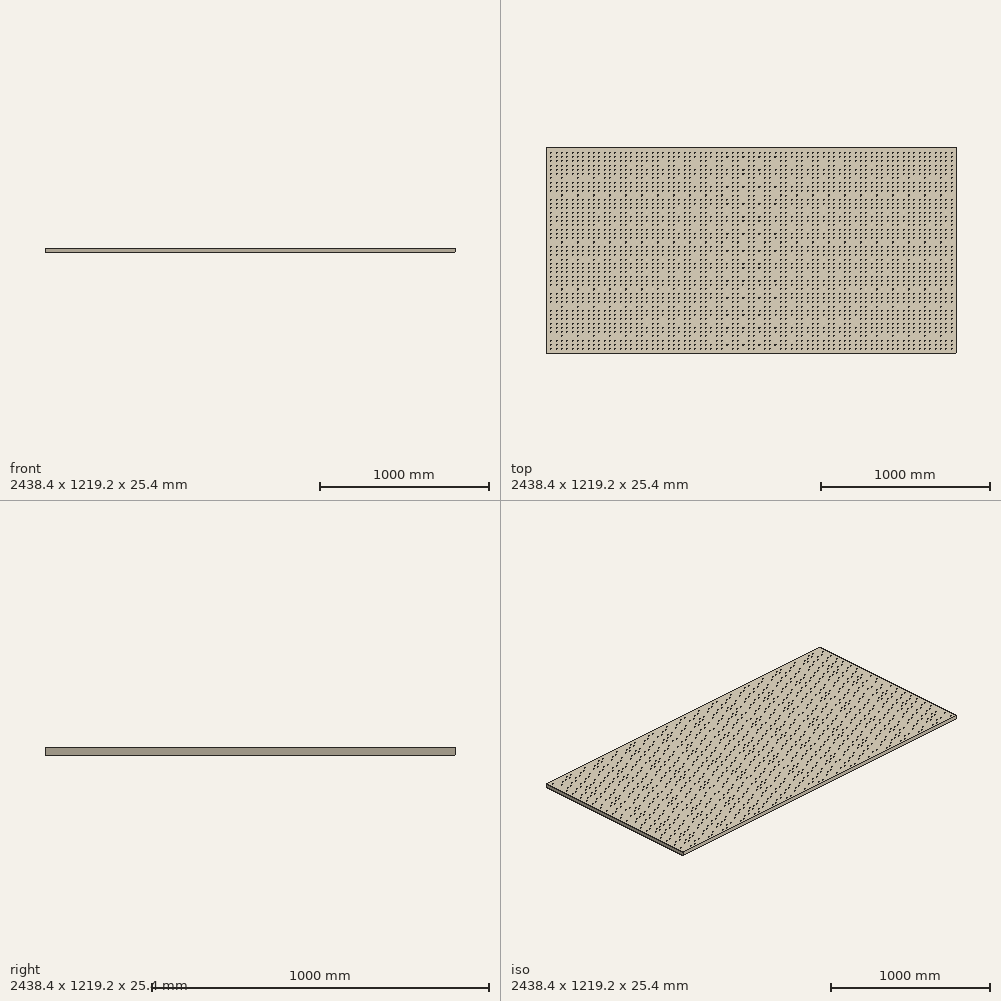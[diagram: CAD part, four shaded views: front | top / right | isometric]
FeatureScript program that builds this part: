
annotation { "Feature Type Name" : "Feature", "Feature Type Description" : "" }
export const myFeature = defineFeature(function(context is Context, id is Id, definition is map)
    precondition{}
    {
        {
            var Q0;
            Q0=qCreatedBy(makeId("Top.planeOp"),FACE);
            var sketch = newSketch(context, id + "F0", { "sketchPlane" : qUnion([Q0])});
            skLineSegment(sketch, "E0.bottom", {"start": v(-70.34, 15.58) * mm, "end": v(2368.06, 15.58) * mm});
            skLineSegment(sketch, "E0.top", {"start": v(-70.34, -1203.62) * mm, "end": v(2368.06, -1203.62) * mm});
            skLineSegment(sketch, "E0.left", {"start": v(-70.34, 15.58) * mm, "end": v(-70.34, -1203.62) * mm});
            skLineSegment(sketch, "E0.right", {"start": v(2368.06, 15.58) * mm, "end": v(2368.06, -1203.62) * mm});
            skCircle(sketch, "E1", {"center": v(-41.76, -13) * mm, "radius": 3.18 * mm});
            skCircle(sketch, "E2.1.0.0", {"center": v(-10.01, -13) * mm, "radius": 3.18 * mm});
            skCircle(sketch, "E2.2.0.0", {"center": v(21.74, -13) * mm, "radius": 3.18 * mm});
            skLineSegment(sketch, "E2.direction1", {"start": v(-41.76, -13) * mm, "end": v(-10.01, -13) * mm, "construction": true});
            skCircle(sketch, "E3.0.3.0", {"center": v(53.49, -13) * mm, "radius": 3.18 * mm});
            skCircle(sketch, "E3.0.4.0", {"center": v(85.24, -13) * mm, "radius": 3.18 * mm});
            skCircle(sketch, "E3.0.5.0", {"center": v(116.99, -13) * mm, "radius": 3.18 * mm});
            skCircle(sketch, "E3.0.6.0", {"center": v(148.74, -13) * mm, "radius": 3.18 * mm});
            skCircle(sketch, "E3.0.7.0", {"center": v(180.49, -13) * mm, "radius": 3.18 * mm});
            skCircle(sketch, "E3.0.8.0", {"center": v(212.24, -13) * mm, "radius": 3.18 * mm});
            skCircle(sketch, "E3.0.9.0", {"center": v(243.99, -13) * mm, "radius": 3.18 * mm});
            skCircle(sketch, "E3.0.10.0", {"center": v(275.74, -13) * mm, "radius": 3.18 * mm});
            skCircle(sketch, "E3.0.11.0", {"center": v(307.49, -13) * mm, "radius": 3.18 * mm});
            skCircle(sketch, "E4.0.12.0", {"center": v(339.24, -13) * mm, "radius": 3.18 * mm});
            skCircle(sketch, "E4.0.13.0", {"center": v(370.99, -13) * mm, "radius": 3.18 * mm});
            skCircle(sketch, "E4.0.14.0", {"center": v(402.74, -13) * mm, "radius": 3.18 * mm});
            skCircle(sketch, "E4.0.15.0", {"center": v(434.49, -13) * mm, "radius": 3.18 * mm});
            skCircle(sketch, "E4.0.16.0", {"center": v(466.24, -13) * mm, "radius": 3.18 * mm});
            skCircle(sketch, "E4.0.17.0", {"center": v(497.99, -13) * mm, "radius": 3.18 * mm});
            skCircle(sketch, "E4.0.18.0", {"center": v(529.74, -13) * mm, "radius": 3.18 * mm});
            skCircle(sketch, "E4.0.19.0", {"center": v(561.49, -13) * mm, "radius": 3.18 * mm});
            skCircle(sketch, "E4.0.20.0", {"center": v(593.24, -13) * mm, "radius": 3.18 * mm});
            skCircle(sketch, "E4.0.21.0", {"center": v(624.99, -13) * mm, "radius": 3.18 * mm});
            skCircle(sketch, "E4.0.22.0", {"center": v(656.74, -13) * mm, "radius": 3.18 * mm});
            skCircle(sketch, "E4.0.23.0", {"center": v(688.49, -13) * mm, "radius": 3.18 * mm});
            skCircle(sketch, "E4.0.24.0", {"center": v(720.24, -13) * mm, "radius": 3.18 * mm});
            skCircle(sketch, "E4.0.25.0", {"center": v(751.99, -13) * mm, "radius": 3.18 * mm});
            skCircle(sketch, "E4.0.26.0", {"center": v(783.74, -13) * mm, "radius": 3.18 * mm});
            skCircle(sketch, "E4.0.27.0", {"center": v(815.49, -13) * mm, "radius": 3.18 * mm});
            skCircle(sketch, "E4.0.28.0", {"center": v(847.24, -13) * mm, "radius": 3.18 * mm});
            skCircle(sketch, "E4.0.29.0", {"center": v(878.99, -13) * mm, "radius": 3.18 * mm});
            skCircle(sketch, "E4.0.30.0", {"center": v(910.74, -13) * mm, "radius": 3.18 * mm});
            skCircle(sketch, "E4.0.31.0", {"center": v(942.49, -13) * mm, "radius": 3.18 * mm});
            skCircle(sketch, "E4.0.32.0", {"center": v(974.24, -13) * mm, "radius": 3.18 * mm});
            skCircle(sketch, "E4.0.33.0", {"center": v(1005.99, -13) * mm, "radius": 3.18 * mm});
            skCircle(sketch, "E4.0.34.0", {"center": v(1037.74, -13) * mm, "radius": 3.18 * mm});
            skCircle(sketch, "E4.0.35.0", {"center": v(1069.49, -13) * mm, "radius": 3.18 * mm});
            skCircle(sketch, "E4.0.36.0", {"center": v(1101.24, -13) * mm, "radius": 3.18 * mm});
            skCircle(sketch, "E4.0.37.0", {"center": v(1132.99, -13) * mm, "radius": 3.18 * mm});
            skCircle(sketch, "E4.0.38.0", {"center": v(1164.74, -13) * mm, "radius": 3.18 * mm});
            skCircle(sketch, "E4.0.39.0", {"center": v(1196.49, -13) * mm, "radius": 3.18 * mm});
            skCircle(sketch, "E4.0.40.0", {"center": v(1228.24, -13) * mm, "radius": 3.18 * mm});
            skCircle(sketch, "E4.0.41.0", {"center": v(1259.99, -13) * mm, "radius": 3.18 * mm});
            skCircle(sketch, "E4.0.42.0", {"center": v(1291.74, -13) * mm, "radius": 3.18 * mm});
            skCircle(sketch, "E4.0.43.0", {"center": v(1323.49, -13) * mm, "radius": 3.18 * mm});
            skCircle(sketch, "E4.0.44.0", {"center": v(1355.24, -13) * mm, "radius": 3.18 * mm});
            skCircle(sketch, "E4.0.45.0", {"center": v(1386.99, -13) * mm, "radius": 3.18 * mm});
            skCircle(sketch, "E4.0.46.0", {"center": v(1418.74, -13) * mm, "radius": 3.18 * mm});
            skCircle(sketch, "E4.0.47.0", {"center": v(1450.49, -13) * mm, "radius": 3.18 * mm});
            skCircle(sketch, "E4.0.48.0", {"center": v(1482.24, -13) * mm, "radius": 3.18 * mm});
            skCircle(sketch, "E4.0.49.0", {"center": v(1513.99, -13) * mm, "radius": 3.18 * mm});
            skCircle(sketch, "E4.0.50.0", {"center": v(1545.74, -13) * mm, "radius": 3.18 * mm});
            skCircle(sketch, "E4.0.51.0", {"center": v(1577.49, -13) * mm, "radius": 3.18 * mm});
            skCircle(sketch, "E4.0.52.0", {"center": v(1609.24, -13) * mm, "radius": 3.18 * mm});
            skCircle(sketch, "E4.0.53.0", {"center": v(1640.99, -13) * mm, "radius": 3.18 * mm});
            skCircle(sketch, "E4.0.54.0", {"center": v(1672.74, -13) * mm, "radius": 3.18 * mm});
            skCircle(sketch, "E4.0.55.0", {"center": v(1704.49, -13) * mm, "radius": 3.18 * mm});
            skCircle(sketch, "E4.0.56.0", {"center": v(1736.24, -13) * mm, "radius": 3.18 * mm});
            skCircle(sketch, "E4.0.57.0", {"center": v(1767.99, -13) * mm, "radius": 3.18 * mm});
            skCircle(sketch, "E4.0.58.0", {"center": v(1799.74, -13) * mm, "radius": 3.18 * mm});
            skCircle(sketch, "E4.0.59.0", {"center": v(1831.49, -13) * mm, "radius": 3.18 * mm});
            skCircle(sketch, "E4.0.60.0", {"center": v(1863.24, -13) * mm, "radius": 3.18 * mm});
            skCircle(sketch, "E4.0.61.0", {"center": v(1894.99, -13) * mm, "radius": 3.18 * mm});
            skCircle(sketch, "E4.0.62.0", {"center": v(1926.74, -13) * mm, "radius": 3.18 * mm});
            skCircle(sketch, "E4.0.63.0", {"center": v(1958.49, -13) * mm, "radius": 3.18 * mm});
            skCircle(sketch, "E4.0.64.0", {"center": v(1990.24, -13) * mm, "radius": 3.18 * mm});
            skCircle(sketch, "E4.0.65.0", {"center": v(2021.99, -13) * mm, "radius": 3.18 * mm});
            skCircle(sketch, "E4.0.66.0", {"center": v(2053.74, -13) * mm, "radius": 3.18 * mm});
            skCircle(sketch, "E4.0.67.0", {"center": v(2085.49, -13) * mm, "radius": 3.18 * mm});
            skCircle(sketch, "E4.0.68.0", {"center": v(2117.24, -13) * mm, "radius": 3.18 * mm});
            skCircle(sketch, "E4.0.69.0", {"center": v(2148.99, -13) * mm, "radius": 3.18 * mm});
            skCircle(sketch, "E4.0.70.0", {"center": v(2180.74, -13) * mm, "radius": 3.18 * mm});
            skCircle(sketch, "E4.0.71.0", {"center": v(2212.49, -13) * mm, "radius": 3.18 * mm});
            skCircle(sketch, "E4.0.72.0", {"center": v(2244.24, -13) * mm, "radius": 3.18 * mm});
            skCircle(sketch, "E4.0.73.0", {"center": v(2275.99, -13) * mm, "radius": 3.18 * mm});
            skCircle(sketch, "E4.0.74.0", {"center": v(2307.74, -13) * mm, "radius": 3.18 * mm});
            skCircle(sketch, "E4.0.75.0", {"center": v(2339.49, -13) * mm, "radius": 3.18 * mm});
            skCircle(sketch, "E5.0.1.0", {"center": v(2244.24, -38.4) * mm, "radius": 3.18 * mm});
            skCircle(sketch, "E5.0.1.1", {"center": v(2180.74, -38.4) * mm, "radius": 3.18 * mm});
            skCircle(sketch, "E5.0.1.2", {"center": v(2339.49, -38.4) * mm, "radius": 3.18 * mm});
            skCircle(sketch, "E5.0.1.3", {"center": v(2307.74, -38.4) * mm, "radius": 3.18 * mm});
            skCircle(sketch, "E5.0.1.4", {"center": v(2275.99, -38.4) * mm, "radius": 3.18 * mm});
            skCircle(sketch, "E5.0.1.5", {"center": v(2212.49, -38.4) * mm, "radius": 3.18 * mm});
            skCircle(sketch, "E5.0.1.6", {"center": v(1958.49, -38.4) * mm, "radius": 3.18 * mm});
            skCircle(sketch, "E5.0.1.7", {"center": v(1894.99, -38.4) * mm, "radius": 3.18 * mm});
            skCircle(sketch, "E5.0.1.8", {"center": v(2117.24, -38.4) * mm, "radius": 3.18 * mm});
            skCircle(sketch, "E5.0.1.9", {"center": v(2085.49, -38.4) * mm, "radius": 3.18 * mm});
            skCircle(sketch, "E5.0.1.10", {"center": v(2053.74, -38.4) * mm, "radius": 3.18 * mm});
            skCircle(sketch, "E5.0.1.11", {"center": v(1926.74, -38.4) * mm, "radius": 3.18 * mm});
            skCircle(sketch, "E5.0.1.12", {"center": v(2021.99, -38.4) * mm, "radius": 3.18 * mm});
            skCircle(sketch, "E5.0.1.13", {"center": v(2148.99, -38.4) * mm, "radius": 3.18 * mm});
            skCircle(sketch, "E5.0.1.14", {"center": v(1990.24, -38.4) * mm, "radius": 3.18 * mm});
            skCircle(sketch, "E5.0.1.15", {"center": v(1450.49, -38.4) * mm, "radius": 3.18 * mm});
            skCircle(sketch, "E5.0.1.16", {"center": v(1228.24, -38.4) * mm, "radius": 3.18 * mm});
            skCircle(sketch, "E5.0.1.17", {"center": v(1736.24, -38.4) * mm, "radius": 3.18 * mm});
            skCircle(sketch, "E5.0.1.18", {"center": v(1386.99, -38.4) * mm, "radius": 3.18 * mm});
            skCircle(sketch, "E5.0.1.19", {"center": v(1164.74, -38.4) * mm, "radius": 3.18 * mm});
            skCircle(sketch, "E5.0.1.20", {"center": v(1672.74, -38.4) * mm, "radius": 3.18 * mm});
            skCircle(sketch, "E5.0.1.21", {"center": v(1101.24, -38.4) * mm, "radius": 3.18 * mm});
            skCircle(sketch, "E5.0.1.22", {"center": v(1609.24, -38.4) * mm, "radius": 3.18 * mm});
            skCircle(sketch, "E5.0.1.23", {"center": v(1355.24, -38.4) * mm, "radius": 3.18 * mm});
            skCircle(sketch, "E5.0.1.24", {"center": v(1863.24, -38.4) * mm, "radius": 3.18 * mm});
            skCircle(sketch, "E5.0.1.25", {"center": v(1069.49, -38.4) * mm, "radius": 3.18 * mm});
            skCircle(sketch, "E5.0.1.26", {"center": v(1577.49, -38.4) * mm, "radius": 3.18 * mm});
            skCircle(sketch, "E5.0.1.27", {"center": v(1323.49, -38.4) * mm, "radius": 3.18 * mm});
            skCircle(sketch, "E5.0.1.28", {"center": v(1831.49, -38.4) * mm, "radius": 3.18 * mm});
            skCircle(sketch, "E5.0.1.29", {"center": v(1037.74, -38.4) * mm, "radius": 3.18 * mm});
            skCircle(sketch, "E5.0.1.30", {"center": v(1545.74, -38.4) * mm, "radius": 3.18 * mm});
            skCircle(sketch, "E5.0.1.31", {"center": v(1418.74, -38.4) * mm, "radius": 3.18 * mm});
            skCircle(sketch, "E5.0.1.32", {"center": v(1005.99, -38.4) * mm, "radius": 3.18 * mm});
            skCircle(sketch, "E5.0.1.33", {"center": v(1513.99, -38.4) * mm, "radius": 3.18 * mm});
            skCircle(sketch, "E5.0.1.34", {"center": v(1799.74, -38.4) * mm, "radius": 3.18 * mm});
            skCircle(sketch, "E5.0.1.35", {"center": v(1291.74, -38.4) * mm, "radius": 3.18 * mm});
            skCircle(sketch, "E5.0.1.36", {"center": v(1132.99, -38.4) * mm, "radius": 3.18 * mm});
            skCircle(sketch, "E5.0.1.37", {"center": v(974.24, -38.4) * mm, "radius": 3.18 * mm});
            skCircle(sketch, "E5.0.1.38", {"center": v(1482.24, -38.4) * mm, "radius": 3.18 * mm});
            skCircle(sketch, "E5.0.1.39", {"center": v(1259.99, -38.4) * mm, "radius": 3.18 * mm});
            skCircle(sketch, "E5.0.1.40", {"center": v(1640.99, -38.4) * mm, "radius": 3.18 * mm});
            skCircle(sketch, "E5.0.1.41", {"center": v(1767.99, -38.4) * mm, "radius": 3.18 * mm});
            skCircle(sketch, "E5.0.1.42", {"center": v(1196.49, -38.4) * mm, "radius": 3.18 * mm});
            skCircle(sketch, "E5.0.1.43", {"center": v(1704.49, -38.4) * mm, "radius": 3.18 * mm});
            skCircle(sketch, "E5.0.1.44", {"center": v(720.24, -38.4) * mm, "radius": 3.18 * mm});
            skCircle(sketch, "E5.0.1.45", {"center": v(942.49, -38.4) * mm, "radius": 3.18 * mm});
            skCircle(sketch, "E5.0.1.46", {"center": v(878.99, -38.4) * mm, "radius": 3.18 * mm});
            skCircle(sketch, "E5.0.1.47", {"center": v(434.49, -38.4) * mm, "radius": 3.18 * mm});
            skCircle(sketch, "E5.0.1.48", {"center": v(656.74, -38.4) * mm, "radius": 3.18 * mm});
            skCircle(sketch, "E5.0.1.49", {"center": v(370.99, -38.4) * mm, "radius": 3.18 * mm});
            skCircle(sketch, "E5.0.1.50", {"center": v(593.24, -38.4) * mm, "radius": 3.18 * mm});
            skCircle(sketch, "E5.0.1.51", {"center": v(847.24, -38.4) * mm, "radius": 3.18 * mm});
            skCircle(sketch, "E5.0.1.52", {"center": v(339.24, -38.4) * mm, "radius": 3.18 * mm});
            skCircle(sketch, "E5.0.1.53", {"center": v(561.49, -38.4) * mm, "radius": 3.18 * mm});
            skCircle(sketch, "E5.0.1.54", {"center": v(815.49, -38.4) * mm, "radius": 3.18 * mm});
            skCircle(sketch, "E5.0.1.55", {"center": v(307.49, -38.4) * mm, "radius": 3.18 * mm});
            skCircle(sketch, "E5.0.1.56", {"center": v(529.74, -38.4) * mm, "radius": 3.18 * mm});
            skCircle(sketch, "E5.0.1.57", {"center": v(180.49, -38.4) * mm, "radius": 3.18 * mm});
            skCircle(sketch, "E5.0.1.58", {"center": v(148.74, -38.4) * mm, "radius": 3.18 * mm});
            skCircle(sketch, "E5.0.1.59", {"center": v(910.74, -38.4) * mm, "radius": 3.18 * mm});
            skCircle(sketch, "E5.0.1.60", {"center": v(275.74, -38.4) * mm, "radius": 3.18 * mm});
            skCircle(sketch, "E5.0.1.61", {"center": v(243.99, -38.4) * mm, "radius": 3.18 * mm});
            skCircle(sketch, "E5.0.1.62", {"center": v(212.24, -38.4) * mm, "radius": 3.18 * mm});
            skCircle(sketch, "E5.0.1.63", {"center": v(783.74, -38.4) * mm, "radius": 3.18 * mm});
            skCircle(sketch, "E5.0.1.64", {"center": v(497.99, -38.4) * mm, "radius": 3.18 * mm});
            skCircle(sketch, "E5.0.1.65", {"center": v(402.74, -38.4) * mm, "radius": 3.18 * mm});
            skCircle(sketch, "E5.0.1.66", {"center": v(624.99, -38.4) * mm, "radius": 3.18 * mm});
            skCircle(sketch, "E5.0.1.67", {"center": v(751.99, -38.4) * mm, "radius": 3.18 * mm});
            skCircle(sketch, "E5.0.1.68", {"center": v(466.24, -38.4) * mm, "radius": 3.18 * mm});
            skCircle(sketch, "E5.0.1.69", {"center": v(688.49, -38.4) * mm, "radius": 3.18 * mm});
            skCircle(sketch, "E5.0.1.70", {"center": v(116.99, -38.4) * mm, "radius": 3.18 * mm});
            skCircle(sketch, "E5.0.1.71", {"center": v(85.24, -38.4) * mm, "radius": 3.18 * mm});
            skCircle(sketch, "E5.0.1.72", {"center": v(53.49, -38.4) * mm, "radius": 3.18 * mm});
            skLineSegment(sketch, "E5.0.1.73", {"start": v(-41.76, -38.4) * mm, "end": v(-10.01, -38.4) * mm, "construction": true});
            skCircle(sketch, "E5.0.1.74", {"center": v(21.74, -38.4) * mm, "radius": 3.18 * mm});
            skCircle(sketch, "E5.0.1.75", {"center": v(-10.01, -38.4) * mm, "radius": 3.18 * mm});
            skCircle(sketch, "E5.0.1.76", {"center": v(-41.76, -38.4) * mm, "radius": 3.18 * mm});
            skCircle(sketch, "E5.0.2.0", {"center": v(2244.24, -63.8) * mm, "radius": 3.18 * mm});
            skCircle(sketch, "E5.0.2.1", {"center": v(2180.74, -63.8) * mm, "radius": 3.18 * mm});
            skCircle(sketch, "E5.0.2.2", {"center": v(2339.49, -63.8) * mm, "radius": 3.18 * mm});
            skCircle(sketch, "E5.0.2.3", {"center": v(2307.74, -63.8) * mm, "radius": 3.18 * mm});
            skCircle(sketch, "E5.0.2.4", {"center": v(2275.99, -63.8) * mm, "radius": 3.18 * mm});
            skCircle(sketch, "E5.0.2.5", {"center": v(2212.49, -63.8) * mm, "radius": 3.18 * mm});
            skCircle(sketch, "E5.0.2.6", {"center": v(1958.49, -63.8) * mm, "radius": 3.18 * mm});
            skCircle(sketch, "E5.0.2.7", {"center": v(1894.99, -63.8) * mm, "radius": 3.18 * mm});
            skCircle(sketch, "E5.0.2.8", {"center": v(2117.24, -63.8) * mm, "radius": 3.18 * mm});
            skCircle(sketch, "E5.0.2.9", {"center": v(2085.49, -63.8) * mm, "radius": 3.18 * mm});
            skCircle(sketch, "E5.0.2.10", {"center": v(2053.74, -63.8) * mm, "radius": 3.18 * mm});
            skCircle(sketch, "E5.0.2.11", {"center": v(1926.74, -63.8) * mm, "radius": 3.18 * mm});
            skCircle(sketch, "E5.0.2.12", {"center": v(2021.99, -63.8) * mm, "radius": 3.18 * mm});
            skCircle(sketch, "E5.0.2.13", {"center": v(2148.99, -63.8) * mm, "radius": 3.18 * mm});
            skCircle(sketch, "E5.0.2.14", {"center": v(1990.24, -63.8) * mm, "radius": 3.18 * mm});
            skCircle(sketch, "E5.0.2.15", {"center": v(1450.49, -63.8) * mm, "radius": 3.18 * mm});
            skCircle(sketch, "E5.0.2.16", {"center": v(1228.24, -63.8) * mm, "radius": 3.18 * mm});
            skCircle(sketch, "E5.0.2.17", {"center": v(1736.24, -63.8) * mm, "radius": 3.18 * mm});
            skCircle(sketch, "E5.0.2.18", {"center": v(1386.99, -63.8) * mm, "radius": 3.18 * mm});
            skCircle(sketch, "E5.0.2.19", {"center": v(1164.74, -63.8) * mm, "radius": 3.18 * mm});
            skCircle(sketch, "E5.0.2.20", {"center": v(1672.74, -63.8) * mm, "radius": 3.18 * mm});
            skCircle(sketch, "E5.0.2.21", {"center": v(1101.24, -63.8) * mm, "radius": 3.18 * mm});
            skCircle(sketch, "E5.0.2.22", {"center": v(1609.24, -63.8) * mm, "radius": 3.18 * mm});
            skCircle(sketch, "E5.0.2.23", {"center": v(1355.24, -63.8) * mm, "radius": 3.18 * mm});
            skCircle(sketch, "E5.0.2.24", {"center": v(1863.24, -63.8) * mm, "radius": 3.18 * mm});
            skCircle(sketch, "E5.0.2.25", {"center": v(1069.49, -63.8) * mm, "radius": 3.18 * mm});
            skCircle(sketch, "E5.0.2.26", {"center": v(1577.49, -63.8) * mm, "radius": 3.18 * mm});
            skCircle(sketch, "E5.0.2.27", {"center": v(1323.49, -63.8) * mm, "radius": 3.18 * mm});
            skCircle(sketch, "E5.0.2.28", {"center": v(1831.49, -63.8) * mm, "radius": 3.18 * mm});
            skCircle(sketch, "E5.0.2.29", {"center": v(1037.74, -63.8) * mm, "radius": 3.18 * mm});
            skCircle(sketch, "E5.0.2.30", {"center": v(1545.74, -63.8) * mm, "radius": 3.18 * mm});
            skCircle(sketch, "E5.0.2.31", {"center": v(1418.74, -63.8) * mm, "radius": 3.18 * mm});
            skCircle(sketch, "E5.0.2.32", {"center": v(1005.99, -63.8) * mm, "radius": 3.18 * mm});
            skCircle(sketch, "E5.0.2.33", {"center": v(1513.99, -63.8) * mm, "radius": 3.18 * mm});
            skCircle(sketch, "E5.0.2.34", {"center": v(1799.74, -63.8) * mm, "radius": 3.18 * mm});
            skCircle(sketch, "E5.0.2.35", {"center": v(1291.74, -63.8) * mm, "radius": 3.18 * mm});
            skCircle(sketch, "E5.0.2.36", {"center": v(1132.99, -63.8) * mm, "radius": 3.18 * mm});
            skCircle(sketch, "E5.0.2.37", {"center": v(974.24, -63.8) * mm, "radius": 3.18 * mm});
            skCircle(sketch, "E5.0.2.38", {"center": v(1482.24, -63.8) * mm, "radius": 3.18 * mm});
            skCircle(sketch, "E5.0.2.39", {"center": v(1259.99, -63.8) * mm, "radius": 3.18 * mm});
            skCircle(sketch, "E5.0.2.40", {"center": v(1640.99, -63.8) * mm, "radius": 3.18 * mm});
            skCircle(sketch, "E5.0.2.41", {"center": v(1767.99, -63.8) * mm, "radius": 3.18 * mm});
            skCircle(sketch, "E5.0.2.42", {"center": v(1196.49, -63.8) * mm, "radius": 3.18 * mm});
            skCircle(sketch, "E5.0.2.43", {"center": v(1704.49, -63.8) * mm, "radius": 3.18 * mm});
            skCircle(sketch, "E5.0.2.44", {"center": v(720.24, -63.8) * mm, "radius": 3.18 * mm});
            skCircle(sketch, "E5.0.2.45", {"center": v(942.49, -63.8) * mm, "radius": 3.18 * mm});
            skCircle(sketch, "E5.0.2.46", {"center": v(878.99, -63.8) * mm, "radius": 3.18 * mm});
            skCircle(sketch, "E5.0.2.47", {"center": v(434.49, -63.8) * mm, "radius": 3.18 * mm});
            skCircle(sketch, "E5.0.2.48", {"center": v(656.74, -63.8) * mm, "radius": 3.18 * mm});
            skCircle(sketch, "E5.0.2.49", {"center": v(370.99, -63.8) * mm, "radius": 3.18 * mm});
            skCircle(sketch, "E5.0.2.50", {"center": v(593.24, -63.8) * mm, "radius": 3.18 * mm});
            skCircle(sketch, "E5.0.2.51", {"center": v(847.24, -63.8) * mm, "radius": 3.18 * mm});
            skCircle(sketch, "E5.0.2.52", {"center": v(339.24, -63.8) * mm, "radius": 3.18 * mm});
            skCircle(sketch, "E5.0.2.53", {"center": v(561.49, -63.8) * mm, "radius": 3.18 * mm});
            skCircle(sketch, "E5.0.2.54", {"center": v(815.49, -63.8) * mm, "radius": 3.18 * mm});
            skCircle(sketch, "E5.0.2.55", {"center": v(307.49, -63.8) * mm, "radius": 3.18 * mm});
            skCircle(sketch, "E5.0.2.56", {"center": v(529.74, -63.8) * mm, "radius": 3.18 * mm});
            skCircle(sketch, "E5.0.2.57", {"center": v(180.49, -63.8) * mm, "radius": 3.18 * mm});
            skCircle(sketch, "E5.0.2.58", {"center": v(148.74, -63.8) * mm, "radius": 3.18 * mm});
            skCircle(sketch, "E5.0.2.59", {"center": v(910.74, -63.8) * mm, "radius": 3.18 * mm});
            skCircle(sketch, "E5.0.2.60", {"center": v(275.74, -63.8) * mm, "radius": 3.18 * mm});
            skCircle(sketch, "E5.0.2.61", {"center": v(243.99, -63.8) * mm, "radius": 3.18 * mm});
            skCircle(sketch, "E5.0.2.62", {"center": v(212.24, -63.8) * mm, "radius": 3.18 * mm});
            skCircle(sketch, "E5.0.2.63", {"center": v(783.74, -63.8) * mm, "radius": 3.18 * mm});
            skCircle(sketch, "E5.0.2.64", {"center": v(497.99, -63.8) * mm, "radius": 3.18 * mm});
            skCircle(sketch, "E5.0.2.65", {"center": v(402.74, -63.8) * mm, "radius": 3.18 * mm});
            skCircle(sketch, "E5.0.2.66", {"center": v(624.99, -63.8) * mm, "radius": 3.18 * mm});
            skCircle(sketch, "E5.0.2.67", {"center": v(751.99, -63.8) * mm, "radius": 3.18 * mm});
            skCircle(sketch, "E5.0.2.68", {"center": v(466.24, -63.8) * mm, "radius": 3.18 * mm});
            skCircle(sketch, "E5.0.2.69", {"center": v(688.49, -63.8) * mm, "radius": 3.18 * mm});
            skCircle(sketch, "E5.0.2.70", {"center": v(116.99, -63.8) * mm, "radius": 3.18 * mm});
            skCircle(sketch, "E5.0.2.71", {"center": v(85.24, -63.8) * mm, "radius": 3.18 * mm});
            skCircle(sketch, "E5.0.2.72", {"center": v(53.49, -63.8) * mm, "radius": 3.18 * mm});
            skLineSegment(sketch, "E5.0.2.73", {"start": v(-41.76, -63.8) * mm, "end": v(-10.01, -63.8) * mm, "construction": true});
            skCircle(sketch, "E5.0.2.74", {"center": v(21.74, -63.8) * mm, "radius": 3.18 * mm});
            skCircle(sketch, "E5.0.2.75", {"center": v(-10.01, -63.8) * mm, "radius": 3.18 * mm});
            skCircle(sketch, "E5.0.2.76", {"center": v(-41.76, -63.8) * mm, "radius": 3.18 * mm});
            skCircle(sketch, "E5.0.3.0", {"center": v(2244.24, -89.2) * mm, "radius": 3.18 * mm});
            skCircle(sketch, "E5.0.3.1", {"center": v(2180.74, -89.2) * mm, "radius": 3.18 * mm});
            skCircle(sketch, "E5.0.3.2", {"center": v(2339.49, -89.2) * mm, "radius": 3.18 * mm});
            skCircle(sketch, "E5.0.3.3", {"center": v(2307.74, -89.2) * mm, "radius": 3.18 * mm});
            skCircle(sketch, "E5.0.3.4", {"center": v(2275.99, -89.2) * mm, "radius": 3.18 * mm});
            skCircle(sketch, "E5.0.3.5", {"center": v(2212.49, -89.2) * mm, "radius": 3.18 * mm});
            skCircle(sketch, "E5.0.3.6", {"center": v(1958.49, -89.2) * mm, "radius": 3.18 * mm});
            skCircle(sketch, "E5.0.3.7", {"center": v(1894.99, -89.2) * mm, "radius": 3.18 * mm});
            skCircle(sketch, "E5.0.3.8", {"center": v(2117.24, -89.2) * mm, "radius": 3.18 * mm});
            skCircle(sketch, "E5.0.3.9", {"center": v(2085.49, -89.2) * mm, "radius": 3.18 * mm});
            skCircle(sketch, "E5.0.3.10", {"center": v(2053.74, -89.2) * mm, "radius": 3.18 * mm});
            skCircle(sketch, "E5.0.3.11", {"center": v(1926.74, -89.2) * mm, "radius": 3.18 * mm});
            skCircle(sketch, "E5.0.3.12", {"center": v(2021.99, -89.2) * mm, "radius": 3.18 * mm});
            skCircle(sketch, "E5.0.3.13", {"center": v(2148.99, -89.2) * mm, "radius": 3.18 * mm});
            skCircle(sketch, "E5.0.3.14", {"center": v(1990.24, -89.2) * mm, "radius": 3.18 * mm});
            skCircle(sketch, "E5.0.3.15", {"center": v(1450.49, -89.2) * mm, "radius": 3.18 * mm});
            skCircle(sketch, "E5.0.3.16", {"center": v(1228.24, -89.2) * mm, "radius": 3.18 * mm});
            skCircle(sketch, "E5.0.3.17", {"center": v(1736.24, -89.2) * mm, "radius": 3.18 * mm});
            skCircle(sketch, "E5.0.3.18", {"center": v(1386.99, -89.2) * mm, "radius": 3.18 * mm});
            skCircle(sketch, "E5.0.3.19", {"center": v(1164.74, -89.2) * mm, "radius": 3.18 * mm});
            skCircle(sketch, "E5.0.3.20", {"center": v(1672.74, -89.2) * mm, "radius": 3.18 * mm});
            skCircle(sketch, "E5.0.3.21", {"center": v(1101.24, -89.2) * mm, "radius": 3.18 * mm});
            skCircle(sketch, "E5.0.3.22", {"center": v(1609.24, -89.2) * mm, "radius": 3.18 * mm});
            skCircle(sketch, "E5.0.3.23", {"center": v(1355.24, -89.2) * mm, "radius": 3.18 * mm});
            skCircle(sketch, "E5.0.3.24", {"center": v(1863.24, -89.2) * mm, "radius": 3.18 * mm});
            skCircle(sketch, "E5.0.3.25", {"center": v(1069.49, -89.2) * mm, "radius": 3.18 * mm});
            skCircle(sketch, "E5.0.3.26", {"center": v(1577.49, -89.2) * mm, "radius": 3.18 * mm});
            skCircle(sketch, "E5.0.3.27", {"center": v(1323.49, -89.2) * mm, "radius": 3.18 * mm});
            skCircle(sketch, "E5.0.3.28", {"center": v(1831.49, -89.2) * mm, "radius": 3.18 * mm});
            skCircle(sketch, "E5.0.3.29", {"center": v(1037.74, -89.2) * mm, "radius": 3.18 * mm});
            skCircle(sketch, "E5.0.3.30", {"center": v(1545.74, -89.2) * mm, "radius": 3.18 * mm});
            skCircle(sketch, "E5.0.3.31", {"center": v(1418.74, -89.2) * mm, "radius": 3.18 * mm});
            skCircle(sketch, "E5.0.3.32", {"center": v(1005.99, -89.2) * mm, "radius": 3.18 * mm});
            skCircle(sketch, "E5.0.3.33", {"center": v(1513.99, -89.2) * mm, "radius": 3.18 * mm});
            skCircle(sketch, "E5.0.3.34", {"center": v(1799.74, -89.2) * mm, "radius": 3.18 * mm});
            skCircle(sketch, "E5.0.3.35", {"center": v(1291.74, -89.2) * mm, "radius": 3.18 * mm});
            skCircle(sketch, "E5.0.3.36", {"center": v(1132.99, -89.2) * mm, "radius": 3.18 * mm});
            skCircle(sketch, "E5.0.3.37", {"center": v(974.24, -89.2) * mm, "radius": 3.18 * mm});
            skCircle(sketch, "E5.0.3.38", {"center": v(1482.24, -89.2) * mm, "radius": 3.18 * mm});
            skCircle(sketch, "E5.0.3.39", {"center": v(1259.99, -89.2) * mm, "radius": 3.18 * mm});
            skCircle(sketch, "E5.0.3.40", {"center": v(1640.99, -89.2) * mm, "radius": 3.18 * mm});
            skCircle(sketch, "E5.0.3.41", {"center": v(1767.99, -89.2) * mm, "radius": 3.18 * mm});
            skCircle(sketch, "E5.0.3.42", {"center": v(1196.49, -89.2) * mm, "radius": 3.18 * mm});
            skCircle(sketch, "E5.0.3.43", {"center": v(1704.49, -89.2) * mm, "radius": 3.18 * mm});
            skCircle(sketch, "E5.0.3.44", {"center": v(720.24, -89.2) * mm, "radius": 3.18 * mm});
            skCircle(sketch, "E5.0.3.45", {"center": v(942.49, -89.2) * mm, "radius": 3.18 * mm});
            skCircle(sketch, "E5.0.3.46", {"center": v(878.99, -89.2) * mm, "radius": 3.18 * mm});
            skCircle(sketch, "E5.0.3.47", {"center": v(434.49, -89.2) * mm, "radius": 3.18 * mm});
            skCircle(sketch, "E5.0.3.48", {"center": v(656.74, -89.2) * mm, "radius": 3.18 * mm});
            skCircle(sketch, "E5.0.3.49", {"center": v(370.99, -89.2) * mm, "radius": 3.18 * mm});
            skCircle(sketch, "E5.0.3.50", {"center": v(593.24, -89.2) * mm, "radius": 3.18 * mm});
            skCircle(sketch, "E5.0.3.51", {"center": v(847.24, -89.2) * mm, "radius": 3.18 * mm});
            skCircle(sketch, "E5.0.3.52", {"center": v(339.24, -89.2) * mm, "radius": 3.18 * mm});
            skCircle(sketch, "E5.0.3.53", {"center": v(561.49, -89.2) * mm, "radius": 3.18 * mm});
            skCircle(sketch, "E5.0.3.54", {"center": v(815.49, -89.2) * mm, "radius": 3.18 * mm});
            skCircle(sketch, "E5.0.3.55", {"center": v(307.49, -89.2) * mm, "radius": 3.18 * mm});
            skCircle(sketch, "E5.0.3.56", {"center": v(529.74, -89.2) * mm, "radius": 3.18 * mm});
            skCircle(sketch, "E5.0.3.57", {"center": v(180.49, -89.2) * mm, "radius": 3.18 * mm});
            skCircle(sketch, "E5.0.3.58", {"center": v(148.74, -89.2) * mm, "radius": 3.18 * mm});
            skCircle(sketch, "E5.0.3.59", {"center": v(910.74, -89.2) * mm, "radius": 3.18 * mm});
            skCircle(sketch, "E5.0.3.60", {"center": v(275.74, -89.2) * mm, "radius": 3.18 * mm});
            skCircle(sketch, "E5.0.3.61", {"center": v(243.99, -89.2) * mm, "radius": 3.18 * mm});
            skCircle(sketch, "E5.0.3.62", {"center": v(212.24, -89.2) * mm, "radius": 3.18 * mm});
            skCircle(sketch, "E5.0.3.63", {"center": v(783.74, -89.2) * mm, "radius": 3.18 * mm});
            skCircle(sketch, "E5.0.3.64", {"center": v(497.99, -89.2) * mm, "radius": 3.18 * mm});
            skCircle(sketch, "E5.0.3.65", {"center": v(402.74, -89.2) * mm, "radius": 3.18 * mm});
            skCircle(sketch, "E5.0.3.66", {"center": v(624.99, -89.2) * mm, "radius": 3.18 * mm});
            skCircle(sketch, "E5.0.3.67", {"center": v(751.99, -89.2) * mm, "radius": 3.18 * mm});
            skCircle(sketch, "E5.0.3.68", {"center": v(466.24, -89.2) * mm, "radius": 3.18 * mm});
            skCircle(sketch, "E5.0.3.69", {"center": v(688.49, -89.2) * mm, "radius": 3.18 * mm});
            skCircle(sketch, "E5.0.3.70", {"center": v(116.99, -89.2) * mm, "radius": 3.18 * mm});
            skCircle(sketch, "E5.0.3.71", {"center": v(85.24, -89.2) * mm, "radius": 3.18 * mm});
            skCircle(sketch, "E5.0.3.72", {"center": v(53.49, -89.2) * mm, "radius": 3.18 * mm});
            skLineSegment(sketch, "E5.0.3.73", {"start": v(-41.76, -89.2) * mm, "end": v(-10.01, -89.2) * mm, "construction": true});
            skCircle(sketch, "E5.0.3.74", {"center": v(21.74, -89.2) * mm, "radius": 3.18 * mm});
            skCircle(sketch, "E5.0.3.75", {"center": v(-10.01, -89.2) * mm, "radius": 3.18 * mm});
            skCircle(sketch, "E5.0.3.76", {"center": v(-41.76, -89.2) * mm, "radius": 3.18 * mm});
            skCircle(sketch, "E5.0.4.0", {"center": v(2244.24, -114.6) * mm, "radius": 3.18 * mm});
            skCircle(sketch, "E5.0.4.1", {"center": v(2180.74, -114.6) * mm, "radius": 3.18 * mm});
            skCircle(sketch, "E5.0.4.2", {"center": v(2339.49, -114.6) * mm, "radius": 3.18 * mm});
            skCircle(sketch, "E5.0.4.3", {"center": v(2307.74, -114.6) * mm, "radius": 3.18 * mm});
            skCircle(sketch, "E5.0.4.4", {"center": v(2275.99, -114.6) * mm, "radius": 3.18 * mm});
            skCircle(sketch, "E5.0.4.5", {"center": v(2212.49, -114.6) * mm, "radius": 3.18 * mm});
            skCircle(sketch, "E5.0.4.6", {"center": v(1958.49, -114.6) * mm, "radius": 3.18 * mm});
            skCircle(sketch, "E5.0.4.7", {"center": v(1894.99, -114.6) * mm, "radius": 3.18 * mm});
            skCircle(sketch, "E5.0.4.8", {"center": v(2117.24, -114.6) * mm, "radius": 3.18 * mm});
            skCircle(sketch, "E5.0.4.9", {"center": v(2085.49, -114.6) * mm, "radius": 3.18 * mm});
            skCircle(sketch, "E5.0.4.10", {"center": v(2053.74, -114.6) * mm, "radius": 3.18 * mm});
            skCircle(sketch, "E5.0.4.11", {"center": v(1926.74, -114.6) * mm, "radius": 3.18 * mm});
            skCircle(sketch, "E5.0.4.12", {"center": v(2021.99, -114.6) * mm, "radius": 3.18 * mm});
            skCircle(sketch, "E5.0.4.13", {"center": v(2148.99, -114.6) * mm, "radius": 3.18 * mm});
            skCircle(sketch, "E5.0.4.14", {"center": v(1990.24, -114.6) * mm, "radius": 3.18 * mm});
            skCircle(sketch, "E5.0.4.15", {"center": v(1450.49, -114.6) * mm, "radius": 3.18 * mm});
            skCircle(sketch, "E5.0.4.16", {"center": v(1228.24, -114.6) * mm, "radius": 3.18 * mm});
            skCircle(sketch, "E5.0.4.17", {"center": v(1736.24, -114.6) * mm, "radius": 3.18 * mm});
            skCircle(sketch, "E5.0.4.18", {"center": v(1386.99, -114.6) * mm, "radius": 3.18 * mm});
            skCircle(sketch, "E5.0.4.19", {"center": v(1164.74, -114.6) * mm, "radius": 3.18 * mm});
            skCircle(sketch, "E5.0.4.20", {"center": v(1672.74, -114.6) * mm, "radius": 3.18 * mm});
            skCircle(sketch, "E5.0.4.21", {"center": v(1101.24, -114.6) * mm, "radius": 3.18 * mm});
            skCircle(sketch, "E5.0.4.22", {"center": v(1609.24, -114.6) * mm, "radius": 3.18 * mm});
            skCircle(sketch, "E5.0.4.23", {"center": v(1355.24, -114.6) * mm, "radius": 3.18 * mm});
            skCircle(sketch, "E5.0.4.24", {"center": v(1863.24, -114.6) * mm, "radius": 3.18 * mm});
            skCircle(sketch, "E5.0.4.25", {"center": v(1069.49, -114.6) * mm, "radius": 3.18 * mm});
            skCircle(sketch, "E5.0.4.26", {"center": v(1577.49, -114.6) * mm, "radius": 3.18 * mm});
            skCircle(sketch, "E5.0.4.27", {"center": v(1323.49, -114.6) * mm, "radius": 3.18 * mm});
            skCircle(sketch, "E5.0.4.28", {"center": v(1831.49, -114.6) * mm, "radius": 3.18 * mm});
            skCircle(sketch, "E5.0.4.29", {"center": v(1037.74, -114.6) * mm, "radius": 3.18 * mm});
            skCircle(sketch, "E5.0.4.30", {"center": v(1545.74, -114.6) * mm, "radius": 3.18 * mm});
            skCircle(sketch, "E5.0.4.31", {"center": v(1418.74, -114.6) * mm, "radius": 3.18 * mm});
            skCircle(sketch, "E5.0.4.32", {"center": v(1005.99, -114.6) * mm, "radius": 3.18 * mm});
            skCircle(sketch, "E5.0.4.33", {"center": v(1513.99, -114.6) * mm, "radius": 3.18 * mm});
            skCircle(sketch, "E5.0.4.34", {"center": v(1799.74, -114.6) * mm, "radius": 3.18 * mm});
            skCircle(sketch, "E5.0.4.35", {"center": v(1291.74, -114.6) * mm, "radius": 3.18 * mm});
            skCircle(sketch, "E5.0.4.36", {"center": v(1132.99, -114.6) * mm, "radius": 3.18 * mm});
            skCircle(sketch, "E5.0.4.37", {"center": v(974.24, -114.6) * mm, "radius": 3.18 * mm});
            skCircle(sketch, "E5.0.4.38", {"center": v(1482.24, -114.6) * mm, "radius": 3.18 * mm});
            skCircle(sketch, "E5.0.4.39", {"center": v(1259.99, -114.6) * mm, "radius": 3.18 * mm});
            skCircle(sketch, "E5.0.4.40", {"center": v(1640.99, -114.6) * mm, "radius": 3.18 * mm});
            skCircle(sketch, "E5.0.4.41", {"center": v(1767.99, -114.6) * mm, "radius": 3.18 * mm});
            skCircle(sketch, "E5.0.4.42", {"center": v(1196.49, -114.6) * mm, "radius": 3.18 * mm});
            skCircle(sketch, "E5.0.4.43", {"center": v(1704.49, -114.6) * mm, "radius": 3.18 * mm});
            skCircle(sketch, "E5.0.4.44", {"center": v(720.24, -114.6) * mm, "radius": 3.18 * mm});
            skCircle(sketch, "E5.0.4.45", {"center": v(942.49, -114.6) * mm, "radius": 3.18 * mm});
            skCircle(sketch, "E5.0.4.46", {"center": v(878.99, -114.6) * mm, "radius": 3.18 * mm});
            skCircle(sketch, "E5.0.4.47", {"center": v(434.49, -114.6) * mm, "radius": 3.18 * mm});
            skCircle(sketch, "E5.0.4.48", {"center": v(656.74, -114.6) * mm, "radius": 3.18 * mm});
            skCircle(sketch, "E5.0.4.49", {"center": v(370.99, -114.6) * mm, "radius": 3.18 * mm});
            skCircle(sketch, "E5.0.4.50", {"center": v(593.24, -114.6) * mm, "radius": 3.18 * mm});
            skCircle(sketch, "E5.0.4.51", {"center": v(847.24, -114.6) * mm, "radius": 3.18 * mm});
            skCircle(sketch, "E5.0.4.52", {"center": v(339.24, -114.6) * mm, "radius": 3.18 * mm});
            skCircle(sketch, "E5.0.4.53", {"center": v(561.49, -114.6) * mm, "radius": 3.18 * mm});
            skCircle(sketch, "E5.0.4.54", {"center": v(815.49, -114.6) * mm, "radius": 3.18 * mm});
            skCircle(sketch, "E5.0.4.55", {"center": v(307.49, -114.6) * mm, "radius": 3.18 * mm});
            skCircle(sketch, "E5.0.4.56", {"center": v(529.74, -114.6) * mm, "radius": 3.18 * mm});
            skCircle(sketch, "E5.0.4.57", {"center": v(180.49, -114.6) * mm, "radius": 3.18 * mm});
            skCircle(sketch, "E5.0.4.58", {"center": v(148.74, -114.6) * mm, "radius": 3.18 * mm});
            skCircle(sketch, "E5.0.4.59", {"center": v(910.74, -114.6) * mm, "radius": 3.18 * mm});
            skCircle(sketch, "E5.0.4.60", {"center": v(275.74, -114.6) * mm, "radius": 3.18 * mm});
            skCircle(sketch, "E5.0.4.61", {"center": v(243.99, -114.6) * mm, "radius": 3.18 * mm});
            skCircle(sketch, "E5.0.4.62", {"center": v(212.24, -114.6) * mm, "radius": 3.18 * mm});
            skCircle(sketch, "E5.0.4.63", {"center": v(783.74, -114.6) * mm, "radius": 3.18 * mm});
            skCircle(sketch, "E5.0.4.64", {"center": v(497.99, -114.6) * mm, "radius": 3.18 * mm});
            skCircle(sketch, "E5.0.4.65", {"center": v(402.74, -114.6) * mm, "radius": 3.18 * mm});
            skCircle(sketch, "E5.0.4.66", {"center": v(624.99, -114.6) * mm, "radius": 3.18 * mm});
            skCircle(sketch, "E5.0.4.67", {"center": v(751.99, -114.6) * mm, "radius": 3.18 * mm});
            skCircle(sketch, "E5.0.4.68", {"center": v(466.24, -114.6) * mm, "radius": 3.18 * mm});
            skCircle(sketch, "E5.0.4.69", {"center": v(688.49, -114.6) * mm, "radius": 3.18 * mm});
            skCircle(sketch, "E5.0.4.70", {"center": v(116.99, -114.6) * mm, "radius": 3.18 * mm});
            skCircle(sketch, "E5.0.4.71", {"center": v(85.24, -114.6) * mm, "radius": 3.18 * mm});
            skCircle(sketch, "E5.0.4.72", {"center": v(53.49, -114.6) * mm, "radius": 3.18 * mm});
            skLineSegment(sketch, "E5.0.4.73", {"start": v(-41.76, -114.6) * mm, "end": v(-10.01, -114.6) * mm, "construction": true});
            skCircle(sketch, "E5.0.4.74", {"center": v(21.74, -114.6) * mm, "radius": 3.18 * mm});
            skCircle(sketch, "E5.0.4.75", {"center": v(-10.01, -114.6) * mm, "radius": 3.18 * mm});
            skCircle(sketch, "E5.0.4.76", {"center": v(-41.76, -114.6) * mm, "radius": 3.18 * mm});
            skCircle(sketch, "E5.0.5.0", {"center": v(2244.24, -140) * mm, "radius": 3.18 * mm});
            skCircle(sketch, "E5.0.5.1", {"center": v(2180.74, -140) * mm, "radius": 3.18 * mm});
            skCircle(sketch, "E5.0.5.2", {"center": v(2339.49, -140) * mm, "radius": 3.18 * mm});
            skCircle(sketch, "E5.0.5.3", {"center": v(2307.74, -140) * mm, "radius": 3.18 * mm});
            skCircle(sketch, "E5.0.5.4", {"center": v(2275.99, -140) * mm, "radius": 3.18 * mm});
            skCircle(sketch, "E5.0.5.5", {"center": v(2212.49, -140) * mm, "radius": 3.18 * mm});
            skCircle(sketch, "E5.0.5.6", {"center": v(1958.49, -140) * mm, "radius": 3.18 * mm});
            skCircle(sketch, "E5.0.5.7", {"center": v(1894.99, -140) * mm, "radius": 3.18 * mm});
            skCircle(sketch, "E5.0.5.8", {"center": v(2117.24, -140) * mm, "radius": 3.18 * mm});
            skCircle(sketch, "E5.0.5.9", {"center": v(2085.49, -140) * mm, "radius": 3.18 * mm});
            skCircle(sketch, "E5.0.5.10", {"center": v(2053.74, -140) * mm, "radius": 3.18 * mm});
            skCircle(sketch, "E5.0.5.11", {"center": v(1926.74, -140) * mm, "radius": 3.18 * mm});
            skCircle(sketch, "E5.0.5.12", {"center": v(2021.99, -140) * mm, "radius": 3.18 * mm});
            skCircle(sketch, "E5.0.5.13", {"center": v(2148.99, -140) * mm, "radius": 3.18 * mm});
            skCircle(sketch, "E5.0.5.14", {"center": v(1990.24, -140) * mm, "radius": 3.18 * mm});
            skCircle(sketch, "E5.0.5.15", {"center": v(1450.49, -140) * mm, "radius": 3.18 * mm});
            skCircle(sketch, "E5.0.5.16", {"center": v(1228.24, -140) * mm, "radius": 3.18 * mm});
            skCircle(sketch, "E5.0.5.17", {"center": v(1736.24, -140) * mm, "radius": 3.18 * mm});
            skCircle(sketch, "E5.0.5.18", {"center": v(1386.99, -140) * mm, "radius": 3.18 * mm});
            skCircle(sketch, "E5.0.5.19", {"center": v(1164.74, -140) * mm, "radius": 3.18 * mm});
            skCircle(sketch, "E5.0.5.20", {"center": v(1672.74, -140) * mm, "radius": 3.18 * mm});
            skCircle(sketch, "E5.0.5.21", {"center": v(1101.24, -140) * mm, "radius": 3.18 * mm});
            skCircle(sketch, "E5.0.5.22", {"center": v(1609.24, -140) * mm, "radius": 3.18 * mm});
            skCircle(sketch, "E5.0.5.23", {"center": v(1355.24, -140) * mm, "radius": 3.18 * mm});
            skCircle(sketch, "E5.0.5.24", {"center": v(1863.24, -140) * mm, "radius": 3.18 * mm});
            skCircle(sketch, "E5.0.5.25", {"center": v(1069.49, -140) * mm, "radius": 3.18 * mm});
            skCircle(sketch, "E5.0.5.26", {"center": v(1577.49, -140) * mm, "radius": 3.18 * mm});
            skCircle(sketch, "E5.0.5.27", {"center": v(1323.49, -140) * mm, "radius": 3.18 * mm});
            skCircle(sketch, "E5.0.5.28", {"center": v(1831.49, -140) * mm, "radius": 3.18 * mm});
            skCircle(sketch, "E5.0.5.29", {"center": v(1037.74, -140) * mm, "radius": 3.18 * mm});
            skCircle(sketch, "E5.0.5.30", {"center": v(1545.74, -140) * mm, "radius": 3.18 * mm});
            skCircle(sketch, "E5.0.5.31", {"center": v(1418.74, -140) * mm, "radius": 3.18 * mm});
            skCircle(sketch, "E5.0.5.32", {"center": v(1005.99, -140) * mm, "radius": 3.18 * mm});
            skCircle(sketch, "E5.0.5.33", {"center": v(1513.99, -140) * mm, "radius": 3.18 * mm});
            skCircle(sketch, "E5.0.5.34", {"center": v(1799.74, -140) * mm, "radius": 3.18 * mm});
            skCircle(sketch, "E5.0.5.35", {"center": v(1291.74, -140) * mm, "radius": 3.18 * mm});
            skCircle(sketch, "E5.0.5.36", {"center": v(1132.99, -140) * mm, "radius": 3.18 * mm});
            skCircle(sketch, "E5.0.5.37", {"center": v(974.24, -140) * mm, "radius": 3.18 * mm});
            skCircle(sketch, "E5.0.5.38", {"center": v(1482.24, -140) * mm, "radius": 3.18 * mm});
            skCircle(sketch, "E5.0.5.39", {"center": v(1259.99, -140) * mm, "radius": 3.18 * mm});
            skCircle(sketch, "E5.0.5.40", {"center": v(1640.99, -140) * mm, "radius": 3.18 * mm});
            skCircle(sketch, "E5.0.5.41", {"center": v(1767.99, -140) * mm, "radius": 3.18 * mm});
            skCircle(sketch, "E5.0.5.42", {"center": v(1196.49, -140) * mm, "radius": 3.18 * mm});
            skCircle(sketch, "E5.0.5.43", {"center": v(1704.49, -140) * mm, "radius": 3.18 * mm});
            skCircle(sketch, "E5.0.5.44", {"center": v(720.24, -140) * mm, "radius": 3.18 * mm});
            skCircle(sketch, "E5.0.5.45", {"center": v(942.49, -140) * mm, "radius": 3.18 * mm});
            skCircle(sketch, "E5.0.5.46", {"center": v(878.99, -140) * mm, "radius": 3.18 * mm});
            skCircle(sketch, "E5.0.5.47", {"center": v(434.49, -140) * mm, "radius": 3.18 * mm});
            skCircle(sketch, "E5.0.5.48", {"center": v(656.74, -140) * mm, "radius": 3.18 * mm});
            skCircle(sketch, "E5.0.5.49", {"center": v(370.99, -140) * mm, "radius": 3.18 * mm});
            skCircle(sketch, "E5.0.5.50", {"center": v(593.24, -140) * mm, "radius": 3.18 * mm});
            skCircle(sketch, "E5.0.5.51", {"center": v(847.24, -140) * mm, "radius": 3.18 * mm});
            skCircle(sketch, "E5.0.5.52", {"center": v(339.24, -140) * mm, "radius": 3.18 * mm});
            skCircle(sketch, "E5.0.5.53", {"center": v(561.49, -140) * mm, "radius": 3.18 * mm});
            skCircle(sketch, "E5.0.5.54", {"center": v(815.49, -140) * mm, "radius": 3.18 * mm});
            skCircle(sketch, "E5.0.5.55", {"center": v(307.49, -140) * mm, "radius": 3.18 * mm});
            skCircle(sketch, "E5.0.5.56", {"center": v(529.74, -140) * mm, "radius": 3.18 * mm});
            skCircle(sketch, "E5.0.5.57", {"center": v(180.49, -140) * mm, "radius": 3.18 * mm});
            skCircle(sketch, "E5.0.5.58", {"center": v(148.74, -140) * mm, "radius": 3.18 * mm});
            skCircle(sketch, "E5.0.5.59", {"center": v(910.74, -140) * mm, "radius": 3.18 * mm});
            skCircle(sketch, "E5.0.5.60", {"center": v(275.74, -140) * mm, "radius": 3.18 * mm});
            skCircle(sketch, "E5.0.5.61", {"center": v(243.99, -140) * mm, "radius": 3.18 * mm});
            skCircle(sketch, "E5.0.5.62", {"center": v(212.24, -140) * mm, "radius": 3.18 * mm});
            skCircle(sketch, "E5.0.5.63", {"center": v(783.74, -140) * mm, "radius": 3.18 * mm});
            skCircle(sketch, "E5.0.5.64", {"center": v(497.99, -140) * mm, "radius": 3.18 * mm});
            skCircle(sketch, "E5.0.5.65", {"center": v(402.74, -140) * mm, "radius": 3.18 * mm});
            skCircle(sketch, "E5.0.5.66", {"center": v(624.99, -140) * mm, "radius": 3.18 * mm});
            skCircle(sketch, "E5.0.5.67", {"center": v(751.99, -140) * mm, "radius": 3.18 * mm});
            skCircle(sketch, "E5.0.5.68", {"center": v(466.24, -140) * mm, "radius": 3.18 * mm});
            skCircle(sketch, "E5.0.5.69", {"center": v(688.49, -140) * mm, "radius": 3.18 * mm});
            skCircle(sketch, "E5.0.5.70", {"center": v(116.99, -140) * mm, "radius": 3.18 * mm});
            skCircle(sketch, "E5.0.5.71", {"center": v(85.24, -140) * mm, "radius": 3.18 * mm});
            skCircle(sketch, "E5.0.5.72", {"center": v(53.49, -140) * mm, "radius": 3.18 * mm});
            skLineSegment(sketch, "E5.0.5.73", {"start": v(-41.76, -140) * mm, "end": v(-10.01, -140) * mm, "construction": true});
            skCircle(sketch, "E5.0.5.74", {"center": v(21.74, -140) * mm, "radius": 3.18 * mm});
            skCircle(sketch, "E5.0.5.75", {"center": v(-10.01, -140) * mm, "radius": 3.18 * mm});
            skCircle(sketch, "E5.0.5.76", {"center": v(-41.76, -140) * mm, "radius": 3.18 * mm});
            skCircle(sketch, "E5.0.6.0", {"center": v(2244.24, -165.4) * mm, "radius": 3.18 * mm});
            skCircle(sketch, "E5.0.6.1", {"center": v(2180.74, -165.4) * mm, "radius": 3.18 * mm});
            skCircle(sketch, "E5.0.6.2", {"center": v(2339.49, -165.4) * mm, "radius": 3.18 * mm});
            skCircle(sketch, "E5.0.6.3", {"center": v(2307.74, -165.4) * mm, "radius": 3.18 * mm});
            skCircle(sketch, "E5.0.6.4", {"center": v(2275.99, -165.4) * mm, "radius": 3.18 * mm});
            skCircle(sketch, "E5.0.6.5", {"center": v(2212.49, -165.4) * mm, "radius": 3.18 * mm});
            skCircle(sketch, "E5.0.6.6", {"center": v(1958.49, -165.4) * mm, "radius": 3.18 * mm});
            skCircle(sketch, "E5.0.6.7", {"center": v(1894.99, -165.4) * mm, "radius": 3.18 * mm});
            skCircle(sketch, "E5.0.6.8", {"center": v(2117.24, -165.4) * mm, "radius": 3.18 * mm});
            skCircle(sketch, "E5.0.6.9", {"center": v(2085.49, -165.4) * mm, "radius": 3.18 * mm});
            skCircle(sketch, "E5.0.6.10", {"center": v(2053.74, -165.4) * mm, "radius": 3.18 * mm});
            skCircle(sketch, "E5.0.6.11", {"center": v(1926.74, -165.4) * mm, "radius": 3.18 * mm});
            skCircle(sketch, "E5.0.6.12", {"center": v(2021.99, -165.4) * mm, "radius": 3.18 * mm});
            skCircle(sketch, "E5.0.6.13", {"center": v(2148.99, -165.4) * mm, "radius": 3.18 * mm});
            skCircle(sketch, "E5.0.6.14", {"center": v(1990.24, -165.4) * mm, "radius": 3.18 * mm});
            skCircle(sketch, "E5.0.6.15", {"center": v(1450.49, -165.4) * mm, "radius": 3.18 * mm});
            skCircle(sketch, "E5.0.6.16", {"center": v(1228.24, -165.4) * mm, "radius": 3.18 * mm});
            skCircle(sketch, "E5.0.6.17", {"center": v(1736.24, -165.4) * mm, "radius": 3.18 * mm});
            skCircle(sketch, "E5.0.6.18", {"center": v(1386.99, -165.4) * mm, "radius": 3.18 * mm});
            skCircle(sketch, "E5.0.6.19", {"center": v(1164.74, -165.4) * mm, "radius": 3.18 * mm});
            skCircle(sketch, "E5.0.6.20", {"center": v(1672.74, -165.4) * mm, "radius": 3.18 * mm});
            skCircle(sketch, "E5.0.6.21", {"center": v(1101.24, -165.4) * mm, "radius": 3.18 * mm});
            skCircle(sketch, "E5.0.6.22", {"center": v(1609.24, -165.4) * mm, "radius": 3.18 * mm});
            skCircle(sketch, "E5.0.6.23", {"center": v(1355.24, -165.4) * mm, "radius": 3.18 * mm});
            skCircle(sketch, "E5.0.6.24", {"center": v(1863.24, -165.4) * mm, "radius": 3.18 * mm});
            skCircle(sketch, "E5.0.6.25", {"center": v(1069.49, -165.4) * mm, "radius": 3.18 * mm});
            skCircle(sketch, "E5.0.6.26", {"center": v(1577.49, -165.4) * mm, "radius": 3.18 * mm});
            skCircle(sketch, "E5.0.6.27", {"center": v(1323.49, -165.4) * mm, "radius": 3.18 * mm});
            skCircle(sketch, "E5.0.6.28", {"center": v(1831.49, -165.4) * mm, "radius": 3.18 * mm});
            skCircle(sketch, "E5.0.6.29", {"center": v(1037.74, -165.4) * mm, "radius": 3.18 * mm});
            skCircle(sketch, "E5.0.6.30", {"center": v(1545.74, -165.4) * mm, "radius": 3.18 * mm});
            skCircle(sketch, "E5.0.6.31", {"center": v(1418.74, -165.4) * mm, "radius": 3.18 * mm});
            skCircle(sketch, "E5.0.6.32", {"center": v(1005.99, -165.4) * mm, "radius": 3.18 * mm});
            skCircle(sketch, "E5.0.6.33", {"center": v(1513.99, -165.4) * mm, "radius": 3.18 * mm});
            skCircle(sketch, "E5.0.6.34", {"center": v(1799.74, -165.4) * mm, "radius": 3.18 * mm});
            skCircle(sketch, "E5.0.6.35", {"center": v(1291.74, -165.4) * mm, "radius": 3.18 * mm});
            skCircle(sketch, "E5.0.6.36", {"center": v(1132.99, -165.4) * mm, "radius": 3.18 * mm});
            skCircle(sketch, "E5.0.6.37", {"center": v(974.24, -165.4) * mm, "radius": 3.18 * mm});
            skCircle(sketch, "E5.0.6.38", {"center": v(1482.24, -165.4) * mm, "radius": 3.18 * mm});
            skCircle(sketch, "E5.0.6.39", {"center": v(1259.99, -165.4) * mm, "radius": 3.18 * mm});
            skCircle(sketch, "E5.0.6.40", {"center": v(1640.99, -165.4) * mm, "radius": 3.18 * mm});
            skCircle(sketch, "E5.0.6.41", {"center": v(1767.99, -165.4) * mm, "radius": 3.18 * mm});
            skCircle(sketch, "E5.0.6.42", {"center": v(1196.49, -165.4) * mm, "radius": 3.18 * mm});
            skCircle(sketch, "E5.0.6.43", {"center": v(1704.49, -165.4) * mm, "radius": 3.18 * mm});
            skCircle(sketch, "E5.0.6.44", {"center": v(720.24, -165.4) * mm, "radius": 3.18 * mm});
            skCircle(sketch, "E5.0.6.45", {"center": v(942.49, -165.4) * mm, "radius": 3.18 * mm});
            skCircle(sketch, "E5.0.6.46", {"center": v(878.99, -165.4) * mm, "radius": 3.18 * mm});
            skCircle(sketch, "E5.0.6.47", {"center": v(434.49, -165.4) * mm, "radius": 3.18 * mm});
            skCircle(sketch, "E5.0.6.48", {"center": v(656.74, -165.4) * mm, "radius": 3.18 * mm});
            skCircle(sketch, "E5.0.6.49", {"center": v(370.99, -165.4) * mm, "radius": 3.18 * mm});
            skCircle(sketch, "E5.0.6.50", {"center": v(593.24, -165.4) * mm, "radius": 3.18 * mm});
            skCircle(sketch, "E5.0.6.51", {"center": v(847.24, -165.4) * mm, "radius": 3.18 * mm});
            skCircle(sketch, "E5.0.6.52", {"center": v(339.24, -165.4) * mm, "radius": 3.18 * mm});
            skCircle(sketch, "E5.0.6.53", {"center": v(561.49, -165.4) * mm, "radius": 3.18 * mm});
            skCircle(sketch, "E5.0.6.54", {"center": v(815.49, -165.4) * mm, "radius": 3.18 * mm});
            skCircle(sketch, "E5.0.6.55", {"center": v(307.49, -165.4) * mm, "radius": 3.18 * mm});
            skCircle(sketch, "E5.0.6.56", {"center": v(529.74, -165.4) * mm, "radius": 3.18 * mm});
            skCircle(sketch, "E5.0.6.57", {"center": v(180.49, -165.4) * mm, "radius": 3.18 * mm});
            skCircle(sketch, "E5.0.6.58", {"center": v(148.74, -165.4) * mm, "radius": 3.18 * mm});
            skCircle(sketch, "E5.0.6.59", {"center": v(910.74, -165.4) * mm, "radius": 3.18 * mm});
            skCircle(sketch, "E5.0.6.60", {"center": v(275.74, -165.4) * mm, "radius": 3.18 * mm});
            skCircle(sketch, "E5.0.6.61", {"center": v(243.99, -165.4) * mm, "radius": 3.18 * mm});
            skCircle(sketch, "E5.0.6.62", {"center": v(212.24, -165.4) * mm, "radius": 3.18 * mm});
            skCircle(sketch, "E5.0.6.63", {"center": v(783.74, -165.4) * mm, "radius": 3.18 * mm});
            skCircle(sketch, "E5.0.6.64", {"center": v(497.99, -165.4) * mm, "radius": 3.18 * mm});
            skCircle(sketch, "E5.0.6.65", {"center": v(402.74, -165.4) * mm, "radius": 3.18 * mm});
            skCircle(sketch, "E5.0.6.66", {"center": v(624.99, -165.4) * mm, "radius": 3.18 * mm});
            skCircle(sketch, "E5.0.6.67", {"center": v(751.99, -165.4) * mm, "radius": 3.18 * mm});
            skCircle(sketch, "E5.0.6.68", {"center": v(466.24, -165.4) * mm, "radius": 3.18 * mm});
            skCircle(sketch, "E5.0.6.69", {"center": v(688.49, -165.4) * mm, "radius": 3.18 * mm});
            skCircle(sketch, "E5.0.6.70", {"center": v(116.99, -165.4) * mm, "radius": 3.18 * mm});
            skCircle(sketch, "E5.0.6.71", {"center": v(85.24, -165.4) * mm, "radius": 3.18 * mm});
            skCircle(sketch, "E5.0.6.72", {"center": v(53.49, -165.4) * mm, "radius": 3.18 * mm});
            skLineSegment(sketch, "E5.0.6.73", {"start": v(-41.76, -165.4) * mm, "end": v(-10.01, -165.4) * mm, "construction": true});
            skCircle(sketch, "E5.0.6.74", {"center": v(21.74, -165.4) * mm, "radius": 3.18 * mm});
            skCircle(sketch, "E5.0.6.75", {"center": v(-10.01, -165.4) * mm, "radius": 3.18 * mm});
            skCircle(sketch, "E5.0.6.76", {"center": v(-41.76, -165.4) * mm, "radius": 3.18 * mm});
            skCircle(sketch, "E5.0.7.0", {"center": v(2244.24, -190.8) * mm, "radius": 3.18 * mm});
            skCircle(sketch, "E5.0.7.1", {"center": v(2180.74, -190.8) * mm, "radius": 3.18 * mm});
            skCircle(sketch, "E5.0.7.2", {"center": v(2339.49, -190.8) * mm, "radius": 3.18 * mm});
            skCircle(sketch, "E5.0.7.3", {"center": v(2307.74, -190.8) * mm, "radius": 3.18 * mm});
            skCircle(sketch, "E5.0.7.4", {"center": v(2275.99, -190.8) * mm, "radius": 3.18 * mm});
            skCircle(sketch, "E5.0.7.5", {"center": v(2212.49, -190.8) * mm, "radius": 3.18 * mm});
            skCircle(sketch, "E5.0.7.6", {"center": v(1958.49, -190.8) * mm, "radius": 3.18 * mm});
            skCircle(sketch, "E5.0.7.7", {"center": v(1894.99, -190.8) * mm, "radius": 3.18 * mm});
            skCircle(sketch, "E5.0.7.8", {"center": v(2117.24, -190.8) * mm, "radius": 3.18 * mm});
            skCircle(sketch, "E5.0.7.9", {"center": v(2085.49, -190.8) * mm, "radius": 3.18 * mm});
            skCircle(sketch, "E5.0.7.10", {"center": v(2053.74, -190.8) * mm, "radius": 3.18 * mm});
            skCircle(sketch, "E5.0.7.11", {"center": v(1926.74, -190.8) * mm, "radius": 3.18 * mm});
            skCircle(sketch, "E5.0.7.12", {"center": v(2021.99, -190.8) * mm, "radius": 3.18 * mm});
            skCircle(sketch, "E5.0.7.13", {"center": v(2148.99, -190.8) * mm, "radius": 3.18 * mm});
            skCircle(sketch, "E5.0.7.14", {"center": v(1990.24, -190.8) * mm, "radius": 3.18 * mm});
            skCircle(sketch, "E5.0.7.15", {"center": v(1450.49, -190.8) * mm, "radius": 3.18 * mm});
            skCircle(sketch, "E5.0.7.16", {"center": v(1228.24, -190.8) * mm, "radius": 3.18 * mm});
            skCircle(sketch, "E5.0.7.17", {"center": v(1736.24, -190.8) * mm, "radius": 3.18 * mm});
            skCircle(sketch, "E5.0.7.18", {"center": v(1386.99, -190.8) * mm, "radius": 3.18 * mm});
            skCircle(sketch, "E5.0.7.19", {"center": v(1164.74, -190.8) * mm, "radius": 3.18 * mm});
            skCircle(sketch, "E5.0.7.20", {"center": v(1672.74, -190.8) * mm, "radius": 3.18 * mm});
            skCircle(sketch, "E5.0.7.21", {"center": v(1101.24, -190.8) * mm, "radius": 3.18 * mm});
            skCircle(sketch, "E5.0.7.22", {"center": v(1609.24, -190.8) * mm, "radius": 3.18 * mm});
            skCircle(sketch, "E5.0.7.23", {"center": v(1355.24, -190.8) * mm, "radius": 3.18 * mm});
            skCircle(sketch, "E5.0.7.24", {"center": v(1863.24, -190.8) * mm, "radius": 3.18 * mm});
            skCircle(sketch, "E5.0.7.25", {"center": v(1069.49, -190.8) * mm, "radius": 3.18 * mm});
            skCircle(sketch, "E5.0.7.26", {"center": v(1577.49, -190.8) * mm, "radius": 3.18 * mm});
            skCircle(sketch, "E5.0.7.27", {"center": v(1323.49, -190.8) * mm, "radius": 3.18 * mm});
            skCircle(sketch, "E5.0.7.28", {"center": v(1831.49, -190.8) * mm, "radius": 3.18 * mm});
            skCircle(sketch, "E5.0.7.29", {"center": v(1037.74, -190.8) * mm, "radius": 3.18 * mm});
            skCircle(sketch, "E5.0.7.30", {"center": v(1545.74, -190.8) * mm, "radius": 3.18 * mm});
            skCircle(sketch, "E5.0.7.31", {"center": v(1418.74, -190.8) * mm, "radius": 3.18 * mm});
            skCircle(sketch, "E5.0.7.32", {"center": v(1005.99, -190.8) * mm, "radius": 3.18 * mm});
            skCircle(sketch, "E5.0.7.33", {"center": v(1513.99, -190.8) * mm, "radius": 3.18 * mm});
            skCircle(sketch, "E5.0.7.34", {"center": v(1799.74, -190.8) * mm, "radius": 3.18 * mm});
            skCircle(sketch, "E5.0.7.35", {"center": v(1291.74, -190.8) * mm, "radius": 3.18 * mm});
            skCircle(sketch, "E5.0.7.36", {"center": v(1132.99, -190.8) * mm, "radius": 3.18 * mm});
            skCircle(sketch, "E5.0.7.37", {"center": v(974.24, -190.8) * mm, "radius": 3.18 * mm});
            skCircle(sketch, "E5.0.7.38", {"center": v(1482.24, -190.8) * mm, "radius": 3.18 * mm});
            skCircle(sketch, "E5.0.7.39", {"center": v(1259.99, -190.8) * mm, "radius": 3.18 * mm});
            skCircle(sketch, "E5.0.7.40", {"center": v(1640.99, -190.8) * mm, "radius": 3.18 * mm});
            skCircle(sketch, "E5.0.7.41", {"center": v(1767.99, -190.8) * mm, "radius": 3.18 * mm});
            skCircle(sketch, "E5.0.7.42", {"center": v(1196.49, -190.8) * mm, "radius": 3.18 * mm});
            skCircle(sketch, "E5.0.7.43", {"center": v(1704.49, -190.8) * mm, "radius": 3.18 * mm});
            skCircle(sketch, "E5.0.7.44", {"center": v(720.24, -190.8) * mm, "radius": 3.18 * mm});
            skCircle(sketch, "E5.0.7.45", {"center": v(942.49, -190.8) * mm, "radius": 3.18 * mm});
            skCircle(sketch, "E5.0.7.46", {"center": v(878.99, -190.8) * mm, "radius": 3.18 * mm});
            skCircle(sketch, "E5.0.7.47", {"center": v(434.49, -190.8) * mm, "radius": 3.18 * mm});
            skCircle(sketch, "E5.0.7.48", {"center": v(656.74, -190.8) * mm, "radius": 3.18 * mm});
            skCircle(sketch, "E5.0.7.49", {"center": v(370.99, -190.8) * mm, "radius": 3.18 * mm});
            skCircle(sketch, "E5.0.7.50", {"center": v(593.24, -190.8) * mm, "radius": 3.18 * mm});
            skCircle(sketch, "E5.0.7.51", {"center": v(847.24, -190.8) * mm, "radius": 3.18 * mm});
            skCircle(sketch, "E5.0.7.52", {"center": v(339.24, -190.8) * mm, "radius": 3.18 * mm});
            skCircle(sketch, "E5.0.7.53", {"center": v(561.49, -190.8) * mm, "radius": 3.18 * mm});
            skCircle(sketch, "E5.0.7.54", {"center": v(815.49, -190.8) * mm, "radius": 3.18 * mm});
            skCircle(sketch, "E5.0.7.55", {"center": v(307.49, -190.8) * mm, "radius": 3.18 * mm});
            skCircle(sketch, "E5.0.7.56", {"center": v(529.74, -190.8) * mm, "radius": 3.18 * mm});
            skCircle(sketch, "E5.0.7.57", {"center": v(180.49, -190.8) * mm, "radius": 3.18 * mm});
            skCircle(sketch, "E5.0.7.58", {"center": v(148.74, -190.8) * mm, "radius": 3.18 * mm});
            skCircle(sketch, "E5.0.7.59", {"center": v(910.74, -190.8) * mm, "radius": 3.18 * mm});
            skCircle(sketch, "E5.0.7.60", {"center": v(275.74, -190.8) * mm, "radius": 3.18 * mm});
            skCircle(sketch, "E5.0.7.61", {"center": v(243.99, -190.8) * mm, "radius": 3.18 * mm});
            skCircle(sketch, "E5.0.7.62", {"center": v(212.24, -190.8) * mm, "radius": 3.18 * mm});
            skCircle(sketch, "E5.0.7.63", {"center": v(783.74, -190.8) * mm, "radius": 3.18 * mm});
            skCircle(sketch, "E5.0.7.64", {"center": v(497.99, -190.8) * mm, "radius": 3.18 * mm});
            skCircle(sketch, "E5.0.7.65", {"center": v(402.74, -190.8) * mm, "radius": 3.18 * mm});
            skCircle(sketch, "E5.0.7.66", {"center": v(624.99, -190.8) * mm, "radius": 3.18 * mm});
            skCircle(sketch, "E5.0.7.67", {"center": v(751.99, -190.8) * mm, "radius": 3.18 * mm});
            skCircle(sketch, "E5.0.7.68", {"center": v(466.24, -190.8) * mm, "radius": 3.18 * mm});
            skCircle(sketch, "E5.0.7.69", {"center": v(688.49, -190.8) * mm, "radius": 3.18 * mm});
            skCircle(sketch, "E5.0.7.70", {"center": v(116.99, -190.8) * mm, "radius": 3.18 * mm});
            skCircle(sketch, "E5.0.7.71", {"center": v(85.24, -190.8) * mm, "radius": 3.18 * mm});
            skCircle(sketch, "E5.0.7.72", {"center": v(53.49, -190.8) * mm, "radius": 3.18 * mm});
            skLineSegment(sketch, "E5.0.7.73", {"start": v(-41.76, -190.8) * mm, "end": v(-10.01, -190.8) * mm, "construction": true});
            skCircle(sketch, "E5.0.7.74", {"center": v(21.74, -190.8) * mm, "radius": 3.18 * mm});
            skCircle(sketch, "E5.0.7.75", {"center": v(-10.01, -190.8) * mm, "radius": 3.18 * mm});
            skCircle(sketch, "E5.0.7.76", {"center": v(-41.76, -190.8) * mm, "radius": 3.18 * mm});
            skCircle(sketch, "E5.0.8.0", {"center": v(2244.24, -216.2) * mm, "radius": 3.18 * mm});
            skCircle(sketch, "E5.0.8.1", {"center": v(2180.74, -216.2) * mm, "radius": 3.18 * mm});
            skCircle(sketch, "E5.0.8.2", {"center": v(2339.49, -216.2) * mm, "radius": 3.18 * mm});
            skCircle(sketch, "E5.0.8.3", {"center": v(2307.74, -216.2) * mm, "radius": 3.18 * mm});
            skCircle(sketch, "E5.0.8.4", {"center": v(2275.99, -216.2) * mm, "radius": 3.18 * mm});
            skCircle(sketch, "E5.0.8.5", {"center": v(2212.49, -216.2) * mm, "radius": 3.18 * mm});
            skCircle(sketch, "E5.0.8.6", {"center": v(1958.49, -216.2) * mm, "radius": 3.18 * mm});
            skCircle(sketch, "E5.0.8.7", {"center": v(1894.99, -216.2) * mm, "radius": 3.18 * mm});
            skCircle(sketch, "E5.0.8.8", {"center": v(2117.24, -216.2) * mm, "radius": 3.18 * mm});
            skCircle(sketch, "E5.0.8.9", {"center": v(2085.49, -216.2) * mm, "radius": 3.18 * mm});
            skCircle(sketch, "E5.0.8.10", {"center": v(2053.74, -216.2) * mm, "radius": 3.18 * mm});
            skCircle(sketch, "E5.0.8.11", {"center": v(1926.74, -216.2) * mm, "radius": 3.18 * mm});
            skCircle(sketch, "E5.0.8.12", {"center": v(2021.99, -216.2) * mm, "radius": 3.18 * mm});
            skCircle(sketch, "E5.0.8.13", {"center": v(2148.99, -216.2) * mm, "radius": 3.18 * mm});
            skCircle(sketch, "E5.0.8.14", {"center": v(1990.24, -216.2) * mm, "radius": 3.18 * mm});
            skCircle(sketch, "E5.0.8.15", {"center": v(1450.49, -216.2) * mm, "radius": 3.18 * mm});
            skCircle(sketch, "E5.0.8.16", {"center": v(1228.24, -216.2) * mm, "radius": 3.18 * mm});
            skCircle(sketch, "E5.0.8.17", {"center": v(1736.24, -216.2) * mm, "radius": 3.18 * mm});
            skCircle(sketch, "E5.0.8.18", {"center": v(1386.99, -216.2) * mm, "radius": 3.18 * mm});
            skCircle(sketch, "E5.0.8.19", {"center": v(1164.74, -216.2) * mm, "radius": 3.18 * mm});
            skCircle(sketch, "E5.0.8.20", {"center": v(1672.74, -216.2) * mm, "radius": 3.18 * mm});
            skCircle(sketch, "E5.0.8.21", {"center": v(1101.24, -216.2) * mm, "radius": 3.18 * mm});
            skCircle(sketch, "E5.0.8.22", {"center": v(1609.24, -216.2) * mm, "radius": 3.18 * mm});
            skCircle(sketch, "E5.0.8.23", {"center": v(1355.24, -216.2) * mm, "radius": 3.18 * mm});
            skCircle(sketch, "E5.0.8.24", {"center": v(1863.24, -216.2) * mm, "radius": 3.18 * mm});
            skCircle(sketch, "E5.0.8.25", {"center": v(1069.49, -216.2) * mm, "radius": 3.18 * mm});
            skCircle(sketch, "E5.0.8.26", {"center": v(1577.49, -216.2) * mm, "radius": 3.18 * mm});
            skCircle(sketch, "E5.0.8.27", {"center": v(1323.49, -216.2) * mm, "radius": 3.18 * mm});
            skCircle(sketch, "E5.0.8.28", {"center": v(1831.49, -216.2) * mm, "radius": 3.18 * mm});
            skCircle(sketch, "E5.0.8.29", {"center": v(1037.74, -216.2) * mm, "radius": 3.18 * mm});
            skCircle(sketch, "E5.0.8.30", {"center": v(1545.74, -216.2) * mm, "radius": 3.18 * mm});
            skCircle(sketch, "E5.0.8.31", {"center": v(1418.74, -216.2) * mm, "radius": 3.18 * mm});
            skCircle(sketch, "E5.0.8.32", {"center": v(1005.99, -216.2) * mm, "radius": 3.18 * mm});
            skCircle(sketch, "E5.0.8.33", {"center": v(1513.99, -216.2) * mm, "radius": 3.18 * mm});
            skCircle(sketch, "E5.0.8.34", {"center": v(1799.74, -216.2) * mm, "radius": 3.18 * mm});
            skCircle(sketch, "E5.0.8.35", {"center": v(1291.74, -216.2) * mm, "radius": 3.18 * mm});
            skCircle(sketch, "E5.0.8.36", {"center": v(1132.99, -216.2) * mm, "radius": 3.18 * mm});
            skCircle(sketch, "E5.0.8.37", {"center": v(974.24, -216.2) * mm, "radius": 3.18 * mm});
            skCircle(sketch, "E5.0.8.38", {"center": v(1482.24, -216.2) * mm, "radius": 3.18 * mm});
            skCircle(sketch, "E5.0.8.39", {"center": v(1259.99, -216.2) * mm, "radius": 3.18 * mm});
            skCircle(sketch, "E5.0.8.40", {"center": v(1640.99, -216.2) * mm, "radius": 3.18 * mm});
            skCircle(sketch, "E5.0.8.41", {"center": v(1767.99, -216.2) * mm, "radius": 3.18 * mm});
            skCircle(sketch, "E5.0.8.42", {"center": v(1196.49, -216.2) * mm, "radius": 3.18 * mm});
            skCircle(sketch, "E5.0.8.43", {"center": v(1704.49, -216.2) * mm, "radius": 3.18 * mm});
            skCircle(sketch, "E5.0.8.44", {"center": v(720.24, -216.2) * mm, "radius": 3.18 * mm});
            skCircle(sketch, "E5.0.8.45", {"center": v(942.49, -216.2) * mm, "radius": 3.18 * mm});
            skCircle(sketch, "E5.0.8.46", {"center": v(878.99, -216.2) * mm, "radius": 3.18 * mm});
            skCircle(sketch, "E5.0.8.47", {"center": v(434.49, -216.2) * mm, "radius": 3.18 * mm});
            skCircle(sketch, "E5.0.8.48", {"center": v(656.74, -216.2) * mm, "radius": 3.18 * mm});
            skCircle(sketch, "E5.0.8.49", {"center": v(370.99, -216.2) * mm, "radius": 3.18 * mm});
            skCircle(sketch, "E5.0.8.50", {"center": v(593.24, -216.2) * mm, "radius": 3.18 * mm});
            skCircle(sketch, "E5.0.8.51", {"center": v(847.24, -216.2) * mm, "radius": 3.18 * mm});
            skCircle(sketch, "E5.0.8.52", {"center": v(339.24, -216.2) * mm, "radius": 3.18 * mm});
            skCircle(sketch, "E5.0.8.53", {"center": v(561.49, -216.2) * mm, "radius": 3.18 * mm});
            skCircle(sketch, "E5.0.8.54", {"center": v(815.49, -216.2) * mm, "radius": 3.18 * mm});
            skCircle(sketch, "E5.0.8.55", {"center": v(307.49, -216.2) * mm, "radius": 3.18 * mm});
            skCircle(sketch, "E5.0.8.56", {"center": v(529.74, -216.2) * mm, "radius": 3.18 * mm});
            skCircle(sketch, "E5.0.8.57", {"center": v(180.49, -216.2) * mm, "radius": 3.18 * mm});
            skCircle(sketch, "E5.0.8.58", {"center": v(148.74, -216.2) * mm, "radius": 3.18 * mm});
            skCircle(sketch, "E5.0.8.59", {"center": v(910.74, -216.2) * mm, "radius": 3.18 * mm});
            skCircle(sketch, "E5.0.8.60", {"center": v(275.74, -216.2) * mm, "radius": 3.18 * mm});
            skCircle(sketch, "E5.0.8.61", {"center": v(243.99, -216.2) * mm, "radius": 3.18 * mm});
            skCircle(sketch, "E5.0.8.62", {"center": v(212.24, -216.2) * mm, "radius": 3.18 * mm});
            skCircle(sketch, "E5.0.8.63", {"center": v(783.74, -216.2) * mm, "radius": 3.18 * mm});
            skCircle(sketch, "E5.0.8.64", {"center": v(497.99, -216.2) * mm, "radius": 3.18 * mm});
            skCircle(sketch, "E5.0.8.65", {"center": v(402.74, -216.2) * mm, "radius": 3.18 * mm});
            skCircle(sketch, "E5.0.8.66", {"center": v(624.99, -216.2) * mm, "radius": 3.18 * mm});
            skCircle(sketch, "E5.0.8.67", {"center": v(751.99, -216.2) * mm, "radius": 3.18 * mm});
            skCircle(sketch, "E5.0.8.68", {"center": v(466.24, -216.2) * mm, "radius": 3.18 * mm});
            skCircle(sketch, "E5.0.8.69", {"center": v(688.49, -216.2) * mm, "radius": 3.18 * mm});
            skCircle(sketch, "E5.0.8.70", {"center": v(116.99, -216.2) * mm, "radius": 3.18 * mm});
            skCircle(sketch, "E5.0.8.71", {"center": v(85.24, -216.2) * mm, "radius": 3.18 * mm});
            skCircle(sketch, "E5.0.8.72", {"center": v(53.49, -216.2) * mm, "radius": 3.18 * mm});
            skLineSegment(sketch, "E5.0.8.73", {"start": v(-41.76, -216.2) * mm, "end": v(-10.01, -216.2) * mm, "construction": true});
            skCircle(sketch, "E5.0.8.74", {"center": v(21.74, -216.2) * mm, "radius": 3.18 * mm});
            skCircle(sketch, "E5.0.8.75", {"center": v(-10.01, -216.2) * mm, "radius": 3.18 * mm});
            skCircle(sketch, "E5.0.8.76", {"center": v(-41.76, -216.2) * mm, "radius": 3.18 * mm});
            skCircle(sketch, "E5.0.9.0", {"center": v(2244.24, -241.6) * mm, "radius": 3.18 * mm});
            skCircle(sketch, "E5.0.9.1", {"center": v(2180.74, -241.6) * mm, "radius": 3.18 * mm});
            skCircle(sketch, "E5.0.9.2", {"center": v(2339.49, -241.6) * mm, "radius": 3.18 * mm});
            skCircle(sketch, "E5.0.9.3", {"center": v(2307.74, -241.6) * mm, "radius": 3.18 * mm});
            skCircle(sketch, "E5.0.9.4", {"center": v(2275.99, -241.6) * mm, "radius": 3.18 * mm});
            skCircle(sketch, "E5.0.9.5", {"center": v(2212.49, -241.6) * mm, "radius": 3.18 * mm});
            skCircle(sketch, "E5.0.9.6", {"center": v(1958.49, -241.6) * mm, "radius": 3.18 * mm});
            skCircle(sketch, "E5.0.9.7", {"center": v(1894.99, -241.6) * mm, "radius": 3.18 * mm});
            skCircle(sketch, "E5.0.9.8", {"center": v(2117.24, -241.6) * mm, "radius": 3.18 * mm});
            skCircle(sketch, "E5.0.9.9", {"center": v(2085.49, -241.6) * mm, "radius": 3.18 * mm});
            skCircle(sketch, "E5.0.9.10", {"center": v(2053.74, -241.6) * mm, "radius": 3.18 * mm});
            skCircle(sketch, "E5.0.9.11", {"center": v(1926.74, -241.6) * mm, "radius": 3.18 * mm});
            skCircle(sketch, "E5.0.9.12", {"center": v(2021.99, -241.6) * mm, "radius": 3.18 * mm});
            skCircle(sketch, "E5.0.9.13", {"center": v(2148.99, -241.6) * mm, "radius": 3.18 * mm});
            skCircle(sketch, "E5.0.9.14", {"center": v(1990.24, -241.6) * mm, "radius": 3.18 * mm});
            skCircle(sketch, "E5.0.9.15", {"center": v(1450.49, -241.6) * mm, "radius": 3.18 * mm});
            skCircle(sketch, "E5.0.9.16", {"center": v(1228.24, -241.6) * mm, "radius": 3.18 * mm});
            skCircle(sketch, "E5.0.9.17", {"center": v(1736.24, -241.6) * mm, "radius": 3.18 * mm});
            skCircle(sketch, "E5.0.9.18", {"center": v(1386.99, -241.6) * mm, "radius": 3.18 * mm});
            skCircle(sketch, "E5.0.9.19", {"center": v(1164.74, -241.6) * mm, "radius": 3.18 * mm});
            skCircle(sketch, "E5.0.9.20", {"center": v(1672.74, -241.6) * mm, "radius": 3.18 * mm});
            skCircle(sketch, "E5.0.9.21", {"center": v(1101.24, -241.6) * mm, "radius": 3.18 * mm});
            skCircle(sketch, "E5.0.9.22", {"center": v(1609.24, -241.6) * mm, "radius": 3.18 * mm});
            skCircle(sketch, "E5.0.9.23", {"center": v(1355.24, -241.6) * mm, "radius": 3.18 * mm});
            skCircle(sketch, "E5.0.9.24", {"center": v(1863.24, -241.6) * mm, "radius": 3.18 * mm});
            skCircle(sketch, "E5.0.9.25", {"center": v(1069.49, -241.6) * mm, "radius": 3.18 * mm});
            skCircle(sketch, "E5.0.9.26", {"center": v(1577.49, -241.6) * mm, "radius": 3.18 * mm});
            skCircle(sketch, "E5.0.9.27", {"center": v(1323.49, -241.6) * mm, "radius": 3.18 * mm});
            skCircle(sketch, "E5.0.9.28", {"center": v(1831.49, -241.6) * mm, "radius": 3.18 * mm});
            skCircle(sketch, "E5.0.9.29", {"center": v(1037.74, -241.6) * mm, "radius": 3.18 * mm});
            skCircle(sketch, "E5.0.9.30", {"center": v(1545.74, -241.6) * mm, "radius": 3.18 * mm});
            skCircle(sketch, "E5.0.9.31", {"center": v(1418.74, -241.6) * mm, "radius": 3.18 * mm});
            skCircle(sketch, "E5.0.9.32", {"center": v(1005.99, -241.6) * mm, "radius": 3.18 * mm});
            skCircle(sketch, "E5.0.9.33", {"center": v(1513.99, -241.6) * mm, "radius": 3.18 * mm});
            skCircle(sketch, "E5.0.9.34", {"center": v(1799.74, -241.6) * mm, "radius": 3.18 * mm});
            skCircle(sketch, "E5.0.9.35", {"center": v(1291.74, -241.6) * mm, "radius": 3.18 * mm});
            skCircle(sketch, "E5.0.9.36", {"center": v(1132.99, -241.6) * mm, "radius": 3.18 * mm});
            skCircle(sketch, "E5.0.9.37", {"center": v(974.24, -241.6) * mm, "radius": 3.18 * mm});
            skCircle(sketch, "E5.0.9.38", {"center": v(1482.24, -241.6) * mm, "radius": 3.18 * mm});
            skCircle(sketch, "E5.0.9.39", {"center": v(1259.99, -241.6) * mm, "radius": 3.18 * mm});
            skCircle(sketch, "E5.0.9.40", {"center": v(1640.99, -241.6) * mm, "radius": 3.18 * mm});
            skCircle(sketch, "E5.0.9.41", {"center": v(1767.99, -241.6) * mm, "radius": 3.18 * mm});
            skCircle(sketch, "E5.0.9.42", {"center": v(1196.49, -241.6) * mm, "radius": 3.18 * mm});
            skCircle(sketch, "E5.0.9.43", {"center": v(1704.49, -241.6) * mm, "radius": 3.18 * mm});
            skCircle(sketch, "E5.0.9.44", {"center": v(720.24, -241.6) * mm, "radius": 3.18 * mm});
            skCircle(sketch, "E5.0.9.45", {"center": v(942.49, -241.6) * mm, "radius": 3.18 * mm});
            skCircle(sketch, "E5.0.9.46", {"center": v(878.99, -241.6) * mm, "radius": 3.18 * mm});
            skCircle(sketch, "E5.0.9.47", {"center": v(434.49, -241.6) * mm, "radius": 3.18 * mm});
            skCircle(sketch, "E5.0.9.48", {"center": v(656.74, -241.6) * mm, "radius": 3.18 * mm});
            skCircle(sketch, "E5.0.9.49", {"center": v(370.99, -241.6) * mm, "radius": 3.18 * mm});
            skCircle(sketch, "E5.0.9.50", {"center": v(593.24, -241.6) * mm, "radius": 3.18 * mm});
            skCircle(sketch, "E5.0.9.51", {"center": v(847.24, -241.6) * mm, "radius": 3.18 * mm});
            skCircle(sketch, "E5.0.9.52", {"center": v(339.24, -241.6) * mm, "radius": 3.18 * mm});
            skCircle(sketch, "E5.0.9.53", {"center": v(561.49, -241.6) * mm, "radius": 3.18 * mm});
            skCircle(sketch, "E5.0.9.54", {"center": v(815.49, -241.6) * mm, "radius": 3.18 * mm});
            skCircle(sketch, "E5.0.9.55", {"center": v(307.49, -241.6) * mm, "radius": 3.18 * mm});
            skCircle(sketch, "E5.0.9.56", {"center": v(529.74, -241.6) * mm, "radius": 3.18 * mm});
            skCircle(sketch, "E5.0.9.57", {"center": v(180.49, -241.6) * mm, "radius": 3.18 * mm});
            skCircle(sketch, "E5.0.9.58", {"center": v(148.74, -241.6) * mm, "radius": 3.18 * mm});
            skCircle(sketch, "E5.0.9.59", {"center": v(910.74, -241.6) * mm, "radius": 3.18 * mm});
            skCircle(sketch, "E5.0.9.60", {"center": v(275.74, -241.6) * mm, "radius": 3.18 * mm});
            skCircle(sketch, "E5.0.9.61", {"center": v(243.99, -241.6) * mm, "radius": 3.18 * mm});
            skCircle(sketch, "E5.0.9.62", {"center": v(212.24, -241.6) * mm, "radius": 3.18 * mm});
            skCircle(sketch, "E5.0.9.63", {"center": v(783.74, -241.6) * mm, "radius": 3.18 * mm});
            skCircle(sketch, "E5.0.9.64", {"center": v(497.99, -241.6) * mm, "radius": 3.18 * mm});
            skCircle(sketch, "E5.0.9.65", {"center": v(402.74, -241.6) * mm, "radius": 3.18 * mm});
            skCircle(sketch, "E5.0.9.66", {"center": v(624.99, -241.6) * mm, "radius": 3.18 * mm});
            skCircle(sketch, "E5.0.9.67", {"center": v(751.99, -241.6) * mm, "radius": 3.18 * mm});
            skCircle(sketch, "E5.0.9.68", {"center": v(466.24, -241.6) * mm, "radius": 3.18 * mm});
            skCircle(sketch, "E5.0.9.69", {"center": v(688.49, -241.6) * mm, "radius": 3.18 * mm});
            skCircle(sketch, "E5.0.9.70", {"center": v(116.99, -241.6) * mm, "radius": 3.18 * mm});
            skCircle(sketch, "E5.0.9.71", {"center": v(85.24, -241.6) * mm, "radius": 3.18 * mm});
            skCircle(sketch, "E5.0.9.72", {"center": v(53.49, -241.6) * mm, "radius": 3.18 * mm});
            skLineSegment(sketch, "E5.0.9.73", {"start": v(-41.76, -241.6) * mm, "end": v(-10.01, -241.6) * mm, "construction": true});
            skCircle(sketch, "E5.0.9.74", {"center": v(21.74, -241.6) * mm, "radius": 3.18 * mm});
            skCircle(sketch, "E5.0.9.75", {"center": v(-10.01, -241.6) * mm, "radius": 3.18 * mm});
            skCircle(sketch, "E5.0.9.76", {"center": v(-41.76, -241.6) * mm, "radius": 3.18 * mm});
            skCircle(sketch, "E5.0.10.0", {"center": v(2244.24, -267) * mm, "radius": 3.18 * mm});
            skCircle(sketch, "E5.0.10.1", {"center": v(2180.74, -267) * mm, "radius": 3.18 * mm});
            skCircle(sketch, "E5.0.10.2", {"center": v(2339.49, -267) * mm, "radius": 3.18 * mm});
            skCircle(sketch, "E5.0.10.3", {"center": v(2307.74, -267) * mm, "radius": 3.18 * mm});
            skCircle(sketch, "E5.0.10.4", {"center": v(2275.99, -267) * mm, "radius": 3.18 * mm});
            skCircle(sketch, "E5.0.10.5", {"center": v(2212.49, -267) * mm, "radius": 3.18 * mm});
            skCircle(sketch, "E5.0.10.6", {"center": v(1958.49, -267) * mm, "radius": 3.18 * mm});
            skCircle(sketch, "E5.0.10.7", {"center": v(1894.99, -267) * mm, "radius": 3.18 * mm});
            skCircle(sketch, "E5.0.10.8", {"center": v(2117.24, -267) * mm, "radius": 3.18 * mm});
            skCircle(sketch, "E5.0.10.9", {"center": v(2085.49, -267) * mm, "radius": 3.18 * mm});
            skCircle(sketch, "E5.0.10.10", {"center": v(2053.74, -267) * mm, "radius": 3.18 * mm});
            skCircle(sketch, "E5.0.10.11", {"center": v(1926.74, -267) * mm, "radius": 3.18 * mm});
            skCircle(sketch, "E5.0.10.12", {"center": v(2021.99, -267) * mm, "radius": 3.18 * mm});
            skCircle(sketch, "E5.0.10.13", {"center": v(2148.99, -267) * mm, "radius": 3.18 * mm});
            skCircle(sketch, "E5.0.10.14", {"center": v(1990.24, -267) * mm, "radius": 3.18 * mm});
            skCircle(sketch, "E5.0.10.15", {"center": v(1450.49, -267) * mm, "radius": 3.18 * mm});
            skCircle(sketch, "E5.0.10.16", {"center": v(1228.24, -267) * mm, "radius": 3.18 * mm});
            skCircle(sketch, "E5.0.10.17", {"center": v(1736.24, -267) * mm, "radius": 3.18 * mm});
            skCircle(sketch, "E5.0.10.18", {"center": v(1386.99, -267) * mm, "radius": 3.18 * mm});
            skCircle(sketch, "E5.0.10.19", {"center": v(1164.74, -267) * mm, "radius": 3.18 * mm});
            skCircle(sketch, "E5.0.10.20", {"center": v(1672.74, -267) * mm, "radius": 3.18 * mm});
            skCircle(sketch, "E5.0.10.21", {"center": v(1101.24, -267) * mm, "radius": 3.18 * mm});
            skCircle(sketch, "E5.0.10.22", {"center": v(1609.24, -267) * mm, "radius": 3.18 * mm});
            skCircle(sketch, "E5.0.10.23", {"center": v(1355.24, -267) * mm, "radius": 3.18 * mm});
            skCircle(sketch, "E5.0.10.24", {"center": v(1863.24, -267) * mm, "radius": 3.18 * mm});
            skCircle(sketch, "E5.0.10.25", {"center": v(1069.49, -267) * mm, "radius": 3.18 * mm});
            skCircle(sketch, "E5.0.10.26", {"center": v(1577.49, -267) * mm, "radius": 3.18 * mm});
            skCircle(sketch, "E5.0.10.27", {"center": v(1323.49, -267) * mm, "radius": 3.18 * mm});
            skCircle(sketch, "E5.0.10.28", {"center": v(1831.49, -267) * mm, "radius": 3.18 * mm});
            skCircle(sketch, "E5.0.10.29", {"center": v(1037.74, -267) * mm, "radius": 3.18 * mm});
            skCircle(sketch, "E5.0.10.30", {"center": v(1545.74, -267) * mm, "radius": 3.18 * mm});
            skCircle(sketch, "E5.0.10.31", {"center": v(1418.74, -267) * mm, "radius": 3.18 * mm});
            skCircle(sketch, "E5.0.10.32", {"center": v(1005.99, -267) * mm, "radius": 3.18 * mm});
            skCircle(sketch, "E5.0.10.33", {"center": v(1513.99, -267) * mm, "radius": 3.18 * mm});
            skCircle(sketch, "E5.0.10.34", {"center": v(1799.74, -267) * mm, "radius": 3.18 * mm});
            skCircle(sketch, "E5.0.10.35", {"center": v(1291.74, -267) * mm, "radius": 3.18 * mm});
            skCircle(sketch, "E5.0.10.36", {"center": v(1132.99, -267) * mm, "radius": 3.18 * mm});
            skCircle(sketch, "E5.0.10.37", {"center": v(974.24, -267) * mm, "radius": 3.18 * mm});
            skCircle(sketch, "E5.0.10.38", {"center": v(1482.24, -267) * mm, "radius": 3.18 * mm});
            skCircle(sketch, "E5.0.10.39", {"center": v(1259.99, -267) * mm, "radius": 3.18 * mm});
            skCircle(sketch, "E5.0.10.40", {"center": v(1640.99, -267) * mm, "radius": 3.18 * mm});
            skCircle(sketch, "E5.0.10.41", {"center": v(1767.99, -267) * mm, "radius": 3.18 * mm});
            skCircle(sketch, "E5.0.10.42", {"center": v(1196.49, -267) * mm, "radius": 3.18 * mm});
            skCircle(sketch, "E5.0.10.43", {"center": v(1704.49, -267) * mm, "radius": 3.18 * mm});
            skCircle(sketch, "E5.0.10.44", {"center": v(720.24, -267) * mm, "radius": 3.18 * mm});
            skCircle(sketch, "E5.0.10.45", {"center": v(942.49, -267) * mm, "radius": 3.18 * mm});
            skCircle(sketch, "E5.0.10.46", {"center": v(878.99, -267) * mm, "radius": 3.18 * mm});
            skCircle(sketch, "E5.0.10.47", {"center": v(434.49, -267) * mm, "radius": 3.18 * mm});
            skCircle(sketch, "E5.0.10.48", {"center": v(656.74, -267) * mm, "radius": 3.18 * mm});
            skCircle(sketch, "E5.0.10.49", {"center": v(370.99, -267) * mm, "radius": 3.18 * mm});
            skCircle(sketch, "E5.0.10.50", {"center": v(593.24, -267) * mm, "radius": 3.18 * mm});
            skCircle(sketch, "E5.0.10.51", {"center": v(847.24, -267) * mm, "radius": 3.18 * mm});
            skCircle(sketch, "E5.0.10.52", {"center": v(339.24, -267) * mm, "radius": 3.18 * mm});
            skCircle(sketch, "E5.0.10.53", {"center": v(561.49, -267) * mm, "radius": 3.18 * mm});
            skCircle(sketch, "E5.0.10.54", {"center": v(815.49, -267) * mm, "radius": 3.18 * mm});
            skCircle(sketch, "E5.0.10.55", {"center": v(307.49, -267) * mm, "radius": 3.18 * mm});
            skCircle(sketch, "E5.0.10.56", {"center": v(529.74, -267) * mm, "radius": 3.18 * mm});
            skCircle(sketch, "E5.0.10.57", {"center": v(180.49, -267) * mm, "radius": 3.18 * mm});
            skCircle(sketch, "E5.0.10.58", {"center": v(148.74, -267) * mm, "radius": 3.18 * mm});
            skCircle(sketch, "E5.0.10.59", {"center": v(910.74, -267) * mm, "radius": 3.18 * mm});
            skCircle(sketch, "E5.0.10.60", {"center": v(275.74, -267) * mm, "radius": 3.18 * mm});
            skCircle(sketch, "E5.0.10.61", {"center": v(243.99, -267) * mm, "radius": 3.18 * mm});
            skCircle(sketch, "E5.0.10.62", {"center": v(212.24, -267) * mm, "radius": 3.18 * mm});
            skCircle(sketch, "E5.0.10.63", {"center": v(783.74, -267) * mm, "radius": 3.18 * mm});
            skCircle(sketch, "E5.0.10.64", {"center": v(497.99, -267) * mm, "radius": 3.18 * mm});
            skCircle(sketch, "E5.0.10.65", {"center": v(402.74, -267) * mm, "radius": 3.18 * mm});
            skCircle(sketch, "E5.0.10.66", {"center": v(624.99, -267) * mm, "radius": 3.18 * mm});
            skCircle(sketch, "E5.0.10.67", {"center": v(751.99, -267) * mm, "radius": 3.18 * mm});
            skCircle(sketch, "E5.0.10.68", {"center": v(466.24, -267) * mm, "radius": 3.18 * mm});
            skCircle(sketch, "E5.0.10.69", {"center": v(688.49, -267) * mm, "radius": 3.18 * mm});
            skCircle(sketch, "E5.0.10.70", {"center": v(116.99, -267) * mm, "radius": 3.18 * mm});
            skCircle(sketch, "E5.0.10.71", {"center": v(85.24, -267) * mm, "radius": 3.18 * mm});
            skCircle(sketch, "E5.0.10.72", {"center": v(53.49, -267) * mm, "radius": 3.18 * mm});
            skLineSegment(sketch, "E5.0.10.73", {"start": v(-41.76, -267) * mm, "end": v(-10.01, -267) * mm, "construction": true});
            skCircle(sketch, "E5.0.10.74", {"center": v(21.74, -267) * mm, "radius": 3.18 * mm});
            skCircle(sketch, "E5.0.10.75", {"center": v(-10.01, -267) * mm, "radius": 3.18 * mm});
            skCircle(sketch, "E5.0.10.76", {"center": v(-41.76, -267) * mm, "radius": 3.18 * mm});
            skCircle(sketch, "E5.0.11.0", {"center": v(2244.24, -292.4) * mm, "radius": 3.18 * mm});
            skCircle(sketch, "E5.0.11.1", {"center": v(2180.74, -292.4) * mm, "radius": 3.18 * mm});
            skCircle(sketch, "E5.0.11.2", {"center": v(2339.49, -292.4) * mm, "radius": 3.18 * mm});
            skCircle(sketch, "E5.0.11.3", {"center": v(2307.74, -292.4) * mm, "radius": 3.18 * mm});
            skCircle(sketch, "E5.0.11.4", {"center": v(2275.99, -292.4) * mm, "radius": 3.18 * mm});
            skCircle(sketch, "E5.0.11.5", {"center": v(2212.49, -292.4) * mm, "radius": 3.18 * mm});
            skCircle(sketch, "E5.0.11.6", {"center": v(1958.49, -292.4) * mm, "radius": 3.18 * mm});
            skCircle(sketch, "E5.0.11.7", {"center": v(1894.99, -292.4) * mm, "radius": 3.18 * mm});
            skCircle(sketch, "E5.0.11.8", {"center": v(2117.24, -292.4) * mm, "radius": 3.18 * mm});
            skCircle(sketch, "E5.0.11.9", {"center": v(2085.49, -292.4) * mm, "radius": 3.18 * mm});
            skCircle(sketch, "E5.0.11.10", {"center": v(2053.74, -292.4) * mm, "radius": 3.18 * mm});
            skCircle(sketch, "E5.0.11.11", {"center": v(1926.74, -292.4) * mm, "radius": 3.18 * mm});
            skCircle(sketch, "E5.0.11.12", {"center": v(2021.99, -292.4) * mm, "radius": 3.18 * mm});
            skCircle(sketch, "E5.0.11.13", {"center": v(2148.99, -292.4) * mm, "radius": 3.18 * mm});
            skCircle(sketch, "E5.0.11.14", {"center": v(1990.24, -292.4) * mm, "radius": 3.18 * mm});
            skCircle(sketch, "E5.0.11.15", {"center": v(1450.49, -292.4) * mm, "radius": 3.18 * mm});
            skCircle(sketch, "E5.0.11.16", {"center": v(1228.24, -292.4) * mm, "radius": 3.18 * mm});
            skCircle(sketch, "E5.0.11.17", {"center": v(1736.24, -292.4) * mm, "radius": 3.18 * mm});
            skCircle(sketch, "E5.0.11.18", {"center": v(1386.99, -292.4) * mm, "radius": 3.18 * mm});
            skCircle(sketch, "E5.0.11.19", {"center": v(1164.74, -292.4) * mm, "radius": 3.18 * mm});
            skCircle(sketch, "E5.0.11.20", {"center": v(1672.74, -292.4) * mm, "radius": 3.18 * mm});
            skCircle(sketch, "E5.0.11.21", {"center": v(1101.24, -292.4) * mm, "radius": 3.18 * mm});
            skCircle(sketch, "E5.0.11.22", {"center": v(1609.24, -292.4) * mm, "radius": 3.18 * mm});
            skCircle(sketch, "E5.0.11.23", {"center": v(1355.24, -292.4) * mm, "radius": 3.18 * mm});
            skCircle(sketch, "E5.0.11.24", {"center": v(1863.24, -292.4) * mm, "radius": 3.18 * mm});
            skCircle(sketch, "E5.0.11.25", {"center": v(1069.49, -292.4) * mm, "radius": 3.18 * mm});
            skCircle(sketch, "E5.0.11.26", {"center": v(1577.49, -292.4) * mm, "radius": 3.18 * mm});
            skCircle(sketch, "E5.0.11.27", {"center": v(1323.49, -292.4) * mm, "radius": 3.18 * mm});
            skCircle(sketch, "E5.0.11.28", {"center": v(1831.49, -292.4) * mm, "radius": 3.18 * mm});
            skCircle(sketch, "E5.0.11.29", {"center": v(1037.74, -292.4) * mm, "radius": 3.18 * mm});
            skCircle(sketch, "E5.0.11.30", {"center": v(1545.74, -292.4) * mm, "radius": 3.18 * mm});
            skCircle(sketch, "E5.0.11.31", {"center": v(1418.74, -292.4) * mm, "radius": 3.18 * mm});
            skCircle(sketch, "E5.0.11.32", {"center": v(1005.99, -292.4) * mm, "radius": 3.18 * mm});
            skCircle(sketch, "E5.0.11.33", {"center": v(1513.99, -292.4) * mm, "radius": 3.18 * mm});
            skCircle(sketch, "E5.0.11.34", {"center": v(1799.74, -292.4) * mm, "radius": 3.18 * mm});
            skCircle(sketch, "E5.0.11.35", {"center": v(1291.74, -292.4) * mm, "radius": 3.18 * mm});
            skCircle(sketch, "E5.0.11.36", {"center": v(1132.99, -292.4) * mm, "radius": 3.18 * mm});
            skCircle(sketch, "E5.0.11.37", {"center": v(974.24, -292.4) * mm, "radius": 3.18 * mm});
            skCircle(sketch, "E5.0.11.38", {"center": v(1482.24, -292.4) * mm, "radius": 3.18 * mm});
            skCircle(sketch, "E5.0.11.39", {"center": v(1259.99, -292.4) * mm, "radius": 3.18 * mm});
            skCircle(sketch, "E5.0.11.40", {"center": v(1640.99, -292.4) * mm, "radius": 3.18 * mm});
            skCircle(sketch, "E5.0.11.41", {"center": v(1767.99, -292.4) * mm, "radius": 3.18 * mm});
            skCircle(sketch, "E5.0.11.42", {"center": v(1196.49, -292.4) * mm, "radius": 3.18 * mm});
            skCircle(sketch, "E5.0.11.43", {"center": v(1704.49, -292.4) * mm, "radius": 3.18 * mm});
            skCircle(sketch, "E5.0.11.44", {"center": v(720.24, -292.4) * mm, "radius": 3.18 * mm});
            skCircle(sketch, "E5.0.11.45", {"center": v(942.49, -292.4) * mm, "radius": 3.18 * mm});
            skCircle(sketch, "E5.0.11.46", {"center": v(878.99, -292.4) * mm, "radius": 3.18 * mm});
            skCircle(sketch, "E5.0.11.47", {"center": v(434.49, -292.4) * mm, "radius": 3.18 * mm});
            skCircle(sketch, "E5.0.11.48", {"center": v(656.74, -292.4) * mm, "radius": 3.18 * mm});
            skCircle(sketch, "E5.0.11.49", {"center": v(370.99, -292.4) * mm, "radius": 3.18 * mm});
            skCircle(sketch, "E5.0.11.50", {"center": v(593.24, -292.4) * mm, "radius": 3.18 * mm});
            skCircle(sketch, "E5.0.11.51", {"center": v(847.24, -292.4) * mm, "radius": 3.18 * mm});
            skCircle(sketch, "E5.0.11.52", {"center": v(339.24, -292.4) * mm, "radius": 3.18 * mm});
            skCircle(sketch, "E5.0.11.53", {"center": v(561.49, -292.4) * mm, "radius": 3.18 * mm});
            skCircle(sketch, "E5.0.11.54", {"center": v(815.49, -292.4) * mm, "radius": 3.18 * mm});
            skCircle(sketch, "E5.0.11.55", {"center": v(307.49, -292.4) * mm, "radius": 3.18 * mm});
            skCircle(sketch, "E5.0.11.56", {"center": v(529.74, -292.4) * mm, "radius": 3.18 * mm});
            skCircle(sketch, "E5.0.11.57", {"center": v(180.49, -292.4) * mm, "radius": 3.18 * mm});
            skCircle(sketch, "E5.0.11.58", {"center": v(148.74, -292.4) * mm, "radius": 3.18 * mm});
            skCircle(sketch, "E5.0.11.59", {"center": v(910.74, -292.4) * mm, "radius": 3.18 * mm});
            skCircle(sketch, "E5.0.11.60", {"center": v(275.74, -292.4) * mm, "radius": 3.18 * mm});
            skCircle(sketch, "E5.0.11.61", {"center": v(243.99, -292.4) * mm, "radius": 3.18 * mm});
            skCircle(sketch, "E5.0.11.62", {"center": v(212.24, -292.4) * mm, "radius": 3.18 * mm});
            skCircle(sketch, "E5.0.11.63", {"center": v(783.74, -292.4) * mm, "radius": 3.18 * mm});
            skCircle(sketch, "E5.0.11.64", {"center": v(497.99, -292.4) * mm, "radius": 3.18 * mm});
            skCircle(sketch, "E5.0.11.65", {"center": v(402.74, -292.4) * mm, "radius": 3.18 * mm});
            skCircle(sketch, "E5.0.11.66", {"center": v(624.99, -292.4) * mm, "radius": 3.18 * mm});
            skCircle(sketch, "E5.0.11.67", {"center": v(751.99, -292.4) * mm, "radius": 3.18 * mm});
            skCircle(sketch, "E5.0.11.68", {"center": v(466.24, -292.4) * mm, "radius": 3.18 * mm});
            skCircle(sketch, "E5.0.11.69", {"center": v(688.49, -292.4) * mm, "radius": 3.18 * mm});
            skCircle(sketch, "E5.0.11.70", {"center": v(116.99, -292.4) * mm, "radius": 3.18 * mm});
            skCircle(sketch, "E5.0.11.71", {"center": v(85.24, -292.4) * mm, "radius": 3.18 * mm});
            skCircle(sketch, "E5.0.11.72", {"center": v(53.49, -292.4) * mm, "radius": 3.18 * mm});
            skLineSegment(sketch, "E5.0.11.73", {"start": v(-41.76, -292.4) * mm, "end": v(-10.01, -292.4) * mm, "construction": true});
            skCircle(sketch, "E5.0.11.74", {"center": v(21.74, -292.4) * mm, "radius": 3.18 * mm});
            skCircle(sketch, "E5.0.11.75", {"center": v(-10.01, -292.4) * mm, "radius": 3.18 * mm});
            skCircle(sketch, "E5.0.11.76", {"center": v(-41.76, -292.4) * mm, "radius": 3.18 * mm});
            skCircle(sketch, "E5.0.12.0", {"center": v(2244.24, -317.8) * mm, "radius": 3.18 * mm});
            skCircle(sketch, "E5.0.12.1", {"center": v(2180.74, -317.8) * mm, "radius": 3.18 * mm});
            skCircle(sketch, "E5.0.12.2", {"center": v(2339.49, -317.8) * mm, "radius": 3.18 * mm});
            skCircle(sketch, "E5.0.12.3", {"center": v(2307.74, -317.8) * mm, "radius": 3.18 * mm});
            skCircle(sketch, "E5.0.12.4", {"center": v(2275.99, -317.8) * mm, "radius": 3.18 * mm});
            skCircle(sketch, "E5.0.12.5", {"center": v(2212.49, -317.8) * mm, "radius": 3.18 * mm});
            skCircle(sketch, "E5.0.12.6", {"center": v(1958.49, -317.8) * mm, "radius": 3.18 * mm});
            skCircle(sketch, "E5.0.12.7", {"center": v(1894.99, -317.8) * mm, "radius": 3.18 * mm});
            skCircle(sketch, "E5.0.12.8", {"center": v(2117.24, -317.8) * mm, "radius": 3.18 * mm});
            skCircle(sketch, "E5.0.12.9", {"center": v(2085.49, -317.8) * mm, "radius": 3.18 * mm});
            skCircle(sketch, "E5.0.12.10", {"center": v(2053.74, -317.8) * mm, "radius": 3.18 * mm});
            skCircle(sketch, "E5.0.12.11", {"center": v(1926.74, -317.8) * mm, "radius": 3.18 * mm});
            skCircle(sketch, "E5.0.12.12", {"center": v(2021.99, -317.8) * mm, "radius": 3.18 * mm});
            skCircle(sketch, "E5.0.12.13", {"center": v(2148.99, -317.8) * mm, "radius": 3.18 * mm});
            skCircle(sketch, "E5.0.12.14", {"center": v(1990.24, -317.8) * mm, "radius": 3.18 * mm});
            skCircle(sketch, "E5.0.12.15", {"center": v(1450.49, -317.8) * mm, "radius": 3.18 * mm});
            skCircle(sketch, "E5.0.12.16", {"center": v(1228.24, -317.8) * mm, "radius": 3.18 * mm});
            skCircle(sketch, "E5.0.12.17", {"center": v(1736.24, -317.8) * mm, "radius": 3.18 * mm});
            skCircle(sketch, "E5.0.12.18", {"center": v(1386.99, -317.8) * mm, "radius": 3.18 * mm});
            skCircle(sketch, "E5.0.12.19", {"center": v(1164.74, -317.8) * mm, "radius": 3.18 * mm});
            skCircle(sketch, "E5.0.12.20", {"center": v(1672.74, -317.8) * mm, "radius": 3.18 * mm});
            skCircle(sketch, "E5.0.12.21", {"center": v(1101.24, -317.8) * mm, "radius": 3.18 * mm});
            skCircle(sketch, "E5.0.12.22", {"center": v(1609.24, -317.8) * mm, "radius": 3.18 * mm});
            skCircle(sketch, "E5.0.12.23", {"center": v(1355.24, -317.8) * mm, "radius": 3.18 * mm});
            skCircle(sketch, "E5.0.12.24", {"center": v(1863.24, -317.8) * mm, "radius": 3.18 * mm});
            skCircle(sketch, "E5.0.12.25", {"center": v(1069.49, -317.8) * mm, "radius": 3.18 * mm});
            skCircle(sketch, "E5.0.12.26", {"center": v(1577.49, -317.8) * mm, "radius": 3.18 * mm});
            skCircle(sketch, "E5.0.12.27", {"center": v(1323.49, -317.8) * mm, "radius": 3.18 * mm});
            skCircle(sketch, "E5.0.12.28", {"center": v(1831.49, -317.8) * mm, "radius": 3.18 * mm});
            skCircle(sketch, "E5.0.12.29", {"center": v(1037.74, -317.8) * mm, "radius": 3.18 * mm});
            skCircle(sketch, "E5.0.12.30", {"center": v(1545.74, -317.8) * mm, "radius": 3.18 * mm});
            skCircle(sketch, "E5.0.12.31", {"center": v(1418.74, -317.8) * mm, "radius": 3.18 * mm});
            skCircle(sketch, "E5.0.12.32", {"center": v(1005.99, -317.8) * mm, "radius": 3.18 * mm});
            skCircle(sketch, "E5.0.12.33", {"center": v(1513.99, -317.8) * mm, "radius": 3.18 * mm});
            skCircle(sketch, "E5.0.12.34", {"center": v(1799.74, -317.8) * mm, "radius": 3.18 * mm});
            skCircle(sketch, "E5.0.12.35", {"center": v(1291.74, -317.8) * mm, "radius": 3.18 * mm});
            skCircle(sketch, "E5.0.12.36", {"center": v(1132.99, -317.8) * mm, "radius": 3.18 * mm});
            skCircle(sketch, "E5.0.12.37", {"center": v(974.24, -317.8) * mm, "radius": 3.18 * mm});
            skCircle(sketch, "E5.0.12.38", {"center": v(1482.24, -317.8) * mm, "radius": 3.18 * mm});
            skCircle(sketch, "E5.0.12.39", {"center": v(1259.99, -317.8) * mm, "radius": 3.18 * mm});
            skCircle(sketch, "E5.0.12.40", {"center": v(1640.99, -317.8) * mm, "radius": 3.18 * mm});
            skCircle(sketch, "E5.0.12.41", {"center": v(1767.99, -317.8) * mm, "radius": 3.18 * mm});
            skCircle(sketch, "E5.0.12.42", {"center": v(1196.49, -317.8) * mm, "radius": 3.18 * mm});
            skCircle(sketch, "E5.0.12.43", {"center": v(1704.49, -317.8) * mm, "radius": 3.18 * mm});
            skCircle(sketch, "E5.0.12.44", {"center": v(720.24, -317.8) * mm, "radius": 3.18 * mm});
            skCircle(sketch, "E5.0.12.45", {"center": v(942.49, -317.8) * mm, "radius": 3.18 * mm});
            skCircle(sketch, "E5.0.12.46", {"center": v(878.99, -317.8) * mm, "radius": 3.18 * mm});
            skCircle(sketch, "E5.0.12.47", {"center": v(434.49, -317.8) * mm, "radius": 3.18 * mm});
            skCircle(sketch, "E5.0.12.48", {"center": v(656.74, -317.8) * mm, "radius": 3.18 * mm});
            skCircle(sketch, "E5.0.12.49", {"center": v(370.99, -317.8) * mm, "radius": 3.18 * mm});
            skCircle(sketch, "E5.0.12.50", {"center": v(593.24, -317.8) * mm, "radius": 3.18 * mm});
            skCircle(sketch, "E5.0.12.51", {"center": v(847.24, -317.8) * mm, "radius": 3.18 * mm});
            skCircle(sketch, "E5.0.12.52", {"center": v(339.24, -317.8) * mm, "radius": 3.18 * mm});
            skCircle(sketch, "E5.0.12.53", {"center": v(561.49, -317.8) * mm, "radius": 3.18 * mm});
            skCircle(sketch, "E5.0.12.54", {"center": v(815.49, -317.8) * mm, "radius": 3.18 * mm});
            skCircle(sketch, "E5.0.12.55", {"center": v(307.49, -317.8) * mm, "radius": 3.18 * mm});
            skCircle(sketch, "E5.0.12.56", {"center": v(529.74, -317.8) * mm, "radius": 3.18 * mm});
            skCircle(sketch, "E5.0.12.57", {"center": v(180.49, -317.8) * mm, "radius": 3.18 * mm});
            skCircle(sketch, "E5.0.12.58", {"center": v(148.74, -317.8) * mm, "radius": 3.18 * mm});
            skCircle(sketch, "E5.0.12.59", {"center": v(910.74, -317.8) * mm, "radius": 3.18 * mm});
            skCircle(sketch, "E5.0.12.60", {"center": v(275.74, -317.8) * mm, "radius": 3.18 * mm});
            skCircle(sketch, "E5.0.12.61", {"center": v(243.99, -317.8) * mm, "radius": 3.18 * mm});
            skCircle(sketch, "E5.0.12.62", {"center": v(212.24, -317.8) * mm, "radius": 3.18 * mm});
            skCircle(sketch, "E5.0.12.63", {"center": v(783.74, -317.8) * mm, "radius": 3.18 * mm});
            skCircle(sketch, "E5.0.12.64", {"center": v(497.99, -317.8) * mm, "radius": 3.18 * mm});
            skCircle(sketch, "E5.0.12.65", {"center": v(402.74, -317.8) * mm, "radius": 3.18 * mm});
            skCircle(sketch, "E5.0.12.66", {"center": v(624.99, -317.8) * mm, "radius": 3.18 * mm});
            skCircle(sketch, "E5.0.12.67", {"center": v(751.99, -317.8) * mm, "radius": 3.18 * mm});
            skCircle(sketch, "E5.0.12.68", {"center": v(466.24, -317.8) * mm, "radius": 3.18 * mm});
            skCircle(sketch, "E5.0.12.69", {"center": v(688.49, -317.8) * mm, "radius": 3.18 * mm});
            skCircle(sketch, "E5.0.12.70", {"center": v(116.99, -317.8) * mm, "radius": 3.18 * mm});
            skCircle(sketch, "E5.0.12.71", {"center": v(85.24, -317.8) * mm, "radius": 3.18 * mm});
            skCircle(sketch, "E5.0.12.72", {"center": v(53.49, -317.8) * mm, "radius": 3.18 * mm});
            skLineSegment(sketch, "E5.0.12.73", {"start": v(-41.76, -317.8) * mm, "end": v(-10.01, -317.8) * mm, "construction": true});
            skCircle(sketch, "E5.0.12.74", {"center": v(21.74, -317.8) * mm, "radius": 3.18 * mm});
            skCircle(sketch, "E5.0.12.75", {"center": v(-10.01, -317.8) * mm, "radius": 3.18 * mm});
            skCircle(sketch, "E5.0.12.76", {"center": v(-41.76, -317.8) * mm, "radius": 3.18 * mm});
            skCircle(sketch, "E5.0.13.0", {"center": v(2244.24, -343.2) * mm, "radius": 3.18 * mm});
            skCircle(sketch, "E5.0.13.1", {"center": v(2180.74, -343.2) * mm, "radius": 3.18 * mm});
            skCircle(sketch, "E5.0.13.2", {"center": v(2339.49, -343.2) * mm, "radius": 3.18 * mm});
            skCircle(sketch, "E5.0.13.3", {"center": v(2307.74, -343.2) * mm, "radius": 3.18 * mm});
            skCircle(sketch, "E5.0.13.4", {"center": v(2275.99, -343.2) * mm, "radius": 3.18 * mm});
            skCircle(sketch, "E5.0.13.5", {"center": v(2212.49, -343.2) * mm, "radius": 3.18 * mm});
            skCircle(sketch, "E5.0.13.6", {"center": v(1958.49, -343.2) * mm, "radius": 3.18 * mm});
            skCircle(sketch, "E5.0.13.7", {"center": v(1894.99, -343.2) * mm, "radius": 3.18 * mm});
            skCircle(sketch, "E5.0.13.8", {"center": v(2117.24, -343.2) * mm, "radius": 3.18 * mm});
            skCircle(sketch, "E5.0.13.9", {"center": v(2085.49, -343.2) * mm, "radius": 3.18 * mm});
            skCircle(sketch, "E5.0.13.10", {"center": v(2053.74, -343.2) * mm, "radius": 3.18 * mm});
            skCircle(sketch, "E5.0.13.11", {"center": v(1926.74, -343.2) * mm, "radius": 3.18 * mm});
            skCircle(sketch, "E5.0.13.12", {"center": v(2021.99, -343.2) * mm, "radius": 3.18 * mm});
            skCircle(sketch, "E5.0.13.13", {"center": v(2148.99, -343.2) * mm, "radius": 3.18 * mm});
            skCircle(sketch, "E5.0.13.14", {"center": v(1990.24, -343.2) * mm, "radius": 3.18 * mm});
            skCircle(sketch, "E5.0.13.15", {"center": v(1450.49, -343.2) * mm, "radius": 3.18 * mm});
            skCircle(sketch, "E5.0.13.16", {"center": v(1228.24, -343.2) * mm, "radius": 3.18 * mm});
            skCircle(sketch, "E5.0.13.17", {"center": v(1736.24, -343.2) * mm, "radius": 3.18 * mm});
            skCircle(sketch, "E5.0.13.18", {"center": v(1386.99, -343.2) * mm, "radius": 3.18 * mm});
            skCircle(sketch, "E5.0.13.19", {"center": v(1164.74, -343.2) * mm, "radius": 3.18 * mm});
            skCircle(sketch, "E5.0.13.20", {"center": v(1672.74, -343.2) * mm, "radius": 3.18 * mm});
            skCircle(sketch, "E5.0.13.21", {"center": v(1101.24, -343.2) * mm, "radius": 3.18 * mm});
            skCircle(sketch, "E5.0.13.22", {"center": v(1609.24, -343.2) * mm, "radius": 3.18 * mm});
            skCircle(sketch, "E5.0.13.23", {"center": v(1355.24, -343.2) * mm, "radius": 3.18 * mm});
            skCircle(sketch, "E5.0.13.24", {"center": v(1863.24, -343.2) * mm, "radius": 3.18 * mm});
            skCircle(sketch, "E5.0.13.25", {"center": v(1069.49, -343.2) * mm, "radius": 3.18 * mm});
            skCircle(sketch, "E5.0.13.26", {"center": v(1577.49, -343.2) * mm, "radius": 3.18 * mm});
            skCircle(sketch, "E5.0.13.27", {"center": v(1323.49, -343.2) * mm, "radius": 3.18 * mm});
            skCircle(sketch, "E5.0.13.28", {"center": v(1831.49, -343.2) * mm, "radius": 3.18 * mm});
            skCircle(sketch, "E5.0.13.29", {"center": v(1037.74, -343.2) * mm, "radius": 3.18 * mm});
            skCircle(sketch, "E5.0.13.30", {"center": v(1545.74, -343.2) * mm, "radius": 3.18 * mm});
            skCircle(sketch, "E5.0.13.31", {"center": v(1418.74, -343.2) * mm, "radius": 3.18 * mm});
            skCircle(sketch, "E5.0.13.32", {"center": v(1005.99, -343.2) * mm, "radius": 3.18 * mm});
            skCircle(sketch, "E5.0.13.33", {"center": v(1513.99, -343.2) * mm, "radius": 3.18 * mm});
            skCircle(sketch, "E5.0.13.34", {"center": v(1799.74, -343.2) * mm, "radius": 3.18 * mm});
            skCircle(sketch, "E5.0.13.35", {"center": v(1291.74, -343.2) * mm, "radius": 3.18 * mm});
            skCircle(sketch, "E5.0.13.36", {"center": v(1132.99, -343.2) * mm, "radius": 3.18 * mm});
            skCircle(sketch, "E5.0.13.37", {"center": v(974.24, -343.2) * mm, "radius": 3.18 * mm});
            skCircle(sketch, "E5.0.13.38", {"center": v(1482.24, -343.2) * mm, "radius": 3.18 * mm});
            skCircle(sketch, "E5.0.13.39", {"center": v(1259.99, -343.2) * mm, "radius": 3.18 * mm});
            skCircle(sketch, "E5.0.13.40", {"center": v(1640.99, -343.2) * mm, "radius": 3.18 * mm});
            skCircle(sketch, "E5.0.13.41", {"center": v(1767.99, -343.2) * mm, "radius": 3.18 * mm});
            skCircle(sketch, "E5.0.13.42", {"center": v(1196.49, -343.2) * mm, "radius": 3.18 * mm});
            skCircle(sketch, "E5.0.13.43", {"center": v(1704.49, -343.2) * mm, "radius": 3.18 * mm});
            skCircle(sketch, "E5.0.13.44", {"center": v(720.24, -343.2) * mm, "radius": 3.18 * mm});
            skCircle(sketch, "E5.0.13.45", {"center": v(942.49, -343.2) * mm, "radius": 3.18 * mm});
            skCircle(sketch, "E5.0.13.46", {"center": v(878.99, -343.2) * mm, "radius": 3.18 * mm});
            skCircle(sketch, "E5.0.13.47", {"center": v(434.49, -343.2) * mm, "radius": 3.18 * mm});
            skCircle(sketch, "E5.0.13.48", {"center": v(656.74, -343.2) * mm, "radius": 3.18 * mm});
            skCircle(sketch, "E5.0.13.49", {"center": v(370.99, -343.2) * mm, "radius": 3.18 * mm});
            skCircle(sketch, "E5.0.13.50", {"center": v(593.24, -343.2) * mm, "radius": 3.18 * mm});
            skCircle(sketch, "E5.0.13.51", {"center": v(847.24, -343.2) * mm, "radius": 3.18 * mm});
            skCircle(sketch, "E5.0.13.52", {"center": v(339.24, -343.2) * mm, "radius": 3.18 * mm});
            skCircle(sketch, "E5.0.13.53", {"center": v(561.49, -343.2) * mm, "radius": 3.18 * mm});
            skCircle(sketch, "E5.0.13.54", {"center": v(815.49, -343.2) * mm, "radius": 3.18 * mm});
            skCircle(sketch, "E5.0.13.55", {"center": v(307.49, -343.2) * mm, "radius": 3.18 * mm});
            skCircle(sketch, "E5.0.13.56", {"center": v(529.74, -343.2) * mm, "radius": 3.18 * mm});
            skCircle(sketch, "E5.0.13.57", {"center": v(180.49, -343.2) * mm, "radius": 3.18 * mm});
            skCircle(sketch, "E5.0.13.58", {"center": v(148.74, -343.2) * mm, "radius": 3.18 * mm});
            skCircle(sketch, "E5.0.13.59", {"center": v(910.74, -343.2) * mm, "radius": 3.18 * mm});
            skCircle(sketch, "E5.0.13.60", {"center": v(275.74, -343.2) * mm, "radius": 3.18 * mm});
            skCircle(sketch, "E5.0.13.61", {"center": v(243.99, -343.2) * mm, "radius": 3.18 * mm});
            skCircle(sketch, "E5.0.13.62", {"center": v(212.24, -343.2) * mm, "radius": 3.18 * mm});
            skCircle(sketch, "E5.0.13.63", {"center": v(783.74, -343.2) * mm, "radius": 3.18 * mm});
            skCircle(sketch, "E5.0.13.64", {"center": v(497.99, -343.2) * mm, "radius": 3.18 * mm});
            skCircle(sketch, "E5.0.13.65", {"center": v(402.74, -343.2) * mm, "radius": 3.18 * mm});
            skCircle(sketch, "E5.0.13.66", {"center": v(624.99, -343.2) * mm, "radius": 3.18 * mm});
            skCircle(sketch, "E5.0.13.67", {"center": v(751.99, -343.2) * mm, "radius": 3.18 * mm});
            skCircle(sketch, "E5.0.13.68", {"center": v(466.24, -343.2) * mm, "radius": 3.18 * mm});
            skCircle(sketch, "E5.0.13.69", {"center": v(688.49, -343.2) * mm, "radius": 3.18 * mm});
            skCircle(sketch, "E5.0.13.70", {"center": v(116.99, -343.2) * mm, "radius": 3.18 * mm});
            skCircle(sketch, "E5.0.13.71", {"center": v(85.24, -343.2) * mm, "radius": 3.18 * mm});
            skCircle(sketch, "E5.0.13.72", {"center": v(53.49, -343.2) * mm, "radius": 3.18 * mm});
            skLineSegment(sketch, "E5.0.13.73", {"start": v(-41.76, -343.2) * mm, "end": v(-10.01, -343.2) * mm, "construction": true});
            skCircle(sketch, "E5.0.13.74", {"center": v(21.74, -343.2) * mm, "radius": 3.18 * mm});
            skCircle(sketch, "E5.0.13.75", {"center": v(-10.01, -343.2) * mm, "radius": 3.18 * mm});
            skCircle(sketch, "E5.0.13.76", {"center": v(-41.76, -343.2) * mm, "radius": 3.18 * mm});
            skCircle(sketch, "E5.0.14.0", {"center": v(2244.24, -368.6) * mm, "radius": 3.18 * mm});
            skCircle(sketch, "E5.0.14.1", {"center": v(2180.74, -368.6) * mm, "radius": 3.18 * mm});
            skCircle(sketch, "E5.0.14.2", {"center": v(2339.49, -368.6) * mm, "radius": 3.18 * mm});
            skCircle(sketch, "E5.0.14.3", {"center": v(2307.74, -368.6) * mm, "radius": 3.18 * mm});
            skCircle(sketch, "E5.0.14.4", {"center": v(2275.99, -368.6) * mm, "radius": 3.18 * mm});
            skCircle(sketch, "E5.0.14.5", {"center": v(2212.49, -368.6) * mm, "radius": 3.18 * mm});
            skCircle(sketch, "E5.0.14.6", {"center": v(1958.49, -368.6) * mm, "radius": 3.18 * mm});
            skCircle(sketch, "E5.0.14.7", {"center": v(1894.99, -368.6) * mm, "radius": 3.18 * mm});
            skCircle(sketch, "E5.0.14.8", {"center": v(2117.24, -368.6) * mm, "radius": 3.18 * mm});
            skCircle(sketch, "E5.0.14.9", {"center": v(2085.49, -368.6) * mm, "radius": 3.18 * mm});
            skCircle(sketch, "E5.0.14.10", {"center": v(2053.74, -368.6) * mm, "radius": 3.18 * mm});
            skCircle(sketch, "E5.0.14.11", {"center": v(1926.74, -368.6) * mm, "radius": 3.18 * mm});
            skCircle(sketch, "E5.0.14.12", {"center": v(2021.99, -368.6) * mm, "radius": 3.18 * mm});
            skCircle(sketch, "E5.0.14.13", {"center": v(2148.99, -368.6) * mm, "radius": 3.18 * mm});
            skCircle(sketch, "E5.0.14.14", {"center": v(1990.24, -368.6) * mm, "radius": 3.18 * mm});
            skCircle(sketch, "E5.0.14.15", {"center": v(1450.49, -368.6) * mm, "radius": 3.18 * mm});
            skCircle(sketch, "E5.0.14.16", {"center": v(1228.24, -368.6) * mm, "radius": 3.18 * mm});
            skCircle(sketch, "E5.0.14.17", {"center": v(1736.24, -368.6) * mm, "radius": 3.18 * mm});
            skCircle(sketch, "E5.0.14.18", {"center": v(1386.99, -368.6) * mm, "radius": 3.18 * mm});
            skCircle(sketch, "E5.0.14.19", {"center": v(1164.74, -368.6) * mm, "radius": 3.18 * mm});
            skCircle(sketch, "E5.0.14.20", {"center": v(1672.74, -368.6) * mm, "radius": 3.18 * mm});
            skCircle(sketch, "E5.0.14.21", {"center": v(1101.24, -368.6) * mm, "radius": 3.18 * mm});
            skCircle(sketch, "E5.0.14.22", {"center": v(1609.24, -368.6) * mm, "radius": 3.18 * mm});
            skCircle(sketch, "E5.0.14.23", {"center": v(1355.24, -368.6) * mm, "radius": 3.18 * mm});
            skCircle(sketch, "E5.0.14.24", {"center": v(1863.24, -368.6) * mm, "radius": 3.18 * mm});
            skCircle(sketch, "E5.0.14.25", {"center": v(1069.49, -368.6) * mm, "radius": 3.18 * mm});
            skCircle(sketch, "E5.0.14.26", {"center": v(1577.49, -368.6) * mm, "radius": 3.18 * mm});
            skCircle(sketch, "E5.0.14.27", {"center": v(1323.49, -368.6) * mm, "radius": 3.18 * mm});
            skCircle(sketch, "E5.0.14.28", {"center": v(1831.49, -368.6) * mm, "radius": 3.18 * mm});
            skCircle(sketch, "E5.0.14.29", {"center": v(1037.74, -368.6) * mm, "radius": 3.18 * mm});
            skCircle(sketch, "E5.0.14.30", {"center": v(1545.74, -368.6) * mm, "radius": 3.18 * mm});
            skCircle(sketch, "E5.0.14.31", {"center": v(1418.74, -368.6) * mm, "radius": 3.18 * mm});
            skCircle(sketch, "E5.0.14.32", {"center": v(1005.99, -368.6) * mm, "radius": 3.18 * mm});
            skCircle(sketch, "E5.0.14.33", {"center": v(1513.99, -368.6) * mm, "radius": 3.18 * mm});
            skCircle(sketch, "E5.0.14.34", {"center": v(1799.74, -368.6) * mm, "radius": 3.18 * mm});
            skCircle(sketch, "E5.0.14.35", {"center": v(1291.74, -368.6) * mm, "radius": 3.18 * mm});
            skCircle(sketch, "E5.0.14.36", {"center": v(1132.99, -368.6) * mm, "radius": 3.18 * mm});
            skCircle(sketch, "E5.0.14.37", {"center": v(974.24, -368.6) * mm, "radius": 3.18 * mm});
            skCircle(sketch, "E5.0.14.38", {"center": v(1482.24, -368.6) * mm, "radius": 3.18 * mm});
            skCircle(sketch, "E5.0.14.39", {"center": v(1259.99, -368.6) * mm, "radius": 3.18 * mm});
            skCircle(sketch, "E5.0.14.40", {"center": v(1640.99, -368.6) * mm, "radius": 3.18 * mm});
            skCircle(sketch, "E5.0.14.41", {"center": v(1767.99, -368.6) * mm, "radius": 3.18 * mm});
            skCircle(sketch, "E5.0.14.42", {"center": v(1196.49, -368.6) * mm, "radius": 3.18 * mm});
            skCircle(sketch, "E5.0.14.43", {"center": v(1704.49, -368.6) * mm, "radius": 3.18 * mm});
            skCircle(sketch, "E5.0.14.44", {"center": v(720.24, -368.6) * mm, "radius": 3.18 * mm});
            skCircle(sketch, "E5.0.14.45", {"center": v(942.49, -368.6) * mm, "radius": 3.18 * mm});
            skCircle(sketch, "E5.0.14.46", {"center": v(878.99, -368.6) * mm, "radius": 3.18 * mm});
            skCircle(sketch, "E5.0.14.47", {"center": v(434.49, -368.6) * mm, "radius": 3.18 * mm});
            skCircle(sketch, "E5.0.14.48", {"center": v(656.74, -368.6) * mm, "radius": 3.18 * mm});
            skCircle(sketch, "E5.0.14.49", {"center": v(370.99, -368.6) * mm, "radius": 3.18 * mm});
            skCircle(sketch, "E5.0.14.50", {"center": v(593.24, -368.6) * mm, "radius": 3.18 * mm});
            skCircle(sketch, "E5.0.14.51", {"center": v(847.24, -368.6) * mm, "radius": 3.18 * mm});
            skCircle(sketch, "E5.0.14.52", {"center": v(339.24, -368.6) * mm, "radius": 3.18 * mm});
            skCircle(sketch, "E5.0.14.53", {"center": v(561.49, -368.6) * mm, "radius": 3.18 * mm});
            skCircle(sketch, "E5.0.14.54", {"center": v(815.49, -368.6) * mm, "radius": 3.18 * mm});
            skCircle(sketch, "E5.0.14.55", {"center": v(307.49, -368.6) * mm, "radius": 3.18 * mm});
            skCircle(sketch, "E5.0.14.56", {"center": v(529.74, -368.6) * mm, "radius": 3.18 * mm});
            skCircle(sketch, "E5.0.14.57", {"center": v(180.49, -368.6) * mm, "radius": 3.18 * mm});
            skCircle(sketch, "E5.0.14.58", {"center": v(148.74, -368.6) * mm, "radius": 3.18 * mm});
            skCircle(sketch, "E5.0.14.59", {"center": v(910.74, -368.6) * mm, "radius": 3.18 * mm});
            skCircle(sketch, "E5.0.14.60", {"center": v(275.74, -368.6) * mm, "radius": 3.18 * mm});
            skCircle(sketch, "E5.0.14.61", {"center": v(243.99, -368.6) * mm, "radius": 3.18 * mm});
            skCircle(sketch, "E5.0.14.62", {"center": v(212.24, -368.6) * mm, "radius": 3.18 * mm});
            skCircle(sketch, "E5.0.14.63", {"center": v(783.74, -368.6) * mm, "radius": 3.18 * mm});
            skCircle(sketch, "E5.0.14.64", {"center": v(497.99, -368.6) * mm, "radius": 3.18 * mm});
            skCircle(sketch, "E5.0.14.65", {"center": v(402.74, -368.6) * mm, "radius": 3.18 * mm});
            skCircle(sketch, "E5.0.14.66", {"center": v(624.99, -368.6) * mm, "radius": 3.18 * mm});
            skCircle(sketch, "E5.0.14.67", {"center": v(751.99, -368.6) * mm, "radius": 3.18 * mm});
            skCircle(sketch, "E5.0.14.68", {"center": v(466.24, -368.6) * mm, "radius": 3.18 * mm});
            skCircle(sketch, "E5.0.14.69", {"center": v(688.49, -368.6) * mm, "radius": 3.18 * mm});
            skCircle(sketch, "E5.0.14.70", {"center": v(116.99, -368.6) * mm, "radius": 3.18 * mm});
            skCircle(sketch, "E5.0.14.71", {"center": v(85.24, -368.6) * mm, "radius": 3.18 * mm});
            skCircle(sketch, "E5.0.14.72", {"center": v(53.49, -368.6) * mm, "radius": 3.18 * mm});
            skLineSegment(sketch, "E5.0.14.73", {"start": v(-41.76, -368.6) * mm, "end": v(-10.01, -368.6) * mm, "construction": true});
            skCircle(sketch, "E5.0.14.74", {"center": v(21.74, -368.6) * mm, "radius": 3.18 * mm});
            skCircle(sketch, "E5.0.14.75", {"center": v(-10.01, -368.6) * mm, "radius": 3.18 * mm});
            skCircle(sketch, "E5.0.14.76", {"center": v(-41.76, -368.6) * mm, "radius": 3.18 * mm});
            skCircle(sketch, "E5.0.15.0", {"center": v(2244.24, -394) * mm, "radius": 3.18 * mm});
            skCircle(sketch, "E5.0.15.1", {"center": v(2180.74, -394) * mm, "radius": 3.18 * mm});
            skCircle(sketch, "E5.0.15.2", {"center": v(2339.49, -394) * mm, "radius": 3.18 * mm});
            skCircle(sketch, "E5.0.15.3", {"center": v(2307.74, -394) * mm, "radius": 3.18 * mm});
            skCircle(sketch, "E5.0.15.4", {"center": v(2275.99, -394) * mm, "radius": 3.18 * mm});
            skCircle(sketch, "E5.0.15.5", {"center": v(2212.49, -394) * mm, "radius": 3.18 * mm});
            skCircle(sketch, "E5.0.15.6", {"center": v(1958.49, -394) * mm, "radius": 3.18 * mm});
            skCircle(sketch, "E5.0.15.7", {"center": v(1894.99, -394) * mm, "radius": 3.18 * mm});
            skCircle(sketch, "E5.0.15.8", {"center": v(2117.24, -394) * mm, "radius": 3.18 * mm});
            skCircle(sketch, "E5.0.15.9", {"center": v(2085.49, -394) * mm, "radius": 3.18 * mm});
            skCircle(sketch, "E5.0.15.10", {"center": v(2053.74, -394) * mm, "radius": 3.18 * mm});
            skCircle(sketch, "E5.0.15.11", {"center": v(1926.74, -394) * mm, "radius": 3.18 * mm});
            skCircle(sketch, "E5.0.15.12", {"center": v(2021.99, -394) * mm, "radius": 3.18 * mm});
            skCircle(sketch, "E5.0.15.13", {"center": v(2148.99, -394) * mm, "radius": 3.18 * mm});
            skCircle(sketch, "E5.0.15.14", {"center": v(1990.24, -394) * mm, "radius": 3.18 * mm});
            skCircle(sketch, "E5.0.15.15", {"center": v(1450.49, -394) * mm, "radius": 3.18 * mm});
            skCircle(sketch, "E5.0.15.16", {"center": v(1228.24, -394) * mm, "radius": 3.18 * mm});
            skCircle(sketch, "E5.0.15.17", {"center": v(1736.24, -394) * mm, "radius": 3.18 * mm});
            skCircle(sketch, "E5.0.15.18", {"center": v(1386.99, -394) * mm, "radius": 3.18 * mm});
            skCircle(sketch, "E5.0.15.19", {"center": v(1164.74, -394) * mm, "radius": 3.18 * mm});
            skCircle(sketch, "E5.0.15.20", {"center": v(1672.74, -394) * mm, "radius": 3.18 * mm});
            skCircle(sketch, "E5.0.15.21", {"center": v(1101.24, -394) * mm, "radius": 3.18 * mm});
            skCircle(sketch, "E5.0.15.22", {"center": v(1609.24, -394) * mm, "radius": 3.18 * mm});
            skCircle(sketch, "E5.0.15.23", {"center": v(1355.24, -394) * mm, "radius": 3.18 * mm});
            skCircle(sketch, "E5.0.15.24", {"center": v(1863.24, -394) * mm, "radius": 3.18 * mm});
            skCircle(sketch, "E5.0.15.25", {"center": v(1069.49, -394) * mm, "radius": 3.18 * mm});
            skCircle(sketch, "E5.0.15.26", {"center": v(1577.49, -394) * mm, "radius": 3.18 * mm});
            skCircle(sketch, "E5.0.15.27", {"center": v(1323.49, -394) * mm, "radius": 3.18 * mm});
            skCircle(sketch, "E5.0.15.28", {"center": v(1831.49, -394) * mm, "radius": 3.18 * mm});
            skCircle(sketch, "E5.0.15.29", {"center": v(1037.74, -394) * mm, "radius": 3.18 * mm});
            skCircle(sketch, "E5.0.15.30", {"center": v(1545.74, -394) * mm, "radius": 3.18 * mm});
            skCircle(sketch, "E5.0.15.31", {"center": v(1418.74, -394) * mm, "radius": 3.18 * mm});
            skCircle(sketch, "E5.0.15.32", {"center": v(1005.99, -394) * mm, "radius": 3.18 * mm});
            skCircle(sketch, "E5.0.15.33", {"center": v(1513.99, -394) * mm, "radius": 3.18 * mm});
            skCircle(sketch, "E5.0.15.34", {"center": v(1799.74, -394) * mm, "radius": 3.18 * mm});
            skCircle(sketch, "E5.0.15.35", {"center": v(1291.74, -394) * mm, "radius": 3.18 * mm});
            skCircle(sketch, "E5.0.15.36", {"center": v(1132.99, -394) * mm, "radius": 3.18 * mm});
            skCircle(sketch, "E5.0.15.37", {"center": v(974.24, -394) * mm, "radius": 3.18 * mm});
            skCircle(sketch, "E5.0.15.38", {"center": v(1482.24, -394) * mm, "radius": 3.18 * mm});
            skCircle(sketch, "E5.0.15.39", {"center": v(1259.99, -394) * mm, "radius": 3.18 * mm});
            skCircle(sketch, "E5.0.15.40", {"center": v(1640.99, -394) * mm, "radius": 3.18 * mm});
            skCircle(sketch, "E5.0.15.41", {"center": v(1767.99, -394) * mm, "radius": 3.18 * mm});
            skCircle(sketch, "E5.0.15.42", {"center": v(1196.49, -394) * mm, "radius": 3.18 * mm});
            skCircle(sketch, "E5.0.15.43", {"center": v(1704.49, -394) * mm, "radius": 3.18 * mm});
            skCircle(sketch, "E5.0.15.44", {"center": v(720.24, -394) * mm, "radius": 3.18 * mm});
            skCircle(sketch, "E5.0.15.45", {"center": v(942.49, -394) * mm, "radius": 3.18 * mm});
            skCircle(sketch, "E5.0.15.46", {"center": v(878.99, -394) * mm, "radius": 3.18 * mm});
            skCircle(sketch, "E5.0.15.47", {"center": v(434.49, -394) * mm, "radius": 3.18 * mm});
            skCircle(sketch, "E5.0.15.48", {"center": v(656.74, -394) * mm, "radius": 3.18 * mm});
            skCircle(sketch, "E5.0.15.49", {"center": v(370.99, -394) * mm, "radius": 3.18 * mm});
            skCircle(sketch, "E5.0.15.50", {"center": v(593.24, -394) * mm, "radius": 3.18 * mm});
            skCircle(sketch, "E5.0.15.51", {"center": v(847.24, -394) * mm, "radius": 3.18 * mm});
            skCircle(sketch, "E5.0.15.52", {"center": v(339.24, -394) * mm, "radius": 3.18 * mm});
            skCircle(sketch, "E5.0.15.53", {"center": v(561.49, -394) * mm, "radius": 3.18 * mm});
            skCircle(sketch, "E5.0.15.54", {"center": v(815.49, -394) * mm, "radius": 3.18 * mm});
            skCircle(sketch, "E5.0.15.55", {"center": v(307.49, -394) * mm, "radius": 3.18 * mm});
            skCircle(sketch, "E5.0.15.56", {"center": v(529.74, -394) * mm, "radius": 3.18 * mm});
            skCircle(sketch, "E5.0.15.57", {"center": v(180.49, -394) * mm, "radius": 3.18 * mm});
            skCircle(sketch, "E5.0.15.58", {"center": v(148.74, -394) * mm, "radius": 3.18 * mm});
            skCircle(sketch, "E5.0.15.59", {"center": v(910.74, -394) * mm, "radius": 3.18 * mm});
            skCircle(sketch, "E5.0.15.60", {"center": v(275.74, -394) * mm, "radius": 3.18 * mm});
            skCircle(sketch, "E5.0.15.61", {"center": v(243.99, -394) * mm, "radius": 3.18 * mm});
            skCircle(sketch, "E5.0.15.62", {"center": v(212.24, -394) * mm, "radius": 3.18 * mm});
            skCircle(sketch, "E5.0.15.63", {"center": v(783.74, -394) * mm, "radius": 3.18 * mm});
            skCircle(sketch, "E5.0.15.64", {"center": v(497.99, -394) * mm, "radius": 3.18 * mm});
            skCircle(sketch, "E5.0.15.65", {"center": v(402.74, -394) * mm, "radius": 3.18 * mm});
            skCircle(sketch, "E5.0.15.66", {"center": v(624.99, -394) * mm, "radius": 3.18 * mm});
            skCircle(sketch, "E5.0.15.67", {"center": v(751.99, -394) * mm, "radius": 3.18 * mm});
            skCircle(sketch, "E5.0.15.68", {"center": v(466.24, -394) * mm, "radius": 3.18 * mm});
            skCircle(sketch, "E5.0.15.69", {"center": v(688.49, -394) * mm, "radius": 3.18 * mm});
            skCircle(sketch, "E5.0.15.70", {"center": v(116.99, -394) * mm, "radius": 3.18 * mm});
            skCircle(sketch, "E5.0.15.71", {"center": v(85.24, -394) * mm, "radius": 3.18 * mm});
            skCircle(sketch, "E5.0.15.72", {"center": v(53.49, -394) * mm, "radius": 3.18 * mm});
            skLineSegment(sketch, "E5.0.15.73", {"start": v(-41.76, -394) * mm, "end": v(-10.01, -394) * mm, "construction": true});
            skCircle(sketch, "E5.0.15.74", {"center": v(21.74, -394) * mm, "radius": 3.18 * mm});
            skCircle(sketch, "E5.0.15.75", {"center": v(-10.01, -394) * mm, "radius": 3.18 * mm});
            skCircle(sketch, "E5.0.15.76", {"center": v(-41.76, -394) * mm, "radius": 3.18 * mm});
            skCircle(sketch, "E5.0.16.0", {"center": v(2244.24, -419.4) * mm, "radius": 3.18 * mm});
            skCircle(sketch, "E5.0.16.1", {"center": v(2180.74, -419.4) * mm, "radius": 3.18 * mm});
            skCircle(sketch, "E5.0.16.2", {"center": v(2339.49, -419.4) * mm, "radius": 3.18 * mm});
            skCircle(sketch, "E5.0.16.3", {"center": v(2307.74, -419.4) * mm, "radius": 3.18 * mm});
            skCircle(sketch, "E5.0.16.4", {"center": v(2275.99, -419.4) * mm, "radius": 3.18 * mm});
            skCircle(sketch, "E5.0.16.5", {"center": v(2212.49, -419.4) * mm, "radius": 3.18 * mm});
            skCircle(sketch, "E5.0.16.6", {"center": v(1958.49, -419.4) * mm, "radius": 3.18 * mm});
            skCircle(sketch, "E5.0.16.7", {"center": v(1894.99, -419.4) * mm, "radius": 3.18 * mm});
            skCircle(sketch, "E5.0.16.8", {"center": v(2117.24, -419.4) * mm, "radius": 3.18 * mm});
            skCircle(sketch, "E5.0.16.9", {"center": v(2085.49, -419.4) * mm, "radius": 3.18 * mm});
            skCircle(sketch, "E5.0.16.10", {"center": v(2053.74, -419.4) * mm, "radius": 3.18 * mm});
            skCircle(sketch, "E5.0.16.11", {"center": v(1926.74, -419.4) * mm, "radius": 3.18 * mm});
            skCircle(sketch, "E5.0.16.12", {"center": v(2021.99, -419.4) * mm, "radius": 3.18 * mm});
            skCircle(sketch, "E5.0.16.13", {"center": v(2148.99, -419.4) * mm, "radius": 3.18 * mm});
            skCircle(sketch, "E5.0.16.14", {"center": v(1990.24, -419.4) * mm, "radius": 3.18 * mm});
            skCircle(sketch, "E5.0.16.15", {"center": v(1450.49, -419.4) * mm, "radius": 3.18 * mm});
            skCircle(sketch, "E5.0.16.16", {"center": v(1228.24, -419.4) * mm, "radius": 3.18 * mm});
            skCircle(sketch, "E5.0.16.17", {"center": v(1736.24, -419.4) * mm, "radius": 3.18 * mm});
            skCircle(sketch, "E5.0.16.18", {"center": v(1386.99, -419.4) * mm, "radius": 3.18 * mm});
            skCircle(sketch, "E5.0.16.19", {"center": v(1164.74, -419.4) * mm, "radius": 3.18 * mm});
            skCircle(sketch, "E5.0.16.20", {"center": v(1672.74, -419.4) * mm, "radius": 3.18 * mm});
            skCircle(sketch, "E5.0.16.21", {"center": v(1101.24, -419.4) * mm, "radius": 3.18 * mm});
            skCircle(sketch, "E5.0.16.22", {"center": v(1609.24, -419.4) * mm, "radius": 3.18 * mm});
            skCircle(sketch, "E5.0.16.23", {"center": v(1355.24, -419.4) * mm, "radius": 3.18 * mm});
            skCircle(sketch, "E5.0.16.24", {"center": v(1863.24, -419.4) * mm, "radius": 3.18 * mm});
            skCircle(sketch, "E5.0.16.25", {"center": v(1069.49, -419.4) * mm, "radius": 3.18 * mm});
            skCircle(sketch, "E5.0.16.26", {"center": v(1577.49, -419.4) * mm, "radius": 3.18 * mm});
            skCircle(sketch, "E5.0.16.27", {"center": v(1323.49, -419.4) * mm, "radius": 3.18 * mm});
            skCircle(sketch, "E5.0.16.28", {"center": v(1831.49, -419.4) * mm, "radius": 3.18 * mm});
            skCircle(sketch, "E5.0.16.29", {"center": v(1037.74, -419.4) * mm, "radius": 3.18 * mm});
            skCircle(sketch, "E5.0.16.30", {"center": v(1545.74, -419.4) * mm, "radius": 3.18 * mm});
            skCircle(sketch, "E5.0.16.31", {"center": v(1418.74, -419.4) * mm, "radius": 3.18 * mm});
            skCircle(sketch, "E5.0.16.32", {"center": v(1005.99, -419.4) * mm, "radius": 3.18 * mm});
            skCircle(sketch, "E5.0.16.33", {"center": v(1513.99, -419.4) * mm, "radius": 3.18 * mm});
            skCircle(sketch, "E5.0.16.34", {"center": v(1799.74, -419.4) * mm, "radius": 3.18 * mm});
            skCircle(sketch, "E5.0.16.35", {"center": v(1291.74, -419.4) * mm, "radius": 3.18 * mm});
            skCircle(sketch, "E5.0.16.36", {"center": v(1132.99, -419.4) * mm, "radius": 3.18 * mm});
            skCircle(sketch, "E5.0.16.37", {"center": v(974.24, -419.4) * mm, "radius": 3.18 * mm});
            skCircle(sketch, "E5.0.16.38", {"center": v(1482.24, -419.4) * mm, "radius": 3.18 * mm});
            skCircle(sketch, "E5.0.16.39", {"center": v(1259.99, -419.4) * mm, "radius": 3.18 * mm});
            skCircle(sketch, "E5.0.16.40", {"center": v(1640.99, -419.4) * mm, "radius": 3.18 * mm});
            skCircle(sketch, "E5.0.16.41", {"center": v(1767.99, -419.4) * mm, "radius": 3.18 * mm});
            skCircle(sketch, "E5.0.16.42", {"center": v(1196.49, -419.4) * mm, "radius": 3.18 * mm});
            skCircle(sketch, "E5.0.16.43", {"center": v(1704.49, -419.4) * mm, "radius": 3.18 * mm});
            skCircle(sketch, "E5.0.16.44", {"center": v(720.24, -419.4) * mm, "radius": 3.18 * mm});
            skCircle(sketch, "E5.0.16.45", {"center": v(942.49, -419.4) * mm, "radius": 3.18 * mm});
            skCircle(sketch, "E5.0.16.46", {"center": v(878.99, -419.4) * mm, "radius": 3.18 * mm});
            skCircle(sketch, "E5.0.16.47", {"center": v(434.49, -419.4) * mm, "radius": 3.18 * mm});
            skCircle(sketch, "E5.0.16.48", {"center": v(656.74, -419.4) * mm, "radius": 3.18 * mm});
            skCircle(sketch, "E5.0.16.49", {"center": v(370.99, -419.4) * mm, "radius": 3.18 * mm});
            skCircle(sketch, "E5.0.16.50", {"center": v(593.24, -419.4) * mm, "radius": 3.18 * mm});
            skCircle(sketch, "E5.0.16.51", {"center": v(847.24, -419.4) * mm, "radius": 3.18 * mm});
            skCircle(sketch, "E5.0.16.52", {"center": v(339.24, -419.4) * mm, "radius": 3.18 * mm});
            skCircle(sketch, "E5.0.16.53", {"center": v(561.49, -419.4) * mm, "radius": 3.18 * mm});
            skCircle(sketch, "E5.0.16.54", {"center": v(815.49, -419.4) * mm, "radius": 3.18 * mm});
            skCircle(sketch, "E5.0.16.55", {"center": v(307.49, -419.4) * mm, "radius": 3.18 * mm});
            skCircle(sketch, "E5.0.16.56", {"center": v(529.74, -419.4) * mm, "radius": 3.18 * mm});
            skCircle(sketch, "E5.0.16.57", {"center": v(180.49, -419.4) * mm, "radius": 3.18 * mm});
            skCircle(sketch, "E5.0.16.58", {"center": v(148.74, -419.4) * mm, "radius": 3.18 * mm});
            skCircle(sketch, "E5.0.16.59", {"center": v(910.74, -419.4) * mm, "radius": 3.18 * mm});
            skCircle(sketch, "E5.0.16.60", {"center": v(275.74, -419.4) * mm, "radius": 3.18 * mm});
            skCircle(sketch, "E5.0.16.61", {"center": v(243.99, -419.4) * mm, "radius": 3.18 * mm});
            skCircle(sketch, "E5.0.16.62", {"center": v(212.24, -419.4) * mm, "radius": 3.18 * mm});
            skCircle(sketch, "E5.0.16.63", {"center": v(783.74, -419.4) * mm, "radius": 3.18 * mm});
            skCircle(sketch, "E5.0.16.64", {"center": v(497.99, -419.4) * mm, "radius": 3.18 * mm});
            skCircle(sketch, "E5.0.16.65", {"center": v(402.74, -419.4) * mm, "radius": 3.18 * mm});
            skCircle(sketch, "E5.0.16.66", {"center": v(624.99, -419.4) * mm, "radius": 3.18 * mm});
            skCircle(sketch, "E5.0.16.67", {"center": v(751.99, -419.4) * mm, "radius": 3.18 * mm});
            skCircle(sketch, "E5.0.16.68", {"center": v(466.24, -419.4) * mm, "radius": 3.18 * mm});
            skCircle(sketch, "E5.0.16.69", {"center": v(688.49, -419.4) * mm, "radius": 3.18 * mm});
            skCircle(sketch, "E5.0.16.70", {"center": v(116.99, -419.4) * mm, "radius": 3.18 * mm});
            skCircle(sketch, "E5.0.16.71", {"center": v(85.24, -419.4) * mm, "radius": 3.18 * mm});
            skCircle(sketch, "E5.0.16.72", {"center": v(53.49, -419.4) * mm, "radius": 3.18 * mm});
            skLineSegment(sketch, "E5.0.16.73", {"start": v(-41.76, -419.4) * mm, "end": v(-10.01, -419.4) * mm, "construction": true});
            skCircle(sketch, "E5.0.16.74", {"center": v(21.74, -419.4) * mm, "radius": 3.18 * mm});
            skCircle(sketch, "E5.0.16.75", {"center": v(-10.01, -419.4) * mm, "radius": 3.18 * mm});
            skCircle(sketch, "E5.0.16.76", {"center": v(-41.76, -419.4) * mm, "radius": 3.18 * mm});
            skCircle(sketch, "E5.0.17.0", {"center": v(2244.24, -444.8) * mm, "radius": 3.18 * mm});
            skCircle(sketch, "E5.0.17.1", {"center": v(2180.74, -444.8) * mm, "radius": 3.18 * mm});
            skCircle(sketch, "E5.0.17.2", {"center": v(2339.49, -444.8) * mm, "radius": 3.18 * mm});
            skCircle(sketch, "E5.0.17.3", {"center": v(2307.74, -444.8) * mm, "radius": 3.18 * mm});
            skCircle(sketch, "E5.0.17.4", {"center": v(2275.99, -444.8) * mm, "radius": 3.18 * mm});
            skCircle(sketch, "E5.0.17.5", {"center": v(2212.49, -444.8) * mm, "radius": 3.18 * mm});
            skCircle(sketch, "E5.0.17.6", {"center": v(1958.49, -444.8) * mm, "radius": 3.18 * mm});
            skCircle(sketch, "E5.0.17.7", {"center": v(1894.99, -444.8) * mm, "radius": 3.18 * mm});
            skCircle(sketch, "E5.0.17.8", {"center": v(2117.24, -444.8) * mm, "radius": 3.18 * mm});
            skCircle(sketch, "E5.0.17.9", {"center": v(2085.49, -444.8) * mm, "radius": 3.18 * mm});
            skCircle(sketch, "E5.0.17.10", {"center": v(2053.74, -444.8) * mm, "radius": 3.18 * mm});
            skCircle(sketch, "E5.0.17.11", {"center": v(1926.74, -444.8) * mm, "radius": 3.18 * mm});
            skCircle(sketch, "E5.0.17.12", {"center": v(2021.99, -444.8) * mm, "radius": 3.18 * mm});
            skCircle(sketch, "E5.0.17.13", {"center": v(2148.99, -444.8) * mm, "radius": 3.18 * mm});
            skCircle(sketch, "E5.0.17.14", {"center": v(1990.24, -444.8) * mm, "radius": 3.18 * mm});
            skCircle(sketch, "E5.0.17.15", {"center": v(1450.49, -444.8) * mm, "radius": 3.18 * mm});
            skCircle(sketch, "E5.0.17.16", {"center": v(1228.24, -444.8) * mm, "radius": 3.18 * mm});
            skCircle(sketch, "E5.0.17.17", {"center": v(1736.24, -444.8) * mm, "radius": 3.18 * mm});
            skCircle(sketch, "E5.0.17.18", {"center": v(1386.99, -444.8) * mm, "radius": 3.18 * mm});
            skCircle(sketch, "E5.0.17.19", {"center": v(1164.74, -444.8) * mm, "radius": 3.18 * mm});
            skCircle(sketch, "E5.0.17.20", {"center": v(1672.74, -444.8) * mm, "radius": 3.18 * mm});
            skCircle(sketch, "E5.0.17.21", {"center": v(1101.24, -444.8) * mm, "radius": 3.18 * mm});
            skCircle(sketch, "E5.0.17.22", {"center": v(1609.24, -444.8) * mm, "radius": 3.18 * mm});
            skCircle(sketch, "E5.0.17.23", {"center": v(1355.24, -444.8) * mm, "radius": 3.18 * mm});
            skCircle(sketch, "E5.0.17.24", {"center": v(1863.24, -444.8) * mm, "radius": 3.18 * mm});
            skCircle(sketch, "E5.0.17.25", {"center": v(1069.49, -444.8) * mm, "radius": 3.18 * mm});
            skCircle(sketch, "E5.0.17.26", {"center": v(1577.49, -444.8) * mm, "radius": 3.18 * mm});
            skCircle(sketch, "E5.0.17.27", {"center": v(1323.49, -444.8) * mm, "radius": 3.18 * mm});
            skCircle(sketch, "E5.0.17.28", {"center": v(1831.49, -444.8) * mm, "radius": 3.18 * mm});
            skCircle(sketch, "E5.0.17.29", {"center": v(1037.74, -444.8) * mm, "radius": 3.18 * mm});
            skCircle(sketch, "E5.0.17.30", {"center": v(1545.74, -444.8) * mm, "radius": 3.18 * mm});
            skCircle(sketch, "E5.0.17.31", {"center": v(1418.74, -444.8) * mm, "radius": 3.18 * mm});
            skCircle(sketch, "E5.0.17.32", {"center": v(1005.99, -444.8) * mm, "radius": 3.18 * mm});
            skCircle(sketch, "E5.0.17.33", {"center": v(1513.99, -444.8) * mm, "radius": 3.18 * mm});
            skCircle(sketch, "E5.0.17.34", {"center": v(1799.74, -444.8) * mm, "radius": 3.18 * mm});
            skCircle(sketch, "E5.0.17.35", {"center": v(1291.74, -444.8) * mm, "radius": 3.18 * mm});
            skCircle(sketch, "E5.0.17.36", {"center": v(1132.99, -444.8) * mm, "radius": 3.18 * mm});
            skCircle(sketch, "E5.0.17.37", {"center": v(974.24, -444.8) * mm, "radius": 3.18 * mm});
            skCircle(sketch, "E5.0.17.38", {"center": v(1482.24, -444.8) * mm, "radius": 3.18 * mm});
            skCircle(sketch, "E5.0.17.39", {"center": v(1259.99, -444.8) * mm, "radius": 3.18 * mm});
            skCircle(sketch, "E5.0.17.40", {"center": v(1640.99, -444.8) * mm, "radius": 3.18 * mm});
            skCircle(sketch, "E5.0.17.41", {"center": v(1767.99, -444.8) * mm, "radius": 3.18 * mm});
            skCircle(sketch, "E5.0.17.42", {"center": v(1196.49, -444.8) * mm, "radius": 3.18 * mm});
            skCircle(sketch, "E5.0.17.43", {"center": v(1704.49, -444.8) * mm, "radius": 3.18 * mm});
            skCircle(sketch, "E5.0.17.44", {"center": v(720.24, -444.8) * mm, "radius": 3.18 * mm});
            skCircle(sketch, "E5.0.17.45", {"center": v(942.49, -444.8) * mm, "radius": 3.18 * mm});
            skCircle(sketch, "E5.0.17.46", {"center": v(878.99, -444.8) * mm, "radius": 3.18 * mm});
            skCircle(sketch, "E5.0.17.47", {"center": v(434.49, -444.8) * mm, "radius": 3.18 * mm});
            skCircle(sketch, "E5.0.17.48", {"center": v(656.74, -444.8) * mm, "radius": 3.18 * mm});
            skCircle(sketch, "E5.0.17.49", {"center": v(370.99, -444.8) * mm, "radius": 3.18 * mm});
            skCircle(sketch, "E5.0.17.50", {"center": v(593.24, -444.8) * mm, "radius": 3.18 * mm});
            skCircle(sketch, "E5.0.17.51", {"center": v(847.24, -444.8) * mm, "radius": 3.18 * mm});
            skCircle(sketch, "E5.0.17.52", {"center": v(339.24, -444.8) * mm, "radius": 3.18 * mm});
            skCircle(sketch, "E5.0.17.53", {"center": v(561.49, -444.8) * mm, "radius": 3.18 * mm});
            skCircle(sketch, "E5.0.17.54", {"center": v(815.49, -444.8) * mm, "radius": 3.18 * mm});
            skCircle(sketch, "E5.0.17.55", {"center": v(307.49, -444.8) * mm, "radius": 3.18 * mm});
            skCircle(sketch, "E5.0.17.56", {"center": v(529.74, -444.8) * mm, "radius": 3.18 * mm});
            skCircle(sketch, "E5.0.17.57", {"center": v(180.49, -444.8) * mm, "radius": 3.18 * mm});
            skCircle(sketch, "E5.0.17.58", {"center": v(148.74, -444.8) * mm, "radius": 3.18 * mm});
            skCircle(sketch, "E5.0.17.59", {"center": v(910.74, -444.8) * mm, "radius": 3.18 * mm});
            skCircle(sketch, "E5.0.17.60", {"center": v(275.74, -444.8) * mm, "radius": 3.18 * mm});
            skCircle(sketch, "E5.0.17.61", {"center": v(243.99, -444.8) * mm, "radius": 3.18 * mm});
            skCircle(sketch, "E5.0.17.62", {"center": v(212.24, -444.8) * mm, "radius": 3.18 * mm});
            skCircle(sketch, "E5.0.17.63", {"center": v(783.74, -444.8) * mm, "radius": 3.18 * mm});
            skCircle(sketch, "E5.0.17.64", {"center": v(497.99, -444.8) * mm, "radius": 3.18 * mm});
            skCircle(sketch, "E5.0.17.65", {"center": v(402.74, -444.8) * mm, "radius": 3.18 * mm});
            skCircle(sketch, "E5.0.17.66", {"center": v(624.99, -444.8) * mm, "radius": 3.18 * mm});
            skCircle(sketch, "E5.0.17.67", {"center": v(751.99, -444.8) * mm, "radius": 3.18 * mm});
            skCircle(sketch, "E5.0.17.68", {"center": v(466.24, -444.8) * mm, "radius": 3.18 * mm});
            skCircle(sketch, "E5.0.17.69", {"center": v(688.49, -444.8) * mm, "radius": 3.18 * mm});
            skCircle(sketch, "E5.0.17.70", {"center": v(116.99, -444.8) * mm, "radius": 3.18 * mm});
            skCircle(sketch, "E5.0.17.71", {"center": v(85.24, -444.8) * mm, "radius": 3.18 * mm});
            skCircle(sketch, "E5.0.17.72", {"center": v(53.49, -444.8) * mm, "radius": 3.18 * mm});
            skLineSegment(sketch, "E5.0.17.73", {"start": v(-41.76, -444.8) * mm, "end": v(-10.01, -444.8) * mm, "construction": true});
            skCircle(sketch, "E5.0.17.74", {"center": v(21.74, -444.8) * mm, "radius": 3.18 * mm});
            skCircle(sketch, "E5.0.17.75", {"center": v(-10.01, -444.8) * mm, "radius": 3.18 * mm});
            skCircle(sketch, "E5.0.17.76", {"center": v(-41.76, -444.8) * mm, "radius": 3.18 * mm});
            skCircle(sketch, "E5.0.18.0", {"center": v(2244.24, -470.2) * mm, "radius": 3.18 * mm});
            skCircle(sketch, "E5.0.18.1", {"center": v(2180.74, -470.2) * mm, "radius": 3.18 * mm});
            skCircle(sketch, "E5.0.18.2", {"center": v(2339.49, -470.2) * mm, "radius": 3.18 * mm});
            skCircle(sketch, "E5.0.18.3", {"center": v(2307.74, -470.2) * mm, "radius": 3.18 * mm});
            skCircle(sketch, "E5.0.18.4", {"center": v(2275.99, -470.2) * mm, "radius": 3.18 * mm});
            skCircle(sketch, "E5.0.18.5", {"center": v(2212.49, -470.2) * mm, "radius": 3.18 * mm});
            skCircle(sketch, "E5.0.18.6", {"center": v(1958.49, -470.2) * mm, "radius": 3.18 * mm});
            skCircle(sketch, "E5.0.18.7", {"center": v(1894.99, -470.2) * mm, "radius": 3.18 * mm});
            skCircle(sketch, "E5.0.18.8", {"center": v(2117.24, -470.2) * mm, "radius": 3.18 * mm});
            skCircle(sketch, "E5.0.18.9", {"center": v(2085.49, -470.2) * mm, "radius": 3.18 * mm});
            skCircle(sketch, "E5.0.18.10", {"center": v(2053.74, -470.2) * mm, "radius": 3.18 * mm});
            skCircle(sketch, "E5.0.18.11", {"center": v(1926.74, -470.2) * mm, "radius": 3.18 * mm});
            skCircle(sketch, "E5.0.18.12", {"center": v(2021.99, -470.2) * mm, "radius": 3.18 * mm});
            skCircle(sketch, "E5.0.18.13", {"center": v(2148.99, -470.2) * mm, "radius": 3.18 * mm});
            skCircle(sketch, "E5.0.18.14", {"center": v(1990.24, -470.2) * mm, "radius": 3.18 * mm});
            skCircle(sketch, "E5.0.18.15", {"center": v(1450.49, -470.2) * mm, "radius": 3.18 * mm});
            skCircle(sketch, "E5.0.18.16", {"center": v(1228.24, -470.2) * mm, "radius": 3.18 * mm});
            skCircle(sketch, "E5.0.18.17", {"center": v(1736.24, -470.2) * mm, "radius": 3.18 * mm});
            skCircle(sketch, "E5.0.18.18", {"center": v(1386.99, -470.2) * mm, "radius": 3.18 * mm});
            skCircle(sketch, "E5.0.18.19", {"center": v(1164.74, -470.2) * mm, "radius": 3.18 * mm});
            skCircle(sketch, "E5.0.18.20", {"center": v(1672.74, -470.2) * mm, "radius": 3.18 * mm});
            skCircle(sketch, "E5.0.18.21", {"center": v(1101.24, -470.2) * mm, "radius": 3.18 * mm});
            skCircle(sketch, "E5.0.18.22", {"center": v(1609.24, -470.2) * mm, "radius": 3.18 * mm});
            skCircle(sketch, "E5.0.18.23", {"center": v(1355.24, -470.2) * mm, "radius": 3.18 * mm});
            skCircle(sketch, "E5.0.18.24", {"center": v(1863.24, -470.2) * mm, "radius": 3.18 * mm});
            skCircle(sketch, "E5.0.18.25", {"center": v(1069.49, -470.2) * mm, "radius": 3.18 * mm});
            skCircle(sketch, "E5.0.18.26", {"center": v(1577.49, -470.2) * mm, "radius": 3.18 * mm});
            skCircle(sketch, "E5.0.18.27", {"center": v(1323.49, -470.2) * mm, "radius": 3.18 * mm});
            skCircle(sketch, "E5.0.18.28", {"center": v(1831.49, -470.2) * mm, "radius": 3.18 * mm});
            skCircle(sketch, "E5.0.18.29", {"center": v(1037.74, -470.2) * mm, "radius": 3.18 * mm});
            skCircle(sketch, "E5.0.18.30", {"center": v(1545.74, -470.2) * mm, "radius": 3.18 * mm});
            skCircle(sketch, "E5.0.18.31", {"center": v(1418.74, -470.2) * mm, "radius": 3.18 * mm});
            skCircle(sketch, "E5.0.18.32", {"center": v(1005.99, -470.2) * mm, "radius": 3.18 * mm});
            skCircle(sketch, "E5.0.18.33", {"center": v(1513.99, -470.2) * mm, "radius": 3.18 * mm});
            skCircle(sketch, "E5.0.18.34", {"center": v(1799.74, -470.2) * mm, "radius": 3.18 * mm});
            skCircle(sketch, "E5.0.18.35", {"center": v(1291.74, -470.2) * mm, "radius": 3.18 * mm});
            skCircle(sketch, "E5.0.18.36", {"center": v(1132.99, -470.2) * mm, "radius": 3.18 * mm});
            skCircle(sketch, "E5.0.18.37", {"center": v(974.24, -470.2) * mm, "radius": 3.18 * mm});
            skCircle(sketch, "E5.0.18.38", {"center": v(1482.24, -470.2) * mm, "radius": 3.18 * mm});
            skCircle(sketch, "E5.0.18.39", {"center": v(1259.99, -470.2) * mm, "radius": 3.18 * mm});
            skCircle(sketch, "E5.0.18.40", {"center": v(1640.99, -470.2) * mm, "radius": 3.18 * mm});
            skCircle(sketch, "E5.0.18.41", {"center": v(1767.99, -470.2) * mm, "radius": 3.18 * mm});
            skCircle(sketch, "E5.0.18.42", {"center": v(1196.49, -470.2) * mm, "radius": 3.18 * mm});
            skCircle(sketch, "E5.0.18.43", {"center": v(1704.49, -470.2) * mm, "radius": 3.18 * mm});
            skCircle(sketch, "E5.0.18.44", {"center": v(720.24, -470.2) * mm, "radius": 3.18 * mm});
            skCircle(sketch, "E5.0.18.45", {"center": v(942.49, -470.2) * mm, "radius": 3.18 * mm});
            skCircle(sketch, "E5.0.18.46", {"center": v(878.99, -470.2) * mm, "radius": 3.18 * mm});
            skCircle(sketch, "E5.0.18.47", {"center": v(434.49, -470.2) * mm, "radius": 3.18 * mm});
            skCircle(sketch, "E5.0.18.48", {"center": v(656.74, -470.2) * mm, "radius": 3.18 * mm});
            skCircle(sketch, "E5.0.18.49", {"center": v(370.99, -470.2) * mm, "radius": 3.18 * mm});
            skCircle(sketch, "E5.0.18.50", {"center": v(593.24, -470.2) * mm, "radius": 3.18 * mm});
            skCircle(sketch, "E5.0.18.51", {"center": v(847.24, -470.2) * mm, "radius": 3.18 * mm});
            skCircle(sketch, "E5.0.18.52", {"center": v(339.24, -470.2) * mm, "radius": 3.18 * mm});
            skCircle(sketch, "E5.0.18.53", {"center": v(561.49, -470.2) * mm, "radius": 3.18 * mm});
            skCircle(sketch, "E5.0.18.54", {"center": v(815.49, -470.2) * mm, "radius": 3.18 * mm});
            skCircle(sketch, "E5.0.18.55", {"center": v(307.49, -470.2) * mm, "radius": 3.18 * mm});
            skCircle(sketch, "E5.0.18.56", {"center": v(529.74, -470.2) * mm, "radius": 3.18 * mm});
            skCircle(sketch, "E5.0.18.57", {"center": v(180.49, -470.2) * mm, "radius": 3.18 * mm});
            skCircle(sketch, "E5.0.18.58", {"center": v(148.74, -470.2) * mm, "radius": 3.18 * mm});
            skCircle(sketch, "E5.0.18.59", {"center": v(910.74, -470.2) * mm, "radius": 3.18 * mm});
            skCircle(sketch, "E5.0.18.60", {"center": v(275.74, -470.2) * mm, "radius": 3.18 * mm});
            skCircle(sketch, "E5.0.18.61", {"center": v(243.99, -470.2) * mm, "radius": 3.18 * mm});
            skCircle(sketch, "E5.0.18.62", {"center": v(212.24, -470.2) * mm, "radius": 3.18 * mm});
            skCircle(sketch, "E5.0.18.63", {"center": v(783.74, -470.2) * mm, "radius": 3.18 * mm});
            skCircle(sketch, "E5.0.18.64", {"center": v(497.99, -470.2) * mm, "radius": 3.18 * mm});
            skCircle(sketch, "E5.0.18.65", {"center": v(402.74, -470.2) * mm, "radius": 3.18 * mm});
            skCircle(sketch, "E5.0.18.66", {"center": v(624.99, -470.2) * mm, "radius": 3.18 * mm});
            skCircle(sketch, "E5.0.18.67", {"center": v(751.99, -470.2) * mm, "radius": 3.18 * mm});
            skCircle(sketch, "E5.0.18.68", {"center": v(466.24, -470.2) * mm, "radius": 3.18 * mm});
            skCircle(sketch, "E5.0.18.69", {"center": v(688.49, -470.2) * mm, "radius": 3.18 * mm});
            skCircle(sketch, "E5.0.18.70", {"center": v(116.99, -470.2) * mm, "radius": 3.18 * mm});
            skCircle(sketch, "E5.0.18.71", {"center": v(85.24, -470.2) * mm, "radius": 3.18 * mm});
            skCircle(sketch, "E5.0.18.72", {"center": v(53.49, -470.2) * mm, "radius": 3.18 * mm});
            skLineSegment(sketch, "E5.0.18.73", {"start": v(-41.76, -470.2) * mm, "end": v(-10.01, -470.2) * mm, "construction": true});
            skCircle(sketch, "E5.0.18.74", {"center": v(21.74, -470.2) * mm, "radius": 3.18 * mm});
            skCircle(sketch, "E5.0.18.75", {"center": v(-10.01, -470.2) * mm, "radius": 3.18 * mm});
            skCircle(sketch, "E5.0.18.76", {"center": v(-41.76, -470.2) * mm, "radius": 3.18 * mm});
            skCircle(sketch, "E5.0.19.0", {"center": v(2244.24, -495.6) * mm, "radius": 3.18 * mm});
            skCircle(sketch, "E5.0.19.1", {"center": v(2180.74, -495.6) * mm, "radius": 3.18 * mm});
            skCircle(sketch, "E5.0.19.2", {"center": v(2339.49, -495.6) * mm, "radius": 3.18 * mm});
            skCircle(sketch, "E5.0.19.3", {"center": v(2307.74, -495.6) * mm, "radius": 3.18 * mm});
            skCircle(sketch, "E5.0.19.4", {"center": v(2275.99, -495.6) * mm, "radius": 3.18 * mm});
            skCircle(sketch, "E5.0.19.5", {"center": v(2212.49, -495.6) * mm, "radius": 3.18 * mm});
            skCircle(sketch, "E5.0.19.6", {"center": v(1958.49, -495.6) * mm, "radius": 3.18 * mm});
            skCircle(sketch, "E5.0.19.7", {"center": v(1894.99, -495.6) * mm, "radius": 3.18 * mm});
            skCircle(sketch, "E5.0.19.8", {"center": v(2117.24, -495.6) * mm, "radius": 3.18 * mm});
            skCircle(sketch, "E5.0.19.9", {"center": v(2085.49, -495.6) * mm, "radius": 3.18 * mm});
            skCircle(sketch, "E5.0.19.10", {"center": v(2053.74, -495.6) * mm, "radius": 3.18 * mm});
            skCircle(sketch, "E5.0.19.11", {"center": v(1926.74, -495.6) * mm, "radius": 3.18 * mm});
            skCircle(sketch, "E5.0.19.12", {"center": v(2021.99, -495.6) * mm, "radius": 3.18 * mm});
            skCircle(sketch, "E5.0.19.13", {"center": v(2148.99, -495.6) * mm, "radius": 3.18 * mm});
            skCircle(sketch, "E5.0.19.14", {"center": v(1990.24, -495.6) * mm, "radius": 3.18 * mm});
            skCircle(sketch, "E5.0.19.15", {"center": v(1450.49, -495.6) * mm, "radius": 3.18 * mm});
            skCircle(sketch, "E5.0.19.16", {"center": v(1228.24, -495.6) * mm, "radius": 3.18 * mm});
            skCircle(sketch, "E5.0.19.17", {"center": v(1736.24, -495.6) * mm, "radius": 3.18 * mm});
            skCircle(sketch, "E5.0.19.18", {"center": v(1386.99, -495.6) * mm, "radius": 3.18 * mm});
            skCircle(sketch, "E5.0.19.19", {"center": v(1164.74, -495.6) * mm, "radius": 3.18 * mm});
            skCircle(sketch, "E5.0.19.20", {"center": v(1672.74, -495.6) * mm, "radius": 3.18 * mm});
            skCircle(sketch, "E5.0.19.21", {"center": v(1101.24, -495.6) * mm, "radius": 3.18 * mm});
            skCircle(sketch, "E5.0.19.22", {"center": v(1609.24, -495.6) * mm, "radius": 3.18 * mm});
            skCircle(sketch, "E5.0.19.23", {"center": v(1355.24, -495.6) * mm, "radius": 3.18 * mm});
            skCircle(sketch, "E5.0.19.24", {"center": v(1863.24, -495.6) * mm, "radius": 3.18 * mm});
            skCircle(sketch, "E5.0.19.25", {"center": v(1069.49, -495.6) * mm, "radius": 3.18 * mm});
            skCircle(sketch, "E5.0.19.26", {"center": v(1577.49, -495.6) * mm, "radius": 3.18 * mm});
            skCircle(sketch, "E5.0.19.27", {"center": v(1323.49, -495.6) * mm, "radius": 3.18 * mm});
            skCircle(sketch, "E5.0.19.28", {"center": v(1831.49, -495.6) * mm, "radius": 3.18 * mm});
            skCircle(sketch, "E5.0.19.29", {"center": v(1037.74, -495.6) * mm, "radius": 3.18 * mm});
            skCircle(sketch, "E5.0.19.30", {"center": v(1545.74, -495.6) * mm, "radius": 3.18 * mm});
            skCircle(sketch, "E5.0.19.31", {"center": v(1418.74, -495.6) * mm, "radius": 3.18 * mm});
            skCircle(sketch, "E5.0.19.32", {"center": v(1005.99, -495.6) * mm, "radius": 3.18 * mm});
            skCircle(sketch, "E5.0.19.33", {"center": v(1513.99, -495.6) * mm, "radius": 3.18 * mm});
            skCircle(sketch, "E5.0.19.34", {"center": v(1799.74, -495.6) * mm, "radius": 3.18 * mm});
            skCircle(sketch, "E5.0.19.35", {"center": v(1291.74, -495.6) * mm, "radius": 3.18 * mm});
            skCircle(sketch, "E5.0.19.36", {"center": v(1132.99, -495.6) * mm, "radius": 3.18 * mm});
            skCircle(sketch, "E5.0.19.37", {"center": v(974.24, -495.6) * mm, "radius": 3.18 * mm});
            skCircle(sketch, "E5.0.19.38", {"center": v(1482.24, -495.6) * mm, "radius": 3.18 * mm});
            skCircle(sketch, "E5.0.19.39", {"center": v(1259.99, -495.6) * mm, "radius": 3.18 * mm});
            skCircle(sketch, "E5.0.19.40", {"center": v(1640.99, -495.6) * mm, "radius": 3.18 * mm});
            skCircle(sketch, "E5.0.19.41", {"center": v(1767.99, -495.6) * mm, "radius": 3.18 * mm});
            skCircle(sketch, "E5.0.19.42", {"center": v(1196.49, -495.6) * mm, "radius": 3.18 * mm});
            skCircle(sketch, "E5.0.19.43", {"center": v(1704.49, -495.6) * mm, "radius": 3.18 * mm});
            skCircle(sketch, "E5.0.19.44", {"center": v(720.24, -495.6) * mm, "radius": 3.18 * mm});
            skCircle(sketch, "E5.0.19.45", {"center": v(942.49, -495.6) * mm, "radius": 3.18 * mm});
            skCircle(sketch, "E5.0.19.46", {"center": v(878.99, -495.6) * mm, "radius": 3.18 * mm});
            skCircle(sketch, "E5.0.19.47", {"center": v(434.49, -495.6) * mm, "radius": 3.18 * mm});
            skCircle(sketch, "E5.0.19.48", {"center": v(656.74, -495.6) * mm, "radius": 3.18 * mm});
            skCircle(sketch, "E5.0.19.49", {"center": v(370.99, -495.6) * mm, "radius": 3.18 * mm});
            skCircle(sketch, "E5.0.19.50", {"center": v(593.24, -495.6) * mm, "radius": 3.18 * mm});
            skCircle(sketch, "E5.0.19.51", {"center": v(847.24, -495.6) * mm, "radius": 3.18 * mm});
            skCircle(sketch, "E5.0.19.52", {"center": v(339.24, -495.6) * mm, "radius": 3.18 * mm});
            skCircle(sketch, "E5.0.19.53", {"center": v(561.49, -495.6) * mm, "radius": 3.18 * mm});
            skCircle(sketch, "E5.0.19.54", {"center": v(815.49, -495.6) * mm, "radius": 3.18 * mm});
            skCircle(sketch, "E5.0.19.55", {"center": v(307.49, -495.6) * mm, "radius": 3.18 * mm});
            skCircle(sketch, "E5.0.19.56", {"center": v(529.74, -495.6) * mm, "radius": 3.18 * mm});
            skCircle(sketch, "E5.0.19.57", {"center": v(180.49, -495.6) * mm, "radius": 3.18 * mm});
            skCircle(sketch, "E5.0.19.58", {"center": v(148.74, -495.6) * mm, "radius": 3.18 * mm});
            skCircle(sketch, "E5.0.19.59", {"center": v(910.74, -495.6) * mm, "radius": 3.18 * mm});
            skCircle(sketch, "E5.0.19.60", {"center": v(275.74, -495.6) * mm, "radius": 3.18 * mm});
            skCircle(sketch, "E5.0.19.61", {"center": v(243.99, -495.6) * mm, "radius": 3.18 * mm});
            skCircle(sketch, "E5.0.19.62", {"center": v(212.24, -495.6) * mm, "radius": 3.18 * mm});
            skCircle(sketch, "E5.0.19.63", {"center": v(783.74, -495.6) * mm, "radius": 3.18 * mm});
            skCircle(sketch, "E5.0.19.64", {"center": v(497.99, -495.6) * mm, "radius": 3.18 * mm});
            skCircle(sketch, "E5.0.19.65", {"center": v(402.74, -495.6) * mm, "radius": 3.18 * mm});
            skCircle(sketch, "E5.0.19.66", {"center": v(624.99, -495.6) * mm, "radius": 3.18 * mm});
            skCircle(sketch, "E5.0.19.67", {"center": v(751.99, -495.6) * mm, "radius": 3.18 * mm});
            skCircle(sketch, "E5.0.19.68", {"center": v(466.24, -495.6) * mm, "radius": 3.18 * mm});
            skCircle(sketch, "E5.0.19.69", {"center": v(688.49, -495.6) * mm, "radius": 3.18 * mm});
            skCircle(sketch, "E5.0.19.70", {"center": v(116.99, -495.6) * mm, "radius": 3.18 * mm});
            skCircle(sketch, "E5.0.19.71", {"center": v(85.24, -495.6) * mm, "radius": 3.18 * mm});
            skCircle(sketch, "E5.0.19.72", {"center": v(53.49, -495.6) * mm, "radius": 3.18 * mm});
            skLineSegment(sketch, "E5.0.19.73", {"start": v(-41.76, -495.6) * mm, "end": v(-10.01, -495.6) * mm, "construction": true});
            skCircle(sketch, "E5.0.19.74", {"center": v(21.74, -495.6) * mm, "radius": 3.18 * mm});
            skCircle(sketch, "E5.0.19.75", {"center": v(-10.01, -495.6) * mm, "radius": 3.18 * mm});
            skCircle(sketch, "E5.0.19.76", {"center": v(-41.76, -495.6) * mm, "radius": 3.18 * mm});
            skLineSegment(sketch, "E5.direction1", {"start": v(-41.76, -13) * mm, "end": v(-16.36, -13) * mm, "construction": true});
            skLineSegment(sketch, "E5.direction2", {"start": v(-41.76, -13) * mm, "end": v(-41.76, -38.4) * mm, "construction": true});
            skCircle(sketch, "E6.0.0.20", {"center": v(2244.24, -521) * mm, "radius": 3.18 * mm});
            skCircle(sketch, "E6.2.0.20", {"center": v(2180.74, -521) * mm, "radius": 3.18 * mm});
            skCircle(sketch, "E6.4.0.20", {"center": v(2339.49, -521) * mm, "radius": 3.18 * mm});
            skCircle(sketch, "E6.6.0.20", {"center": v(2307.74, -521) * mm, "radius": 3.18 * mm});
            skCircle(sketch, "E6.8.0.20", {"center": v(2275.99, -521) * mm, "radius": 3.18 * mm});
            skCircle(sketch, "E6.10.0.20", {"center": v(2212.49, -521) * mm, "radius": 3.18 * mm});
            skCircle(sketch, "E6.12.0.20", {"center": v(1958.49, -521) * mm, "radius": 3.18 * mm});
            skCircle(sketch, "E6.14.0.20", {"center": v(1894.99, -521) * mm, "radius": 3.18 * mm});
            skCircle(sketch, "E6.16.0.20", {"center": v(2117.24, -521) * mm, "radius": 3.18 * mm});
            skCircle(sketch, "E6.18.0.20", {"center": v(2085.49, -521) * mm, "radius": 3.18 * mm});
            skCircle(sketch, "E6.20.0.20", {"center": v(2053.74, -521) * mm, "radius": 3.18 * mm});
            skCircle(sketch, "E6.22.0.20", {"center": v(1926.74, -521) * mm, "radius": 3.18 * mm});
            skCircle(sketch, "E6.24.0.20", {"center": v(2021.99, -521) * mm, "radius": 3.18 * mm});
            skCircle(sketch, "E6.26.0.20", {"center": v(2148.99, -521) * mm, "radius": 3.18 * mm});
            skCircle(sketch, "E6.28.0.20", {"center": v(1990.24, -521) * mm, "radius": 3.18 * mm});
            skCircle(sketch, "E6.30.0.20", {"center": v(1450.49, -521) * mm, "radius": 3.18 * mm});
            skCircle(sketch, "E6.32.0.20", {"center": v(1228.24, -521) * mm, "radius": 3.18 * mm});
            skCircle(sketch, "E6.34.0.20", {"center": v(1736.24, -521) * mm, "radius": 3.18 * mm});
            skCircle(sketch, "E6.36.0.20", {"center": v(1386.99, -521) * mm, "radius": 3.18 * mm});
            skCircle(sketch, "E6.38.0.20", {"center": v(1164.74, -521) * mm, "radius": 3.18 * mm});
            skCircle(sketch, "E6.40.0.20", {"center": v(1672.74, -521) * mm, "radius": 3.18 * mm});
            skCircle(sketch, "E6.42.0.20", {"center": v(1101.24, -521) * mm, "radius": 3.18 * mm});
            skCircle(sketch, "E6.44.0.20", {"center": v(1609.24, -521) * mm, "radius": 3.18 * mm});
            skCircle(sketch, "E6.46.0.20", {"center": v(1355.24, -521) * mm, "radius": 3.18 * mm});
            skCircle(sketch, "E6.48.0.20", {"center": v(1863.24, -521) * mm, "radius": 3.18 * mm});
            skCircle(sketch, "E6.50.0.20", {"center": v(1069.49, -521) * mm, "radius": 3.18 * mm});
            skCircle(sketch, "E6.52.0.20", {"center": v(1577.49, -521) * mm, "radius": 3.18 * mm});
            skCircle(sketch, "E6.54.0.20", {"center": v(1323.49, -521) * mm, "radius": 3.18 * mm});
            skCircle(sketch, "E6.56.0.20", {"center": v(1831.49, -521) * mm, "radius": 3.18 * mm});
            skCircle(sketch, "E6.58.0.20", {"center": v(1037.74, -521) * mm, "radius": 3.18 * mm});
            skCircle(sketch, "E6.60.0.20", {"center": v(1545.74, -521) * mm, "radius": 3.18 * mm});
            skCircle(sketch, "E6.62.0.20", {"center": v(1418.74, -521) * mm, "radius": 3.18 * mm});
            skCircle(sketch, "E6.64.0.20", {"center": v(1005.99, -521) * mm, "radius": 3.18 * mm});
            skCircle(sketch, "E6.66.0.20", {"center": v(1513.99, -521) * mm, "radius": 3.18 * mm});
            skCircle(sketch, "E6.68.0.20", {"center": v(1799.74, -521) * mm, "radius": 3.18 * mm});
            skCircle(sketch, "E6.70.0.20", {"center": v(1291.74, -521) * mm, "radius": 3.18 * mm});
            skCircle(sketch, "E6.72.0.20", {"center": v(1132.99, -521) * mm, "radius": 3.18 * mm});
            skCircle(sketch, "E6.74.0.20", {"center": v(974.24, -521) * mm, "radius": 3.18 * mm});
            skCircle(sketch, "E6.76.0.20", {"center": v(1482.24, -521) * mm, "radius": 3.18 * mm});
            skCircle(sketch, "E6.78.0.20", {"center": v(1259.99, -521) * mm, "radius": 3.18 * mm});
            skCircle(sketch, "E6.80.0.20", {"center": v(1640.99, -521) * mm, "radius": 3.18 * mm});
            skCircle(sketch, "E6.82.0.20", {"center": v(1767.99, -521) * mm, "radius": 3.18 * mm});
            skCircle(sketch, "E6.84.0.20", {"center": v(1196.49, -521) * mm, "radius": 3.18 * mm});
            skCircle(sketch, "E6.86.0.20", {"center": v(1704.49, -521) * mm, "radius": 3.18 * mm});
            skCircle(sketch, "E6.88.0.20", {"center": v(720.24, -521) * mm, "radius": 3.18 * mm});
            skCircle(sketch, "E6.90.0.20", {"center": v(942.49, -521) * mm, "radius": 3.18 * mm});
            skCircle(sketch, "E6.92.0.20", {"center": v(878.99, -521) * mm, "radius": 3.18 * mm});
            skCircle(sketch, "E6.94.0.20", {"center": v(434.49, -521) * mm, "radius": 3.18 * mm});
            skCircle(sketch, "E6.96.0.20", {"center": v(656.74, -521) * mm, "radius": 3.18 * mm});
            skCircle(sketch, "E6.98.0.20", {"center": v(370.99, -521) * mm, "radius": 3.18 * mm});
            skCircle(sketch, "E6.100.0.20", {"center": v(593.24, -521) * mm, "radius": 3.18 * mm});
            skCircle(sketch, "E6.102.0.20", {"center": v(847.24, -521) * mm, "radius": 3.18 * mm});
            skCircle(sketch, "E6.104.0.20", {"center": v(339.24, -521) * mm, "radius": 3.18 * mm});
            skCircle(sketch, "E6.106.0.20", {"center": v(561.49, -521) * mm, "radius": 3.18 * mm});
            skCircle(sketch, "E6.108.0.20", {"center": v(815.49, -521) * mm, "radius": 3.18 * mm});
            skCircle(sketch, "E6.110.0.20", {"center": v(307.49, -521) * mm, "radius": 3.18 * mm});
            skCircle(sketch, "E6.112.0.20", {"center": v(529.74, -521) * mm, "radius": 3.18 * mm});
            skCircle(sketch, "E6.114.0.20", {"center": v(180.49, -521) * mm, "radius": 3.18 * mm});
            skCircle(sketch, "E6.116.0.20", {"center": v(148.74, -521) * mm, "radius": 3.18 * mm});
            skCircle(sketch, "E6.118.0.20", {"center": v(910.74, -521) * mm, "radius": 3.18 * mm});
            skCircle(sketch, "E6.120.0.20", {"center": v(275.74, -521) * mm, "radius": 3.18 * mm});
            skCircle(sketch, "E6.122.0.20", {"center": v(243.99, -521) * mm, "radius": 3.18 * mm});
            skCircle(sketch, "E6.124.0.20", {"center": v(212.24, -521) * mm, "radius": 3.18 * mm});
            skCircle(sketch, "E6.126.0.20", {"center": v(783.74, -521) * mm, "radius": 3.18 * mm});
            skCircle(sketch, "E6.128.0.20", {"center": v(497.99, -521) * mm, "radius": 3.18 * mm});
            skCircle(sketch, "E6.130.0.20", {"center": v(402.74, -521) * mm, "radius": 3.18 * mm});
            skCircle(sketch, "E6.132.0.20", {"center": v(624.99, -521) * mm, "radius": 3.18 * mm});
            skCircle(sketch, "E6.134.0.20", {"center": v(751.99, -521) * mm, "radius": 3.18 * mm});
            skCircle(sketch, "E6.136.0.20", {"center": v(466.24, -521) * mm, "radius": 3.18 * mm});
            skCircle(sketch, "E6.138.0.20", {"center": v(688.49, -521) * mm, "radius": 3.18 * mm});
            skCircle(sketch, "E6.140.0.20", {"center": v(116.99, -521) * mm, "radius": 3.18 * mm});
            skCircle(sketch, "E6.142.0.20", {"center": v(85.24, -521) * mm, "radius": 3.18 * mm});
            skCircle(sketch, "E6.144.0.20", {"center": v(53.49, -521) * mm, "radius": 3.18 * mm});
            skLineSegment(sketch, "E6.146.0.20", {"start": v(-41.76, -521) * mm, "end": v(-10.01, -521) * mm, "construction": true});
            skCircle(sketch, "E6.149.0.20", {"center": v(21.74, -521) * mm, "radius": 3.18 * mm});
            skCircle(sketch, "E6.151.0.20", {"center": v(-10.01, -521) * mm, "radius": 3.18 * mm});
            skCircle(sketch, "E6.153.0.20", {"center": v(-41.76, -521) * mm, "radius": 3.18 * mm});
            skCircle(sketch, "E6.0.0.21", {"center": v(2244.24, -546.4) * mm, "radius": 3.18 * mm});
            skCircle(sketch, "E6.2.0.21", {"center": v(2180.74, -546.4) * mm, "radius": 3.18 * mm});
            skCircle(sketch, "E6.4.0.21", {"center": v(2339.49, -546.4) * mm, "radius": 3.18 * mm});
            skCircle(sketch, "E6.6.0.21", {"center": v(2307.74, -546.4) * mm, "radius": 3.18 * mm});
            skCircle(sketch, "E6.8.0.21", {"center": v(2275.99, -546.4) * mm, "radius": 3.18 * mm});
            skCircle(sketch, "E6.10.0.21", {"center": v(2212.49, -546.4) * mm, "radius": 3.18 * mm});
            skCircle(sketch, "E6.12.0.21", {"center": v(1958.49, -546.4) * mm, "radius": 3.18 * mm});
            skCircle(sketch, "E6.14.0.21", {"center": v(1894.99, -546.4) * mm, "radius": 3.18 * mm});
            skCircle(sketch, "E6.16.0.21", {"center": v(2117.24, -546.4) * mm, "radius": 3.18 * mm});
            skCircle(sketch, "E6.18.0.21", {"center": v(2085.49, -546.4) * mm, "radius": 3.18 * mm});
            skCircle(sketch, "E6.20.0.21", {"center": v(2053.74, -546.4) * mm, "radius": 3.18 * mm});
            skCircle(sketch, "E6.22.0.21", {"center": v(1926.74, -546.4) * mm, "radius": 3.18 * mm});
            skCircle(sketch, "E6.24.0.21", {"center": v(2021.99, -546.4) * mm, "radius": 3.18 * mm});
            skCircle(sketch, "E6.26.0.21", {"center": v(2148.99, -546.4) * mm, "radius": 3.18 * mm});
            skCircle(sketch, "E6.28.0.21", {"center": v(1990.24, -546.4) * mm, "radius": 3.18 * mm});
            skCircle(sketch, "E6.30.0.21", {"center": v(1450.49, -546.4) * mm, "radius": 3.18 * mm});
            skCircle(sketch, "E6.32.0.21", {"center": v(1228.24, -546.4) * mm, "radius": 3.18 * mm});
            skCircle(sketch, "E6.34.0.21", {"center": v(1736.24, -546.4) * mm, "radius": 3.18 * mm});
            skCircle(sketch, "E6.36.0.21", {"center": v(1386.99, -546.4) * mm, "radius": 3.18 * mm});
            skCircle(sketch, "E6.38.0.21", {"center": v(1164.74, -546.4) * mm, "radius": 3.18 * mm});
            skCircle(sketch, "E6.40.0.21", {"center": v(1672.74, -546.4) * mm, "radius": 3.18 * mm});
            skCircle(sketch, "E6.42.0.21", {"center": v(1101.24, -546.4) * mm, "radius": 3.18 * mm});
            skCircle(sketch, "E6.44.0.21", {"center": v(1609.24, -546.4) * mm, "radius": 3.18 * mm});
            skCircle(sketch, "E6.46.0.21", {"center": v(1355.24, -546.4) * mm, "radius": 3.18 * mm});
            skCircle(sketch, "E6.48.0.21", {"center": v(1863.24, -546.4) * mm, "radius": 3.18 * mm});
            skCircle(sketch, "E6.50.0.21", {"center": v(1069.49, -546.4) * mm, "radius": 3.18 * mm});
            skCircle(sketch, "E6.52.0.21", {"center": v(1577.49, -546.4) * mm, "radius": 3.18 * mm});
            skCircle(sketch, "E6.54.0.21", {"center": v(1323.49, -546.4) * mm, "radius": 3.18 * mm});
            skCircle(sketch, "E6.56.0.21", {"center": v(1831.49, -546.4) * mm, "radius": 3.18 * mm});
            skCircle(sketch, "E6.58.0.21", {"center": v(1037.74, -546.4) * mm, "radius": 3.18 * mm});
            skCircle(sketch, "E6.60.0.21", {"center": v(1545.74, -546.4) * mm, "radius": 3.18 * mm});
            skCircle(sketch, "E6.62.0.21", {"center": v(1418.74, -546.4) * mm, "radius": 3.18 * mm});
            skCircle(sketch, "E6.64.0.21", {"center": v(1005.99, -546.4) * mm, "radius": 3.18 * mm});
            skCircle(sketch, "E6.66.0.21", {"center": v(1513.99, -546.4) * mm, "radius": 3.18 * mm});
            skCircle(sketch, "E6.68.0.21", {"center": v(1799.74, -546.4) * mm, "radius": 3.18 * mm});
            skCircle(sketch, "E6.70.0.21", {"center": v(1291.74, -546.4) * mm, "radius": 3.18 * mm});
            skCircle(sketch, "E6.72.0.21", {"center": v(1132.99, -546.4) * mm, "radius": 3.18 * mm});
            skCircle(sketch, "E6.74.0.21", {"center": v(974.24, -546.4) * mm, "radius": 3.18 * mm});
            skCircle(sketch, "E6.76.0.21", {"center": v(1482.24, -546.4) * mm, "radius": 3.18 * mm});
            skCircle(sketch, "E6.78.0.21", {"center": v(1259.99, -546.4) * mm, "radius": 3.18 * mm});
            skCircle(sketch, "E6.80.0.21", {"center": v(1640.99, -546.4) * mm, "radius": 3.18 * mm});
            skCircle(sketch, "E6.82.0.21", {"center": v(1767.99, -546.4) * mm, "radius": 3.18 * mm});
            skCircle(sketch, "E6.84.0.21", {"center": v(1196.49, -546.4) * mm, "radius": 3.18 * mm});
            skCircle(sketch, "E6.86.0.21", {"center": v(1704.49, -546.4) * mm, "radius": 3.18 * mm});
            skCircle(sketch, "E6.88.0.21", {"center": v(720.24, -546.4) * mm, "radius": 3.18 * mm});
            skCircle(sketch, "E6.90.0.21", {"center": v(942.49, -546.4) * mm, "radius": 3.18 * mm});
            skCircle(sketch, "E6.92.0.21", {"center": v(878.99, -546.4) * mm, "radius": 3.18 * mm});
            skCircle(sketch, "E6.94.0.21", {"center": v(434.49, -546.4) * mm, "radius": 3.18 * mm});
            skCircle(sketch, "E6.96.0.21", {"center": v(656.74, -546.4) * mm, "radius": 3.18 * mm});
            skCircle(sketch, "E6.98.0.21", {"center": v(370.99, -546.4) * mm, "radius": 3.18 * mm});
            skCircle(sketch, "E6.100.0.21", {"center": v(593.24, -546.4) * mm, "radius": 3.18 * mm});
            skCircle(sketch, "E6.102.0.21", {"center": v(847.24, -546.4) * mm, "radius": 3.18 * mm});
            skCircle(sketch, "E6.104.0.21", {"center": v(339.24, -546.4) * mm, "radius": 3.18 * mm});
            skCircle(sketch, "E6.106.0.21", {"center": v(561.49, -546.4) * mm, "radius": 3.18 * mm});
            skCircle(sketch, "E6.108.0.21", {"center": v(815.49, -546.4) * mm, "radius": 3.18 * mm});
            skCircle(sketch, "E6.110.0.21", {"center": v(307.49, -546.4) * mm, "radius": 3.18 * mm});
            skCircle(sketch, "E6.112.0.21", {"center": v(529.74, -546.4) * mm, "radius": 3.18 * mm});
            skCircle(sketch, "E6.114.0.21", {"center": v(180.49, -546.4) * mm, "radius": 3.18 * mm});
            skCircle(sketch, "E6.116.0.21", {"center": v(148.74, -546.4) * mm, "radius": 3.18 * mm});
            skCircle(sketch, "E6.118.0.21", {"center": v(910.74, -546.4) * mm, "radius": 3.18 * mm});
            skCircle(sketch, "E6.120.0.21", {"center": v(275.74, -546.4) * mm, "radius": 3.18 * mm});
            skCircle(sketch, "E6.122.0.21", {"center": v(243.99, -546.4) * mm, "radius": 3.18 * mm});
            skCircle(sketch, "E6.124.0.21", {"center": v(212.24, -546.4) * mm, "radius": 3.18 * mm});
            skCircle(sketch, "E6.126.0.21", {"center": v(783.74, -546.4) * mm, "radius": 3.18 * mm});
            skCircle(sketch, "E6.128.0.21", {"center": v(497.99, -546.4) * mm, "radius": 3.18 * mm});
            skCircle(sketch, "E6.130.0.21", {"center": v(402.74, -546.4) * mm, "radius": 3.18 * mm});
            skCircle(sketch, "E6.132.0.21", {"center": v(624.99, -546.4) * mm, "radius": 3.18 * mm});
            skCircle(sketch, "E6.134.0.21", {"center": v(751.99, -546.4) * mm, "radius": 3.18 * mm});
            skCircle(sketch, "E6.136.0.21", {"center": v(466.24, -546.4) * mm, "radius": 3.18 * mm});
            skCircle(sketch, "E6.138.0.21", {"center": v(688.49, -546.4) * mm, "radius": 3.18 * mm});
            skCircle(sketch, "E6.140.0.21", {"center": v(116.99, -546.4) * mm, "radius": 3.18 * mm});
            skCircle(sketch, "E6.142.0.21", {"center": v(85.24, -546.4) * mm, "radius": 3.18 * mm});
            skCircle(sketch, "E6.144.0.21", {"center": v(53.49, -546.4) * mm, "radius": 3.18 * mm});
            skLineSegment(sketch, "E6.146.0.21", {"start": v(-41.76, -546.4) * mm, "end": v(-10.01, -546.4) * mm, "construction": true});
            skCircle(sketch, "E6.149.0.21", {"center": v(21.74, -546.4) * mm, "radius": 3.18 * mm});
            skCircle(sketch, "E6.151.0.21", {"center": v(-10.01, -546.4) * mm, "radius": 3.18 * mm});
            skCircle(sketch, "E6.153.0.21", {"center": v(-41.76, -546.4) * mm, "radius": 3.18 * mm});
            skCircle(sketch, "E6.0.0.22", {"center": v(2244.24, -571.8) * mm, "radius": 3.18 * mm});
            skCircle(sketch, "E6.2.0.22", {"center": v(2180.74, -571.8) * mm, "radius": 3.18 * mm});
            skCircle(sketch, "E6.4.0.22", {"center": v(2339.49, -571.8) * mm, "radius": 3.18 * mm});
            skCircle(sketch, "E6.6.0.22", {"center": v(2307.74, -571.8) * mm, "radius": 3.18 * mm});
            skCircle(sketch, "E6.8.0.22", {"center": v(2275.99, -571.8) * mm, "radius": 3.18 * mm});
            skCircle(sketch, "E6.10.0.22", {"center": v(2212.49, -571.8) * mm, "radius": 3.18 * mm});
            skCircle(sketch, "E6.12.0.22", {"center": v(1958.49, -571.8) * mm, "radius": 3.18 * mm});
            skCircle(sketch, "E6.14.0.22", {"center": v(1894.99, -571.8) * mm, "radius": 3.18 * mm});
            skCircle(sketch, "E6.16.0.22", {"center": v(2117.24, -571.8) * mm, "radius": 3.18 * mm});
            skCircle(sketch, "E6.18.0.22", {"center": v(2085.49, -571.8) * mm, "radius": 3.18 * mm});
            skCircle(sketch, "E6.20.0.22", {"center": v(2053.74, -571.8) * mm, "radius": 3.18 * mm});
            skCircle(sketch, "E6.22.0.22", {"center": v(1926.74, -571.8) * mm, "radius": 3.18 * mm});
            skCircle(sketch, "E6.24.0.22", {"center": v(2021.99, -571.8) * mm, "radius": 3.18 * mm});
            skCircle(sketch, "E6.26.0.22", {"center": v(2148.99, -571.8) * mm, "radius": 3.18 * mm});
            skCircle(sketch, "E6.28.0.22", {"center": v(1990.24, -571.8) * mm, "radius": 3.18 * mm});
            skCircle(sketch, "E6.30.0.22", {"center": v(1450.49, -571.8) * mm, "radius": 3.18 * mm});
            skCircle(sketch, "E6.32.0.22", {"center": v(1228.24, -571.8) * mm, "radius": 3.18 * mm});
            skCircle(sketch, "E6.34.0.22", {"center": v(1736.24, -571.8) * mm, "radius": 3.18 * mm});
            skCircle(sketch, "E6.36.0.22", {"center": v(1386.99, -571.8) * mm, "radius": 3.18 * mm});
            skCircle(sketch, "E6.38.0.22", {"center": v(1164.74, -571.8) * mm, "radius": 3.18 * mm});
            skCircle(sketch, "E6.40.0.22", {"center": v(1672.74, -571.8) * mm, "radius": 3.18 * mm});
            skCircle(sketch, "E6.42.0.22", {"center": v(1101.24, -571.8) * mm, "radius": 3.18 * mm});
            skCircle(sketch, "E6.44.0.22", {"center": v(1609.24, -571.8) * mm, "radius": 3.18 * mm});
            skCircle(sketch, "E6.46.0.22", {"center": v(1355.24, -571.8) * mm, "radius": 3.18 * mm});
            skCircle(sketch, "E6.48.0.22", {"center": v(1863.24, -571.8) * mm, "radius": 3.18 * mm});
            skCircle(sketch, "E6.50.0.22", {"center": v(1069.49, -571.8) * mm, "radius": 3.18 * mm});
            skCircle(sketch, "E6.52.0.22", {"center": v(1577.49, -571.8) * mm, "radius": 3.18 * mm});
            skCircle(sketch, "E6.54.0.22", {"center": v(1323.49, -571.8) * mm, "radius": 3.18 * mm});
            skCircle(sketch, "E6.56.0.22", {"center": v(1831.49, -571.8) * mm, "radius": 3.18 * mm});
            skCircle(sketch, "E6.58.0.22", {"center": v(1037.74, -571.8) * mm, "radius": 3.18 * mm});
            skCircle(sketch, "E6.60.0.22", {"center": v(1545.74, -571.8) * mm, "radius": 3.18 * mm});
            skCircle(sketch, "E6.62.0.22", {"center": v(1418.74, -571.8) * mm, "radius": 3.18 * mm});
            skCircle(sketch, "E6.64.0.22", {"center": v(1005.99, -571.8) * mm, "radius": 3.18 * mm});
            skCircle(sketch, "E6.66.0.22", {"center": v(1513.99, -571.8) * mm, "radius": 3.18 * mm});
            skCircle(sketch, "E6.68.0.22", {"center": v(1799.74, -571.8) * mm, "radius": 3.18 * mm});
            skCircle(sketch, "E6.70.0.22", {"center": v(1291.74, -571.8) * mm, "radius": 3.18 * mm});
            skCircle(sketch, "E6.72.0.22", {"center": v(1132.99, -571.8) * mm, "radius": 3.18 * mm});
            skCircle(sketch, "E6.74.0.22", {"center": v(974.24, -571.8) * mm, "radius": 3.18 * mm});
            skCircle(sketch, "E6.76.0.22", {"center": v(1482.24, -571.8) * mm, "radius": 3.18 * mm});
            skCircle(sketch, "E6.78.0.22", {"center": v(1259.99, -571.8) * mm, "radius": 3.18 * mm});
            skCircle(sketch, "E6.80.0.22", {"center": v(1640.99, -571.8) * mm, "radius": 3.18 * mm});
            skCircle(sketch, "E6.82.0.22", {"center": v(1767.99, -571.8) * mm, "radius": 3.18 * mm});
            skCircle(sketch, "E6.84.0.22", {"center": v(1196.49, -571.8) * mm, "radius": 3.18 * mm});
            skCircle(sketch, "E6.86.0.22", {"center": v(1704.49, -571.8) * mm, "radius": 3.18 * mm});
            skCircle(sketch, "E6.88.0.22", {"center": v(720.24, -571.8) * mm, "radius": 3.18 * mm});
            skCircle(sketch, "E6.90.0.22", {"center": v(942.49, -571.8) * mm, "radius": 3.18 * mm});
            skCircle(sketch, "E6.92.0.22", {"center": v(878.99, -571.8) * mm, "radius": 3.18 * mm});
            skCircle(sketch, "E6.94.0.22", {"center": v(434.49, -571.8) * mm, "radius": 3.18 * mm});
            skCircle(sketch, "E6.96.0.22", {"center": v(656.74, -571.8) * mm, "radius": 3.18 * mm});
            skCircle(sketch, "E6.98.0.22", {"center": v(370.99, -571.8) * mm, "radius": 3.18 * mm});
            skCircle(sketch, "E6.100.0.22", {"center": v(593.24, -571.8) * mm, "radius": 3.18 * mm});
            skCircle(sketch, "E6.102.0.22", {"center": v(847.24, -571.8) * mm, "radius": 3.18 * mm});
            skCircle(sketch, "E6.104.0.22", {"center": v(339.24, -571.8) * mm, "radius": 3.18 * mm});
            skCircle(sketch, "E6.106.0.22", {"center": v(561.49, -571.8) * mm, "radius": 3.18 * mm});
            skCircle(sketch, "E6.108.0.22", {"center": v(815.49, -571.8) * mm, "radius": 3.18 * mm});
            skCircle(sketch, "E6.110.0.22", {"center": v(307.49, -571.8) * mm, "radius": 3.18 * mm});
            skCircle(sketch, "E6.112.0.22", {"center": v(529.74, -571.8) * mm, "radius": 3.18 * mm});
            skCircle(sketch, "E6.114.0.22", {"center": v(180.49, -571.8) * mm, "radius": 3.18 * mm});
            skCircle(sketch, "E6.116.0.22", {"center": v(148.74, -571.8) * mm, "radius": 3.18 * mm});
            skCircle(sketch, "E6.118.0.22", {"center": v(910.74, -571.8) * mm, "radius": 3.18 * mm});
            skCircle(sketch, "E6.120.0.22", {"center": v(275.74, -571.8) * mm, "radius": 3.18 * mm});
            skCircle(sketch, "E6.122.0.22", {"center": v(243.99, -571.8) * mm, "radius": 3.18 * mm});
            skCircle(sketch, "E6.124.0.22", {"center": v(212.24, -571.8) * mm, "radius": 3.18 * mm});
            skCircle(sketch, "E6.126.0.22", {"center": v(783.74, -571.8) * mm, "radius": 3.18 * mm});
            skCircle(sketch, "E6.128.0.22", {"center": v(497.99, -571.8) * mm, "radius": 3.18 * mm});
            skCircle(sketch, "E6.130.0.22", {"center": v(402.74, -571.8) * mm, "radius": 3.18 * mm});
            skCircle(sketch, "E6.132.0.22", {"center": v(624.99, -571.8) * mm, "radius": 3.18 * mm});
            skCircle(sketch, "E6.134.0.22", {"center": v(751.99, -571.8) * mm, "radius": 3.18 * mm});
            skCircle(sketch, "E6.136.0.22", {"center": v(466.24, -571.8) * mm, "radius": 3.18 * mm});
            skCircle(sketch, "E6.138.0.22", {"center": v(688.49, -571.8) * mm, "radius": 3.18 * mm});
            skCircle(sketch, "E6.140.0.22", {"center": v(116.99, -571.8) * mm, "radius": 3.18 * mm});
            skCircle(sketch, "E6.142.0.22", {"center": v(85.24, -571.8) * mm, "radius": 3.18 * mm});
            skCircle(sketch, "E6.144.0.22", {"center": v(53.49, -571.8) * mm, "radius": 3.18 * mm});
            skLineSegment(sketch, "E6.146.0.22", {"start": v(-41.76, -571.8) * mm, "end": v(-10.01, -571.8) * mm, "construction": true});
            skCircle(sketch, "E6.149.0.22", {"center": v(21.74, -571.8) * mm, "radius": 3.18 * mm});
            skCircle(sketch, "E6.151.0.22", {"center": v(-10.01, -571.8) * mm, "radius": 3.18 * mm});
            skCircle(sketch, "E6.153.0.22", {"center": v(-41.76, -571.8) * mm, "radius": 3.18 * mm});
            skCircle(sketch, "E6.0.0.23", {"center": v(2244.24, -597.2) * mm, "radius": 3.18 * mm});
            skCircle(sketch, "E6.2.0.23", {"center": v(2180.74, -597.2) * mm, "radius": 3.18 * mm});
            skCircle(sketch, "E6.4.0.23", {"center": v(2339.49, -597.2) * mm, "radius": 3.18 * mm});
            skCircle(sketch, "E6.6.0.23", {"center": v(2307.74, -597.2) * mm, "radius": 3.18 * mm});
            skCircle(sketch, "E6.8.0.23", {"center": v(2275.99, -597.2) * mm, "radius": 3.18 * mm});
            skCircle(sketch, "E6.10.0.23", {"center": v(2212.49, -597.2) * mm, "radius": 3.18 * mm});
            skCircle(sketch, "E6.12.0.23", {"center": v(1958.49, -597.2) * mm, "radius": 3.18 * mm});
            skCircle(sketch, "E6.14.0.23", {"center": v(1894.99, -597.2) * mm, "radius": 3.18 * mm});
            skCircle(sketch, "E6.16.0.23", {"center": v(2117.24, -597.2) * mm, "radius": 3.18 * mm});
            skCircle(sketch, "E6.18.0.23", {"center": v(2085.49, -597.2) * mm, "radius": 3.18 * mm});
            skCircle(sketch, "E6.20.0.23", {"center": v(2053.74, -597.2) * mm, "radius": 3.18 * mm});
            skCircle(sketch, "E6.22.0.23", {"center": v(1926.74, -597.2) * mm, "radius": 3.18 * mm});
            skCircle(sketch, "E6.24.0.23", {"center": v(2021.99, -597.2) * mm, "radius": 3.18 * mm});
            skCircle(sketch, "E6.26.0.23", {"center": v(2148.99, -597.2) * mm, "radius": 3.18 * mm});
            skCircle(sketch, "E6.28.0.23", {"center": v(1990.24, -597.2) * mm, "radius": 3.18 * mm});
            skCircle(sketch, "E6.30.0.23", {"center": v(1450.49, -597.2) * mm, "radius": 3.18 * mm});
            skCircle(sketch, "E6.32.0.23", {"center": v(1228.24, -597.2) * mm, "radius": 3.18 * mm});
            skCircle(sketch, "E6.34.0.23", {"center": v(1736.24, -597.2) * mm, "radius": 3.18 * mm});
            skCircle(sketch, "E6.36.0.23", {"center": v(1386.99, -597.2) * mm, "radius": 3.18 * mm});
            skCircle(sketch, "E6.38.0.23", {"center": v(1164.74, -597.2) * mm, "radius": 3.18 * mm});
            skCircle(sketch, "E6.40.0.23", {"center": v(1672.74, -597.2) * mm, "radius": 3.18 * mm});
            skCircle(sketch, "E6.42.0.23", {"center": v(1101.24, -597.2) * mm, "radius": 3.18 * mm});
            skCircle(sketch, "E6.44.0.23", {"center": v(1609.24, -597.2) * mm, "radius": 3.18 * mm});
            skCircle(sketch, "E6.46.0.23", {"center": v(1355.24, -597.2) * mm, "radius": 3.18 * mm});
            skCircle(sketch, "E6.48.0.23", {"center": v(1863.24, -597.2) * mm, "radius": 3.18 * mm});
            skCircle(sketch, "E6.50.0.23", {"center": v(1069.49, -597.2) * mm, "radius": 3.18 * mm});
            skCircle(sketch, "E6.52.0.23", {"center": v(1577.49, -597.2) * mm, "radius": 3.18 * mm});
            skCircle(sketch, "E6.54.0.23", {"center": v(1323.49, -597.2) * mm, "radius": 3.18 * mm});
            skCircle(sketch, "E6.56.0.23", {"center": v(1831.49, -597.2) * mm, "radius": 3.18 * mm});
            skCircle(sketch, "E6.58.0.23", {"center": v(1037.74, -597.2) * mm, "radius": 3.18 * mm});
            skCircle(sketch, "E6.60.0.23", {"center": v(1545.74, -597.2) * mm, "radius": 3.18 * mm});
            skCircle(sketch, "E6.62.0.23", {"center": v(1418.74, -597.2) * mm, "radius": 3.18 * mm});
            skCircle(sketch, "E6.64.0.23", {"center": v(1005.99, -597.2) * mm, "radius": 3.18 * mm});
            skCircle(sketch, "E6.66.0.23", {"center": v(1513.99, -597.2) * mm, "radius": 3.18 * mm});
            skCircle(sketch, "E6.68.0.23", {"center": v(1799.74, -597.2) * mm, "radius": 3.18 * mm});
            skCircle(sketch, "E6.70.0.23", {"center": v(1291.74, -597.2) * mm, "radius": 3.18 * mm});
            skCircle(sketch, "E6.72.0.23", {"center": v(1132.99, -597.2) * mm, "radius": 3.18 * mm});
            skCircle(sketch, "E6.74.0.23", {"center": v(974.24, -597.2) * mm, "radius": 3.18 * mm});
            skCircle(sketch, "E6.76.0.23", {"center": v(1482.24, -597.2) * mm, "radius": 3.18 * mm});
            skCircle(sketch, "E6.78.0.23", {"center": v(1259.99, -597.2) * mm, "radius": 3.18 * mm});
            skCircle(sketch, "E6.80.0.23", {"center": v(1640.99, -597.2) * mm, "radius": 3.18 * mm});
            skCircle(sketch, "E6.82.0.23", {"center": v(1767.99, -597.2) * mm, "radius": 3.18 * mm});
            skCircle(sketch, "E6.84.0.23", {"center": v(1196.49, -597.2) * mm, "radius": 3.18 * mm});
            skCircle(sketch, "E6.86.0.23", {"center": v(1704.49, -597.2) * mm, "radius": 3.18 * mm});
            skCircle(sketch, "E6.88.0.23", {"center": v(720.24, -597.2) * mm, "radius": 3.18 * mm});
            skCircle(sketch, "E6.90.0.23", {"center": v(942.49, -597.2) * mm, "radius": 3.18 * mm});
            skCircle(sketch, "E6.92.0.23", {"center": v(878.99, -597.2) * mm, "radius": 3.18 * mm});
            skCircle(sketch, "E6.94.0.23", {"center": v(434.49, -597.2) * mm, "radius": 3.18 * mm});
            skCircle(sketch, "E6.96.0.23", {"center": v(656.74, -597.2) * mm, "radius": 3.18 * mm});
            skCircle(sketch, "E6.98.0.23", {"center": v(370.99, -597.2) * mm, "radius": 3.18 * mm});
            skCircle(sketch, "E6.100.0.23", {"center": v(593.24, -597.2) * mm, "radius": 3.18 * mm});
            skCircle(sketch, "E6.102.0.23", {"center": v(847.24, -597.2) * mm, "radius": 3.18 * mm});
            skCircle(sketch, "E6.104.0.23", {"center": v(339.24, -597.2) * mm, "radius": 3.18 * mm});
            skCircle(sketch, "E6.106.0.23", {"center": v(561.49, -597.2) * mm, "radius": 3.18 * mm});
            skCircle(sketch, "E6.108.0.23", {"center": v(815.49, -597.2) * mm, "radius": 3.18 * mm});
            skCircle(sketch, "E6.110.0.23", {"center": v(307.49, -597.2) * mm, "radius": 3.18 * mm});
            skCircle(sketch, "E6.112.0.23", {"center": v(529.74, -597.2) * mm, "radius": 3.18 * mm});
            skCircle(sketch, "E6.114.0.23", {"center": v(180.49, -597.2) * mm, "radius": 3.18 * mm});
            skCircle(sketch, "E6.116.0.23", {"center": v(148.74, -597.2) * mm, "radius": 3.18 * mm});
            skCircle(sketch, "E6.118.0.23", {"center": v(910.74, -597.2) * mm, "radius": 3.18 * mm});
            skCircle(sketch, "E6.120.0.23", {"center": v(275.74, -597.2) * mm, "radius": 3.18 * mm});
            skCircle(sketch, "E6.122.0.23", {"center": v(243.99, -597.2) * mm, "radius": 3.18 * mm});
            skCircle(sketch, "E6.124.0.23", {"center": v(212.24, -597.2) * mm, "radius": 3.18 * mm});
            skCircle(sketch, "E6.126.0.23", {"center": v(783.74, -597.2) * mm, "radius": 3.18 * mm});
            skCircle(sketch, "E6.128.0.23", {"center": v(497.99, -597.2) * mm, "radius": 3.18 * mm});
            skCircle(sketch, "E6.130.0.23", {"center": v(402.74, -597.2) * mm, "radius": 3.18 * mm});
            skCircle(sketch, "E6.132.0.23", {"center": v(624.99, -597.2) * mm, "radius": 3.18 * mm});
            skCircle(sketch, "E6.134.0.23", {"center": v(751.99, -597.2) * mm, "radius": 3.18 * mm});
            skCircle(sketch, "E6.136.0.23", {"center": v(466.24, -597.2) * mm, "radius": 3.18 * mm});
            skCircle(sketch, "E6.138.0.23", {"center": v(688.49, -597.2) * mm, "radius": 3.18 * mm});
            skCircle(sketch, "E6.140.0.23", {"center": v(116.99, -597.2) * mm, "radius": 3.18 * mm});
            skCircle(sketch, "E6.142.0.23", {"center": v(85.24, -597.2) * mm, "radius": 3.18 * mm});
            skCircle(sketch, "E6.144.0.23", {"center": v(53.49, -597.2) * mm, "radius": 3.18 * mm});
            skLineSegment(sketch, "E6.146.0.23", {"start": v(-41.76, -597.2) * mm, "end": v(-10.01, -597.2) * mm, "construction": true});
            skCircle(sketch, "E6.149.0.23", {"center": v(21.74, -597.2) * mm, "radius": 3.18 * mm});
            skCircle(sketch, "E6.151.0.23", {"center": v(-10.01, -597.2) * mm, "radius": 3.18 * mm});
            skCircle(sketch, "E6.153.0.23", {"center": v(-41.76, -597.2) * mm, "radius": 3.18 * mm});
            skCircle(sketch, "E6.0.0.24", {"center": v(2244.24, -622.6) * mm, "radius": 3.18 * mm});
            skCircle(sketch, "E6.2.0.24", {"center": v(2180.74, -622.6) * mm, "radius": 3.18 * mm});
            skCircle(sketch, "E6.4.0.24", {"center": v(2339.49, -622.6) * mm, "radius": 3.18 * mm});
            skCircle(sketch, "E6.6.0.24", {"center": v(2307.74, -622.6) * mm, "radius": 3.18 * mm});
            skCircle(sketch, "E6.8.0.24", {"center": v(2275.99, -622.6) * mm, "radius": 3.18 * mm});
            skCircle(sketch, "E6.10.0.24", {"center": v(2212.49, -622.6) * mm, "radius": 3.18 * mm});
            skCircle(sketch, "E6.12.0.24", {"center": v(1958.49, -622.6) * mm, "radius": 3.18 * mm});
            skCircle(sketch, "E6.14.0.24", {"center": v(1894.99, -622.6) * mm, "radius": 3.18 * mm});
            skCircle(sketch, "E6.16.0.24", {"center": v(2117.24, -622.6) * mm, "radius": 3.18 * mm});
            skCircle(sketch, "E6.18.0.24", {"center": v(2085.49, -622.6) * mm, "radius": 3.18 * mm});
            skCircle(sketch, "E6.20.0.24", {"center": v(2053.74, -622.6) * mm, "radius": 3.18 * mm});
            skCircle(sketch, "E6.22.0.24", {"center": v(1926.74, -622.6) * mm, "radius": 3.18 * mm});
            skCircle(sketch, "E6.24.0.24", {"center": v(2021.99, -622.6) * mm, "radius": 3.18 * mm});
            skCircle(sketch, "E6.26.0.24", {"center": v(2148.99, -622.6) * mm, "radius": 3.18 * mm});
            skCircle(sketch, "E6.28.0.24", {"center": v(1990.24, -622.6) * mm, "radius": 3.18 * mm});
            skCircle(sketch, "E6.30.0.24", {"center": v(1450.49, -622.6) * mm, "radius": 3.18 * mm});
            skCircle(sketch, "E6.32.0.24", {"center": v(1228.24, -622.6) * mm, "radius": 3.18 * mm});
            skCircle(sketch, "E6.34.0.24", {"center": v(1736.24, -622.6) * mm, "radius": 3.18 * mm});
            skCircle(sketch, "E6.36.0.24", {"center": v(1386.99, -622.6) * mm, "radius": 3.18 * mm});
            skCircle(sketch, "E6.38.0.24", {"center": v(1164.74, -622.6) * mm, "radius": 3.18 * mm});
            skCircle(sketch, "E6.40.0.24", {"center": v(1672.74, -622.6) * mm, "radius": 3.18 * mm});
            skCircle(sketch, "E6.42.0.24", {"center": v(1101.24, -622.6) * mm, "radius": 3.18 * mm});
            skCircle(sketch, "E6.44.0.24", {"center": v(1609.24, -622.6) * mm, "radius": 3.18 * mm});
            skCircle(sketch, "E6.46.0.24", {"center": v(1355.24, -622.6) * mm, "radius": 3.18 * mm});
            skCircle(sketch, "E6.48.0.24", {"center": v(1863.24, -622.6) * mm, "radius": 3.18 * mm});
            skCircle(sketch, "E6.50.0.24", {"center": v(1069.49, -622.6) * mm, "radius": 3.18 * mm});
            skCircle(sketch, "E6.52.0.24", {"center": v(1577.49, -622.6) * mm, "radius": 3.18 * mm});
            skCircle(sketch, "E6.54.0.24", {"center": v(1323.49, -622.6) * mm, "radius": 3.18 * mm});
            skCircle(sketch, "E6.56.0.24", {"center": v(1831.49, -622.6) * mm, "radius": 3.18 * mm});
            skCircle(sketch, "E6.58.0.24", {"center": v(1037.74, -622.6) * mm, "radius": 3.18 * mm});
            skCircle(sketch, "E6.60.0.24", {"center": v(1545.74, -622.6) * mm, "radius": 3.18 * mm});
            skCircle(sketch, "E6.62.0.24", {"center": v(1418.74, -622.6) * mm, "radius": 3.18 * mm});
            skCircle(sketch, "E6.64.0.24", {"center": v(1005.99, -622.6) * mm, "radius": 3.18 * mm});
            skCircle(sketch, "E6.66.0.24", {"center": v(1513.99, -622.6) * mm, "radius": 3.18 * mm});
            skCircle(sketch, "E6.68.0.24", {"center": v(1799.74, -622.6) * mm, "radius": 3.18 * mm});
            skCircle(sketch, "E6.70.0.24", {"center": v(1291.74, -622.6) * mm, "radius": 3.18 * mm});
            skCircle(sketch, "E6.72.0.24", {"center": v(1132.99, -622.6) * mm, "radius": 3.18 * mm});
            skCircle(sketch, "E6.74.0.24", {"center": v(974.24, -622.6) * mm, "radius": 3.18 * mm});
            skCircle(sketch, "E6.76.0.24", {"center": v(1482.24, -622.6) * mm, "radius": 3.18 * mm});
            skCircle(sketch, "E6.78.0.24", {"center": v(1259.99, -622.6) * mm, "radius": 3.18 * mm});
            skCircle(sketch, "E6.80.0.24", {"center": v(1640.99, -622.6) * mm, "radius": 3.18 * mm});
            skCircle(sketch, "E6.82.0.24", {"center": v(1767.99, -622.6) * mm, "radius": 3.18 * mm});
            skCircle(sketch, "E6.84.0.24", {"center": v(1196.49, -622.6) * mm, "radius": 3.18 * mm});
            skCircle(sketch, "E6.86.0.24", {"center": v(1704.49, -622.6) * mm, "radius": 3.18 * mm});
            skCircle(sketch, "E6.88.0.24", {"center": v(720.24, -622.6) * mm, "radius": 3.18 * mm});
            skCircle(sketch, "E6.90.0.24", {"center": v(942.49, -622.6) * mm, "radius": 3.18 * mm});
            skCircle(sketch, "E6.92.0.24", {"center": v(878.99, -622.6) * mm, "radius": 3.18 * mm});
            skCircle(sketch, "E6.94.0.24", {"center": v(434.49, -622.6) * mm, "radius": 3.18 * mm});
            skCircle(sketch, "E6.96.0.24", {"center": v(656.74, -622.6) * mm, "radius": 3.18 * mm});
            skCircle(sketch, "E6.98.0.24", {"center": v(370.99, -622.6) * mm, "radius": 3.18 * mm});
            skCircle(sketch, "E6.100.0.24", {"center": v(593.24, -622.6) * mm, "radius": 3.18 * mm});
            skCircle(sketch, "E6.102.0.24", {"center": v(847.24, -622.6) * mm, "radius": 3.18 * mm});
            skCircle(sketch, "E6.104.0.24", {"center": v(339.24, -622.6) * mm, "radius": 3.18 * mm});
            skCircle(sketch, "E6.106.0.24", {"center": v(561.49, -622.6) * mm, "radius": 3.18 * mm});
            skCircle(sketch, "E6.108.0.24", {"center": v(815.49, -622.6) * mm, "radius": 3.18 * mm});
            skCircle(sketch, "E6.110.0.24", {"center": v(307.49, -622.6) * mm, "radius": 3.18 * mm});
            skCircle(sketch, "E6.112.0.24", {"center": v(529.74, -622.6) * mm, "radius": 3.18 * mm});
            skCircle(sketch, "E6.114.0.24", {"center": v(180.49, -622.6) * mm, "radius": 3.18 * mm});
            skCircle(sketch, "E6.116.0.24", {"center": v(148.74, -622.6) * mm, "radius": 3.18 * mm});
            skCircle(sketch, "E6.118.0.24", {"center": v(910.74, -622.6) * mm, "radius": 3.18 * mm});
            skCircle(sketch, "E6.120.0.24", {"center": v(275.74, -622.6) * mm, "radius": 3.18 * mm});
            skCircle(sketch, "E6.122.0.24", {"center": v(243.99, -622.6) * mm, "radius": 3.18 * mm});
            skCircle(sketch, "E6.124.0.24", {"center": v(212.24, -622.6) * mm, "radius": 3.18 * mm});
            skCircle(sketch, "E6.126.0.24", {"center": v(783.74, -622.6) * mm, "radius": 3.18 * mm});
            skCircle(sketch, "E6.128.0.24", {"center": v(497.99, -622.6) * mm, "radius": 3.18 * mm});
            skCircle(sketch, "E6.130.0.24", {"center": v(402.74, -622.6) * mm, "radius": 3.18 * mm});
            skCircle(sketch, "E6.132.0.24", {"center": v(624.99, -622.6) * mm, "radius": 3.18 * mm});
            skCircle(sketch, "E6.134.0.24", {"center": v(751.99, -622.6) * mm, "radius": 3.18 * mm});
            skCircle(sketch, "E6.136.0.24", {"center": v(466.24, -622.6) * mm, "radius": 3.18 * mm});
            skCircle(sketch, "E6.138.0.24", {"center": v(688.49, -622.6) * mm, "radius": 3.18 * mm});
            skCircle(sketch, "E6.140.0.24", {"center": v(116.99, -622.6) * mm, "radius": 3.18 * mm});
            skCircle(sketch, "E6.142.0.24", {"center": v(85.24, -622.6) * mm, "radius": 3.18 * mm});
            skCircle(sketch, "E6.144.0.24", {"center": v(53.49, -622.6) * mm, "radius": 3.18 * mm});
            skLineSegment(sketch, "E6.146.0.24", {"start": v(-41.76, -622.6) * mm, "end": v(-10.01, -622.6) * mm, "construction": true});
            skCircle(sketch, "E6.149.0.24", {"center": v(21.74, -622.6) * mm, "radius": 3.18 * mm});
            skCircle(sketch, "E6.151.0.24", {"center": v(-10.01, -622.6) * mm, "radius": 3.18 * mm});
            skCircle(sketch, "E6.153.0.24", {"center": v(-41.76, -622.6) * mm, "radius": 3.18 * mm});
            skCircle(sketch, "E6.0.0.25", {"center": v(2244.24, -648) * mm, "radius": 3.18 * mm});
            skCircle(sketch, "E6.2.0.25", {"center": v(2180.74, -648) * mm, "radius": 3.18 * mm});
            skCircle(sketch, "E6.4.0.25", {"center": v(2339.49, -648) * mm, "radius": 3.18 * mm});
            skCircle(sketch, "E6.6.0.25", {"center": v(2307.74, -648) * mm, "radius": 3.18 * mm});
            skCircle(sketch, "E6.8.0.25", {"center": v(2275.99, -648) * mm, "radius": 3.18 * mm});
            skCircle(sketch, "E6.10.0.25", {"center": v(2212.49, -648) * mm, "radius": 3.18 * mm});
            skCircle(sketch, "E6.12.0.25", {"center": v(1958.49, -648) * mm, "radius": 3.18 * mm});
            skCircle(sketch, "E6.14.0.25", {"center": v(1894.99, -648) * mm, "radius": 3.18 * mm});
            skCircle(sketch, "E6.16.0.25", {"center": v(2117.24, -648) * mm, "radius": 3.18 * mm});
            skCircle(sketch, "E6.18.0.25", {"center": v(2085.49, -648) * mm, "radius": 3.18 * mm});
            skCircle(sketch, "E6.20.0.25", {"center": v(2053.74, -648) * mm, "radius": 3.18 * mm});
            skCircle(sketch, "E6.22.0.25", {"center": v(1926.74, -648) * mm, "radius": 3.18 * mm});
            skCircle(sketch, "E6.24.0.25", {"center": v(2021.99, -648) * mm, "radius": 3.18 * mm});
            skCircle(sketch, "E6.26.0.25", {"center": v(2148.99, -648) * mm, "radius": 3.18 * mm});
            skCircle(sketch, "E6.28.0.25", {"center": v(1990.24, -648) * mm, "radius": 3.18 * mm});
            skCircle(sketch, "E6.30.0.25", {"center": v(1450.49, -648) * mm, "radius": 3.18 * mm});
            skCircle(sketch, "E6.32.0.25", {"center": v(1228.24, -648) * mm, "radius": 3.18 * mm});
            skCircle(sketch, "E6.34.0.25", {"center": v(1736.24, -648) * mm, "radius": 3.18 * mm});
            skCircle(sketch, "E6.36.0.25", {"center": v(1386.99, -648) * mm, "radius": 3.18 * mm});
            skCircle(sketch, "E6.38.0.25", {"center": v(1164.74, -648) * mm, "radius": 3.18 * mm});
            skCircle(sketch, "E6.40.0.25", {"center": v(1672.74, -648) * mm, "radius": 3.18 * mm});
            skCircle(sketch, "E6.42.0.25", {"center": v(1101.24, -648) * mm, "radius": 3.18 * mm});
            skCircle(sketch, "E6.44.0.25", {"center": v(1609.24, -648) * mm, "radius": 3.18 * mm});
            skCircle(sketch, "E6.46.0.25", {"center": v(1355.24, -648) * mm, "radius": 3.18 * mm});
            skCircle(sketch, "E6.48.0.25", {"center": v(1863.24, -648) * mm, "radius": 3.18 * mm});
            skCircle(sketch, "E6.50.0.25", {"center": v(1069.49, -648) * mm, "radius": 3.18 * mm});
            skCircle(sketch, "E6.52.0.25", {"center": v(1577.49, -648) * mm, "radius": 3.18 * mm});
            skCircle(sketch, "E6.54.0.25", {"center": v(1323.49, -648) * mm, "radius": 3.18 * mm});
            skCircle(sketch, "E6.56.0.25", {"center": v(1831.49, -648) * mm, "radius": 3.18 * mm});
            skCircle(sketch, "E6.58.0.25", {"center": v(1037.74, -648) * mm, "radius": 3.18 * mm});
            skCircle(sketch, "E6.60.0.25", {"center": v(1545.74, -648) * mm, "radius": 3.18 * mm});
            skCircle(sketch, "E6.62.0.25", {"center": v(1418.74, -648) * mm, "radius": 3.18 * mm});
            skCircle(sketch, "E6.64.0.25", {"center": v(1005.99, -648) * mm, "radius": 3.18 * mm});
            skCircle(sketch, "E6.66.0.25", {"center": v(1513.99, -648) * mm, "radius": 3.18 * mm});
            skCircle(sketch, "E6.68.0.25", {"center": v(1799.74, -648) * mm, "radius": 3.18 * mm});
            skCircle(sketch, "E6.70.0.25", {"center": v(1291.74, -648) * mm, "radius": 3.18 * mm});
            skCircle(sketch, "E6.72.0.25", {"center": v(1132.99, -648) * mm, "radius": 3.18 * mm});
            skCircle(sketch, "E6.74.0.25", {"center": v(974.24, -648) * mm, "radius": 3.18 * mm});
            skCircle(sketch, "E6.76.0.25", {"center": v(1482.24, -648) * mm, "radius": 3.18 * mm});
            skCircle(sketch, "E6.78.0.25", {"center": v(1259.99, -648) * mm, "radius": 3.18 * mm});
            skCircle(sketch, "E6.80.0.25", {"center": v(1640.99, -648) * mm, "radius": 3.18 * mm});
            skCircle(sketch, "E6.82.0.25", {"center": v(1767.99, -648) * mm, "radius": 3.18 * mm});
            skCircle(sketch, "E6.84.0.25", {"center": v(1196.49, -648) * mm, "radius": 3.18 * mm});
            skCircle(sketch, "E6.86.0.25", {"center": v(1704.49, -648) * mm, "radius": 3.18 * mm});
            skCircle(sketch, "E6.88.0.25", {"center": v(720.24, -648) * mm, "radius": 3.18 * mm});
            skCircle(sketch, "E6.90.0.25", {"center": v(942.49, -648) * mm, "radius": 3.18 * mm});
            skCircle(sketch, "E6.92.0.25", {"center": v(878.99, -648) * mm, "radius": 3.18 * mm});
            skCircle(sketch, "E6.94.0.25", {"center": v(434.49, -648) * mm, "radius": 3.18 * mm});
            skCircle(sketch, "E6.96.0.25", {"center": v(656.74, -648) * mm, "radius": 3.18 * mm});
            skCircle(sketch, "E6.98.0.25", {"center": v(370.99, -648) * mm, "radius": 3.18 * mm});
            skCircle(sketch, "E6.100.0.25", {"center": v(593.24, -648) * mm, "radius": 3.18 * mm});
            skCircle(sketch, "E6.102.0.25", {"center": v(847.24, -648) * mm, "radius": 3.18 * mm});
            skCircle(sketch, "E6.104.0.25", {"center": v(339.24, -648) * mm, "radius": 3.18 * mm});
            skCircle(sketch, "E6.106.0.25", {"center": v(561.49, -648) * mm, "radius": 3.18 * mm});
            skCircle(sketch, "E6.108.0.25", {"center": v(815.49, -648) * mm, "radius": 3.18 * mm});
            skCircle(sketch, "E6.110.0.25", {"center": v(307.49, -648) * mm, "radius": 3.18 * mm});
            skCircle(sketch, "E6.112.0.25", {"center": v(529.74, -648) * mm, "radius": 3.18 * mm});
            skCircle(sketch, "E6.114.0.25", {"center": v(180.49, -648) * mm, "radius": 3.18 * mm});
            skCircle(sketch, "E6.116.0.25", {"center": v(148.74, -648) * mm, "radius": 3.18 * mm});
            skCircle(sketch, "E6.118.0.25", {"center": v(910.74, -648) * mm, "radius": 3.18 * mm});
            skCircle(sketch, "E6.120.0.25", {"center": v(275.74, -648) * mm, "radius": 3.18 * mm});
            skCircle(sketch, "E6.122.0.25", {"center": v(243.99, -648) * mm, "radius": 3.18 * mm});
            skCircle(sketch, "E6.124.0.25", {"center": v(212.24, -648) * mm, "radius": 3.18 * mm});
            skCircle(sketch, "E6.126.0.25", {"center": v(783.74, -648) * mm, "radius": 3.18 * mm});
            skCircle(sketch, "E6.128.0.25", {"center": v(497.99, -648) * mm, "radius": 3.18 * mm});
            skCircle(sketch, "E6.130.0.25", {"center": v(402.74, -648) * mm, "radius": 3.18 * mm});
            skCircle(sketch, "E6.132.0.25", {"center": v(624.99, -648) * mm, "radius": 3.18 * mm});
            skCircle(sketch, "E6.134.0.25", {"center": v(751.99, -648) * mm, "radius": 3.18 * mm});
            skCircle(sketch, "E6.136.0.25", {"center": v(466.24, -648) * mm, "radius": 3.18 * mm});
            skCircle(sketch, "E6.138.0.25", {"center": v(688.49, -648) * mm, "radius": 3.18 * mm});
            skCircle(sketch, "E6.140.0.25", {"center": v(116.99, -648) * mm, "radius": 3.18 * mm});
            skCircle(sketch, "E6.142.0.25", {"center": v(85.24, -648) * mm, "radius": 3.18 * mm});
            skCircle(sketch, "E6.144.0.25", {"center": v(53.49, -648) * mm, "radius": 3.18 * mm});
            skLineSegment(sketch, "E6.146.0.25", {"start": v(-41.76, -648) * mm, "end": v(-10.01, -648) * mm, "construction": true});
            skCircle(sketch, "E6.149.0.25", {"center": v(21.74, -648) * mm, "radius": 3.18 * mm});
            skCircle(sketch, "E6.151.0.25", {"center": v(-10.01, -648) * mm, "radius": 3.18 * mm});
            skCircle(sketch, "E6.153.0.25", {"center": v(-41.76, -648) * mm, "radius": 3.18 * mm});
            skCircle(sketch, "E6.0.0.26", {"center": v(2244.24, -673.4) * mm, "radius": 3.18 * mm});
            skCircle(sketch, "E6.2.0.26", {"center": v(2180.74, -673.4) * mm, "radius": 3.18 * mm});
            skCircle(sketch, "E6.4.0.26", {"center": v(2339.49, -673.4) * mm, "radius": 3.18 * mm});
            skCircle(sketch, "E6.6.0.26", {"center": v(2307.74, -673.4) * mm, "radius": 3.18 * mm});
            skCircle(sketch, "E6.8.0.26", {"center": v(2275.99, -673.4) * mm, "radius": 3.18 * mm});
            skCircle(sketch, "E6.10.0.26", {"center": v(2212.49, -673.4) * mm, "radius": 3.18 * mm});
            skCircle(sketch, "E6.12.0.26", {"center": v(1958.49, -673.4) * mm, "radius": 3.18 * mm});
            skCircle(sketch, "E6.14.0.26", {"center": v(1894.99, -673.4) * mm, "radius": 3.18 * mm});
            skCircle(sketch, "E6.16.0.26", {"center": v(2117.24, -673.4) * mm, "radius": 3.18 * mm});
            skCircle(sketch, "E6.18.0.26", {"center": v(2085.49, -673.4) * mm, "radius": 3.18 * mm});
            skCircle(sketch, "E6.20.0.26", {"center": v(2053.74, -673.4) * mm, "radius": 3.18 * mm});
            skCircle(sketch, "E6.22.0.26", {"center": v(1926.74, -673.4) * mm, "radius": 3.18 * mm});
            skCircle(sketch, "E6.24.0.26", {"center": v(2021.99, -673.4) * mm, "radius": 3.18 * mm});
            skCircle(sketch, "E6.26.0.26", {"center": v(2148.99, -673.4) * mm, "radius": 3.18 * mm});
            skCircle(sketch, "E6.28.0.26", {"center": v(1990.24, -673.4) * mm, "radius": 3.18 * mm});
            skCircle(sketch, "E6.30.0.26", {"center": v(1450.49, -673.4) * mm, "radius": 3.18 * mm});
            skCircle(sketch, "E6.32.0.26", {"center": v(1228.24, -673.4) * mm, "radius": 3.18 * mm});
            skCircle(sketch, "E6.34.0.26", {"center": v(1736.24, -673.4) * mm, "radius": 3.18 * mm});
            skCircle(sketch, "E6.36.0.26", {"center": v(1386.99, -673.4) * mm, "radius": 3.18 * mm});
            skCircle(sketch, "E6.38.0.26", {"center": v(1164.74, -673.4) * mm, "radius": 3.18 * mm});
            skCircle(sketch, "E6.40.0.26", {"center": v(1672.74, -673.4) * mm, "radius": 3.18 * mm});
            skCircle(sketch, "E6.42.0.26", {"center": v(1101.24, -673.4) * mm, "radius": 3.18 * mm});
            skCircle(sketch, "E6.44.0.26", {"center": v(1609.24, -673.4) * mm, "radius": 3.18 * mm});
            skCircle(sketch, "E6.46.0.26", {"center": v(1355.24, -673.4) * mm, "radius": 3.18 * mm});
            skCircle(sketch, "E6.48.0.26", {"center": v(1863.24, -673.4) * mm, "radius": 3.18 * mm});
            skCircle(sketch, "E6.50.0.26", {"center": v(1069.49, -673.4) * mm, "radius": 3.18 * mm});
            skCircle(sketch, "E6.52.0.26", {"center": v(1577.49, -673.4) * mm, "radius": 3.18 * mm});
            skCircle(sketch, "E6.54.0.26", {"center": v(1323.49, -673.4) * mm, "radius": 3.18 * mm});
            skCircle(sketch, "E6.56.0.26", {"center": v(1831.49, -673.4) * mm, "radius": 3.18 * mm});
            skCircle(sketch, "E6.58.0.26", {"center": v(1037.74, -673.4) * mm, "radius": 3.18 * mm});
            skCircle(sketch, "E6.60.0.26", {"center": v(1545.74, -673.4) * mm, "radius": 3.18 * mm});
            skCircle(sketch, "E6.62.0.26", {"center": v(1418.74, -673.4) * mm, "radius": 3.18 * mm});
            skCircle(sketch, "E6.64.0.26", {"center": v(1005.99, -673.4) * mm, "radius": 3.18 * mm});
            skCircle(sketch, "E6.66.0.26", {"center": v(1513.99, -673.4) * mm, "radius": 3.18 * mm});
            skCircle(sketch, "E6.68.0.26", {"center": v(1799.74, -673.4) * mm, "radius": 3.18 * mm});
            skCircle(sketch, "E6.70.0.26", {"center": v(1291.74, -673.4) * mm, "radius": 3.18 * mm});
            skCircle(sketch, "E6.72.0.26", {"center": v(1132.99, -673.4) * mm, "radius": 3.18 * mm});
            skCircle(sketch, "E6.74.0.26", {"center": v(974.24, -673.4) * mm, "radius": 3.18 * mm});
            skCircle(sketch, "E6.76.0.26", {"center": v(1482.24, -673.4) * mm, "radius": 3.18 * mm});
            skCircle(sketch, "E6.78.0.26", {"center": v(1259.99, -673.4) * mm, "radius": 3.18 * mm});
            skCircle(sketch, "E6.80.0.26", {"center": v(1640.99, -673.4) * mm, "radius": 3.18 * mm});
            skCircle(sketch, "E6.82.0.26", {"center": v(1767.99, -673.4) * mm, "radius": 3.18 * mm});
            skCircle(sketch, "E6.84.0.26", {"center": v(1196.49, -673.4) * mm, "radius": 3.18 * mm});
            skCircle(sketch, "E6.86.0.26", {"center": v(1704.49, -673.4) * mm, "radius": 3.18 * mm});
            skCircle(sketch, "E6.88.0.26", {"center": v(720.24, -673.4) * mm, "radius": 3.18 * mm});
            skCircle(sketch, "E6.90.0.26", {"center": v(942.49, -673.4) * mm, "radius": 3.18 * mm});
            skCircle(sketch, "E6.92.0.26", {"center": v(878.99, -673.4) * mm, "radius": 3.18 * mm});
            skCircle(sketch, "E6.94.0.26", {"center": v(434.49, -673.4) * mm, "radius": 3.18 * mm});
            skCircle(sketch, "E6.96.0.26", {"center": v(656.74, -673.4) * mm, "radius": 3.18 * mm});
            skCircle(sketch, "E6.98.0.26", {"center": v(370.99, -673.4) * mm, "radius": 3.18 * mm});
            skCircle(sketch, "E6.100.0.26", {"center": v(593.24, -673.4) * mm, "radius": 3.18 * mm});
            skCircle(sketch, "E6.102.0.26", {"center": v(847.24, -673.4) * mm, "radius": 3.18 * mm});
            skCircle(sketch, "E6.104.0.26", {"center": v(339.24, -673.4) * mm, "radius": 3.18 * mm});
            skCircle(sketch, "E6.106.0.26", {"center": v(561.49, -673.4) * mm, "radius": 3.18 * mm});
            skCircle(sketch, "E6.108.0.26", {"center": v(815.49, -673.4) * mm, "radius": 3.18 * mm});
            skCircle(sketch, "E6.110.0.26", {"center": v(307.49, -673.4) * mm, "radius": 3.18 * mm});
            skCircle(sketch, "E6.112.0.26", {"center": v(529.74, -673.4) * mm, "radius": 3.18 * mm});
            skCircle(sketch, "E6.114.0.26", {"center": v(180.49, -673.4) * mm, "radius": 3.18 * mm});
            skCircle(sketch, "E6.116.0.26", {"center": v(148.74, -673.4) * mm, "radius": 3.18 * mm});
            skCircle(sketch, "E6.118.0.26", {"center": v(910.74, -673.4) * mm, "radius": 3.18 * mm});
            skCircle(sketch, "E6.120.0.26", {"center": v(275.74, -673.4) * mm, "radius": 3.18 * mm});
            skCircle(sketch, "E6.122.0.26", {"center": v(243.99, -673.4) * mm, "radius": 3.18 * mm});
            skCircle(sketch, "E6.124.0.26", {"center": v(212.24, -673.4) * mm, "radius": 3.18 * mm});
            skCircle(sketch, "E6.126.0.26", {"center": v(783.74, -673.4) * mm, "radius": 3.18 * mm});
            skCircle(sketch, "E6.128.0.26", {"center": v(497.99, -673.4) * mm, "radius": 3.18 * mm});
            skCircle(sketch, "E6.130.0.26", {"center": v(402.74, -673.4) * mm, "radius": 3.18 * mm});
            skCircle(sketch, "E6.132.0.26", {"center": v(624.99, -673.4) * mm, "radius": 3.18 * mm});
            skCircle(sketch, "E6.134.0.26", {"center": v(751.99, -673.4) * mm, "radius": 3.18 * mm});
            skCircle(sketch, "E6.136.0.26", {"center": v(466.24, -673.4) * mm, "radius": 3.18 * mm});
            skCircle(sketch, "E6.138.0.26", {"center": v(688.49, -673.4) * mm, "radius": 3.18 * mm});
            skCircle(sketch, "E6.140.0.26", {"center": v(116.99, -673.4) * mm, "radius": 3.18 * mm});
            skCircle(sketch, "E6.142.0.26", {"center": v(85.24, -673.4) * mm, "radius": 3.18 * mm});
            skCircle(sketch, "E6.144.0.26", {"center": v(53.49, -673.4) * mm, "radius": 3.18 * mm});
            skLineSegment(sketch, "E6.146.0.26", {"start": v(-41.76, -673.4) * mm, "end": v(-10.01, -673.4) * mm, "construction": true});
            skCircle(sketch, "E6.149.0.26", {"center": v(21.74, -673.4) * mm, "radius": 3.18 * mm});
            skCircle(sketch, "E6.151.0.26", {"center": v(-10.01, -673.4) * mm, "radius": 3.18 * mm});
            skCircle(sketch, "E6.153.0.26", {"center": v(-41.76, -673.4) * mm, "radius": 3.18 * mm});
            skCircle(sketch, "E6.0.0.27", {"center": v(2244.24, -698.8) * mm, "radius": 3.18 * mm});
            skCircle(sketch, "E6.2.0.27", {"center": v(2180.74, -698.8) * mm, "radius": 3.18 * mm});
            skCircle(sketch, "E6.4.0.27", {"center": v(2339.49, -698.8) * mm, "radius": 3.18 * mm});
            skCircle(sketch, "E6.6.0.27", {"center": v(2307.74, -698.8) * mm, "radius": 3.18 * mm});
            skCircle(sketch, "E6.8.0.27", {"center": v(2275.99, -698.8) * mm, "radius": 3.18 * mm});
            skCircle(sketch, "E6.10.0.27", {"center": v(2212.49, -698.8) * mm, "radius": 3.18 * mm});
            skCircle(sketch, "E6.12.0.27", {"center": v(1958.49, -698.8) * mm, "radius": 3.18 * mm});
            skCircle(sketch, "E6.14.0.27", {"center": v(1894.99, -698.8) * mm, "radius": 3.18 * mm});
            skCircle(sketch, "E6.16.0.27", {"center": v(2117.24, -698.8) * mm, "radius": 3.18 * mm});
            skCircle(sketch, "E6.18.0.27", {"center": v(2085.49, -698.8) * mm, "radius": 3.18 * mm});
            skCircle(sketch, "E6.20.0.27", {"center": v(2053.74, -698.8) * mm, "radius": 3.18 * mm});
            skCircle(sketch, "E6.22.0.27", {"center": v(1926.74, -698.8) * mm, "radius": 3.18 * mm});
            skCircle(sketch, "E6.24.0.27", {"center": v(2021.99, -698.8) * mm, "radius": 3.18 * mm});
            skCircle(sketch, "E6.26.0.27", {"center": v(2148.99, -698.8) * mm, "radius": 3.18 * mm});
            skCircle(sketch, "E6.28.0.27", {"center": v(1990.24, -698.8) * mm, "radius": 3.18 * mm});
            skCircle(sketch, "E6.30.0.27", {"center": v(1450.49, -698.8) * mm, "radius": 3.18 * mm});
            skCircle(sketch, "E6.32.0.27", {"center": v(1228.24, -698.8) * mm, "radius": 3.18 * mm});
            skCircle(sketch, "E6.34.0.27", {"center": v(1736.24, -698.8) * mm, "radius": 3.18 * mm});
            skCircle(sketch, "E6.36.0.27", {"center": v(1386.99, -698.8) * mm, "radius": 3.18 * mm});
            skCircle(sketch, "E6.38.0.27", {"center": v(1164.74, -698.8) * mm, "radius": 3.18 * mm});
            skCircle(sketch, "E6.40.0.27", {"center": v(1672.74, -698.8) * mm, "radius": 3.18 * mm});
            skCircle(sketch, "E6.42.0.27", {"center": v(1101.24, -698.8) * mm, "radius": 3.18 * mm});
            skCircle(sketch, "E6.44.0.27", {"center": v(1609.24, -698.8) * mm, "radius": 3.18 * mm});
            skCircle(sketch, "E6.46.0.27", {"center": v(1355.24, -698.8) * mm, "radius": 3.18 * mm});
            skCircle(sketch, "E6.48.0.27", {"center": v(1863.24, -698.8) * mm, "radius": 3.18 * mm});
            skCircle(sketch, "E6.50.0.27", {"center": v(1069.49, -698.8) * mm, "radius": 3.18 * mm});
            skCircle(sketch, "E6.52.0.27", {"center": v(1577.49, -698.8) * mm, "radius": 3.18 * mm});
            skCircle(sketch, "E6.54.0.27", {"center": v(1323.49, -698.8) * mm, "radius": 3.18 * mm});
            skCircle(sketch, "E6.56.0.27", {"center": v(1831.49, -698.8) * mm, "radius": 3.18 * mm});
            skCircle(sketch, "E6.58.0.27", {"center": v(1037.74, -698.8) * mm, "radius": 3.18 * mm});
            skCircle(sketch, "E6.60.0.27", {"center": v(1545.74, -698.8) * mm, "radius": 3.18 * mm});
            skCircle(sketch, "E6.62.0.27", {"center": v(1418.74, -698.8) * mm, "radius": 3.18 * mm});
            skCircle(sketch, "E6.64.0.27", {"center": v(1005.99, -698.8) * mm, "radius": 3.18 * mm});
            skCircle(sketch, "E6.66.0.27", {"center": v(1513.99, -698.8) * mm, "radius": 3.18 * mm});
            skCircle(sketch, "E6.68.0.27", {"center": v(1799.74, -698.8) * mm, "radius": 3.18 * mm});
            skCircle(sketch, "E6.70.0.27", {"center": v(1291.74, -698.8) * mm, "radius": 3.18 * mm});
            skCircle(sketch, "E6.72.0.27", {"center": v(1132.99, -698.8) * mm, "radius": 3.18 * mm});
            skCircle(sketch, "E6.74.0.27", {"center": v(974.24, -698.8) * mm, "radius": 3.18 * mm});
            skCircle(sketch, "E6.76.0.27", {"center": v(1482.24, -698.8) * mm, "radius": 3.18 * mm});
            skCircle(sketch, "E6.78.0.27", {"center": v(1259.99, -698.8) * mm, "radius": 3.18 * mm});
            skCircle(sketch, "E6.80.0.27", {"center": v(1640.99, -698.8) * mm, "radius": 3.18 * mm});
            skCircle(sketch, "E6.82.0.27", {"center": v(1767.99, -698.8) * mm, "radius": 3.18 * mm});
            skCircle(sketch, "E6.84.0.27", {"center": v(1196.49, -698.8) * mm, "radius": 3.18 * mm});
            skCircle(sketch, "E6.86.0.27", {"center": v(1704.49, -698.8) * mm, "radius": 3.18 * mm});
            skCircle(sketch, "E6.88.0.27", {"center": v(720.24, -698.8) * mm, "radius": 3.18 * mm});
            skCircle(sketch, "E6.90.0.27", {"center": v(942.49, -698.8) * mm, "radius": 3.18 * mm});
            skCircle(sketch, "E6.92.0.27", {"center": v(878.99, -698.8) * mm, "radius": 3.18 * mm});
            skCircle(sketch, "E6.94.0.27", {"center": v(434.49, -698.8) * mm, "radius": 3.18 * mm});
            skCircle(sketch, "E6.96.0.27", {"center": v(656.74, -698.8) * mm, "radius": 3.18 * mm});
            skCircle(sketch, "E6.98.0.27", {"center": v(370.99, -698.8) * mm, "radius": 3.18 * mm});
            skCircle(sketch, "E6.100.0.27", {"center": v(593.24, -698.8) * mm, "radius": 3.18 * mm});
            skCircle(sketch, "E6.102.0.27", {"center": v(847.24, -698.8) * mm, "radius": 3.18 * mm});
            skCircle(sketch, "E6.104.0.27", {"center": v(339.24, -698.8) * mm, "radius": 3.18 * mm});
            skCircle(sketch, "E6.106.0.27", {"center": v(561.49, -698.8) * mm, "radius": 3.18 * mm});
            skCircle(sketch, "E6.108.0.27", {"center": v(815.49, -698.8) * mm, "radius": 3.18 * mm});
            skCircle(sketch, "E6.110.0.27", {"center": v(307.49, -698.8) * mm, "radius": 3.18 * mm});
            skCircle(sketch, "E6.112.0.27", {"center": v(529.74, -698.8) * mm, "radius": 3.18 * mm});
            skCircle(sketch, "E6.114.0.27", {"center": v(180.49, -698.8) * mm, "radius": 3.18 * mm});
            skCircle(sketch, "E6.116.0.27", {"center": v(148.74, -698.8) * mm, "radius": 3.18 * mm});
            skCircle(sketch, "E6.118.0.27", {"center": v(910.74, -698.8) * mm, "radius": 3.18 * mm});
            skCircle(sketch, "E6.120.0.27", {"center": v(275.74, -698.8) * mm, "radius": 3.18 * mm});
            skCircle(sketch, "E6.122.0.27", {"center": v(243.99, -698.8) * mm, "radius": 3.18 * mm});
            skCircle(sketch, "E6.124.0.27", {"center": v(212.24, -698.8) * mm, "radius": 3.18 * mm});
            skCircle(sketch, "E6.126.0.27", {"center": v(783.74, -698.8) * mm, "radius": 3.18 * mm});
            skCircle(sketch, "E6.128.0.27", {"center": v(497.99, -698.8) * mm, "radius": 3.18 * mm});
            skCircle(sketch, "E6.130.0.27", {"center": v(402.74, -698.8) * mm, "radius": 3.18 * mm});
            skCircle(sketch, "E6.132.0.27", {"center": v(624.99, -698.8) * mm, "radius": 3.18 * mm});
            skCircle(sketch, "E6.134.0.27", {"center": v(751.99, -698.8) * mm, "radius": 3.18 * mm});
            skCircle(sketch, "E6.136.0.27", {"center": v(466.24, -698.8) * mm, "radius": 3.18 * mm});
            skCircle(sketch, "E6.138.0.27", {"center": v(688.49, -698.8) * mm, "radius": 3.18 * mm});
            skCircle(sketch, "E6.140.0.27", {"center": v(116.99, -698.8) * mm, "radius": 3.18 * mm});
            skCircle(sketch, "E6.142.0.27", {"center": v(85.24, -698.8) * mm, "radius": 3.18 * mm});
            skCircle(sketch, "E6.144.0.27", {"center": v(53.49, -698.8) * mm, "radius": 3.18 * mm});
            skLineSegment(sketch, "E6.146.0.27", {"start": v(-41.76, -698.8) * mm, "end": v(-10.01, -698.8) * mm, "construction": true});
            skCircle(sketch, "E6.149.0.27", {"center": v(21.74, -698.8) * mm, "radius": 3.18 * mm});
            skCircle(sketch, "E6.151.0.27", {"center": v(-10.01, -698.8) * mm, "radius": 3.18 * mm});
            skCircle(sketch, "E6.153.0.27", {"center": v(-41.76, -698.8) * mm, "radius": 3.18 * mm});
            skCircle(sketch, "E6.0.0.28", {"center": v(2244.24, -724.2) * mm, "radius": 3.18 * mm});
            skCircle(sketch, "E6.2.0.28", {"center": v(2180.74, -724.2) * mm, "radius": 3.18 * mm});
            skCircle(sketch, "E6.4.0.28", {"center": v(2339.49, -724.2) * mm, "radius": 3.18 * mm});
            skCircle(sketch, "E6.6.0.28", {"center": v(2307.74, -724.2) * mm, "radius": 3.18 * mm});
            skCircle(sketch, "E6.8.0.28", {"center": v(2275.99, -724.2) * mm, "radius": 3.18 * mm});
            skCircle(sketch, "E6.10.0.28", {"center": v(2212.49, -724.2) * mm, "radius": 3.18 * mm});
            skCircle(sketch, "E6.12.0.28", {"center": v(1958.49, -724.2) * mm, "radius": 3.18 * mm});
            skCircle(sketch, "E6.14.0.28", {"center": v(1894.99, -724.2) * mm, "radius": 3.18 * mm});
            skCircle(sketch, "E6.16.0.28", {"center": v(2117.24, -724.2) * mm, "radius": 3.18 * mm});
            skCircle(sketch, "E6.18.0.28", {"center": v(2085.49, -724.2) * mm, "radius": 3.18 * mm});
            skCircle(sketch, "E6.20.0.28", {"center": v(2053.74, -724.2) * mm, "radius": 3.18 * mm});
            skCircle(sketch, "E6.22.0.28", {"center": v(1926.74, -724.2) * mm, "radius": 3.18 * mm});
            skCircle(sketch, "E6.24.0.28", {"center": v(2021.99, -724.2) * mm, "radius": 3.18 * mm});
            skCircle(sketch, "E6.26.0.28", {"center": v(2148.99, -724.2) * mm, "radius": 3.18 * mm});
            skCircle(sketch, "E6.28.0.28", {"center": v(1990.24, -724.2) * mm, "radius": 3.18 * mm});
            skCircle(sketch, "E6.30.0.28", {"center": v(1450.49, -724.2) * mm, "radius": 3.18 * mm});
            skCircle(sketch, "E6.32.0.28", {"center": v(1228.24, -724.2) * mm, "radius": 3.18 * mm});
            skCircle(sketch, "E6.34.0.28", {"center": v(1736.24, -724.2) * mm, "radius": 3.18 * mm});
            skCircle(sketch, "E6.36.0.28", {"center": v(1386.99, -724.2) * mm, "radius": 3.18 * mm});
            skCircle(sketch, "E6.38.0.28", {"center": v(1164.74, -724.2) * mm, "radius": 3.18 * mm});
            skCircle(sketch, "E6.40.0.28", {"center": v(1672.74, -724.2) * mm, "radius": 3.18 * mm});
            skCircle(sketch, "E6.42.0.28", {"center": v(1101.24, -724.2) * mm, "radius": 3.18 * mm});
            skCircle(sketch, "E6.44.0.28", {"center": v(1609.24, -724.2) * mm, "radius": 3.18 * mm});
            skCircle(sketch, "E6.46.0.28", {"center": v(1355.24, -724.2) * mm, "radius": 3.18 * mm});
            skCircle(sketch, "E6.48.0.28", {"center": v(1863.24, -724.2) * mm, "radius": 3.18 * mm});
            skCircle(sketch, "E6.50.0.28", {"center": v(1069.49, -724.2) * mm, "radius": 3.18 * mm});
            skCircle(sketch, "E6.52.0.28", {"center": v(1577.49, -724.2) * mm, "radius": 3.18 * mm});
            skCircle(sketch, "E6.54.0.28", {"center": v(1323.49, -724.2) * mm, "radius": 3.18 * mm});
            skCircle(sketch, "E6.56.0.28", {"center": v(1831.49, -724.2) * mm, "radius": 3.18 * mm});
            skCircle(sketch, "E6.58.0.28", {"center": v(1037.74, -724.2) * mm, "radius": 3.18 * mm});
            skCircle(sketch, "E6.60.0.28", {"center": v(1545.74, -724.2) * mm, "radius": 3.18 * mm});
            skCircle(sketch, "E6.62.0.28", {"center": v(1418.74, -724.2) * mm, "radius": 3.18 * mm});
            skCircle(sketch, "E6.64.0.28", {"center": v(1005.99, -724.2) * mm, "radius": 3.18 * mm});
            skCircle(sketch, "E6.66.0.28", {"center": v(1513.99, -724.2) * mm, "radius": 3.18 * mm});
            skCircle(sketch, "E6.68.0.28", {"center": v(1799.74, -724.2) * mm, "radius": 3.18 * mm});
            skCircle(sketch, "E6.70.0.28", {"center": v(1291.74, -724.2) * mm, "radius": 3.18 * mm});
            skCircle(sketch, "E6.72.0.28", {"center": v(1132.99, -724.2) * mm, "radius": 3.18 * mm});
            skCircle(sketch, "E6.74.0.28", {"center": v(974.24, -724.2) * mm, "radius": 3.18 * mm});
            skCircle(sketch, "E6.76.0.28", {"center": v(1482.24, -724.2) * mm, "radius": 3.18 * mm});
            skCircle(sketch, "E6.78.0.28", {"center": v(1259.99, -724.2) * mm, "radius": 3.18 * mm});
            skCircle(sketch, "E6.80.0.28", {"center": v(1640.99, -724.2) * mm, "radius": 3.18 * mm});
            skCircle(sketch, "E6.82.0.28", {"center": v(1767.99, -724.2) * mm, "radius": 3.18 * mm});
            skCircle(sketch, "E6.84.0.28", {"center": v(1196.49, -724.2) * mm, "radius": 3.18 * mm});
            skCircle(sketch, "E6.86.0.28", {"center": v(1704.49, -724.2) * mm, "radius": 3.18 * mm});
            skCircle(sketch, "E6.88.0.28", {"center": v(720.24, -724.2) * mm, "radius": 3.18 * mm});
            skCircle(sketch, "E6.90.0.28", {"center": v(942.49, -724.2) * mm, "radius": 3.18 * mm});
            skCircle(sketch, "E6.92.0.28", {"center": v(878.99, -724.2) * mm, "radius": 3.18 * mm});
            skCircle(sketch, "E6.94.0.28", {"center": v(434.49, -724.2) * mm, "radius": 3.18 * mm});
            skCircle(sketch, "E6.96.0.28", {"center": v(656.74, -724.2) * mm, "radius": 3.18 * mm});
            skCircle(sketch, "E6.98.0.28", {"center": v(370.99, -724.2) * mm, "radius": 3.18 * mm});
            skCircle(sketch, "E6.100.0.28", {"center": v(593.24, -724.2) * mm, "radius": 3.18 * mm});
            skCircle(sketch, "E6.102.0.28", {"center": v(847.24, -724.2) * mm, "radius": 3.18 * mm});
            skCircle(sketch, "E6.104.0.28", {"center": v(339.24, -724.2) * mm, "radius": 3.18 * mm});
            skCircle(sketch, "E6.106.0.28", {"center": v(561.49, -724.2) * mm, "radius": 3.18 * mm});
            skCircle(sketch, "E6.108.0.28", {"center": v(815.49, -724.2) * mm, "radius": 3.18 * mm});
            skCircle(sketch, "E6.110.0.28", {"center": v(307.49, -724.2) * mm, "radius": 3.18 * mm});
            skCircle(sketch, "E6.112.0.28", {"center": v(529.74, -724.2) * mm, "radius": 3.18 * mm});
            skCircle(sketch, "E6.114.0.28", {"center": v(180.49, -724.2) * mm, "radius": 3.18 * mm});
            skCircle(sketch, "E6.116.0.28", {"center": v(148.74, -724.2) * mm, "radius": 3.18 * mm});
            skCircle(sketch, "E6.118.0.28", {"center": v(910.74, -724.2) * mm, "radius": 3.18 * mm});
            skCircle(sketch, "E6.120.0.28", {"center": v(275.74, -724.2) * mm, "radius": 3.18 * mm});
            skCircle(sketch, "E6.122.0.28", {"center": v(243.99, -724.2) * mm, "radius": 3.18 * mm});
            skCircle(sketch, "E6.124.0.28", {"center": v(212.24, -724.2) * mm, "radius": 3.18 * mm});
            skCircle(sketch, "E6.126.0.28", {"center": v(783.74, -724.2) * mm, "radius": 3.18 * mm});
            skCircle(sketch, "E6.128.0.28", {"center": v(497.99, -724.2) * mm, "radius": 3.18 * mm});
            skCircle(sketch, "E6.130.0.28", {"center": v(402.74, -724.2) * mm, "radius": 3.18 * mm});
            skCircle(sketch, "E6.132.0.28", {"center": v(624.99, -724.2) * mm, "radius": 3.18 * mm});
            skCircle(sketch, "E6.134.0.28", {"center": v(751.99, -724.2) * mm, "radius": 3.18 * mm});
            skCircle(sketch, "E6.136.0.28", {"center": v(466.24, -724.2) * mm, "radius": 3.18 * mm});
            skCircle(sketch, "E6.138.0.28", {"center": v(688.49, -724.2) * mm, "radius": 3.18 * mm});
            skCircle(sketch, "E6.140.0.28", {"center": v(116.99, -724.2) * mm, "radius": 3.18 * mm});
            skCircle(sketch, "E6.142.0.28", {"center": v(85.24, -724.2) * mm, "radius": 3.18 * mm});
            skCircle(sketch, "E6.144.0.28", {"center": v(53.49, -724.2) * mm, "radius": 3.18 * mm});
            skLineSegment(sketch, "E6.146.0.28", {"start": v(-41.76, -724.2) * mm, "end": v(-10.01, -724.2) * mm, "construction": true});
            skCircle(sketch, "E6.149.0.28", {"center": v(21.74, -724.2) * mm, "radius": 3.18 * mm});
            skCircle(sketch, "E6.151.0.28", {"center": v(-10.01, -724.2) * mm, "radius": 3.18 * mm});
            skCircle(sketch, "E6.153.0.28", {"center": v(-41.76, -724.2) * mm, "radius": 3.18 * mm});
            skCircle(sketch, "E6.0.0.29", {"center": v(2244.24, -749.6) * mm, "radius": 3.18 * mm});
            skCircle(sketch, "E6.2.0.29", {"center": v(2180.74, -749.6) * mm, "radius": 3.18 * mm});
            skCircle(sketch, "E6.4.0.29", {"center": v(2339.49, -749.6) * mm, "radius": 3.18 * mm});
            skCircle(sketch, "E6.6.0.29", {"center": v(2307.74, -749.6) * mm, "radius": 3.18 * mm});
            skCircle(sketch, "E6.8.0.29", {"center": v(2275.99, -749.6) * mm, "radius": 3.18 * mm});
            skCircle(sketch, "E6.10.0.29", {"center": v(2212.49, -749.6) * mm, "radius": 3.18 * mm});
            skCircle(sketch, "E6.12.0.29", {"center": v(1958.49, -749.6) * mm, "radius": 3.18 * mm});
            skCircle(sketch, "E6.14.0.29", {"center": v(1894.99, -749.6) * mm, "radius": 3.18 * mm});
            skCircle(sketch, "E6.16.0.29", {"center": v(2117.24, -749.6) * mm, "radius": 3.18 * mm});
            skCircle(sketch, "E6.18.0.29", {"center": v(2085.49, -749.6) * mm, "radius": 3.18 * mm});
            skCircle(sketch, "E6.20.0.29", {"center": v(2053.74, -749.6) * mm, "radius": 3.18 * mm});
            skCircle(sketch, "E6.22.0.29", {"center": v(1926.74, -749.6) * mm, "radius": 3.18 * mm});
            skCircle(sketch, "E6.24.0.29", {"center": v(2021.99, -749.6) * mm, "radius": 3.18 * mm});
            skCircle(sketch, "E6.26.0.29", {"center": v(2148.99, -749.6) * mm, "radius": 3.18 * mm});
            skCircle(sketch, "E6.28.0.29", {"center": v(1990.24, -749.6) * mm, "radius": 3.18 * mm});
            skCircle(sketch, "E6.30.0.29", {"center": v(1450.49, -749.6) * mm, "radius": 3.18 * mm});
            skCircle(sketch, "E6.32.0.29", {"center": v(1228.24, -749.6) * mm, "radius": 3.18 * mm});
            skCircle(sketch, "E6.34.0.29", {"center": v(1736.24, -749.6) * mm, "radius": 3.18 * mm});
            skCircle(sketch, "E6.36.0.29", {"center": v(1386.99, -749.6) * mm, "radius": 3.18 * mm});
            skCircle(sketch, "E6.38.0.29", {"center": v(1164.74, -749.6) * mm, "radius": 3.18 * mm});
            skCircle(sketch, "E6.40.0.29", {"center": v(1672.74, -749.6) * mm, "radius": 3.18 * mm});
            skCircle(sketch, "E6.42.0.29", {"center": v(1101.24, -749.6) * mm, "radius": 3.18 * mm});
            skCircle(sketch, "E6.44.0.29", {"center": v(1609.24, -749.6) * mm, "radius": 3.18 * mm});
            skCircle(sketch, "E6.46.0.29", {"center": v(1355.24, -749.6) * mm, "radius": 3.18 * mm});
            skCircle(sketch, "E6.48.0.29", {"center": v(1863.24, -749.6) * mm, "radius": 3.18 * mm});
            skCircle(sketch, "E6.50.0.29", {"center": v(1069.49, -749.6) * mm, "radius": 3.18 * mm});
            skCircle(sketch, "E6.52.0.29", {"center": v(1577.49, -749.6) * mm, "radius": 3.18 * mm});
            skCircle(sketch, "E6.54.0.29", {"center": v(1323.49, -749.6) * mm, "radius": 3.18 * mm});
            skCircle(sketch, "E6.56.0.29", {"center": v(1831.49, -749.6) * mm, "radius": 3.18 * mm});
            skCircle(sketch, "E6.58.0.29", {"center": v(1037.74, -749.6) * mm, "radius": 3.18 * mm});
            skCircle(sketch, "E6.60.0.29", {"center": v(1545.74, -749.6) * mm, "radius": 3.18 * mm});
            skCircle(sketch, "E6.62.0.29", {"center": v(1418.74, -749.6) * mm, "radius": 3.18 * mm});
            skCircle(sketch, "E6.64.0.29", {"center": v(1005.99, -749.6) * mm, "radius": 3.18 * mm});
            skCircle(sketch, "E6.66.0.29", {"center": v(1513.99, -749.6) * mm, "radius": 3.18 * mm});
            skCircle(sketch, "E6.68.0.29", {"center": v(1799.74, -749.6) * mm, "radius": 3.18 * mm});
            skCircle(sketch, "E6.70.0.29", {"center": v(1291.74, -749.6) * mm, "radius": 3.18 * mm});
            skCircle(sketch, "E6.72.0.29", {"center": v(1132.99, -749.6) * mm, "radius": 3.18 * mm});
            skCircle(sketch, "E6.74.0.29", {"center": v(974.24, -749.6) * mm, "radius": 3.18 * mm});
            skCircle(sketch, "E6.76.0.29", {"center": v(1482.24, -749.6) * mm, "radius": 3.18 * mm});
            skCircle(sketch, "E6.78.0.29", {"center": v(1259.99, -749.6) * mm, "radius": 3.18 * mm});
            skCircle(sketch, "E6.80.0.29", {"center": v(1640.99, -749.6) * mm, "radius": 3.18 * mm});
            skCircle(sketch, "E6.82.0.29", {"center": v(1767.99, -749.6) * mm, "radius": 3.18 * mm});
            skCircle(sketch, "E6.84.0.29", {"center": v(1196.49, -749.6) * mm, "radius": 3.18 * mm});
            skCircle(sketch, "E6.86.0.29", {"center": v(1704.49, -749.6) * mm, "radius": 3.18 * mm});
            skCircle(sketch, "E6.88.0.29", {"center": v(720.24, -749.6) * mm, "radius": 3.18 * mm});
            skCircle(sketch, "E6.90.0.29", {"center": v(942.49, -749.6) * mm, "radius": 3.18 * mm});
            skCircle(sketch, "E6.92.0.29", {"center": v(878.99, -749.6) * mm, "radius": 3.18 * mm});
            skCircle(sketch, "E6.94.0.29", {"center": v(434.49, -749.6) * mm, "radius": 3.18 * mm});
            skCircle(sketch, "E6.96.0.29", {"center": v(656.74, -749.6) * mm, "radius": 3.18 * mm});
            skCircle(sketch, "E6.98.0.29", {"center": v(370.99, -749.6) * mm, "radius": 3.18 * mm});
            skCircle(sketch, "E6.100.0.29", {"center": v(593.24, -749.6) * mm, "radius": 3.18 * mm});
            skCircle(sketch, "E6.102.0.29", {"center": v(847.24, -749.6) * mm, "radius": 3.18 * mm});
            skCircle(sketch, "E6.104.0.29", {"center": v(339.24, -749.6) * mm, "radius": 3.18 * mm});
            skCircle(sketch, "E6.106.0.29", {"center": v(561.49, -749.6) * mm, "radius": 3.18 * mm});
            skCircle(sketch, "E6.108.0.29", {"center": v(815.49, -749.6) * mm, "radius": 3.18 * mm});
            skCircle(sketch, "E6.110.0.29", {"center": v(307.49, -749.6) * mm, "radius": 3.18 * mm});
            skCircle(sketch, "E6.112.0.29", {"center": v(529.74, -749.6) * mm, "radius": 3.18 * mm});
            skCircle(sketch, "E6.114.0.29", {"center": v(180.49, -749.6) * mm, "radius": 3.18 * mm});
            skCircle(sketch, "E6.116.0.29", {"center": v(148.74, -749.6) * mm, "radius": 3.18 * mm});
            skCircle(sketch, "E6.118.0.29", {"center": v(910.74, -749.6) * mm, "radius": 3.18 * mm});
            skCircle(sketch, "E6.120.0.29", {"center": v(275.74, -749.6) * mm, "radius": 3.18 * mm});
            skCircle(sketch, "E6.122.0.29", {"center": v(243.99, -749.6) * mm, "radius": 3.18 * mm});
            skCircle(sketch, "E6.124.0.29", {"center": v(212.24, -749.6) * mm, "radius": 3.18 * mm});
            skCircle(sketch, "E6.126.0.29", {"center": v(783.74, -749.6) * mm, "radius": 3.18 * mm});
            skCircle(sketch, "E6.128.0.29", {"center": v(497.99, -749.6) * mm, "radius": 3.18 * mm});
            skCircle(sketch, "E6.130.0.29", {"center": v(402.74, -749.6) * mm, "radius": 3.18 * mm});
            skCircle(sketch, "E6.132.0.29", {"center": v(624.99, -749.6) * mm, "radius": 3.18 * mm});
            skCircle(sketch, "E6.134.0.29", {"center": v(751.99, -749.6) * mm, "radius": 3.18 * mm});
            skCircle(sketch, "E6.136.0.29", {"center": v(466.24, -749.6) * mm, "radius": 3.18 * mm});
            skCircle(sketch, "E6.138.0.29", {"center": v(688.49, -749.6) * mm, "radius": 3.18 * mm});
            skCircle(sketch, "E6.140.0.29", {"center": v(116.99, -749.6) * mm, "radius": 3.18 * mm});
            skCircle(sketch, "E6.142.0.29", {"center": v(85.24, -749.6) * mm, "radius": 3.18 * mm});
            skCircle(sketch, "E6.144.0.29", {"center": v(53.49, -749.6) * mm, "radius": 3.18 * mm});
            skLineSegment(sketch, "E6.146.0.29", {"start": v(-41.76, -749.6) * mm, "end": v(-10.01, -749.6) * mm, "construction": true});
            skCircle(sketch, "E6.149.0.29", {"center": v(21.74, -749.6) * mm, "radius": 3.18 * mm});
            skCircle(sketch, "E6.151.0.29", {"center": v(-10.01, -749.6) * mm, "radius": 3.18 * mm});
            skCircle(sketch, "E6.153.0.29", {"center": v(-41.76, -749.6) * mm, "radius": 3.18 * mm});
            skCircle(sketch, "E6.0.0.30", {"center": v(2244.24, -775) * mm, "radius": 3.18 * mm});
            skCircle(sketch, "E6.2.0.30", {"center": v(2180.74, -775) * mm, "radius": 3.18 * mm});
            skCircle(sketch, "E6.4.0.30", {"center": v(2339.49, -775) * mm, "radius": 3.18 * mm});
            skCircle(sketch, "E6.6.0.30", {"center": v(2307.74, -775) * mm, "radius": 3.18 * mm});
            skCircle(sketch, "E6.8.0.30", {"center": v(2275.99, -775) * mm, "radius": 3.18 * mm});
            skCircle(sketch, "E6.10.0.30", {"center": v(2212.49, -775) * mm, "radius": 3.18 * mm});
            skCircle(sketch, "E6.12.0.30", {"center": v(1958.49, -775) * mm, "radius": 3.18 * mm});
            skCircle(sketch, "E6.14.0.30", {"center": v(1894.99, -775) * mm, "radius": 3.18 * mm});
            skCircle(sketch, "E6.16.0.30", {"center": v(2117.24, -775) * mm, "radius": 3.18 * mm});
            skCircle(sketch, "E6.18.0.30", {"center": v(2085.49, -775) * mm, "radius": 3.18 * mm});
            skCircle(sketch, "E6.20.0.30", {"center": v(2053.74, -775) * mm, "radius": 3.18 * mm});
            skCircle(sketch, "E6.22.0.30", {"center": v(1926.74, -775) * mm, "radius": 3.18 * mm});
            skCircle(sketch, "E6.24.0.30", {"center": v(2021.99, -775) * mm, "radius": 3.18 * mm});
            skCircle(sketch, "E6.26.0.30", {"center": v(2148.99, -775) * mm, "radius": 3.18 * mm});
            skCircle(sketch, "E6.28.0.30", {"center": v(1990.24, -775) * mm, "radius": 3.18 * mm});
            skCircle(sketch, "E6.30.0.30", {"center": v(1450.49, -775) * mm, "radius": 3.18 * mm});
            skCircle(sketch, "E6.32.0.30", {"center": v(1228.24, -775) * mm, "radius": 3.18 * mm});
            skCircle(sketch, "E6.34.0.30", {"center": v(1736.24, -775) * mm, "radius": 3.18 * mm});
            skCircle(sketch, "E6.36.0.30", {"center": v(1386.99, -775) * mm, "radius": 3.18 * mm});
            skCircle(sketch, "E6.38.0.30", {"center": v(1164.74, -775) * mm, "radius": 3.18 * mm});
            skCircle(sketch, "E6.40.0.30", {"center": v(1672.74, -775) * mm, "radius": 3.18 * mm});
            skCircle(sketch, "E6.42.0.30", {"center": v(1101.24, -775) * mm, "radius": 3.18 * mm});
            skCircle(sketch, "E6.44.0.30", {"center": v(1609.24, -775) * mm, "radius": 3.18 * mm});
            skCircle(sketch, "E6.46.0.30", {"center": v(1355.24, -775) * mm, "radius": 3.18 * mm});
            skCircle(sketch, "E6.48.0.30", {"center": v(1863.24, -775) * mm, "radius": 3.18 * mm});
            skCircle(sketch, "E6.50.0.30", {"center": v(1069.49, -775) * mm, "radius": 3.18 * mm});
            skCircle(sketch, "E6.52.0.30", {"center": v(1577.49, -775) * mm, "radius": 3.18 * mm});
            skCircle(sketch, "E6.54.0.30", {"center": v(1323.49, -775) * mm, "radius": 3.18 * mm});
            skCircle(sketch, "E6.56.0.30", {"center": v(1831.49, -775) * mm, "radius": 3.18 * mm});
            skCircle(sketch, "E6.58.0.30", {"center": v(1037.74, -775) * mm, "radius": 3.18 * mm});
            skCircle(sketch, "E6.60.0.30", {"center": v(1545.74, -775) * mm, "radius": 3.18 * mm});
            skCircle(sketch, "E6.62.0.30", {"center": v(1418.74, -775) * mm, "radius": 3.18 * mm});
            skCircle(sketch, "E6.64.0.30", {"center": v(1005.99, -775) * mm, "radius": 3.18 * mm});
            skCircle(sketch, "E6.66.0.30", {"center": v(1513.99, -775) * mm, "radius": 3.18 * mm});
            skCircle(sketch, "E6.68.0.30", {"center": v(1799.74, -775) * mm, "radius": 3.18 * mm});
            skCircle(sketch, "E6.70.0.30", {"center": v(1291.74, -775) * mm, "radius": 3.18 * mm});
            skCircle(sketch, "E6.72.0.30", {"center": v(1132.99, -775) * mm, "radius": 3.18 * mm});
            skCircle(sketch, "E6.74.0.30", {"center": v(974.24, -775) * mm, "radius": 3.18 * mm});
            skCircle(sketch, "E6.76.0.30", {"center": v(1482.24, -775) * mm, "radius": 3.18 * mm});
            skCircle(sketch, "E6.78.0.30", {"center": v(1259.99, -775) * mm, "radius": 3.18 * mm});
            skCircle(sketch, "E6.80.0.30", {"center": v(1640.99, -775) * mm, "radius": 3.18 * mm});
            skCircle(sketch, "E6.82.0.30", {"center": v(1767.99, -775) * mm, "radius": 3.18 * mm});
            skCircle(sketch, "E6.84.0.30", {"center": v(1196.49, -775) * mm, "radius": 3.18 * mm});
            skCircle(sketch, "E6.86.0.30", {"center": v(1704.49, -775) * mm, "radius": 3.18 * mm});
            skCircle(sketch, "E6.88.0.30", {"center": v(720.24, -775) * mm, "radius": 3.18 * mm});
            skCircle(sketch, "E6.90.0.30", {"center": v(942.49, -775) * mm, "radius": 3.18 * mm});
            skCircle(sketch, "E6.92.0.30", {"center": v(878.99, -775) * mm, "radius": 3.18 * mm});
            skCircle(sketch, "E6.94.0.30", {"center": v(434.49, -775) * mm, "radius": 3.18 * mm});
            skCircle(sketch, "E6.96.0.30", {"center": v(656.74, -775) * mm, "radius": 3.18 * mm});
            skCircle(sketch, "E6.98.0.30", {"center": v(370.99, -775) * mm, "radius": 3.18 * mm});
            skCircle(sketch, "E6.100.0.30", {"center": v(593.24, -775) * mm, "radius": 3.18 * mm});
            skCircle(sketch, "E6.102.0.30", {"center": v(847.24, -775) * mm, "radius": 3.18 * mm});
            skCircle(sketch, "E6.104.0.30", {"center": v(339.24, -775) * mm, "radius": 3.18 * mm});
            skCircle(sketch, "E6.106.0.30", {"center": v(561.49, -775) * mm, "radius": 3.18 * mm});
            skCircle(sketch, "E6.108.0.30", {"center": v(815.49, -775) * mm, "radius": 3.18 * mm});
            skCircle(sketch, "E6.110.0.30", {"center": v(307.49, -775) * mm, "radius": 3.18 * mm});
            skCircle(sketch, "E6.112.0.30", {"center": v(529.74, -775) * mm, "radius": 3.18 * mm});
            skCircle(sketch, "E6.114.0.30", {"center": v(180.49, -775) * mm, "radius": 3.18 * mm});
            skCircle(sketch, "E6.116.0.30", {"center": v(148.74, -775) * mm, "radius": 3.18 * mm});
            skCircle(sketch, "E6.118.0.30", {"center": v(910.74, -775) * mm, "radius": 3.18 * mm});
            skCircle(sketch, "E6.120.0.30", {"center": v(275.74, -775) * mm, "radius": 3.18 * mm});
            skCircle(sketch, "E6.122.0.30", {"center": v(243.99, -775) * mm, "radius": 3.18 * mm});
            skCircle(sketch, "E6.124.0.30", {"center": v(212.24, -775) * mm, "radius": 3.18 * mm});
            skCircle(sketch, "E6.126.0.30", {"center": v(783.74, -775) * mm, "radius": 3.18 * mm});
            skCircle(sketch, "E6.128.0.30", {"center": v(497.99, -775) * mm, "radius": 3.18 * mm});
            skCircle(sketch, "E6.130.0.30", {"center": v(402.74, -775) * mm, "radius": 3.18 * mm});
            skCircle(sketch, "E6.132.0.30", {"center": v(624.99, -775) * mm, "radius": 3.18 * mm});
            skCircle(sketch, "E6.134.0.30", {"center": v(751.99, -775) * mm, "radius": 3.18 * mm});
            skCircle(sketch, "E6.136.0.30", {"center": v(466.24, -775) * mm, "radius": 3.18 * mm});
            skCircle(sketch, "E6.138.0.30", {"center": v(688.49, -775) * mm, "radius": 3.18 * mm});
            skCircle(sketch, "E6.140.0.30", {"center": v(116.99, -775) * mm, "radius": 3.18 * mm});
            skCircle(sketch, "E6.142.0.30", {"center": v(85.24, -775) * mm, "radius": 3.18 * mm});
            skCircle(sketch, "E6.144.0.30", {"center": v(53.49, -775) * mm, "radius": 3.18 * mm});
            skLineSegment(sketch, "E6.146.0.30", {"start": v(-41.76, -775) * mm, "end": v(-10.01, -775) * mm, "construction": true});
            skCircle(sketch, "E6.149.0.30", {"center": v(21.74, -775) * mm, "radius": 3.18 * mm});
            skCircle(sketch, "E6.151.0.30", {"center": v(-10.01, -775) * mm, "radius": 3.18 * mm});
            skCircle(sketch, "E6.153.0.30", {"center": v(-41.76, -775) * mm, "radius": 3.18 * mm});
            skCircle(sketch, "E6.0.0.31", {"center": v(2244.24, -800.4) * mm, "radius": 3.18 * mm});
            skCircle(sketch, "E6.2.0.31", {"center": v(2180.74, -800.4) * mm, "radius": 3.18 * mm});
            skCircle(sketch, "E6.4.0.31", {"center": v(2339.49, -800.4) * mm, "radius": 3.18 * mm});
            skCircle(sketch, "E6.6.0.31", {"center": v(2307.74, -800.4) * mm, "radius": 3.18 * mm});
            skCircle(sketch, "E6.8.0.31", {"center": v(2275.99, -800.4) * mm, "radius": 3.18 * mm});
            skCircle(sketch, "E6.10.0.31", {"center": v(2212.49, -800.4) * mm, "radius": 3.18 * mm});
            skCircle(sketch, "E6.12.0.31", {"center": v(1958.49, -800.4) * mm, "radius": 3.18 * mm});
            skCircle(sketch, "E6.14.0.31", {"center": v(1894.99, -800.4) * mm, "radius": 3.18 * mm});
            skCircle(sketch, "E6.16.0.31", {"center": v(2117.24, -800.4) * mm, "radius": 3.18 * mm});
            skCircle(sketch, "E6.18.0.31", {"center": v(2085.49, -800.4) * mm, "radius": 3.18 * mm});
            skCircle(sketch, "E6.20.0.31", {"center": v(2053.74, -800.4) * mm, "radius": 3.18 * mm});
            skCircle(sketch, "E6.22.0.31", {"center": v(1926.74, -800.4) * mm, "radius": 3.18 * mm});
            skCircle(sketch, "E6.24.0.31", {"center": v(2021.99, -800.4) * mm, "radius": 3.18 * mm});
            skCircle(sketch, "E6.26.0.31", {"center": v(2148.99, -800.4) * mm, "radius": 3.18 * mm});
            skCircle(sketch, "E6.28.0.31", {"center": v(1990.24, -800.4) * mm, "radius": 3.18 * mm});
            skCircle(sketch, "E6.30.0.31", {"center": v(1450.49, -800.4) * mm, "radius": 3.18 * mm});
            skCircle(sketch, "E6.32.0.31", {"center": v(1228.24, -800.4) * mm, "radius": 3.18 * mm});
            skCircle(sketch, "E6.34.0.31", {"center": v(1736.24, -800.4) * mm, "radius": 3.18 * mm});
            skCircle(sketch, "E6.36.0.31", {"center": v(1386.99, -800.4) * mm, "radius": 3.18 * mm});
            skCircle(sketch, "E6.38.0.31", {"center": v(1164.74, -800.4) * mm, "radius": 3.18 * mm});
            skCircle(sketch, "E6.40.0.31", {"center": v(1672.74, -800.4) * mm, "radius": 3.18 * mm});
            skCircle(sketch, "E6.42.0.31", {"center": v(1101.24, -800.4) * mm, "radius": 3.18 * mm});
            skCircle(sketch, "E6.44.0.31", {"center": v(1609.24, -800.4) * mm, "radius": 3.18 * mm});
            skCircle(sketch, "E6.46.0.31", {"center": v(1355.24, -800.4) * mm, "radius": 3.18 * mm});
            skCircle(sketch, "E6.48.0.31", {"center": v(1863.24, -800.4) * mm, "radius": 3.18 * mm});
            skCircle(sketch, "E6.50.0.31", {"center": v(1069.49, -800.4) * mm, "radius": 3.18 * mm});
            skCircle(sketch, "E6.52.0.31", {"center": v(1577.49, -800.4) * mm, "radius": 3.18 * mm});
            skCircle(sketch, "E6.54.0.31", {"center": v(1323.49, -800.4) * mm, "radius": 3.18 * mm});
            skCircle(sketch, "E6.56.0.31", {"center": v(1831.49, -800.4) * mm, "radius": 3.18 * mm});
            skCircle(sketch, "E6.58.0.31", {"center": v(1037.74, -800.4) * mm, "radius": 3.18 * mm});
            skCircle(sketch, "E6.60.0.31", {"center": v(1545.74, -800.4) * mm, "radius": 3.18 * mm});
            skCircle(sketch, "E6.62.0.31", {"center": v(1418.74, -800.4) * mm, "radius": 3.18 * mm});
            skCircle(sketch, "E6.64.0.31", {"center": v(1005.99, -800.4) * mm, "radius": 3.18 * mm});
            skCircle(sketch, "E6.66.0.31", {"center": v(1513.99, -800.4) * mm, "radius": 3.18 * mm});
            skCircle(sketch, "E6.68.0.31", {"center": v(1799.74, -800.4) * mm, "radius": 3.18 * mm});
            skCircle(sketch, "E6.70.0.31", {"center": v(1291.74, -800.4) * mm, "radius": 3.18 * mm});
            skCircle(sketch, "E6.72.0.31", {"center": v(1132.99, -800.4) * mm, "radius": 3.18 * mm});
            skCircle(sketch, "E6.74.0.31", {"center": v(974.24, -800.4) * mm, "radius": 3.18 * mm});
            skCircle(sketch, "E6.76.0.31", {"center": v(1482.24, -800.4) * mm, "radius": 3.18 * mm});
            skCircle(sketch, "E6.78.0.31", {"center": v(1259.99, -800.4) * mm, "radius": 3.18 * mm});
            skCircle(sketch, "E6.80.0.31", {"center": v(1640.99, -800.4) * mm, "radius": 3.18 * mm});
            skCircle(sketch, "E6.82.0.31", {"center": v(1767.99, -800.4) * mm, "radius": 3.18 * mm});
            skCircle(sketch, "E6.84.0.31", {"center": v(1196.49, -800.4) * mm, "radius": 3.18 * mm});
            skCircle(sketch, "E6.86.0.31", {"center": v(1704.49, -800.4) * mm, "radius": 3.18 * mm});
            skCircle(sketch, "E6.88.0.31", {"center": v(720.24, -800.4) * mm, "radius": 3.18 * mm});
            skCircle(sketch, "E6.90.0.31", {"center": v(942.49, -800.4) * mm, "radius": 3.18 * mm});
            skCircle(sketch, "E6.92.0.31", {"center": v(878.99, -800.4) * mm, "radius": 3.18 * mm});
            skCircle(sketch, "E6.94.0.31", {"center": v(434.49, -800.4) * mm, "radius": 3.18 * mm});
            skCircle(sketch, "E6.96.0.31", {"center": v(656.74, -800.4) * mm, "radius": 3.18 * mm});
            skCircle(sketch, "E6.98.0.31", {"center": v(370.99, -800.4) * mm, "radius": 3.18 * mm});
            skCircle(sketch, "E6.100.0.31", {"center": v(593.24, -800.4) * mm, "radius": 3.18 * mm});
            skCircle(sketch, "E6.102.0.31", {"center": v(847.24, -800.4) * mm, "radius": 3.18 * mm});
            skCircle(sketch, "E6.104.0.31", {"center": v(339.24, -800.4) * mm, "radius": 3.18 * mm});
            skCircle(sketch, "E6.106.0.31", {"center": v(561.49, -800.4) * mm, "radius": 3.18 * mm});
            skCircle(sketch, "E6.108.0.31", {"center": v(815.49, -800.4) * mm, "radius": 3.18 * mm});
            skCircle(sketch, "E6.110.0.31", {"center": v(307.49, -800.4) * mm, "radius": 3.18 * mm});
            skCircle(sketch, "E6.112.0.31", {"center": v(529.74, -800.4) * mm, "radius": 3.18 * mm});
            skCircle(sketch, "E6.114.0.31", {"center": v(180.49, -800.4) * mm, "radius": 3.18 * mm});
            skCircle(sketch, "E6.116.0.31", {"center": v(148.74, -800.4) * mm, "radius": 3.18 * mm});
            skCircle(sketch, "E6.118.0.31", {"center": v(910.74, -800.4) * mm, "radius": 3.18 * mm});
            skCircle(sketch, "E6.120.0.31", {"center": v(275.74, -800.4) * mm, "radius": 3.18 * mm});
            skCircle(sketch, "E6.122.0.31", {"center": v(243.99, -800.4) * mm, "radius": 3.18 * mm});
            skCircle(sketch, "E6.124.0.31", {"center": v(212.24, -800.4) * mm, "radius": 3.18 * mm});
            skCircle(sketch, "E6.126.0.31", {"center": v(783.74, -800.4) * mm, "radius": 3.18 * mm});
            skCircle(sketch, "E6.128.0.31", {"center": v(497.99, -800.4) * mm, "radius": 3.18 * mm});
            skCircle(sketch, "E6.130.0.31", {"center": v(402.74, -800.4) * mm, "radius": 3.18 * mm});
            skCircle(sketch, "E6.132.0.31", {"center": v(624.99, -800.4) * mm, "radius": 3.18 * mm});
            skCircle(sketch, "E6.134.0.31", {"center": v(751.99, -800.4) * mm, "radius": 3.18 * mm});
            skCircle(sketch, "E6.136.0.31", {"center": v(466.24, -800.4) * mm, "radius": 3.18 * mm});
            skCircle(sketch, "E6.138.0.31", {"center": v(688.49, -800.4) * mm, "radius": 3.18 * mm});
            skCircle(sketch, "E6.140.0.31", {"center": v(116.99, -800.4) * mm, "radius": 3.18 * mm});
            skCircle(sketch, "E6.142.0.31", {"center": v(85.24, -800.4) * mm, "radius": 3.18 * mm});
            skCircle(sketch, "E6.144.0.31", {"center": v(53.49, -800.4) * mm, "radius": 3.18 * mm});
            skLineSegment(sketch, "E6.146.0.31", {"start": v(-41.76, -800.4) * mm, "end": v(-10.01, -800.4) * mm, "construction": true});
            skCircle(sketch, "E6.149.0.31", {"center": v(21.74, -800.4) * mm, "radius": 3.18 * mm});
            skCircle(sketch, "E6.151.0.31", {"center": v(-10.01, -800.4) * mm, "radius": 3.18 * mm});
            skCircle(sketch, "E6.153.0.31", {"center": v(-41.76, -800.4) * mm, "radius": 3.18 * mm});
            skCircle(sketch, "E6.0.0.32", {"center": v(2244.24, -825.8) * mm, "radius": 3.18 * mm});
            skCircle(sketch, "E6.2.0.32", {"center": v(2180.74, -825.8) * mm, "radius": 3.18 * mm});
            skCircle(sketch, "E6.4.0.32", {"center": v(2339.49, -825.8) * mm, "radius": 3.18 * mm});
            skCircle(sketch, "E6.6.0.32", {"center": v(2307.74, -825.8) * mm, "radius": 3.18 * mm});
            skCircle(sketch, "E6.8.0.32", {"center": v(2275.99, -825.8) * mm, "radius": 3.18 * mm});
            skCircle(sketch, "E6.10.0.32", {"center": v(2212.49, -825.8) * mm, "radius": 3.18 * mm});
            skCircle(sketch, "E6.12.0.32", {"center": v(1958.49, -825.8) * mm, "radius": 3.18 * mm});
            skCircle(sketch, "E6.14.0.32", {"center": v(1894.99, -825.8) * mm, "radius": 3.18 * mm});
            skCircle(sketch, "E6.16.0.32", {"center": v(2117.24, -825.8) * mm, "radius": 3.18 * mm});
            skCircle(sketch, "E6.18.0.32", {"center": v(2085.49, -825.8) * mm, "radius": 3.18 * mm});
            skCircle(sketch, "E6.20.0.32", {"center": v(2053.74, -825.8) * mm, "radius": 3.18 * mm});
            skCircle(sketch, "E6.22.0.32", {"center": v(1926.74, -825.8) * mm, "radius": 3.18 * mm});
            skCircle(sketch, "E6.24.0.32", {"center": v(2021.99, -825.8) * mm, "radius": 3.18 * mm});
            skCircle(sketch, "E6.26.0.32", {"center": v(2148.99, -825.8) * mm, "radius": 3.18 * mm});
            skCircle(sketch, "E6.28.0.32", {"center": v(1990.24, -825.8) * mm, "radius": 3.18 * mm});
            skCircle(sketch, "E6.30.0.32", {"center": v(1450.49, -825.8) * mm, "radius": 3.18 * mm});
            skCircle(sketch, "E6.32.0.32", {"center": v(1228.24, -825.8) * mm, "radius": 3.18 * mm});
            skCircle(sketch, "E6.34.0.32", {"center": v(1736.24, -825.8) * mm, "radius": 3.18 * mm});
            skCircle(sketch, "E6.36.0.32", {"center": v(1386.99, -825.8) * mm, "radius": 3.18 * mm});
            skCircle(sketch, "E6.38.0.32", {"center": v(1164.74, -825.8) * mm, "radius": 3.18 * mm});
            skCircle(sketch, "E6.40.0.32", {"center": v(1672.74, -825.8) * mm, "radius": 3.18 * mm});
            skCircle(sketch, "E6.42.0.32", {"center": v(1101.24, -825.8) * mm, "radius": 3.18 * mm});
            skCircle(sketch, "E6.44.0.32", {"center": v(1609.24, -825.8) * mm, "radius": 3.18 * mm});
            skCircle(sketch, "E6.46.0.32", {"center": v(1355.24, -825.8) * mm, "radius": 3.18 * mm});
            skCircle(sketch, "E6.48.0.32", {"center": v(1863.24, -825.8) * mm, "radius": 3.18 * mm});
            skCircle(sketch, "E6.50.0.32", {"center": v(1069.49, -825.8) * mm, "radius": 3.18 * mm});
            skCircle(sketch, "E6.52.0.32", {"center": v(1577.49, -825.8) * mm, "radius": 3.18 * mm});
            skCircle(sketch, "E6.54.0.32", {"center": v(1323.49, -825.8) * mm, "radius": 3.18 * mm});
            skCircle(sketch, "E6.56.0.32", {"center": v(1831.49, -825.8) * mm, "radius": 3.18 * mm});
            skCircle(sketch, "E6.58.0.32", {"center": v(1037.74, -825.8) * mm, "radius": 3.18 * mm});
            skCircle(sketch, "E6.60.0.32", {"center": v(1545.74, -825.8) * mm, "radius": 3.18 * mm});
            skCircle(sketch, "E6.62.0.32", {"center": v(1418.74, -825.8) * mm, "radius": 3.18 * mm});
            skCircle(sketch, "E6.64.0.32", {"center": v(1005.99, -825.8) * mm, "radius": 3.18 * mm});
            skCircle(sketch, "E6.66.0.32", {"center": v(1513.99, -825.8) * mm, "radius": 3.18 * mm});
            skCircle(sketch, "E6.68.0.32", {"center": v(1799.74, -825.8) * mm, "radius": 3.18 * mm});
            skCircle(sketch, "E6.70.0.32", {"center": v(1291.74, -825.8) * mm, "radius": 3.18 * mm});
            skCircle(sketch, "E6.72.0.32", {"center": v(1132.99, -825.8) * mm, "radius": 3.18 * mm});
            skCircle(sketch, "E6.74.0.32", {"center": v(974.24, -825.8) * mm, "radius": 3.18 * mm});
            skCircle(sketch, "E6.76.0.32", {"center": v(1482.24, -825.8) * mm, "radius": 3.18 * mm});
            skCircle(sketch, "E6.78.0.32", {"center": v(1259.99, -825.8) * mm, "radius": 3.18 * mm});
            skCircle(sketch, "E6.80.0.32", {"center": v(1640.99, -825.8) * mm, "radius": 3.18 * mm});
            skCircle(sketch, "E6.82.0.32", {"center": v(1767.99, -825.8) * mm, "radius": 3.18 * mm});
            skCircle(sketch, "E6.84.0.32", {"center": v(1196.49, -825.8) * mm, "radius": 3.18 * mm});
            skCircle(sketch, "E6.86.0.32", {"center": v(1704.49, -825.8) * mm, "radius": 3.18 * mm});
            skCircle(sketch, "E6.88.0.32", {"center": v(720.24, -825.8) * mm, "radius": 3.18 * mm});
            skCircle(sketch, "E6.90.0.32", {"center": v(942.49, -825.8) * mm, "radius": 3.18 * mm});
            skCircle(sketch, "E6.92.0.32", {"center": v(878.99, -825.8) * mm, "radius": 3.18 * mm});
            skCircle(sketch, "E6.94.0.32", {"center": v(434.49, -825.8) * mm, "radius": 3.18 * mm});
            skCircle(sketch, "E6.96.0.32", {"center": v(656.74, -825.8) * mm, "radius": 3.18 * mm});
            skCircle(sketch, "E6.98.0.32", {"center": v(370.99, -825.8) * mm, "radius": 3.18 * mm});
            skCircle(sketch, "E6.100.0.32", {"center": v(593.24, -825.8) * mm, "radius": 3.18 * mm});
            skCircle(sketch, "E6.102.0.32", {"center": v(847.24, -825.8) * mm, "radius": 3.18 * mm});
            skCircle(sketch, "E6.104.0.32", {"center": v(339.24, -825.8) * mm, "radius": 3.18 * mm});
            skCircle(sketch, "E6.106.0.32", {"center": v(561.49, -825.8) * mm, "radius": 3.18 * mm});
            skCircle(sketch, "E6.108.0.32", {"center": v(815.49, -825.8) * mm, "radius": 3.18 * mm});
            skCircle(sketch, "E6.110.0.32", {"center": v(307.49, -825.8) * mm, "radius": 3.18 * mm});
            skCircle(sketch, "E6.112.0.32", {"center": v(529.74, -825.8) * mm, "radius": 3.18 * mm});
            skCircle(sketch, "E6.114.0.32", {"center": v(180.49, -825.8) * mm, "radius": 3.18 * mm});
            skCircle(sketch, "E6.116.0.32", {"center": v(148.74, -825.8) * mm, "radius": 3.18 * mm});
            skCircle(sketch, "E6.118.0.32", {"center": v(910.74, -825.8) * mm, "radius": 3.18 * mm});
            skCircle(sketch, "E6.120.0.32", {"center": v(275.74, -825.8) * mm, "radius": 3.18 * mm});
            skCircle(sketch, "E6.122.0.32", {"center": v(243.99, -825.8) * mm, "radius": 3.18 * mm});
            skCircle(sketch, "E6.124.0.32", {"center": v(212.24, -825.8) * mm, "radius": 3.18 * mm});
            skCircle(sketch, "E6.126.0.32", {"center": v(783.74, -825.8) * mm, "radius": 3.18 * mm});
            skCircle(sketch, "E6.128.0.32", {"center": v(497.99, -825.8) * mm, "radius": 3.18 * mm});
            skCircle(sketch, "E6.130.0.32", {"center": v(402.74, -825.8) * mm, "radius": 3.18 * mm});
            skCircle(sketch, "E6.132.0.32", {"center": v(624.99, -825.8) * mm, "radius": 3.18 * mm});
            skCircle(sketch, "E6.134.0.32", {"center": v(751.99, -825.8) * mm, "radius": 3.18 * mm});
            skCircle(sketch, "E6.136.0.32", {"center": v(466.24, -825.8) * mm, "radius": 3.18 * mm});
            skCircle(sketch, "E6.138.0.32", {"center": v(688.49, -825.8) * mm, "radius": 3.18 * mm});
            skCircle(sketch, "E6.140.0.32", {"center": v(116.99, -825.8) * mm, "radius": 3.18 * mm});
            skCircle(sketch, "E6.142.0.32", {"center": v(85.24, -825.8) * mm, "radius": 3.18 * mm});
            skCircle(sketch, "E6.144.0.32", {"center": v(53.49, -825.8) * mm, "radius": 3.18 * mm});
            skLineSegment(sketch, "E6.146.0.32", {"start": v(-41.76, -825.8) * mm, "end": v(-10.01, -825.8) * mm, "construction": true});
            skCircle(sketch, "E6.149.0.32", {"center": v(21.74, -825.8) * mm, "radius": 3.18 * mm});
            skCircle(sketch, "E6.151.0.32", {"center": v(-10.01, -825.8) * mm, "radius": 3.18 * mm});
            skCircle(sketch, "E6.153.0.32", {"center": v(-41.76, -825.8) * mm, "radius": 3.18 * mm});
            skCircle(sketch, "E6.0.0.33", {"center": v(2244.24, -851.2) * mm, "radius": 3.18 * mm});
            skCircle(sketch, "E6.2.0.33", {"center": v(2180.74, -851.2) * mm, "radius": 3.18 * mm});
            skCircle(sketch, "E6.4.0.33", {"center": v(2339.49, -851.2) * mm, "radius": 3.18 * mm});
            skCircle(sketch, "E6.6.0.33", {"center": v(2307.74, -851.2) * mm, "radius": 3.18 * mm});
            skCircle(sketch, "E6.8.0.33", {"center": v(2275.99, -851.2) * mm, "radius": 3.18 * mm});
            skCircle(sketch, "E6.10.0.33", {"center": v(2212.49, -851.2) * mm, "radius": 3.18 * mm});
            skCircle(sketch, "E6.12.0.33", {"center": v(1958.49, -851.2) * mm, "radius": 3.18 * mm});
            skCircle(sketch, "E6.14.0.33", {"center": v(1894.99, -851.2) * mm, "radius": 3.18 * mm});
            skCircle(sketch, "E6.16.0.33", {"center": v(2117.24, -851.2) * mm, "radius": 3.18 * mm});
            skCircle(sketch, "E6.18.0.33", {"center": v(2085.49, -851.2) * mm, "radius": 3.18 * mm});
            skCircle(sketch, "E6.20.0.33", {"center": v(2053.74, -851.2) * mm, "radius": 3.18 * mm});
            skCircle(sketch, "E6.22.0.33", {"center": v(1926.74, -851.2) * mm, "radius": 3.18 * mm});
            skCircle(sketch, "E6.24.0.33", {"center": v(2021.99, -851.2) * mm, "radius": 3.18 * mm});
            skCircle(sketch, "E6.26.0.33", {"center": v(2148.99, -851.2) * mm, "radius": 3.18 * mm});
            skCircle(sketch, "E6.28.0.33", {"center": v(1990.24, -851.2) * mm, "radius": 3.18 * mm});
            skCircle(sketch, "E6.30.0.33", {"center": v(1450.49, -851.2) * mm, "radius": 3.18 * mm});
            skCircle(sketch, "E6.32.0.33", {"center": v(1228.24, -851.2) * mm, "radius": 3.18 * mm});
            skCircle(sketch, "E6.34.0.33", {"center": v(1736.24, -851.2) * mm, "radius": 3.18 * mm});
            skCircle(sketch, "E6.36.0.33", {"center": v(1386.99, -851.2) * mm, "radius": 3.18 * mm});
            skCircle(sketch, "E6.38.0.33", {"center": v(1164.74, -851.2) * mm, "radius": 3.18 * mm});
            skCircle(sketch, "E6.40.0.33", {"center": v(1672.74, -851.2) * mm, "radius": 3.18 * mm});
            skCircle(sketch, "E6.42.0.33", {"center": v(1101.24, -851.2) * mm, "radius": 3.18 * mm});
            skCircle(sketch, "E6.44.0.33", {"center": v(1609.24, -851.2) * mm, "radius": 3.18 * mm});
            skCircle(sketch, "E6.46.0.33", {"center": v(1355.24, -851.2) * mm, "radius": 3.18 * mm});
            skCircle(sketch, "E6.48.0.33", {"center": v(1863.24, -851.2) * mm, "radius": 3.18 * mm});
            skCircle(sketch, "E6.50.0.33", {"center": v(1069.49, -851.2) * mm, "radius": 3.18 * mm});
            skCircle(sketch, "E6.52.0.33", {"center": v(1577.49, -851.2) * mm, "radius": 3.18 * mm});
            skCircle(sketch, "E6.54.0.33", {"center": v(1323.49, -851.2) * mm, "radius": 3.18 * mm});
            skCircle(sketch, "E6.56.0.33", {"center": v(1831.49, -851.2) * mm, "radius": 3.18 * mm});
            skCircle(sketch, "E6.58.0.33", {"center": v(1037.74, -851.2) * mm, "radius": 3.18 * mm});
            skCircle(sketch, "E6.60.0.33", {"center": v(1545.74, -851.2) * mm, "radius": 3.18 * mm});
            skCircle(sketch, "E6.62.0.33", {"center": v(1418.74, -851.2) * mm, "radius": 3.18 * mm});
            skCircle(sketch, "E6.64.0.33", {"center": v(1005.99, -851.2) * mm, "radius": 3.18 * mm});
            skCircle(sketch, "E6.66.0.33", {"center": v(1513.99, -851.2) * mm, "radius": 3.18 * mm});
            skCircle(sketch, "E6.68.0.33", {"center": v(1799.74, -851.2) * mm, "radius": 3.18 * mm});
            skCircle(sketch, "E6.70.0.33", {"center": v(1291.74, -851.2) * mm, "radius": 3.18 * mm});
            skCircle(sketch, "E6.72.0.33", {"center": v(1132.99, -851.2) * mm, "radius": 3.18 * mm});
            skCircle(sketch, "E6.74.0.33", {"center": v(974.24, -851.2) * mm, "radius": 3.18 * mm});
            skCircle(sketch, "E6.76.0.33", {"center": v(1482.24, -851.2) * mm, "radius": 3.18 * mm});
            skCircle(sketch, "E6.78.0.33", {"center": v(1259.99, -851.2) * mm, "radius": 3.18 * mm});
            skCircle(sketch, "E6.80.0.33", {"center": v(1640.99, -851.2) * mm, "radius": 3.18 * mm});
            skCircle(sketch, "E6.82.0.33", {"center": v(1767.99, -851.2) * mm, "radius": 3.18 * mm});
            skCircle(sketch, "E6.84.0.33", {"center": v(1196.49, -851.2) * mm, "radius": 3.18 * mm});
            skCircle(sketch, "E6.86.0.33", {"center": v(1704.49, -851.2) * mm, "radius": 3.18 * mm});
            skCircle(sketch, "E6.88.0.33", {"center": v(720.24, -851.2) * mm, "radius": 3.18 * mm});
            skCircle(sketch, "E6.90.0.33", {"center": v(942.49, -851.2) * mm, "radius": 3.18 * mm});
            skCircle(sketch, "E6.92.0.33", {"center": v(878.99, -851.2) * mm, "radius": 3.18 * mm});
            skCircle(sketch, "E6.94.0.33", {"center": v(434.49, -851.2) * mm, "radius": 3.18 * mm});
            skCircle(sketch, "E6.96.0.33", {"center": v(656.74, -851.2) * mm, "radius": 3.18 * mm});
            skCircle(sketch, "E6.98.0.33", {"center": v(370.99, -851.2) * mm, "radius": 3.18 * mm});
            skCircle(sketch, "E6.100.0.33", {"center": v(593.24, -851.2) * mm, "radius": 3.18 * mm});
            skCircle(sketch, "E6.102.0.33", {"center": v(847.24, -851.2) * mm, "radius": 3.18 * mm});
            skCircle(sketch, "E6.104.0.33", {"center": v(339.24, -851.2) * mm, "radius": 3.18 * mm});
            skCircle(sketch, "E6.106.0.33", {"center": v(561.49, -851.2) * mm, "radius": 3.18 * mm});
            skCircle(sketch, "E6.108.0.33", {"center": v(815.49, -851.2) * mm, "radius": 3.18 * mm});
            skCircle(sketch, "E6.110.0.33", {"center": v(307.49, -851.2) * mm, "radius": 3.18 * mm});
            skCircle(sketch, "E6.112.0.33", {"center": v(529.74, -851.2) * mm, "radius": 3.18 * mm});
            skCircle(sketch, "E6.114.0.33", {"center": v(180.49, -851.2) * mm, "radius": 3.18 * mm});
            skCircle(sketch, "E6.116.0.33", {"center": v(148.74, -851.2) * mm, "radius": 3.18 * mm});
            skCircle(sketch, "E6.118.0.33", {"center": v(910.74, -851.2) * mm, "radius": 3.18 * mm});
            skCircle(sketch, "E6.120.0.33", {"center": v(275.74, -851.2) * mm, "radius": 3.18 * mm});
            skCircle(sketch, "E6.122.0.33", {"center": v(243.99, -851.2) * mm, "radius": 3.18 * mm});
            skCircle(sketch, "E6.124.0.33", {"center": v(212.24, -851.2) * mm, "radius": 3.18 * mm});
            skCircle(sketch, "E6.126.0.33", {"center": v(783.74, -851.2) * mm, "radius": 3.18 * mm});
            skCircle(sketch, "E6.128.0.33", {"center": v(497.99, -851.2) * mm, "radius": 3.18 * mm});
            skCircle(sketch, "E6.130.0.33", {"center": v(402.74, -851.2) * mm, "radius": 3.18 * mm});
            skCircle(sketch, "E6.132.0.33", {"center": v(624.99, -851.2) * mm, "radius": 3.18 * mm});
            skCircle(sketch, "E6.134.0.33", {"center": v(751.99, -851.2) * mm, "radius": 3.18 * mm});
            skCircle(sketch, "E6.136.0.33", {"center": v(466.24, -851.2) * mm, "radius": 3.18 * mm});
            skCircle(sketch, "E6.138.0.33", {"center": v(688.49, -851.2) * mm, "radius": 3.18 * mm});
            skCircle(sketch, "E6.140.0.33", {"center": v(116.99, -851.2) * mm, "radius": 3.18 * mm});
            skCircle(sketch, "E6.142.0.33", {"center": v(85.24, -851.2) * mm, "radius": 3.18 * mm});
            skCircle(sketch, "E6.144.0.33", {"center": v(53.49, -851.2) * mm, "radius": 3.18 * mm});
            skLineSegment(sketch, "E6.146.0.33", {"start": v(-41.76, -851.2) * mm, "end": v(-10.01, -851.2) * mm, "construction": true});
            skCircle(sketch, "E6.149.0.33", {"center": v(21.74, -851.2) * mm, "radius": 3.18 * mm});
            skCircle(sketch, "E6.151.0.33", {"center": v(-10.01, -851.2) * mm, "radius": 3.18 * mm});
            skCircle(sketch, "E6.153.0.33", {"center": v(-41.76, -851.2) * mm, "radius": 3.18 * mm});
            skCircle(sketch, "E6.0.0.34", {"center": v(2244.24, -876.6) * mm, "radius": 3.18 * mm});
            skCircle(sketch, "E6.2.0.34", {"center": v(2180.74, -876.6) * mm, "radius": 3.18 * mm});
            skCircle(sketch, "E6.4.0.34", {"center": v(2339.49, -876.6) * mm, "radius": 3.18 * mm});
            skCircle(sketch, "E6.6.0.34", {"center": v(2307.74, -876.6) * mm, "radius": 3.18 * mm});
            skCircle(sketch, "E6.8.0.34", {"center": v(2275.99, -876.6) * mm, "radius": 3.18 * mm});
            skCircle(sketch, "E6.10.0.34", {"center": v(2212.49, -876.6) * mm, "radius": 3.18 * mm});
            skCircle(sketch, "E6.12.0.34", {"center": v(1958.49, -876.6) * mm, "radius": 3.18 * mm});
            skCircle(sketch, "E6.14.0.34", {"center": v(1894.99, -876.6) * mm, "radius": 3.18 * mm});
            skCircle(sketch, "E6.16.0.34", {"center": v(2117.24, -876.6) * mm, "radius": 3.18 * mm});
            skCircle(sketch, "E6.18.0.34", {"center": v(2085.49, -876.6) * mm, "radius": 3.18 * mm});
            skCircle(sketch, "E6.20.0.34", {"center": v(2053.74, -876.6) * mm, "radius": 3.18 * mm});
            skCircle(sketch, "E6.22.0.34", {"center": v(1926.74, -876.6) * mm, "radius": 3.18 * mm});
            skCircle(sketch, "E6.24.0.34", {"center": v(2021.99, -876.6) * mm, "radius": 3.18 * mm});
            skCircle(sketch, "E6.26.0.34", {"center": v(2148.99, -876.6) * mm, "radius": 3.18 * mm});
            skCircle(sketch, "E6.28.0.34", {"center": v(1990.24, -876.6) * mm, "radius": 3.18 * mm});
            skCircle(sketch, "E6.30.0.34", {"center": v(1450.49, -876.6) * mm, "radius": 3.18 * mm});
            skCircle(sketch, "E6.32.0.34", {"center": v(1228.24, -876.6) * mm, "radius": 3.18 * mm});
            skCircle(sketch, "E6.34.0.34", {"center": v(1736.24, -876.6) * mm, "radius": 3.18 * mm});
            skCircle(sketch, "E6.36.0.34", {"center": v(1386.99, -876.6) * mm, "radius": 3.18 * mm});
            skCircle(sketch, "E6.38.0.34", {"center": v(1164.74, -876.6) * mm, "radius": 3.18 * mm});
            skCircle(sketch, "E6.40.0.34", {"center": v(1672.74, -876.6) * mm, "radius": 3.18 * mm});
            skCircle(sketch, "E6.42.0.34", {"center": v(1101.24, -876.6) * mm, "radius": 3.18 * mm});
            skCircle(sketch, "E6.44.0.34", {"center": v(1609.24, -876.6) * mm, "radius": 3.18 * mm});
            skCircle(sketch, "E6.46.0.34", {"center": v(1355.24, -876.6) * mm, "radius": 3.18 * mm});
            skCircle(sketch, "E6.48.0.34", {"center": v(1863.24, -876.6) * mm, "radius": 3.18 * mm});
            skCircle(sketch, "E6.50.0.34", {"center": v(1069.49, -876.6) * mm, "radius": 3.18 * mm});
            skCircle(sketch, "E6.52.0.34", {"center": v(1577.49, -876.6) * mm, "radius": 3.18 * mm});
            skCircle(sketch, "E6.54.0.34", {"center": v(1323.49, -876.6) * mm, "radius": 3.18 * mm});
            skCircle(sketch, "E6.56.0.34", {"center": v(1831.49, -876.6) * mm, "radius": 3.18 * mm});
            skCircle(sketch, "E6.58.0.34", {"center": v(1037.74, -876.6) * mm, "radius": 3.18 * mm});
            skCircle(sketch, "E6.60.0.34", {"center": v(1545.74, -876.6) * mm, "radius": 3.18 * mm});
            skCircle(sketch, "E6.62.0.34", {"center": v(1418.74, -876.6) * mm, "radius": 3.18 * mm});
            skCircle(sketch, "E6.64.0.34", {"center": v(1005.99, -876.6) * mm, "radius": 3.18 * mm});
            skCircle(sketch, "E6.66.0.34", {"center": v(1513.99, -876.6) * mm, "radius": 3.18 * mm});
            skCircle(sketch, "E6.68.0.34", {"center": v(1799.74, -876.6) * mm, "radius": 3.18 * mm});
            skCircle(sketch, "E6.70.0.34", {"center": v(1291.74, -876.6) * mm, "radius": 3.18 * mm});
            skCircle(sketch, "E6.72.0.34", {"center": v(1132.99, -876.6) * mm, "radius": 3.18 * mm});
            skCircle(sketch, "E6.74.0.34", {"center": v(974.24, -876.6) * mm, "radius": 3.18 * mm});
            skCircle(sketch, "E6.76.0.34", {"center": v(1482.24, -876.6) * mm, "radius": 3.18 * mm});
            skCircle(sketch, "E6.78.0.34", {"center": v(1259.99, -876.6) * mm, "radius": 3.18 * mm});
            skCircle(sketch, "E6.80.0.34", {"center": v(1640.99, -876.6) * mm, "radius": 3.18 * mm});
            skCircle(sketch, "E6.82.0.34", {"center": v(1767.99, -876.6) * mm, "radius": 3.18 * mm});
            skCircle(sketch, "E6.84.0.34", {"center": v(1196.49, -876.6) * mm, "radius": 3.18 * mm});
            skCircle(sketch, "E6.86.0.34", {"center": v(1704.49, -876.6) * mm, "radius": 3.18 * mm});
            skCircle(sketch, "E6.88.0.34", {"center": v(720.24, -876.6) * mm, "radius": 3.18 * mm});
            skCircle(sketch, "E6.90.0.34", {"center": v(942.49, -876.6) * mm, "radius": 3.18 * mm});
            skCircle(sketch, "E6.92.0.34", {"center": v(878.99, -876.6) * mm, "radius": 3.18 * mm});
            skCircle(sketch, "E6.94.0.34", {"center": v(434.49, -876.6) * mm, "radius": 3.18 * mm});
            skCircle(sketch, "E6.96.0.34", {"center": v(656.74, -876.6) * mm, "radius": 3.18 * mm});
            skCircle(sketch, "E6.98.0.34", {"center": v(370.99, -876.6) * mm, "radius": 3.18 * mm});
            skCircle(sketch, "E6.100.0.34", {"center": v(593.24, -876.6) * mm, "radius": 3.18 * mm});
            skCircle(sketch, "E6.102.0.34", {"center": v(847.24, -876.6) * mm, "radius": 3.18 * mm});
            skCircle(sketch, "E6.104.0.34", {"center": v(339.24, -876.6) * mm, "radius": 3.18 * mm});
            skCircle(sketch, "E6.106.0.34", {"center": v(561.49, -876.6) * mm, "radius": 3.18 * mm});
            skCircle(sketch, "E6.108.0.34", {"center": v(815.49, -876.6) * mm, "radius": 3.18 * mm});
            skCircle(sketch, "E6.110.0.34", {"center": v(307.49, -876.6) * mm, "radius": 3.18 * mm});
            skCircle(sketch, "E6.112.0.34", {"center": v(529.74, -876.6) * mm, "radius": 3.18 * mm});
            skCircle(sketch, "E6.114.0.34", {"center": v(180.49, -876.6) * mm, "radius": 3.18 * mm});
            skCircle(sketch, "E6.116.0.34", {"center": v(148.74, -876.6) * mm, "radius": 3.18 * mm});
            skCircle(sketch, "E6.118.0.34", {"center": v(910.74, -876.6) * mm, "radius": 3.18 * mm});
            skCircle(sketch, "E6.120.0.34", {"center": v(275.74, -876.6) * mm, "radius": 3.18 * mm});
            skCircle(sketch, "E6.122.0.34", {"center": v(243.99, -876.6) * mm, "radius": 3.18 * mm});
            skCircle(sketch, "E6.124.0.34", {"center": v(212.24, -876.6) * mm, "radius": 3.18 * mm});
            skCircle(sketch, "E6.126.0.34", {"center": v(783.74, -876.6) * mm, "radius": 3.18 * mm});
            skCircle(sketch, "E6.128.0.34", {"center": v(497.99, -876.6) * mm, "radius": 3.18 * mm});
            skCircle(sketch, "E6.130.0.34", {"center": v(402.74, -876.6) * mm, "radius": 3.18 * mm});
            skCircle(sketch, "E6.132.0.34", {"center": v(624.99, -876.6) * mm, "radius": 3.18 * mm});
            skCircle(sketch, "E6.134.0.34", {"center": v(751.99, -876.6) * mm, "radius": 3.18 * mm});
            skCircle(sketch, "E6.136.0.34", {"center": v(466.24, -876.6) * mm, "radius": 3.18 * mm});
            skCircle(sketch, "E6.138.0.34", {"center": v(688.49, -876.6) * mm, "radius": 3.18 * mm});
            skCircle(sketch, "E6.140.0.34", {"center": v(116.99, -876.6) * mm, "radius": 3.18 * mm});
            skCircle(sketch, "E6.142.0.34", {"center": v(85.24, -876.6) * mm, "radius": 3.18 * mm});
            skCircle(sketch, "E6.144.0.34", {"center": v(53.49, -876.6) * mm, "radius": 3.18 * mm});
            skLineSegment(sketch, "E6.146.0.34", {"start": v(-41.76, -876.6) * mm, "end": v(-10.01, -876.6) * mm, "construction": true});
            skCircle(sketch, "E6.149.0.34", {"center": v(21.74, -876.6) * mm, "radius": 3.18 * mm});
            skCircle(sketch, "E6.151.0.34", {"center": v(-10.01, -876.6) * mm, "radius": 3.18 * mm});
            skCircle(sketch, "E6.153.0.34", {"center": v(-41.76, -876.6) * mm, "radius": 3.18 * mm});
            skCircle(sketch, "E6.0.0.35", {"center": v(2244.24, -902) * mm, "radius": 3.18 * mm});
            skCircle(sketch, "E6.2.0.35", {"center": v(2180.74, -902) * mm, "radius": 3.18 * mm});
            skCircle(sketch, "E6.4.0.35", {"center": v(2339.49, -902) * mm, "radius": 3.18 * mm});
            skCircle(sketch, "E6.6.0.35", {"center": v(2307.74, -902) * mm, "radius": 3.18 * mm});
            skCircle(sketch, "E6.8.0.35", {"center": v(2275.99, -902) * mm, "radius": 3.18 * mm});
            skCircle(sketch, "E6.10.0.35", {"center": v(2212.49, -902) * mm, "radius": 3.18 * mm});
            skCircle(sketch, "E6.12.0.35", {"center": v(1958.49, -902) * mm, "radius": 3.18 * mm});
            skCircle(sketch, "E6.14.0.35", {"center": v(1894.99, -902) * mm, "radius": 3.18 * mm});
            skCircle(sketch, "E6.16.0.35", {"center": v(2117.24, -902) * mm, "radius": 3.18 * mm});
            skCircle(sketch, "E6.18.0.35", {"center": v(2085.49, -902) * mm, "radius": 3.18 * mm});
            skCircle(sketch, "E6.20.0.35", {"center": v(2053.74, -902) * mm, "radius": 3.18 * mm});
            skCircle(sketch, "E6.22.0.35", {"center": v(1926.74, -902) * mm, "radius": 3.18 * mm});
            skCircle(sketch, "E6.24.0.35", {"center": v(2021.99, -902) * mm, "radius": 3.18 * mm});
            skCircle(sketch, "E6.26.0.35", {"center": v(2148.99, -902) * mm, "radius": 3.18 * mm});
            skCircle(sketch, "E6.28.0.35", {"center": v(1990.24, -902) * mm, "radius": 3.18 * mm});
            skCircle(sketch, "E6.30.0.35", {"center": v(1450.49, -902) * mm, "radius": 3.18 * mm});
            skCircle(sketch, "E6.32.0.35", {"center": v(1228.24, -902) * mm, "radius": 3.18 * mm});
            skCircle(sketch, "E6.34.0.35", {"center": v(1736.24, -902) * mm, "radius": 3.18 * mm});
            skCircle(sketch, "E6.36.0.35", {"center": v(1386.99, -902) * mm, "radius": 3.18 * mm});
            skCircle(sketch, "E6.38.0.35", {"center": v(1164.74, -902) * mm, "radius": 3.18 * mm});
            skCircle(sketch, "E6.40.0.35", {"center": v(1672.74, -902) * mm, "radius": 3.18 * mm});
            skCircle(sketch, "E6.42.0.35", {"center": v(1101.24, -902) * mm, "radius": 3.18 * mm});
            skCircle(sketch, "E6.44.0.35", {"center": v(1609.24, -902) * mm, "radius": 3.18 * mm});
            skCircle(sketch, "E6.46.0.35", {"center": v(1355.24, -902) * mm, "radius": 3.18 * mm});
            skCircle(sketch, "E6.48.0.35", {"center": v(1863.24, -902) * mm, "radius": 3.18 * mm});
            skCircle(sketch, "E6.50.0.35", {"center": v(1069.49, -902) * mm, "radius": 3.18 * mm});
            skCircle(sketch, "E6.52.0.35", {"center": v(1577.49, -902) * mm, "radius": 3.18 * mm});
            skCircle(sketch, "E6.54.0.35", {"center": v(1323.49, -902) * mm, "radius": 3.18 * mm});
            skCircle(sketch, "E6.56.0.35", {"center": v(1831.49, -902) * mm, "radius": 3.18 * mm});
            skCircle(sketch, "E6.58.0.35", {"center": v(1037.74, -902) * mm, "radius": 3.18 * mm});
            skCircle(sketch, "E6.60.0.35", {"center": v(1545.74, -902) * mm, "radius": 3.18 * mm});
            skCircle(sketch, "E6.62.0.35", {"center": v(1418.74, -902) * mm, "radius": 3.18 * mm});
            skCircle(sketch, "E6.64.0.35", {"center": v(1005.99, -902) * mm, "radius": 3.18 * mm});
            skCircle(sketch, "E6.66.0.35", {"center": v(1513.99, -902) * mm, "radius": 3.18 * mm});
            skCircle(sketch, "E6.68.0.35", {"center": v(1799.74, -902) * mm, "radius": 3.18 * mm});
            skCircle(sketch, "E6.70.0.35", {"center": v(1291.74, -902) * mm, "radius": 3.18 * mm});
            skCircle(sketch, "E6.72.0.35", {"center": v(1132.99, -902) * mm, "radius": 3.18 * mm});
            skCircle(sketch, "E6.74.0.35", {"center": v(974.24, -902) * mm, "radius": 3.18 * mm});
            skCircle(sketch, "E6.76.0.35", {"center": v(1482.24, -902) * mm, "radius": 3.18 * mm});
            skCircle(sketch, "E6.78.0.35", {"center": v(1259.99, -902) * mm, "radius": 3.18 * mm});
            skCircle(sketch, "E6.80.0.35", {"center": v(1640.99, -902) * mm, "radius": 3.18 * mm});
            skCircle(sketch, "E6.82.0.35", {"center": v(1767.99, -902) * mm, "radius": 3.18 * mm});
            skCircle(sketch, "E6.84.0.35", {"center": v(1196.49, -902) * mm, "radius": 3.18 * mm});
            skCircle(sketch, "E6.86.0.35", {"center": v(1704.49, -902) * mm, "radius": 3.18 * mm});
            skCircle(sketch, "E6.88.0.35", {"center": v(720.24, -902) * mm, "radius": 3.18 * mm});
            skCircle(sketch, "E6.90.0.35", {"center": v(942.49, -902) * mm, "radius": 3.18 * mm});
            skCircle(sketch, "E6.92.0.35", {"center": v(878.99, -902) * mm, "radius": 3.18 * mm});
            skCircle(sketch, "E6.94.0.35", {"center": v(434.49, -902) * mm, "radius": 3.18 * mm});
            skCircle(sketch, "E6.96.0.35", {"center": v(656.74, -902) * mm, "radius": 3.18 * mm});
            skCircle(sketch, "E6.98.0.35", {"center": v(370.99, -902) * mm, "radius": 3.18 * mm});
            skCircle(sketch, "E6.100.0.35", {"center": v(593.24, -902) * mm, "radius": 3.18 * mm});
            skCircle(sketch, "E6.102.0.35", {"center": v(847.24, -902) * mm, "radius": 3.18 * mm});
            skCircle(sketch, "E6.104.0.35", {"center": v(339.24, -902) * mm, "radius": 3.18 * mm});
            skCircle(sketch, "E6.106.0.35", {"center": v(561.49, -902) * mm, "radius": 3.18 * mm});
            skCircle(sketch, "E6.108.0.35", {"center": v(815.49, -902) * mm, "radius": 3.18 * mm});
            skCircle(sketch, "E6.110.0.35", {"center": v(307.49, -902) * mm, "radius": 3.18 * mm});
            skCircle(sketch, "E6.112.0.35", {"center": v(529.74, -902) * mm, "radius": 3.18 * mm});
            skCircle(sketch, "E6.114.0.35", {"center": v(180.49, -902) * mm, "radius": 3.18 * mm});
            skCircle(sketch, "E6.116.0.35", {"center": v(148.74, -902) * mm, "radius": 3.18 * mm});
            skCircle(sketch, "E6.118.0.35", {"center": v(910.74, -902) * mm, "radius": 3.18 * mm});
            skCircle(sketch, "E6.120.0.35", {"center": v(275.74, -902) * mm, "radius": 3.18 * mm});
            skCircle(sketch, "E6.122.0.35", {"center": v(243.99, -902) * mm, "radius": 3.18 * mm});
            skCircle(sketch, "E6.124.0.35", {"center": v(212.24, -902) * mm, "radius": 3.18 * mm});
            skCircle(sketch, "E6.126.0.35", {"center": v(783.74, -902) * mm, "radius": 3.18 * mm});
            skCircle(sketch, "E6.128.0.35", {"center": v(497.99, -902) * mm, "radius": 3.18 * mm});
            skCircle(sketch, "E6.130.0.35", {"center": v(402.74, -902) * mm, "radius": 3.18 * mm});
            skCircle(sketch, "E6.132.0.35", {"center": v(624.99, -902) * mm, "radius": 3.18 * mm});
            skCircle(sketch, "E6.134.0.35", {"center": v(751.99, -902) * mm, "radius": 3.18 * mm});
            skCircle(sketch, "E6.136.0.35", {"center": v(466.24, -902) * mm, "radius": 3.18 * mm});
            skCircle(sketch, "E6.138.0.35", {"center": v(688.49, -902) * mm, "radius": 3.18 * mm});
            skCircle(sketch, "E6.140.0.35", {"center": v(116.99, -902) * mm, "radius": 3.18 * mm});
            skCircle(sketch, "E6.142.0.35", {"center": v(85.24, -902) * mm, "radius": 3.18 * mm});
            skCircle(sketch, "E6.144.0.35", {"center": v(53.49, -902) * mm, "radius": 3.18 * mm});
            skLineSegment(sketch, "E6.146.0.35", {"start": v(-41.76, -902) * mm, "end": v(-10.01, -902) * mm, "construction": true});
            skCircle(sketch, "E6.149.0.35", {"center": v(21.74, -902) * mm, "radius": 3.18 * mm});
            skCircle(sketch, "E6.151.0.35", {"center": v(-10.01, -902) * mm, "radius": 3.18 * mm});
            skCircle(sketch, "E6.153.0.35", {"center": v(-41.76, -902) * mm, "radius": 3.18 * mm});
            skCircle(sketch, "E6.0.0.36", {"center": v(2244.24, -927.4) * mm, "radius": 3.18 * mm});
            skCircle(sketch, "E6.2.0.36", {"center": v(2180.74, -927.4) * mm, "radius": 3.18 * mm});
            skCircle(sketch, "E6.4.0.36", {"center": v(2339.49, -927.4) * mm, "radius": 3.18 * mm});
            skCircle(sketch, "E6.6.0.36", {"center": v(2307.74, -927.4) * mm, "radius": 3.18 * mm});
            skCircle(sketch, "E6.8.0.36", {"center": v(2275.99, -927.4) * mm, "radius": 3.18 * mm});
            skCircle(sketch, "E6.10.0.36", {"center": v(2212.49, -927.4) * mm, "radius": 3.18 * mm});
            skCircle(sketch, "E6.12.0.36", {"center": v(1958.49, -927.4) * mm, "radius": 3.18 * mm});
            skCircle(sketch, "E6.14.0.36", {"center": v(1894.99, -927.4) * mm, "radius": 3.18 * mm});
            skCircle(sketch, "E6.16.0.36", {"center": v(2117.24, -927.4) * mm, "radius": 3.18 * mm});
            skCircle(sketch, "E6.18.0.36", {"center": v(2085.49, -927.4) * mm, "radius": 3.18 * mm});
            skCircle(sketch, "E6.20.0.36", {"center": v(2053.74, -927.4) * mm, "radius": 3.18 * mm});
            skCircle(sketch, "E6.22.0.36", {"center": v(1926.74, -927.4) * mm, "radius": 3.18 * mm});
            skCircle(sketch, "E6.24.0.36", {"center": v(2021.99, -927.4) * mm, "radius": 3.18 * mm});
            skCircle(sketch, "E6.26.0.36", {"center": v(2148.99, -927.4) * mm, "radius": 3.18 * mm});
            skCircle(sketch, "E6.28.0.36", {"center": v(1990.24, -927.4) * mm, "radius": 3.18 * mm});
            skCircle(sketch, "E6.30.0.36", {"center": v(1450.49, -927.4) * mm, "radius": 3.18 * mm});
            skCircle(sketch, "E6.32.0.36", {"center": v(1228.24, -927.4) * mm, "radius": 3.18 * mm});
            skCircle(sketch, "E6.34.0.36", {"center": v(1736.24, -927.4) * mm, "radius": 3.18 * mm});
            skCircle(sketch, "E6.36.0.36", {"center": v(1386.99, -927.4) * mm, "radius": 3.18 * mm});
            skCircle(sketch, "E6.38.0.36", {"center": v(1164.74, -927.4) * mm, "radius": 3.18 * mm});
            skCircle(sketch, "E6.40.0.36", {"center": v(1672.74, -927.4) * mm, "radius": 3.18 * mm});
            skCircle(sketch, "E6.42.0.36", {"center": v(1101.24, -927.4) * mm, "radius": 3.18 * mm});
            skCircle(sketch, "E6.44.0.36", {"center": v(1609.24, -927.4) * mm, "radius": 3.18 * mm});
            skCircle(sketch, "E6.46.0.36", {"center": v(1355.24, -927.4) * mm, "radius": 3.18 * mm});
            skCircle(sketch, "E6.48.0.36", {"center": v(1863.24, -927.4) * mm, "radius": 3.18 * mm});
            skCircle(sketch, "E6.50.0.36", {"center": v(1069.49, -927.4) * mm, "radius": 3.18 * mm});
            skCircle(sketch, "E6.52.0.36", {"center": v(1577.49, -927.4) * mm, "radius": 3.18 * mm});
            skCircle(sketch, "E6.54.0.36", {"center": v(1323.49, -927.4) * mm, "radius": 3.18 * mm});
            skCircle(sketch, "E6.56.0.36", {"center": v(1831.49, -927.4) * mm, "radius": 3.18 * mm});
            skCircle(sketch, "E6.58.0.36", {"center": v(1037.74, -927.4) * mm, "radius": 3.18 * mm});
            skCircle(sketch, "E6.60.0.36", {"center": v(1545.74, -927.4) * mm, "radius": 3.18 * mm});
            skCircle(sketch, "E6.62.0.36", {"center": v(1418.74, -927.4) * mm, "radius": 3.18 * mm});
            skCircle(sketch, "E6.64.0.36", {"center": v(1005.99, -927.4) * mm, "radius": 3.18 * mm});
            skCircle(sketch, "E6.66.0.36", {"center": v(1513.99, -927.4) * mm, "radius": 3.18 * mm});
            skCircle(sketch, "E6.68.0.36", {"center": v(1799.74, -927.4) * mm, "radius": 3.18 * mm});
            skCircle(sketch, "E6.70.0.36", {"center": v(1291.74, -927.4) * mm, "radius": 3.18 * mm});
            skCircle(sketch, "E6.72.0.36", {"center": v(1132.99, -927.4) * mm, "radius": 3.18 * mm});
            skCircle(sketch, "E6.74.0.36", {"center": v(974.24, -927.4) * mm, "radius": 3.18 * mm});
            skCircle(sketch, "E6.76.0.36", {"center": v(1482.24, -927.4) * mm, "radius": 3.18 * mm});
            skCircle(sketch, "E6.78.0.36", {"center": v(1259.99, -927.4) * mm, "radius": 3.18 * mm});
            skCircle(sketch, "E6.80.0.36", {"center": v(1640.99, -927.4) * mm, "radius": 3.18 * mm});
            skCircle(sketch, "E6.82.0.36", {"center": v(1767.99, -927.4) * mm, "radius": 3.18 * mm});
            skCircle(sketch, "E6.84.0.36", {"center": v(1196.49, -927.4) * mm, "radius": 3.18 * mm});
            skCircle(sketch, "E6.86.0.36", {"center": v(1704.49, -927.4) * mm, "radius": 3.18 * mm});
            skCircle(sketch, "E6.88.0.36", {"center": v(720.24, -927.4) * mm, "radius": 3.18 * mm});
            skCircle(sketch, "E6.90.0.36", {"center": v(942.49, -927.4) * mm, "radius": 3.18 * mm});
            skCircle(sketch, "E6.92.0.36", {"center": v(878.99, -927.4) * mm, "radius": 3.18 * mm});
            skCircle(sketch, "E6.94.0.36", {"center": v(434.49, -927.4) * mm, "radius": 3.18 * mm});
            skCircle(sketch, "E6.96.0.36", {"center": v(656.74, -927.4) * mm, "radius": 3.18 * mm});
            skCircle(sketch, "E6.98.0.36", {"center": v(370.99, -927.4) * mm, "radius": 3.18 * mm});
            skCircle(sketch, "E6.100.0.36", {"center": v(593.24, -927.4) * mm, "radius": 3.18 * mm});
            skCircle(sketch, "E6.102.0.36", {"center": v(847.24, -927.4) * mm, "radius": 3.18 * mm});
            skCircle(sketch, "E6.104.0.36", {"center": v(339.24, -927.4) * mm, "radius": 3.18 * mm});
            skCircle(sketch, "E6.106.0.36", {"center": v(561.49, -927.4) * mm, "radius": 3.18 * mm});
            skCircle(sketch, "E6.108.0.36", {"center": v(815.49, -927.4) * mm, "radius": 3.18 * mm});
            skCircle(sketch, "E6.110.0.36", {"center": v(307.49, -927.4) * mm, "radius": 3.18 * mm});
            skCircle(sketch, "E6.112.0.36", {"center": v(529.74, -927.4) * mm, "radius": 3.18 * mm});
            skCircle(sketch, "E6.114.0.36", {"center": v(180.49, -927.4) * mm, "radius": 3.18 * mm});
            skCircle(sketch, "E6.116.0.36", {"center": v(148.74, -927.4) * mm, "radius": 3.18 * mm});
            skCircle(sketch, "E6.118.0.36", {"center": v(910.74, -927.4) * mm, "radius": 3.18 * mm});
            skCircle(sketch, "E6.120.0.36", {"center": v(275.74, -927.4) * mm, "radius": 3.18 * mm});
            skCircle(sketch, "E6.122.0.36", {"center": v(243.99, -927.4) * mm, "radius": 3.18 * mm});
            skCircle(sketch, "E6.124.0.36", {"center": v(212.24, -927.4) * mm, "radius": 3.18 * mm});
            skCircle(sketch, "E6.126.0.36", {"center": v(783.74, -927.4) * mm, "radius": 3.18 * mm});
            skCircle(sketch, "E6.128.0.36", {"center": v(497.99, -927.4) * mm, "radius": 3.18 * mm});
            skCircle(sketch, "E6.130.0.36", {"center": v(402.74, -927.4) * mm, "radius": 3.18 * mm});
            skCircle(sketch, "E6.132.0.36", {"center": v(624.99, -927.4) * mm, "radius": 3.18 * mm});
            skCircle(sketch, "E6.134.0.36", {"center": v(751.99, -927.4) * mm, "radius": 3.18 * mm});
            skCircle(sketch, "E6.136.0.36", {"center": v(466.24, -927.4) * mm, "radius": 3.18 * mm});
            skCircle(sketch, "E6.138.0.36", {"center": v(688.49, -927.4) * mm, "radius": 3.18 * mm});
            skCircle(sketch, "E6.140.0.36", {"center": v(116.99, -927.4) * mm, "radius": 3.18 * mm});
            skCircle(sketch, "E6.142.0.36", {"center": v(85.24, -927.4) * mm, "radius": 3.18 * mm});
            skCircle(sketch, "E6.144.0.36", {"center": v(53.49, -927.4) * mm, "radius": 3.18 * mm});
            skLineSegment(sketch, "E6.146.0.36", {"start": v(-41.76, -927.4) * mm, "end": v(-10.01, -927.4) * mm, "construction": true});
            skCircle(sketch, "E6.149.0.36", {"center": v(21.74, -927.4) * mm, "radius": 3.18 * mm});
            skCircle(sketch, "E6.151.0.36", {"center": v(-10.01, -927.4) * mm, "radius": 3.18 * mm});
            skCircle(sketch, "E6.153.0.36", {"center": v(-41.76, -927.4) * mm, "radius": 3.18 * mm});
            skCircle(sketch, "E6.0.0.37", {"center": v(2244.24, -952.8) * mm, "radius": 3.18 * mm});
            skCircle(sketch, "E6.2.0.37", {"center": v(2180.74, -952.8) * mm, "radius": 3.18 * mm});
            skCircle(sketch, "E6.4.0.37", {"center": v(2339.49, -952.8) * mm, "radius": 3.18 * mm});
            skCircle(sketch, "E6.6.0.37", {"center": v(2307.74, -952.8) * mm, "radius": 3.18 * mm});
            skCircle(sketch, "E6.8.0.37", {"center": v(2275.99, -952.8) * mm, "radius": 3.18 * mm});
            skCircle(sketch, "E6.10.0.37", {"center": v(2212.49, -952.8) * mm, "radius": 3.18 * mm});
            skCircle(sketch, "E6.12.0.37", {"center": v(1958.49, -952.8) * mm, "radius": 3.18 * mm});
            skCircle(sketch, "E6.14.0.37", {"center": v(1894.99, -952.8) * mm, "radius": 3.18 * mm});
            skCircle(sketch, "E6.16.0.37", {"center": v(2117.24, -952.8) * mm, "radius": 3.18 * mm});
            skCircle(sketch, "E6.18.0.37", {"center": v(2085.49, -952.8) * mm, "radius": 3.18 * mm});
            skCircle(sketch, "E6.20.0.37", {"center": v(2053.74, -952.8) * mm, "radius": 3.18 * mm});
            skCircle(sketch, "E6.22.0.37", {"center": v(1926.74, -952.8) * mm, "radius": 3.18 * mm});
            skCircle(sketch, "E6.24.0.37", {"center": v(2021.99, -952.8) * mm, "radius": 3.18 * mm});
            skCircle(sketch, "E6.26.0.37", {"center": v(2148.99, -952.8) * mm, "radius": 3.18 * mm});
            skCircle(sketch, "E6.28.0.37", {"center": v(1990.24, -952.8) * mm, "radius": 3.18 * mm});
            skCircle(sketch, "E6.30.0.37", {"center": v(1450.49, -952.8) * mm, "radius": 3.18 * mm});
            skCircle(sketch, "E6.32.0.37", {"center": v(1228.24, -952.8) * mm, "radius": 3.18 * mm});
            skCircle(sketch, "E6.34.0.37", {"center": v(1736.24, -952.8) * mm, "radius": 3.18 * mm});
            skCircle(sketch, "E6.36.0.37", {"center": v(1386.99, -952.8) * mm, "radius": 3.18 * mm});
            skCircle(sketch, "E6.38.0.37", {"center": v(1164.74, -952.8) * mm, "radius": 3.18 * mm});
            skCircle(sketch, "E6.40.0.37", {"center": v(1672.74, -952.8) * mm, "radius": 3.18 * mm});
            skCircle(sketch, "E6.42.0.37", {"center": v(1101.24, -952.8) * mm, "radius": 3.18 * mm});
            skCircle(sketch, "E6.44.0.37", {"center": v(1609.24, -952.8) * mm, "radius": 3.18 * mm});
            skCircle(sketch, "E6.46.0.37", {"center": v(1355.24, -952.8) * mm, "radius": 3.18 * mm});
            skCircle(sketch, "E6.48.0.37", {"center": v(1863.24, -952.8) * mm, "radius": 3.18 * mm});
            skCircle(sketch, "E6.50.0.37", {"center": v(1069.49, -952.8) * mm, "radius": 3.18 * mm});
            skCircle(sketch, "E6.52.0.37", {"center": v(1577.49, -952.8) * mm, "radius": 3.18 * mm});
            skCircle(sketch, "E6.54.0.37", {"center": v(1323.49, -952.8) * mm, "radius": 3.18 * mm});
            skCircle(sketch, "E6.56.0.37", {"center": v(1831.49, -952.8) * mm, "radius": 3.18 * mm});
            skCircle(sketch, "E6.58.0.37", {"center": v(1037.74, -952.8) * mm, "radius": 3.18 * mm});
            skCircle(sketch, "E6.60.0.37", {"center": v(1545.74, -952.8) * mm, "radius": 3.18 * mm});
            skCircle(sketch, "E6.62.0.37", {"center": v(1418.74, -952.8) * mm, "radius": 3.18 * mm});
            skCircle(sketch, "E6.64.0.37", {"center": v(1005.99, -952.8) * mm, "radius": 3.18 * mm});
            skCircle(sketch, "E6.66.0.37", {"center": v(1513.99, -952.8) * mm, "radius": 3.18 * mm});
            skCircle(sketch, "E6.68.0.37", {"center": v(1799.74, -952.8) * mm, "radius": 3.18 * mm});
            skCircle(sketch, "E6.70.0.37", {"center": v(1291.74, -952.8) * mm, "radius": 3.18 * mm});
            skCircle(sketch, "E6.72.0.37", {"center": v(1132.99, -952.8) * mm, "radius": 3.18 * mm});
            skCircle(sketch, "E6.74.0.37", {"center": v(974.24, -952.8) * mm, "radius": 3.18 * mm});
            skCircle(sketch, "E6.76.0.37", {"center": v(1482.24, -952.8) * mm, "radius": 3.18 * mm});
            skCircle(sketch, "E6.78.0.37", {"center": v(1259.99, -952.8) * mm, "radius": 3.18 * mm});
            skCircle(sketch, "E6.80.0.37", {"center": v(1640.99, -952.8) * mm, "radius": 3.18 * mm});
            skCircle(sketch, "E6.82.0.37", {"center": v(1767.99, -952.8) * mm, "radius": 3.18 * mm});
            skCircle(sketch, "E6.84.0.37", {"center": v(1196.49, -952.8) * mm, "radius": 3.18 * mm});
            skCircle(sketch, "E6.86.0.37", {"center": v(1704.49, -952.8) * mm, "radius": 3.18 * mm});
            skCircle(sketch, "E6.88.0.37", {"center": v(720.24, -952.8) * mm, "radius": 3.18 * mm});
            skCircle(sketch, "E6.90.0.37", {"center": v(942.49, -952.8) * mm, "radius": 3.18 * mm});
            skCircle(sketch, "E6.92.0.37", {"center": v(878.99, -952.8) * mm, "radius": 3.18 * mm});
            skCircle(sketch, "E6.94.0.37", {"center": v(434.49, -952.8) * mm, "radius": 3.18 * mm});
            skCircle(sketch, "E6.96.0.37", {"center": v(656.74, -952.8) * mm, "radius": 3.18 * mm});
            skCircle(sketch, "E6.98.0.37", {"center": v(370.99, -952.8) * mm, "radius": 3.18 * mm});
            skCircle(sketch, "E6.100.0.37", {"center": v(593.24, -952.8) * mm, "radius": 3.18 * mm});
            skCircle(sketch, "E6.102.0.37", {"center": v(847.24, -952.8) * mm, "radius": 3.18 * mm});
            skCircle(sketch, "E6.104.0.37", {"center": v(339.24, -952.8) * mm, "radius": 3.18 * mm});
            skCircle(sketch, "E6.106.0.37", {"center": v(561.49, -952.8) * mm, "radius": 3.18 * mm});
            skCircle(sketch, "E6.108.0.37", {"center": v(815.49, -952.8) * mm, "radius": 3.18 * mm});
            skCircle(sketch, "E6.110.0.37", {"center": v(307.49, -952.8) * mm, "radius": 3.18 * mm});
            skCircle(sketch, "E6.112.0.37", {"center": v(529.74, -952.8) * mm, "radius": 3.18 * mm});
            skCircle(sketch, "E6.114.0.37", {"center": v(180.49, -952.8) * mm, "radius": 3.18 * mm});
            skCircle(sketch, "E6.116.0.37", {"center": v(148.74, -952.8) * mm, "radius": 3.18 * mm});
            skCircle(sketch, "E6.118.0.37", {"center": v(910.74, -952.8) * mm, "radius": 3.18 * mm});
            skCircle(sketch, "E6.120.0.37", {"center": v(275.74, -952.8) * mm, "radius": 3.18 * mm});
            skCircle(sketch, "E6.122.0.37", {"center": v(243.99, -952.8) * mm, "radius": 3.18 * mm});
            skCircle(sketch, "E6.124.0.37", {"center": v(212.24, -952.8) * mm, "radius": 3.18 * mm});
            skCircle(sketch, "E6.126.0.37", {"center": v(783.74, -952.8) * mm, "radius": 3.18 * mm});
            skCircle(sketch, "E6.128.0.37", {"center": v(497.99, -952.8) * mm, "radius": 3.18 * mm});
            skCircle(sketch, "E6.130.0.37", {"center": v(402.74, -952.8) * mm, "radius": 3.18 * mm});
            skCircle(sketch, "E6.132.0.37", {"center": v(624.99, -952.8) * mm, "radius": 3.18 * mm});
            skCircle(sketch, "E6.134.0.37", {"center": v(751.99, -952.8) * mm, "radius": 3.18 * mm});
            skCircle(sketch, "E6.136.0.37", {"center": v(466.24, -952.8) * mm, "radius": 3.18 * mm});
            skCircle(sketch, "E6.138.0.37", {"center": v(688.49, -952.8) * mm, "radius": 3.18 * mm});
            skCircle(sketch, "E6.140.0.37", {"center": v(116.99, -952.8) * mm, "radius": 3.18 * mm});
            skCircle(sketch, "E6.142.0.37", {"center": v(85.24, -952.8) * mm, "radius": 3.18 * mm});
            skCircle(sketch, "E6.144.0.37", {"center": v(53.49, -952.8) * mm, "radius": 3.18 * mm});
            skLineSegment(sketch, "E6.146.0.37", {"start": v(-41.76, -952.8) * mm, "end": v(-10.01, -952.8) * mm, "construction": true});
            skCircle(sketch, "E6.149.0.37", {"center": v(21.74, -952.8) * mm, "radius": 3.18 * mm});
            skCircle(sketch, "E6.151.0.37", {"center": v(-10.01, -952.8) * mm, "radius": 3.18 * mm});
            skCircle(sketch, "E6.153.0.37", {"center": v(-41.76, -952.8) * mm, "radius": 3.18 * mm});
            skCircle(sketch, "E7.0.0.38", {"center": v(2244.24, -978.2) * mm, "radius": 3.18 * mm});
            skCircle(sketch, "E7.2.0.38", {"center": v(2180.74, -978.2) * mm, "radius": 3.18 * mm});
            skCircle(sketch, "E7.4.0.38", {"center": v(2339.49, -978.2) * mm, "radius": 3.18 * mm});
            skCircle(sketch, "E7.6.0.38", {"center": v(2307.74, -978.2) * mm, "radius": 3.18 * mm});
            skCircle(sketch, "E7.8.0.38", {"center": v(2275.99, -978.2) * mm, "radius": 3.18 * mm});
            skCircle(sketch, "E7.10.0.38", {"center": v(2212.49, -978.2) * mm, "radius": 3.18 * mm});
            skCircle(sketch, "E7.12.0.38", {"center": v(1958.49, -978.2) * mm, "radius": 3.18 * mm});
            skCircle(sketch, "E7.14.0.38", {"center": v(1894.99, -978.2) * mm, "radius": 3.18 * mm});
            skCircle(sketch, "E7.16.0.38", {"center": v(2117.24, -978.2) * mm, "radius": 3.18 * mm});
            skCircle(sketch, "E7.18.0.38", {"center": v(2085.49, -978.2) * mm, "radius": 3.18 * mm});
            skCircle(sketch, "E7.20.0.38", {"center": v(2053.74, -978.2) * mm, "radius": 3.18 * mm});
            skCircle(sketch, "E7.22.0.38", {"center": v(1926.74, -978.2) * mm, "radius": 3.18 * mm});
            skCircle(sketch, "E7.24.0.38", {"center": v(2021.99, -978.2) * mm, "radius": 3.18 * mm});
            skCircle(sketch, "E7.26.0.38", {"center": v(2148.99, -978.2) * mm, "radius": 3.18 * mm});
            skCircle(sketch, "E7.28.0.38", {"center": v(1990.24, -978.2) * mm, "radius": 3.18 * mm});
            skCircle(sketch, "E7.30.0.38", {"center": v(1450.49, -978.2) * mm, "radius": 3.18 * mm});
            skCircle(sketch, "E7.32.0.38", {"center": v(1228.24, -978.2) * mm, "radius": 3.18 * mm});
            skCircle(sketch, "E7.34.0.38", {"center": v(1736.24, -978.2) * mm, "radius": 3.18 * mm});
            skCircle(sketch, "E7.36.0.38", {"center": v(1386.99, -978.2) * mm, "radius": 3.18 * mm});
            skCircle(sketch, "E7.38.0.38", {"center": v(1164.74, -978.2) * mm, "radius": 3.18 * mm});
            skCircle(sketch, "E7.40.0.38", {"center": v(1672.74, -978.2) * mm, "radius": 3.18 * mm});
            skCircle(sketch, "E7.42.0.38", {"center": v(1101.24, -978.2) * mm, "radius": 3.18 * mm});
            skCircle(sketch, "E7.44.0.38", {"center": v(1609.24, -978.2) * mm, "radius": 3.18 * mm});
            skCircle(sketch, "E7.46.0.38", {"center": v(1355.24, -978.2) * mm, "radius": 3.18 * mm});
            skCircle(sketch, "E7.48.0.38", {"center": v(1863.24, -978.2) * mm, "radius": 3.18 * mm});
            skCircle(sketch, "E7.50.0.38", {"center": v(1069.49, -978.2) * mm, "radius": 3.18 * mm});
            skCircle(sketch, "E7.52.0.38", {"center": v(1577.49, -978.2) * mm, "radius": 3.18 * mm});
            skCircle(sketch, "E7.54.0.38", {"center": v(1323.49, -978.2) * mm, "radius": 3.18 * mm});
            skCircle(sketch, "E7.56.0.38", {"center": v(1831.49, -978.2) * mm, "radius": 3.18 * mm});
            skCircle(sketch, "E7.58.0.38", {"center": v(1037.74, -978.2) * mm, "radius": 3.18 * mm});
            skCircle(sketch, "E7.60.0.38", {"center": v(1545.74, -978.2) * mm, "radius": 3.18 * mm});
            skCircle(sketch, "E7.62.0.38", {"center": v(1418.74, -978.2) * mm, "radius": 3.18 * mm});
            skCircle(sketch, "E7.64.0.38", {"center": v(1005.99, -978.2) * mm, "radius": 3.18 * mm});
            skCircle(sketch, "E7.66.0.38", {"center": v(1513.99, -978.2) * mm, "radius": 3.18 * mm});
            skCircle(sketch, "E7.68.0.38", {"center": v(1799.74, -978.2) * mm, "radius": 3.18 * mm});
            skCircle(sketch, "E7.70.0.38", {"center": v(1291.74, -978.2) * mm, "radius": 3.18 * mm});
            skCircle(sketch, "E7.72.0.38", {"center": v(1132.99, -978.2) * mm, "radius": 3.18 * mm});
            skCircle(sketch, "E7.74.0.38", {"center": v(974.24, -978.2) * mm, "radius": 3.18 * mm});
            skCircle(sketch, "E7.76.0.38", {"center": v(1482.24, -978.2) * mm, "radius": 3.18 * mm});
            skCircle(sketch, "E7.78.0.38", {"center": v(1259.99, -978.2) * mm, "radius": 3.18 * mm});
            skCircle(sketch, "E7.80.0.38", {"center": v(1640.99, -978.2) * mm, "radius": 3.18 * mm});
            skCircle(sketch, "E7.82.0.38", {"center": v(1767.99, -978.2) * mm, "radius": 3.18 * mm});
            skCircle(sketch, "E7.84.0.38", {"center": v(1196.49, -978.2) * mm, "radius": 3.18 * mm});
            skCircle(sketch, "E7.86.0.38", {"center": v(1704.49, -978.2) * mm, "radius": 3.18 * mm});
            skCircle(sketch, "E7.88.0.38", {"center": v(720.24, -978.2) * mm, "radius": 3.18 * mm});
            skCircle(sketch, "E7.90.0.38", {"center": v(942.49, -978.2) * mm, "radius": 3.18 * mm});
            skCircle(sketch, "E7.92.0.38", {"center": v(878.99, -978.2) * mm, "radius": 3.18 * mm});
            skCircle(sketch, "E7.94.0.38", {"center": v(434.49, -978.2) * mm, "radius": 3.18 * mm});
            skCircle(sketch, "E7.96.0.38", {"center": v(656.74, -978.2) * mm, "radius": 3.18 * mm});
            skCircle(sketch, "E7.98.0.38", {"center": v(370.99, -978.2) * mm, "radius": 3.18 * mm});
            skCircle(sketch, "E7.100.0.38", {"center": v(593.24, -978.2) * mm, "radius": 3.18 * mm});
            skCircle(sketch, "E7.102.0.38", {"center": v(847.24, -978.2) * mm, "radius": 3.18 * mm});
            skCircle(sketch, "E7.104.0.38", {"center": v(339.24, -978.2) * mm, "radius": 3.18 * mm});
            skCircle(sketch, "E7.106.0.38", {"center": v(561.49, -978.2) * mm, "radius": 3.18 * mm});
            skCircle(sketch, "E7.108.0.38", {"center": v(815.49, -978.2) * mm, "radius": 3.18 * mm});
            skCircle(sketch, "E7.110.0.38", {"center": v(307.49, -978.2) * mm, "radius": 3.18 * mm});
            skCircle(sketch, "E7.112.0.38", {"center": v(529.74, -978.2) * mm, "radius": 3.18 * mm});
            skCircle(sketch, "E7.114.0.38", {"center": v(180.49, -978.2) * mm, "radius": 3.18 * mm});
            skCircle(sketch, "E7.116.0.38", {"center": v(148.74, -978.2) * mm, "radius": 3.18 * mm});
            skCircle(sketch, "E7.118.0.38", {"center": v(910.74, -978.2) * mm, "radius": 3.18 * mm});
            skCircle(sketch, "E7.120.0.38", {"center": v(275.74, -978.2) * mm, "radius": 3.18 * mm});
            skCircle(sketch, "E7.122.0.38", {"center": v(243.99, -978.2) * mm, "radius": 3.18 * mm});
            skCircle(sketch, "E7.124.0.38", {"center": v(212.24, -978.2) * mm, "radius": 3.18 * mm});
            skCircle(sketch, "E7.126.0.38", {"center": v(783.74, -978.2) * mm, "radius": 3.18 * mm});
            skCircle(sketch, "E7.128.0.38", {"center": v(497.99, -978.2) * mm, "radius": 3.18 * mm});
            skCircle(sketch, "E7.130.0.38", {"center": v(402.74, -978.2) * mm, "radius": 3.18 * mm});
            skCircle(sketch, "E7.132.0.38", {"center": v(624.99, -978.2) * mm, "radius": 3.18 * mm});
            skCircle(sketch, "E7.134.0.38", {"center": v(751.99, -978.2) * mm, "radius": 3.18 * mm});
            skCircle(sketch, "E7.136.0.38", {"center": v(466.24, -978.2) * mm, "radius": 3.18 * mm});
            skCircle(sketch, "E7.138.0.38", {"center": v(688.49, -978.2) * mm, "radius": 3.18 * mm});
            skCircle(sketch, "E7.140.0.38", {"center": v(116.99, -978.2) * mm, "radius": 3.18 * mm});
            skCircle(sketch, "E7.142.0.38", {"center": v(85.24, -978.2) * mm, "radius": 3.18 * mm});
            skCircle(sketch, "E7.144.0.38", {"center": v(53.49, -978.2) * mm, "radius": 3.18 * mm});
            skLineSegment(sketch, "E7.146.0.38", {"start": v(-41.76, -978.2) * mm, "end": v(-10.01, -978.2) * mm, "construction": true});
            skCircle(sketch, "E7.149.0.38", {"center": v(21.74, -978.2) * mm, "radius": 3.18 * mm});
            skCircle(sketch, "E7.151.0.38", {"center": v(-10.01, -978.2) * mm, "radius": 3.18 * mm});
            skCircle(sketch, "E7.153.0.38", {"center": v(-41.76, -978.2) * mm, "radius": 3.18 * mm});
            skCircle(sketch, "E7.0.0.39", {"center": v(2244.24, -1003.6) * mm, "radius": 3.18 * mm});
            skCircle(sketch, "E7.2.0.39", {"center": v(2180.74, -1003.6) * mm, "radius": 3.18 * mm});
            skCircle(sketch, "E7.4.0.39", {"center": v(2339.49, -1003.6) * mm, "radius": 3.18 * mm});
            skCircle(sketch, "E7.6.0.39", {"center": v(2307.74, -1003.6) * mm, "radius": 3.18 * mm});
            skCircle(sketch, "E7.8.0.39", {"center": v(2275.99, -1003.6) * mm, "radius": 3.18 * mm});
            skCircle(sketch, "E7.10.0.39", {"center": v(2212.49, -1003.6) * mm, "radius": 3.18 * mm});
            skCircle(sketch, "E7.12.0.39", {"center": v(1958.49, -1003.6) * mm, "radius": 3.18 * mm});
            skCircle(sketch, "E7.14.0.39", {"center": v(1894.99, -1003.6) * mm, "radius": 3.18 * mm});
            skCircle(sketch, "E7.16.0.39", {"center": v(2117.24, -1003.6) * mm, "radius": 3.18 * mm});
            skCircle(sketch, "E7.18.0.39", {"center": v(2085.49, -1003.6) * mm, "radius": 3.18 * mm});
            skCircle(sketch, "E7.20.0.39", {"center": v(2053.74, -1003.6) * mm, "radius": 3.18 * mm});
            skCircle(sketch, "E7.22.0.39", {"center": v(1926.74, -1003.6) * mm, "radius": 3.18 * mm});
            skCircle(sketch, "E7.24.0.39", {"center": v(2021.99, -1003.6) * mm, "radius": 3.18 * mm});
            skCircle(sketch, "E7.26.0.39", {"center": v(2148.99, -1003.6) * mm, "radius": 3.18 * mm});
            skCircle(sketch, "E7.28.0.39", {"center": v(1990.24, -1003.6) * mm, "radius": 3.18 * mm});
            skCircle(sketch, "E7.30.0.39", {"center": v(1450.49, -1003.6) * mm, "radius": 3.18 * mm});
            skCircle(sketch, "E7.32.0.39", {"center": v(1228.24, -1003.6) * mm, "radius": 3.18 * mm});
            skCircle(sketch, "E7.34.0.39", {"center": v(1736.24, -1003.6) * mm, "radius": 3.18 * mm});
            skCircle(sketch, "E7.36.0.39", {"center": v(1386.99, -1003.6) * mm, "radius": 3.18 * mm});
            skCircle(sketch, "E7.38.0.39", {"center": v(1164.74, -1003.6) * mm, "radius": 3.18 * mm});
            skCircle(sketch, "E7.40.0.39", {"center": v(1672.74, -1003.6) * mm, "radius": 3.18 * mm});
            skCircle(sketch, "E7.42.0.39", {"center": v(1101.24, -1003.6) * mm, "radius": 3.18 * mm});
            skCircle(sketch, "E7.44.0.39", {"center": v(1609.24, -1003.6) * mm, "radius": 3.18 * mm});
            skCircle(sketch, "E7.46.0.39", {"center": v(1355.24, -1003.6) * mm, "radius": 3.18 * mm});
            skCircle(sketch, "E7.48.0.39", {"center": v(1863.24, -1003.6) * mm, "radius": 3.18 * mm});
            skCircle(sketch, "E7.50.0.39", {"center": v(1069.49, -1003.6) * mm, "radius": 3.18 * mm});
            skCircle(sketch, "E7.52.0.39", {"center": v(1577.49, -1003.6) * mm, "radius": 3.18 * mm});
            skCircle(sketch, "E7.54.0.39", {"center": v(1323.49, -1003.6) * mm, "radius": 3.18 * mm});
            skCircle(sketch, "E7.56.0.39", {"center": v(1831.49, -1003.6) * mm, "radius": 3.18 * mm});
            skCircle(sketch, "E7.58.0.39", {"center": v(1037.74, -1003.6) * mm, "radius": 3.18 * mm});
            skCircle(sketch, "E7.60.0.39", {"center": v(1545.74, -1003.6) * mm, "radius": 3.18 * mm});
            skCircle(sketch, "E7.62.0.39", {"center": v(1418.74, -1003.6) * mm, "radius": 3.18 * mm});
            skCircle(sketch, "E7.64.0.39", {"center": v(1005.99, -1003.6) * mm, "radius": 3.18 * mm});
            skCircle(sketch, "E7.66.0.39", {"center": v(1513.99, -1003.6) * mm, "radius": 3.18 * mm});
            skCircle(sketch, "E7.68.0.39", {"center": v(1799.74, -1003.6) * mm, "radius": 3.18 * mm});
            skCircle(sketch, "E7.70.0.39", {"center": v(1291.74, -1003.6) * mm, "radius": 3.18 * mm});
            skCircle(sketch, "E7.72.0.39", {"center": v(1132.99, -1003.6) * mm, "radius": 3.18 * mm});
            skCircle(sketch, "E7.74.0.39", {"center": v(974.24, -1003.6) * mm, "radius": 3.18 * mm});
            skCircle(sketch, "E7.76.0.39", {"center": v(1482.24, -1003.6) * mm, "radius": 3.18 * mm});
            skCircle(sketch, "E7.78.0.39", {"center": v(1259.99, -1003.6) * mm, "radius": 3.18 * mm});
            skCircle(sketch, "E7.80.0.39", {"center": v(1640.99, -1003.6) * mm, "radius": 3.18 * mm});
            skCircle(sketch, "E7.82.0.39", {"center": v(1767.99, -1003.6) * mm, "radius": 3.18 * mm});
            skCircle(sketch, "E7.84.0.39", {"center": v(1196.49, -1003.6) * mm, "radius": 3.18 * mm});
            skCircle(sketch, "E7.86.0.39", {"center": v(1704.49, -1003.6) * mm, "radius": 3.18 * mm});
            skCircle(sketch, "E7.88.0.39", {"center": v(720.24, -1003.6) * mm, "radius": 3.18 * mm});
            skCircle(sketch, "E7.90.0.39", {"center": v(942.49, -1003.6) * mm, "radius": 3.18 * mm});
            skCircle(sketch, "E7.92.0.39", {"center": v(878.99, -1003.6) * mm, "radius": 3.18 * mm});
            skCircle(sketch, "E7.94.0.39", {"center": v(434.49, -1003.6) * mm, "radius": 3.18 * mm});
            skCircle(sketch, "E7.96.0.39", {"center": v(656.74, -1003.6) * mm, "radius": 3.18 * mm});
            skCircle(sketch, "E7.98.0.39", {"center": v(370.99, -1003.6) * mm, "radius": 3.18 * mm});
            skCircle(sketch, "E7.100.0.39", {"center": v(593.24, -1003.6) * mm, "radius": 3.18 * mm});
            skCircle(sketch, "E7.102.0.39", {"center": v(847.24, -1003.6) * mm, "radius": 3.18 * mm});
            skCircle(sketch, "E7.104.0.39", {"center": v(339.24, -1003.6) * mm, "radius": 3.18 * mm});
            skCircle(sketch, "E7.106.0.39", {"center": v(561.49, -1003.6) * mm, "radius": 3.18 * mm});
            skCircle(sketch, "E7.108.0.39", {"center": v(815.49, -1003.6) * mm, "radius": 3.18 * mm});
            skCircle(sketch, "E7.110.0.39", {"center": v(307.49, -1003.6) * mm, "radius": 3.18 * mm});
            skCircle(sketch, "E7.112.0.39", {"center": v(529.74, -1003.6) * mm, "radius": 3.18 * mm});
            skCircle(sketch, "E7.114.0.39", {"center": v(180.49, -1003.6) * mm, "radius": 3.18 * mm});
            skCircle(sketch, "E7.116.0.39", {"center": v(148.74, -1003.6) * mm, "radius": 3.18 * mm});
            skCircle(sketch, "E7.118.0.39", {"center": v(910.74, -1003.6) * mm, "radius": 3.18 * mm});
            skCircle(sketch, "E7.120.0.39", {"center": v(275.74, -1003.6) * mm, "radius": 3.18 * mm});
            skCircle(sketch, "E7.122.0.39", {"center": v(243.99, -1003.6) * mm, "radius": 3.18 * mm});
            skCircle(sketch, "E7.124.0.39", {"center": v(212.24, -1003.6) * mm, "radius": 3.18 * mm});
            skCircle(sketch, "E7.126.0.39", {"center": v(783.74, -1003.6) * mm, "radius": 3.18 * mm});
            skCircle(sketch, "E7.128.0.39", {"center": v(497.99, -1003.6) * mm, "radius": 3.18 * mm});
            skCircle(sketch, "E7.130.0.39", {"center": v(402.74, -1003.6) * mm, "radius": 3.18 * mm});
            skCircle(sketch, "E7.132.0.39", {"center": v(624.99, -1003.6) * mm, "radius": 3.18 * mm});
            skCircle(sketch, "E7.134.0.39", {"center": v(751.99, -1003.6) * mm, "radius": 3.18 * mm});
            skCircle(sketch, "E7.136.0.39", {"center": v(466.24, -1003.6) * mm, "radius": 3.18 * mm});
            skCircle(sketch, "E7.138.0.39", {"center": v(688.49, -1003.6) * mm, "radius": 3.18 * mm});
            skCircle(sketch, "E7.140.0.39", {"center": v(116.99, -1003.6) * mm, "radius": 3.18 * mm});
            skCircle(sketch, "E7.142.0.39", {"center": v(85.24, -1003.6) * mm, "radius": 3.18 * mm});
            skCircle(sketch, "E7.144.0.39", {"center": v(53.49, -1003.6) * mm, "radius": 3.18 * mm});
            skLineSegment(sketch, "E7.146.0.39", {"start": v(-41.76, -1003.6) * mm, "end": v(-10.01, -1003.6) * mm, "construction": true});
            skCircle(sketch, "E7.149.0.39", {"center": v(21.74, -1003.6) * mm, "radius": 3.18 * mm});
            skCircle(sketch, "E7.151.0.39", {"center": v(-10.01, -1003.6) * mm, "radius": 3.18 * mm});
            skCircle(sketch, "E7.153.0.39", {"center": v(-41.76, -1003.6) * mm, "radius": 3.18 * mm});
            skCircle(sketch, "E7.0.0.40", {"center": v(2244.24, -1029) * mm, "radius": 3.18 * mm});
            skCircle(sketch, "E7.2.0.40", {"center": v(2180.74, -1029) * mm, "radius": 3.18 * mm});
            skCircle(sketch, "E7.4.0.40", {"center": v(2339.49, -1029) * mm, "radius": 3.18 * mm});
            skCircle(sketch, "E7.6.0.40", {"center": v(2307.74, -1029) * mm, "radius": 3.18 * mm});
            skCircle(sketch, "E7.8.0.40", {"center": v(2275.99, -1029) * mm, "radius": 3.18 * mm});
            skCircle(sketch, "E7.10.0.40", {"center": v(2212.49, -1029) * mm, "radius": 3.18 * mm});
            skCircle(sketch, "E7.12.0.40", {"center": v(1958.49, -1029) * mm, "radius": 3.18 * mm});
            skCircle(sketch, "E7.14.0.40", {"center": v(1894.99, -1029) * mm, "radius": 3.18 * mm});
            skCircle(sketch, "E7.16.0.40", {"center": v(2117.24, -1029) * mm, "radius": 3.18 * mm});
            skCircle(sketch, "E7.18.0.40", {"center": v(2085.49, -1029) * mm, "radius": 3.18 * mm});
            skCircle(sketch, "E7.20.0.40", {"center": v(2053.74, -1029) * mm, "radius": 3.18 * mm});
            skCircle(sketch, "E7.22.0.40", {"center": v(1926.74, -1029) * mm, "radius": 3.18 * mm});
            skCircle(sketch, "E7.24.0.40", {"center": v(2021.99, -1029) * mm, "radius": 3.18 * mm});
            skCircle(sketch, "E7.26.0.40", {"center": v(2148.99, -1029) * mm, "radius": 3.18 * mm});
            skCircle(sketch, "E7.28.0.40", {"center": v(1990.24, -1029) * mm, "radius": 3.18 * mm});
            skCircle(sketch, "E7.30.0.40", {"center": v(1450.49, -1029) * mm, "radius": 3.18 * mm});
            skCircle(sketch, "E7.32.0.40", {"center": v(1228.24, -1029) * mm, "radius": 3.18 * mm});
            skCircle(sketch, "E7.34.0.40", {"center": v(1736.24, -1029) * mm, "radius": 3.18 * mm});
            skCircle(sketch, "E7.36.0.40", {"center": v(1386.99, -1029) * mm, "radius": 3.18 * mm});
            skCircle(sketch, "E7.38.0.40", {"center": v(1164.74, -1029) * mm, "radius": 3.18 * mm});
            skCircle(sketch, "E7.40.0.40", {"center": v(1672.74, -1029) * mm, "radius": 3.18 * mm});
            skCircle(sketch, "E7.42.0.40", {"center": v(1101.24, -1029) * mm, "radius": 3.18 * mm});
            skCircle(sketch, "E7.44.0.40", {"center": v(1609.24, -1029) * mm, "radius": 3.18 * mm});
            skCircle(sketch, "E7.46.0.40", {"center": v(1355.24, -1029) * mm, "radius": 3.18 * mm});
            skCircle(sketch, "E7.48.0.40", {"center": v(1863.24, -1029) * mm, "radius": 3.18 * mm});
            skCircle(sketch, "E7.50.0.40", {"center": v(1069.49, -1029) * mm, "radius": 3.18 * mm});
            skCircle(sketch, "E7.52.0.40", {"center": v(1577.49, -1029) * mm, "radius": 3.18 * mm});
            skCircle(sketch, "E7.54.0.40", {"center": v(1323.49, -1029) * mm, "radius": 3.18 * mm});
            skCircle(sketch, "E7.56.0.40", {"center": v(1831.49, -1029) * mm, "radius": 3.18 * mm});
            skCircle(sketch, "E7.58.0.40", {"center": v(1037.74, -1029) * mm, "radius": 3.18 * mm});
            skCircle(sketch, "E7.60.0.40", {"center": v(1545.74, -1029) * mm, "radius": 3.18 * mm});
            skCircle(sketch, "E7.62.0.40", {"center": v(1418.74, -1029) * mm, "radius": 3.18 * mm});
            skCircle(sketch, "E7.64.0.40", {"center": v(1005.99, -1029) * mm, "radius": 3.18 * mm});
            skCircle(sketch, "E7.66.0.40", {"center": v(1513.99, -1029) * mm, "radius": 3.18 * mm});
            skCircle(sketch, "E7.68.0.40", {"center": v(1799.74, -1029) * mm, "radius": 3.18 * mm});
            skCircle(sketch, "E7.70.0.40", {"center": v(1291.74, -1029) * mm, "radius": 3.18 * mm});
            skCircle(sketch, "E7.72.0.40", {"center": v(1132.99, -1029) * mm, "radius": 3.18 * mm});
            skCircle(sketch, "E7.74.0.40", {"center": v(974.24, -1029) * mm, "radius": 3.18 * mm});
            skCircle(sketch, "E7.76.0.40", {"center": v(1482.24, -1029) * mm, "radius": 3.18 * mm});
            skCircle(sketch, "E7.78.0.40", {"center": v(1259.99, -1029) * mm, "radius": 3.18 * mm});
            skCircle(sketch, "E7.80.0.40", {"center": v(1640.99, -1029) * mm, "radius": 3.18 * mm});
            skCircle(sketch, "E7.82.0.40", {"center": v(1767.99, -1029) * mm, "radius": 3.18 * mm});
            skCircle(sketch, "E7.84.0.40", {"center": v(1196.49, -1029) * mm, "radius": 3.18 * mm});
            skCircle(sketch, "E7.86.0.40", {"center": v(1704.49, -1029) * mm, "radius": 3.18 * mm});
            skCircle(sketch, "E7.88.0.40", {"center": v(720.24, -1029) * mm, "radius": 3.18 * mm});
            skCircle(sketch, "E7.90.0.40", {"center": v(942.49, -1029) * mm, "radius": 3.18 * mm});
            skCircle(sketch, "E7.92.0.40", {"center": v(878.99, -1029) * mm, "radius": 3.18 * mm});
            skCircle(sketch, "E7.94.0.40", {"center": v(434.49, -1029) * mm, "radius": 3.18 * mm});
            skCircle(sketch, "E7.96.0.40", {"center": v(656.74, -1029) * mm, "radius": 3.18 * mm});
            skCircle(sketch, "E7.98.0.40", {"center": v(370.99, -1029) * mm, "radius": 3.18 * mm});
            skCircle(sketch, "E7.100.0.40", {"center": v(593.24, -1029) * mm, "radius": 3.18 * mm});
            skCircle(sketch, "E7.102.0.40", {"center": v(847.24, -1029) * mm, "radius": 3.18 * mm});
            skCircle(sketch, "E7.104.0.40", {"center": v(339.24, -1029) * mm, "radius": 3.18 * mm});
            skCircle(sketch, "E7.106.0.40", {"center": v(561.49, -1029) * mm, "radius": 3.18 * mm});
            skCircle(sketch, "E7.108.0.40", {"center": v(815.49, -1029) * mm, "radius": 3.18 * mm});
            skCircle(sketch, "E7.110.0.40", {"center": v(307.49, -1029) * mm, "radius": 3.18 * mm});
            skCircle(sketch, "E7.112.0.40", {"center": v(529.74, -1029) * mm, "radius": 3.18 * mm});
            skCircle(sketch, "E7.114.0.40", {"center": v(180.49, -1029) * mm, "radius": 3.18 * mm});
            skCircle(sketch, "E7.116.0.40", {"center": v(148.74, -1029) * mm, "radius": 3.18 * mm});
            skCircle(sketch, "E7.118.0.40", {"center": v(910.74, -1029) * mm, "radius": 3.18 * mm});
            skCircle(sketch, "E7.120.0.40", {"center": v(275.74, -1029) * mm, "radius": 3.18 * mm});
            skCircle(sketch, "E7.122.0.40", {"center": v(243.99, -1029) * mm, "radius": 3.18 * mm});
            skCircle(sketch, "E7.124.0.40", {"center": v(212.24, -1029) * mm, "radius": 3.18 * mm});
            skCircle(sketch, "E7.126.0.40", {"center": v(783.74, -1029) * mm, "radius": 3.18 * mm});
            skCircle(sketch, "E7.128.0.40", {"center": v(497.99, -1029) * mm, "radius": 3.18 * mm});
            skCircle(sketch, "E7.130.0.40", {"center": v(402.74, -1029) * mm, "radius": 3.18 * mm});
            skCircle(sketch, "E7.132.0.40", {"center": v(624.99, -1029) * mm, "radius": 3.18 * mm});
            skCircle(sketch, "E7.134.0.40", {"center": v(751.99, -1029) * mm, "radius": 3.18 * mm});
            skCircle(sketch, "E7.136.0.40", {"center": v(466.24, -1029) * mm, "radius": 3.18 * mm});
            skCircle(sketch, "E7.138.0.40", {"center": v(688.49, -1029) * mm, "radius": 3.18 * mm});
            skCircle(sketch, "E7.140.0.40", {"center": v(116.99, -1029) * mm, "radius": 3.18 * mm});
            skCircle(sketch, "E7.142.0.40", {"center": v(85.24, -1029) * mm, "radius": 3.18 * mm});
            skCircle(sketch, "E7.144.0.40", {"center": v(53.49, -1029) * mm, "radius": 3.18 * mm});
            skLineSegment(sketch, "E7.146.0.40", {"start": v(-41.76, -1029) * mm, "end": v(-10.01, -1029) * mm, "construction": true});
            skCircle(sketch, "E7.149.0.40", {"center": v(21.74, -1029) * mm, "radius": 3.18 * mm});
            skCircle(sketch, "E7.151.0.40", {"center": v(-10.01, -1029) * mm, "radius": 3.18 * mm});
            skCircle(sketch, "E7.153.0.40", {"center": v(-41.76, -1029) * mm, "radius": 3.18 * mm});
            skCircle(sketch, "E7.0.0.41", {"center": v(2244.24, -1054.4) * mm, "radius": 3.18 * mm});
            skCircle(sketch, "E7.2.0.41", {"center": v(2180.74, -1054.4) * mm, "radius": 3.18 * mm});
            skCircle(sketch, "E7.4.0.41", {"center": v(2339.49, -1054.4) * mm, "radius": 3.18 * mm});
            skCircle(sketch, "E7.6.0.41", {"center": v(2307.74, -1054.4) * mm, "radius": 3.18 * mm});
            skCircle(sketch, "E7.8.0.41", {"center": v(2275.99, -1054.4) * mm, "radius": 3.18 * mm});
            skCircle(sketch, "E7.10.0.41", {"center": v(2212.49, -1054.4) * mm, "radius": 3.18 * mm});
            skCircle(sketch, "E7.12.0.41", {"center": v(1958.49, -1054.4) * mm, "radius": 3.18 * mm});
            skCircle(sketch, "E7.14.0.41", {"center": v(1894.99, -1054.4) * mm, "radius": 3.18 * mm});
            skCircle(sketch, "E7.16.0.41", {"center": v(2117.24, -1054.4) * mm, "radius": 3.18 * mm});
            skCircle(sketch, "E7.18.0.41", {"center": v(2085.49, -1054.4) * mm, "radius": 3.18 * mm});
            skCircle(sketch, "E7.20.0.41", {"center": v(2053.74, -1054.4) * mm, "radius": 3.18 * mm});
            skCircle(sketch, "E7.22.0.41", {"center": v(1926.74, -1054.4) * mm, "radius": 3.18 * mm});
            skCircle(sketch, "E7.24.0.41", {"center": v(2021.99, -1054.4) * mm, "radius": 3.18 * mm});
            skCircle(sketch, "E7.26.0.41", {"center": v(2148.99, -1054.4) * mm, "radius": 3.18 * mm});
            skCircle(sketch, "E7.28.0.41", {"center": v(1990.24, -1054.4) * mm, "radius": 3.18 * mm});
            skCircle(sketch, "E7.30.0.41", {"center": v(1450.49, -1054.4) * mm, "radius": 3.18 * mm});
            skCircle(sketch, "E7.32.0.41", {"center": v(1228.24, -1054.4) * mm, "radius": 3.18 * mm});
            skCircle(sketch, "E7.34.0.41", {"center": v(1736.24, -1054.4) * mm, "radius": 3.18 * mm});
            skCircle(sketch, "E7.36.0.41", {"center": v(1386.99, -1054.4) * mm, "radius": 3.18 * mm});
            skCircle(sketch, "E7.38.0.41", {"center": v(1164.74, -1054.4) * mm, "radius": 3.18 * mm});
            skCircle(sketch, "E7.40.0.41", {"center": v(1672.74, -1054.4) * mm, "radius": 3.18 * mm});
            skCircle(sketch, "E7.42.0.41", {"center": v(1101.24, -1054.4) * mm, "radius": 3.18 * mm});
            skCircle(sketch, "E7.44.0.41", {"center": v(1609.24, -1054.4) * mm, "radius": 3.18 * mm});
            skCircle(sketch, "E7.46.0.41", {"center": v(1355.24, -1054.4) * mm, "radius": 3.18 * mm});
            skCircle(sketch, "E7.48.0.41", {"center": v(1863.24, -1054.4) * mm, "radius": 3.18 * mm});
            skCircle(sketch, "E7.50.0.41", {"center": v(1069.49, -1054.4) * mm, "radius": 3.18 * mm});
            skCircle(sketch, "E7.52.0.41", {"center": v(1577.49, -1054.4) * mm, "radius": 3.18 * mm});
            skCircle(sketch, "E7.54.0.41", {"center": v(1323.49, -1054.4) * mm, "radius": 3.18 * mm});
            skCircle(sketch, "E7.56.0.41", {"center": v(1831.49, -1054.4) * mm, "radius": 3.18 * mm});
            skCircle(sketch, "E7.58.0.41", {"center": v(1037.74, -1054.4) * mm, "radius": 3.18 * mm});
            skCircle(sketch, "E7.60.0.41", {"center": v(1545.74, -1054.4) * mm, "radius": 3.18 * mm});
            skCircle(sketch, "E7.62.0.41", {"center": v(1418.74, -1054.4) * mm, "radius": 3.18 * mm});
            skCircle(sketch, "E7.64.0.41", {"center": v(1005.99, -1054.4) * mm, "radius": 3.18 * mm});
            skCircle(sketch, "E7.66.0.41", {"center": v(1513.99, -1054.4) * mm, "radius": 3.18 * mm});
            skCircle(sketch, "E7.68.0.41", {"center": v(1799.74, -1054.4) * mm, "radius": 3.18 * mm});
            skCircle(sketch, "E7.70.0.41", {"center": v(1291.74, -1054.4) * mm, "radius": 3.18 * mm});
            skCircle(sketch, "E7.72.0.41", {"center": v(1132.99, -1054.4) * mm, "radius": 3.18 * mm});
            skCircle(sketch, "E7.74.0.41", {"center": v(974.24, -1054.4) * mm, "radius": 3.18 * mm});
            skCircle(sketch, "E7.76.0.41", {"center": v(1482.24, -1054.4) * mm, "radius": 3.18 * mm});
            skCircle(sketch, "E7.78.0.41", {"center": v(1259.99, -1054.4) * mm, "radius": 3.18 * mm});
            skCircle(sketch, "E7.80.0.41", {"center": v(1640.99, -1054.4) * mm, "radius": 3.18 * mm});
            skCircle(sketch, "E7.82.0.41", {"center": v(1767.99, -1054.4) * mm, "radius": 3.18 * mm});
            skCircle(sketch, "E7.84.0.41", {"center": v(1196.49, -1054.4) * mm, "radius": 3.18 * mm});
            skCircle(sketch, "E7.86.0.41", {"center": v(1704.49, -1054.4) * mm, "radius": 3.18 * mm});
            skCircle(sketch, "E7.88.0.41", {"center": v(720.24, -1054.4) * mm, "radius": 3.18 * mm});
            skCircle(sketch, "E7.90.0.41", {"center": v(942.49, -1054.4) * mm, "radius": 3.18 * mm});
            skCircle(sketch, "E7.92.0.41", {"center": v(878.99, -1054.4) * mm, "radius": 3.18 * mm});
            skCircle(sketch, "E7.94.0.41", {"center": v(434.49, -1054.4) * mm, "radius": 3.18 * mm});
            skCircle(sketch, "E7.96.0.41", {"center": v(656.74, -1054.4) * mm, "radius": 3.18 * mm});
            skCircle(sketch, "E7.98.0.41", {"center": v(370.99, -1054.4) * mm, "radius": 3.18 * mm});
            skCircle(sketch, "E7.100.0.41", {"center": v(593.24, -1054.4) * mm, "radius": 3.18 * mm});
            skCircle(sketch, "E7.102.0.41", {"center": v(847.24, -1054.4) * mm, "radius": 3.18 * mm});
            skCircle(sketch, "E7.104.0.41", {"center": v(339.24, -1054.4) * mm, "radius": 3.18 * mm});
            skCircle(sketch, "E7.106.0.41", {"center": v(561.49, -1054.4) * mm, "radius": 3.18 * mm});
            skCircle(sketch, "E7.108.0.41", {"center": v(815.49, -1054.4) * mm, "radius": 3.18 * mm});
            skCircle(sketch, "E7.110.0.41", {"center": v(307.49, -1054.4) * mm, "radius": 3.18 * mm});
            skCircle(sketch, "E7.112.0.41", {"center": v(529.74, -1054.4) * mm, "radius": 3.18 * mm});
            skCircle(sketch, "E7.114.0.41", {"center": v(180.49, -1054.4) * mm, "radius": 3.18 * mm});
            skCircle(sketch, "E7.116.0.41", {"center": v(148.74, -1054.4) * mm, "radius": 3.18 * mm});
            skCircle(sketch, "E7.118.0.41", {"center": v(910.74, -1054.4) * mm, "radius": 3.18 * mm});
            skCircle(sketch, "E7.120.0.41", {"center": v(275.74, -1054.4) * mm, "radius": 3.18 * mm});
            skCircle(sketch, "E7.122.0.41", {"center": v(243.99, -1054.4) * mm, "radius": 3.18 * mm});
            skCircle(sketch, "E7.124.0.41", {"center": v(212.24, -1054.4) * mm, "radius": 3.18 * mm});
            skCircle(sketch, "E7.126.0.41", {"center": v(783.74, -1054.4) * mm, "radius": 3.18 * mm});
            skCircle(sketch, "E7.128.0.41", {"center": v(497.99, -1054.4) * mm, "radius": 3.18 * mm});
            skCircle(sketch, "E7.130.0.41", {"center": v(402.74, -1054.4) * mm, "radius": 3.18 * mm});
            skCircle(sketch, "E7.132.0.41", {"center": v(624.99, -1054.4) * mm, "radius": 3.18 * mm});
            skCircle(sketch, "E7.134.0.41", {"center": v(751.99, -1054.4) * mm, "radius": 3.18 * mm});
            skCircle(sketch, "E7.136.0.41", {"center": v(466.24, -1054.4) * mm, "radius": 3.18 * mm});
            skCircle(sketch, "E7.138.0.41", {"center": v(688.49, -1054.4) * mm, "radius": 3.18 * mm});
            skCircle(sketch, "E7.140.0.41", {"center": v(116.99, -1054.4) * mm, "radius": 3.18 * mm});
            skCircle(sketch, "E7.142.0.41", {"center": v(85.24, -1054.4) * mm, "radius": 3.18 * mm});
            skCircle(sketch, "E7.144.0.41", {"center": v(53.49, -1054.4) * mm, "radius": 3.18 * mm});
            skLineSegment(sketch, "E7.146.0.41", {"start": v(-41.76, -1054.4) * mm, "end": v(-10.01, -1054.4) * mm, "construction": true});
            skCircle(sketch, "E7.149.0.41", {"center": v(21.74, -1054.4) * mm, "radius": 3.18 * mm});
            skCircle(sketch, "E7.151.0.41", {"center": v(-10.01, -1054.4) * mm, "radius": 3.18 * mm});
            skCircle(sketch, "E7.153.0.41", {"center": v(-41.76, -1054.4) * mm, "radius": 3.18 * mm});
            skCircle(sketch, "E7.0.0.42", {"center": v(2244.24, -1079.8) * mm, "radius": 3.18 * mm});
            skCircle(sketch, "E7.2.0.42", {"center": v(2180.74, -1079.8) * mm, "radius": 3.18 * mm});
            skCircle(sketch, "E7.4.0.42", {"center": v(2339.49, -1079.8) * mm, "radius": 3.18 * mm});
            skCircle(sketch, "E7.6.0.42", {"center": v(2307.74, -1079.8) * mm, "radius": 3.18 * mm});
            skCircle(sketch, "E7.8.0.42", {"center": v(2275.99, -1079.8) * mm, "radius": 3.18 * mm});
            skCircle(sketch, "E7.10.0.42", {"center": v(2212.49, -1079.8) * mm, "radius": 3.18 * mm});
            skCircle(sketch, "E7.12.0.42", {"center": v(1958.49, -1079.8) * mm, "radius": 3.18 * mm});
            skCircle(sketch, "E7.14.0.42", {"center": v(1894.99, -1079.8) * mm, "radius": 3.18 * mm});
            skCircle(sketch, "E7.16.0.42", {"center": v(2117.24, -1079.8) * mm, "radius": 3.18 * mm});
            skCircle(sketch, "E7.18.0.42", {"center": v(2085.49, -1079.8) * mm, "radius": 3.18 * mm});
            skCircle(sketch, "E7.20.0.42", {"center": v(2053.74, -1079.8) * mm, "radius": 3.18 * mm});
            skCircle(sketch, "E7.22.0.42", {"center": v(1926.74, -1079.8) * mm, "radius": 3.18 * mm});
            skCircle(sketch, "E7.24.0.42", {"center": v(2021.99, -1079.8) * mm, "radius": 3.18 * mm});
            skCircle(sketch, "E7.26.0.42", {"center": v(2148.99, -1079.8) * mm, "radius": 3.18 * mm});
            skCircle(sketch, "E7.28.0.42", {"center": v(1990.24, -1079.8) * mm, "radius": 3.18 * mm});
            skCircle(sketch, "E7.30.0.42", {"center": v(1450.49, -1079.8) * mm, "radius": 3.18 * mm});
            skCircle(sketch, "E7.32.0.42", {"center": v(1228.24, -1079.8) * mm, "radius": 3.18 * mm});
            skCircle(sketch, "E7.34.0.42", {"center": v(1736.24, -1079.8) * mm, "radius": 3.18 * mm});
            skCircle(sketch, "E7.36.0.42", {"center": v(1386.99, -1079.8) * mm, "radius": 3.18 * mm});
            skCircle(sketch, "E7.38.0.42", {"center": v(1164.74, -1079.8) * mm, "radius": 3.18 * mm});
            skCircle(sketch, "E7.40.0.42", {"center": v(1672.74, -1079.8) * mm, "radius": 3.18 * mm});
            skCircle(sketch, "E7.42.0.42", {"center": v(1101.24, -1079.8) * mm, "radius": 3.18 * mm});
            skCircle(sketch, "E7.44.0.42", {"center": v(1609.24, -1079.8) * mm, "radius": 3.18 * mm});
            skCircle(sketch, "E7.46.0.42", {"center": v(1355.24, -1079.8) * mm, "radius": 3.18 * mm});
            skCircle(sketch, "E7.48.0.42", {"center": v(1863.24, -1079.8) * mm, "radius": 3.18 * mm});
            skCircle(sketch, "E7.50.0.42", {"center": v(1069.49, -1079.8) * mm, "radius": 3.18 * mm});
            skCircle(sketch, "E7.52.0.42", {"center": v(1577.49, -1079.8) * mm, "radius": 3.18 * mm});
            skCircle(sketch, "E7.54.0.42", {"center": v(1323.49, -1079.8) * mm, "radius": 3.18 * mm});
            skCircle(sketch, "E7.56.0.42", {"center": v(1831.49, -1079.8) * mm, "radius": 3.18 * mm});
            skCircle(sketch, "E7.58.0.42", {"center": v(1037.74, -1079.8) * mm, "radius": 3.18 * mm});
            skCircle(sketch, "E7.60.0.42", {"center": v(1545.74, -1079.8) * mm, "radius": 3.18 * mm});
            skCircle(sketch, "E7.62.0.42", {"center": v(1418.74, -1079.8) * mm, "radius": 3.18 * mm});
            skCircle(sketch, "E7.64.0.42", {"center": v(1005.99, -1079.8) * mm, "radius": 3.18 * mm});
            skCircle(sketch, "E7.66.0.42", {"center": v(1513.99, -1079.8) * mm, "radius": 3.18 * mm});
            skCircle(sketch, "E7.68.0.42", {"center": v(1799.74, -1079.8) * mm, "radius": 3.18 * mm});
            skCircle(sketch, "E7.70.0.42", {"center": v(1291.74, -1079.8) * mm, "radius": 3.18 * mm});
            skCircle(sketch, "E7.72.0.42", {"center": v(1132.99, -1079.8) * mm, "radius": 3.18 * mm});
            skCircle(sketch, "E7.74.0.42", {"center": v(974.24, -1079.8) * mm, "radius": 3.18 * mm});
            skCircle(sketch, "E7.76.0.42", {"center": v(1482.24, -1079.8) * mm, "radius": 3.18 * mm});
            skCircle(sketch, "E7.78.0.42", {"center": v(1259.99, -1079.8) * mm, "radius": 3.18 * mm});
            skCircle(sketch, "E7.80.0.42", {"center": v(1640.99, -1079.8) * mm, "radius": 3.18 * mm});
            skCircle(sketch, "E7.82.0.42", {"center": v(1767.99, -1079.8) * mm, "radius": 3.18 * mm});
            skCircle(sketch, "E7.84.0.42", {"center": v(1196.49, -1079.8) * mm, "radius": 3.18 * mm});
            skCircle(sketch, "E7.86.0.42", {"center": v(1704.49, -1079.8) * mm, "radius": 3.18 * mm});
            skCircle(sketch, "E7.88.0.42", {"center": v(720.24, -1079.8) * mm, "radius": 3.18 * mm});
            skCircle(sketch, "E7.90.0.42", {"center": v(942.49, -1079.8) * mm, "radius": 3.18 * mm});
            skCircle(sketch, "E7.92.0.42", {"center": v(878.99, -1079.8) * mm, "radius": 3.18 * mm});
            skCircle(sketch, "E7.94.0.42", {"center": v(434.49, -1079.8) * mm, "radius": 3.18 * mm});
            skCircle(sketch, "E7.96.0.42", {"center": v(656.74, -1079.8) * mm, "radius": 3.18 * mm});
            skCircle(sketch, "E7.98.0.42", {"center": v(370.99, -1079.8) * mm, "radius": 3.18 * mm});
            skCircle(sketch, "E7.100.0.42", {"center": v(593.24, -1079.8) * mm, "radius": 3.18 * mm});
            skCircle(sketch, "E7.102.0.42", {"center": v(847.24, -1079.8) * mm, "radius": 3.18 * mm});
            skCircle(sketch, "E7.104.0.42", {"center": v(339.24, -1079.8) * mm, "radius": 3.18 * mm});
            skCircle(sketch, "E7.106.0.42", {"center": v(561.49, -1079.8) * mm, "radius": 3.18 * mm});
            skCircle(sketch, "E7.108.0.42", {"center": v(815.49, -1079.8) * mm, "radius": 3.18 * mm});
            skCircle(sketch, "E7.110.0.42", {"center": v(307.49, -1079.8) * mm, "radius": 3.18 * mm});
            skCircle(sketch, "E7.112.0.42", {"center": v(529.74, -1079.8) * mm, "radius": 3.18 * mm});
            skCircle(sketch, "E7.114.0.42", {"center": v(180.49, -1079.8) * mm, "radius": 3.18 * mm});
            skCircle(sketch, "E7.116.0.42", {"center": v(148.74, -1079.8) * mm, "radius": 3.18 * mm});
            skCircle(sketch, "E7.118.0.42", {"center": v(910.74, -1079.8) * mm, "radius": 3.18 * mm});
            skCircle(sketch, "E7.120.0.42", {"center": v(275.74, -1079.8) * mm, "radius": 3.18 * mm});
            skCircle(sketch, "E7.122.0.42", {"center": v(243.99, -1079.8) * mm, "radius": 3.18 * mm});
            skCircle(sketch, "E7.124.0.42", {"center": v(212.24, -1079.8) * mm, "radius": 3.18 * mm});
            skCircle(sketch, "E7.126.0.42", {"center": v(783.74, -1079.8) * mm, "radius": 3.18 * mm});
            skCircle(sketch, "E7.128.0.42", {"center": v(497.99, -1079.8) * mm, "radius": 3.18 * mm});
            skCircle(sketch, "E7.130.0.42", {"center": v(402.74, -1079.8) * mm, "radius": 3.18 * mm});
            skCircle(sketch, "E7.132.0.42", {"center": v(624.99, -1079.8) * mm, "radius": 3.18 * mm});
            skCircle(sketch, "E7.134.0.42", {"center": v(751.99, -1079.8) * mm, "radius": 3.18 * mm});
            skCircle(sketch, "E7.136.0.42", {"center": v(466.24, -1079.8) * mm, "radius": 3.18 * mm});
            skCircle(sketch, "E7.138.0.42", {"center": v(688.49, -1079.8) * mm, "radius": 3.18 * mm});
            skCircle(sketch, "E7.140.0.42", {"center": v(116.99, -1079.8) * mm, "radius": 3.18 * mm});
            skCircle(sketch, "E7.142.0.42", {"center": v(85.24, -1079.8) * mm, "radius": 3.18 * mm});
            skCircle(sketch, "E7.144.0.42", {"center": v(53.49, -1079.8) * mm, "radius": 3.18 * mm});
            skLineSegment(sketch, "E7.146.0.42", {"start": v(-41.76, -1079.8) * mm, "end": v(-10.01, -1079.8) * mm, "construction": true});
            skCircle(sketch, "E7.149.0.42", {"center": v(21.74, -1079.8) * mm, "radius": 3.18 * mm});
            skCircle(sketch, "E7.151.0.42", {"center": v(-10.01, -1079.8) * mm, "radius": 3.18 * mm});
            skCircle(sketch, "E7.153.0.42", {"center": v(-41.76, -1079.8) * mm, "radius": 3.18 * mm});
            skCircle(sketch, "E7.0.0.43", {"center": v(2244.24, -1105.2) * mm, "radius": 3.18 * mm});
            skCircle(sketch, "E7.2.0.43", {"center": v(2180.74, -1105.2) * mm, "radius": 3.18 * mm});
            skCircle(sketch, "E7.4.0.43", {"center": v(2339.49, -1105.2) * mm, "radius": 3.18 * mm});
            skCircle(sketch, "E7.6.0.43", {"center": v(2307.74, -1105.2) * mm, "radius": 3.18 * mm});
            skCircle(sketch, "E7.8.0.43", {"center": v(2275.99, -1105.2) * mm, "radius": 3.18 * mm});
            skCircle(sketch, "E7.10.0.43", {"center": v(2212.49, -1105.2) * mm, "radius": 3.18 * mm});
            skCircle(sketch, "E7.12.0.43", {"center": v(1958.49, -1105.2) * mm, "radius": 3.18 * mm});
            skCircle(sketch, "E7.14.0.43", {"center": v(1894.99, -1105.2) * mm, "radius": 3.18 * mm});
            skCircle(sketch, "E7.16.0.43", {"center": v(2117.24, -1105.2) * mm, "radius": 3.18 * mm});
            skCircle(sketch, "E7.18.0.43", {"center": v(2085.49, -1105.2) * mm, "radius": 3.18 * mm});
            skCircle(sketch, "E7.20.0.43", {"center": v(2053.74, -1105.2) * mm, "radius": 3.18 * mm});
            skCircle(sketch, "E7.22.0.43", {"center": v(1926.74, -1105.2) * mm, "radius": 3.18 * mm});
            skCircle(sketch, "E7.24.0.43", {"center": v(2021.99, -1105.2) * mm, "radius": 3.18 * mm});
            skCircle(sketch, "E7.26.0.43", {"center": v(2148.99, -1105.2) * mm, "radius": 3.18 * mm});
            skCircle(sketch, "E7.28.0.43", {"center": v(1990.24, -1105.2) * mm, "radius": 3.18 * mm});
            skCircle(sketch, "E7.30.0.43", {"center": v(1450.49, -1105.2) * mm, "radius": 3.18 * mm});
            skCircle(sketch, "E7.32.0.43", {"center": v(1228.24, -1105.2) * mm, "radius": 3.18 * mm});
            skCircle(sketch, "E7.34.0.43", {"center": v(1736.24, -1105.2) * mm, "radius": 3.18 * mm});
            skCircle(sketch, "E7.36.0.43", {"center": v(1386.99, -1105.2) * mm, "radius": 3.18 * mm});
            skCircle(sketch, "E7.38.0.43", {"center": v(1164.74, -1105.2) * mm, "radius": 3.18 * mm});
            skCircle(sketch, "E7.40.0.43", {"center": v(1672.74, -1105.2) * mm, "radius": 3.18 * mm});
            skCircle(sketch, "E7.42.0.43", {"center": v(1101.24, -1105.2) * mm, "radius": 3.18 * mm});
            skCircle(sketch, "E7.44.0.43", {"center": v(1609.24, -1105.2) * mm, "radius": 3.18 * mm});
            skCircle(sketch, "E7.46.0.43", {"center": v(1355.24, -1105.2) * mm, "radius": 3.18 * mm});
            skCircle(sketch, "E7.48.0.43", {"center": v(1863.24, -1105.2) * mm, "radius": 3.18 * mm});
            skCircle(sketch, "E7.50.0.43", {"center": v(1069.49, -1105.2) * mm, "radius": 3.18 * mm});
            skCircle(sketch, "E7.52.0.43", {"center": v(1577.49, -1105.2) * mm, "radius": 3.18 * mm});
            skCircle(sketch, "E7.54.0.43", {"center": v(1323.49, -1105.2) * mm, "radius": 3.18 * mm});
            skCircle(sketch, "E7.56.0.43", {"center": v(1831.49, -1105.2) * mm, "radius": 3.18 * mm});
            skCircle(sketch, "E7.58.0.43", {"center": v(1037.74, -1105.2) * mm, "radius": 3.18 * mm});
            skCircle(sketch, "E7.60.0.43", {"center": v(1545.74, -1105.2) * mm, "radius": 3.18 * mm});
            skCircle(sketch, "E7.62.0.43", {"center": v(1418.74, -1105.2) * mm, "radius": 3.18 * mm});
            skCircle(sketch, "E7.64.0.43", {"center": v(1005.99, -1105.2) * mm, "radius": 3.18 * mm});
            skCircle(sketch, "E7.66.0.43", {"center": v(1513.99, -1105.2) * mm, "radius": 3.18 * mm});
            skCircle(sketch, "E7.68.0.43", {"center": v(1799.74, -1105.2) * mm, "radius": 3.18 * mm});
            skCircle(sketch, "E7.70.0.43", {"center": v(1291.74, -1105.2) * mm, "radius": 3.18 * mm});
            skCircle(sketch, "E7.72.0.43", {"center": v(1132.99, -1105.2) * mm, "radius": 3.18 * mm});
            skCircle(sketch, "E7.74.0.43", {"center": v(974.24, -1105.2) * mm, "radius": 3.18 * mm});
            skCircle(sketch, "E7.76.0.43", {"center": v(1482.24, -1105.2) * mm, "radius": 3.18 * mm});
            skCircle(sketch, "E7.78.0.43", {"center": v(1259.99, -1105.2) * mm, "radius": 3.18 * mm});
            skCircle(sketch, "E7.80.0.43", {"center": v(1640.99, -1105.2) * mm, "radius": 3.18 * mm});
            skCircle(sketch, "E7.82.0.43", {"center": v(1767.99, -1105.2) * mm, "radius": 3.18 * mm});
            skCircle(sketch, "E7.84.0.43", {"center": v(1196.49, -1105.2) * mm, "radius": 3.18 * mm});
            skCircle(sketch, "E7.86.0.43", {"center": v(1704.49, -1105.2) * mm, "radius": 3.18 * mm});
            skCircle(sketch, "E7.88.0.43", {"center": v(720.24, -1105.2) * mm, "radius": 3.18 * mm});
            skCircle(sketch, "E7.90.0.43", {"center": v(942.49, -1105.2) * mm, "radius": 3.18 * mm});
            skCircle(sketch, "E7.92.0.43", {"center": v(878.99, -1105.2) * mm, "radius": 3.18 * mm});
            skCircle(sketch, "E7.94.0.43", {"center": v(434.49, -1105.2) * mm, "radius": 3.18 * mm});
            skCircle(sketch, "E7.96.0.43", {"center": v(656.74, -1105.2) * mm, "radius": 3.18 * mm});
            skCircle(sketch, "E7.98.0.43", {"center": v(370.99, -1105.2) * mm, "radius": 3.18 * mm});
            skCircle(sketch, "E7.100.0.43", {"center": v(593.24, -1105.2) * mm, "radius": 3.18 * mm});
            skCircle(sketch, "E7.102.0.43", {"center": v(847.24, -1105.2) * mm, "radius": 3.18 * mm});
            skCircle(sketch, "E7.104.0.43", {"center": v(339.24, -1105.2) * mm, "radius": 3.18 * mm});
            skCircle(sketch, "E7.106.0.43", {"center": v(561.49, -1105.2) * mm, "radius": 3.18 * mm});
            skCircle(sketch, "E7.108.0.43", {"center": v(815.49, -1105.2) * mm, "radius": 3.18 * mm});
            skCircle(sketch, "E7.110.0.43", {"center": v(307.49, -1105.2) * mm, "radius": 3.18 * mm});
            skCircle(sketch, "E7.112.0.43", {"center": v(529.74, -1105.2) * mm, "radius": 3.18 * mm});
            skCircle(sketch, "E7.114.0.43", {"center": v(180.49, -1105.2) * mm, "radius": 3.18 * mm});
            skCircle(sketch, "E7.116.0.43", {"center": v(148.74, -1105.2) * mm, "radius": 3.18 * mm});
            skCircle(sketch, "E7.118.0.43", {"center": v(910.74, -1105.2) * mm, "radius": 3.18 * mm});
            skCircle(sketch, "E7.120.0.43", {"center": v(275.74, -1105.2) * mm, "radius": 3.18 * mm});
            skCircle(sketch, "E7.122.0.43", {"center": v(243.99, -1105.2) * mm, "radius": 3.18 * mm});
            skCircle(sketch, "E7.124.0.43", {"center": v(212.24, -1105.2) * mm, "radius": 3.18 * mm});
            skCircle(sketch, "E7.126.0.43", {"center": v(783.74, -1105.2) * mm, "radius": 3.18 * mm});
            skCircle(sketch, "E7.128.0.43", {"center": v(497.99, -1105.2) * mm, "radius": 3.18 * mm});
            skCircle(sketch, "E7.130.0.43", {"center": v(402.74, -1105.2) * mm, "radius": 3.18 * mm});
            skCircle(sketch, "E7.132.0.43", {"center": v(624.99, -1105.2) * mm, "radius": 3.18 * mm});
            skCircle(sketch, "E7.134.0.43", {"center": v(751.99, -1105.2) * mm, "radius": 3.18 * mm});
            skCircle(sketch, "E7.136.0.43", {"center": v(466.24, -1105.2) * mm, "radius": 3.18 * mm});
            skCircle(sketch, "E7.138.0.43", {"center": v(688.49, -1105.2) * mm, "radius": 3.18 * mm});
            skCircle(sketch, "E7.140.0.43", {"center": v(116.99, -1105.2) * mm, "radius": 3.18 * mm});
            skCircle(sketch, "E7.142.0.43", {"center": v(85.24, -1105.2) * mm, "radius": 3.18 * mm});
            skCircle(sketch, "E7.144.0.43", {"center": v(53.49, -1105.2) * mm, "radius": 3.18 * mm});
            skLineSegment(sketch, "E7.146.0.43", {"start": v(-41.76, -1105.2) * mm, "end": v(-10.01, -1105.2) * mm, "construction": true});
            skCircle(sketch, "E7.149.0.43", {"center": v(21.74, -1105.2) * mm, "radius": 3.18 * mm});
            skCircle(sketch, "E7.151.0.43", {"center": v(-10.01, -1105.2) * mm, "radius": 3.18 * mm});
            skCircle(sketch, "E7.153.0.43", {"center": v(-41.76, -1105.2) * mm, "radius": 3.18 * mm});
            skCircle(sketch, "E7.0.0.44", {"center": v(2244.24, -1130.6) * mm, "radius": 3.18 * mm});
            skCircle(sketch, "E7.2.0.44", {"center": v(2180.74, -1130.6) * mm, "radius": 3.18 * mm});
            skCircle(sketch, "E7.4.0.44", {"center": v(2339.49, -1130.6) * mm, "radius": 3.18 * mm});
            skCircle(sketch, "E7.6.0.44", {"center": v(2307.74, -1130.6) * mm, "radius": 3.18 * mm});
            skCircle(sketch, "E7.8.0.44", {"center": v(2275.99, -1130.6) * mm, "radius": 3.18 * mm});
            skCircle(sketch, "E7.10.0.44", {"center": v(2212.49, -1130.6) * mm, "radius": 3.18 * mm});
            skCircle(sketch, "E7.12.0.44", {"center": v(1958.49, -1130.6) * mm, "radius": 3.18 * mm});
            skCircle(sketch, "E7.14.0.44", {"center": v(1894.99, -1130.6) * mm, "radius": 3.18 * mm});
            skCircle(sketch, "E7.16.0.44", {"center": v(2117.24, -1130.6) * mm, "radius": 3.18 * mm});
            skCircle(sketch, "E7.18.0.44", {"center": v(2085.49, -1130.6) * mm, "radius": 3.18 * mm});
            skCircle(sketch, "E7.20.0.44", {"center": v(2053.74, -1130.6) * mm, "radius": 3.18 * mm});
            skCircle(sketch, "E7.22.0.44", {"center": v(1926.74, -1130.6) * mm, "radius": 3.18 * mm});
            skCircle(sketch, "E7.24.0.44", {"center": v(2021.99, -1130.6) * mm, "radius": 3.18 * mm});
            skCircle(sketch, "E7.26.0.44", {"center": v(2148.99, -1130.6) * mm, "radius": 3.18 * mm});
            skCircle(sketch, "E7.28.0.44", {"center": v(1990.24, -1130.6) * mm, "radius": 3.18 * mm});
            skCircle(sketch, "E7.30.0.44", {"center": v(1450.49, -1130.6) * mm, "radius": 3.18 * mm});
            skCircle(sketch, "E7.32.0.44", {"center": v(1228.24, -1130.6) * mm, "radius": 3.18 * mm});
            skCircle(sketch, "E7.34.0.44", {"center": v(1736.24, -1130.6) * mm, "radius": 3.18 * mm});
            skCircle(sketch, "E7.36.0.44", {"center": v(1386.99, -1130.6) * mm, "radius": 3.18 * mm});
            skCircle(sketch, "E7.38.0.44", {"center": v(1164.74, -1130.6) * mm, "radius": 3.18 * mm});
            skCircle(sketch, "E7.40.0.44", {"center": v(1672.74, -1130.6) * mm, "radius": 3.18 * mm});
            skCircle(sketch, "E7.42.0.44", {"center": v(1101.24, -1130.6) * mm, "radius": 3.18 * mm});
            skCircle(sketch, "E7.44.0.44", {"center": v(1609.24, -1130.6) * mm, "radius": 3.18 * mm});
            skCircle(sketch, "E7.46.0.44", {"center": v(1355.24, -1130.6) * mm, "radius": 3.18 * mm});
            skCircle(sketch, "E7.48.0.44", {"center": v(1863.24, -1130.6) * mm, "radius": 3.18 * mm});
            skCircle(sketch, "E7.50.0.44", {"center": v(1069.49, -1130.6) * mm, "radius": 3.18 * mm});
            skCircle(sketch, "E7.52.0.44", {"center": v(1577.49, -1130.6) * mm, "radius": 3.18 * mm});
            skCircle(sketch, "E7.54.0.44", {"center": v(1323.49, -1130.6) * mm, "radius": 3.18 * mm});
            skCircle(sketch, "E7.56.0.44", {"center": v(1831.49, -1130.6) * mm, "radius": 3.18 * mm});
            skCircle(sketch, "E7.58.0.44", {"center": v(1037.74, -1130.6) * mm, "radius": 3.18 * mm});
            skCircle(sketch, "E7.60.0.44", {"center": v(1545.74, -1130.6) * mm, "radius": 3.18 * mm});
            skCircle(sketch, "E7.62.0.44", {"center": v(1418.74, -1130.6) * mm, "radius": 3.18 * mm});
            skCircle(sketch, "E7.64.0.44", {"center": v(1005.99, -1130.6) * mm, "radius": 3.18 * mm});
            skCircle(sketch, "E7.66.0.44", {"center": v(1513.99, -1130.6) * mm, "radius": 3.18 * mm});
            skCircle(sketch, "E7.68.0.44", {"center": v(1799.74, -1130.6) * mm, "radius": 3.18 * mm});
            skCircle(sketch, "E7.70.0.44", {"center": v(1291.74, -1130.6) * mm, "radius": 3.18 * mm});
            skCircle(sketch, "E7.72.0.44", {"center": v(1132.99, -1130.6) * mm, "radius": 3.18 * mm});
            skCircle(sketch, "E7.74.0.44", {"center": v(974.24, -1130.6) * mm, "radius": 3.18 * mm});
            skCircle(sketch, "E7.76.0.44", {"center": v(1482.24, -1130.6) * mm, "radius": 3.18 * mm});
            skCircle(sketch, "E7.78.0.44", {"center": v(1259.99, -1130.6) * mm, "radius": 3.18 * mm});
            skCircle(sketch, "E7.80.0.44", {"center": v(1640.99, -1130.6) * mm, "radius": 3.18 * mm});
            skCircle(sketch, "E7.82.0.44", {"center": v(1767.99, -1130.6) * mm, "radius": 3.18 * mm});
            skCircle(sketch, "E7.84.0.44", {"center": v(1196.49, -1130.6) * mm, "radius": 3.18 * mm});
            skCircle(sketch, "E7.86.0.44", {"center": v(1704.49, -1130.6) * mm, "radius": 3.18 * mm});
            skCircle(sketch, "E7.88.0.44", {"center": v(720.24, -1130.6) * mm, "radius": 3.18 * mm});
            skCircle(sketch, "E7.90.0.44", {"center": v(942.49, -1130.6) * mm, "radius": 3.18 * mm});
            skCircle(sketch, "E7.92.0.44", {"center": v(878.99, -1130.6) * mm, "radius": 3.18 * mm});
            skCircle(sketch, "E7.94.0.44", {"center": v(434.49, -1130.6) * mm, "radius": 3.18 * mm});
            skCircle(sketch, "E7.96.0.44", {"center": v(656.74, -1130.6) * mm, "radius": 3.18 * mm});
            skCircle(sketch, "E7.98.0.44", {"center": v(370.99, -1130.6) * mm, "radius": 3.18 * mm});
            skCircle(sketch, "E7.100.0.44", {"center": v(593.24, -1130.6) * mm, "radius": 3.18 * mm});
            skCircle(sketch, "E7.102.0.44", {"center": v(847.24, -1130.6) * mm, "radius": 3.18 * mm});
            skCircle(sketch, "E7.104.0.44", {"center": v(339.24, -1130.6) * mm, "radius": 3.18 * mm});
            skCircle(sketch, "E7.106.0.44", {"center": v(561.49, -1130.6) * mm, "radius": 3.18 * mm});
            skCircle(sketch, "E7.108.0.44", {"center": v(815.49, -1130.6) * mm, "radius": 3.18 * mm});
            skCircle(sketch, "E7.110.0.44", {"center": v(307.49, -1130.6) * mm, "radius": 3.18 * mm});
            skCircle(sketch, "E7.112.0.44", {"center": v(529.74, -1130.6) * mm, "radius": 3.18 * mm});
            skCircle(sketch, "E7.114.0.44", {"center": v(180.49, -1130.6) * mm, "radius": 3.18 * mm});
            skCircle(sketch, "E7.116.0.44", {"center": v(148.74, -1130.6) * mm, "radius": 3.18 * mm});
            skCircle(sketch, "E7.118.0.44", {"center": v(910.74, -1130.6) * mm, "radius": 3.18 * mm});
            skCircle(sketch, "E7.120.0.44", {"center": v(275.74, -1130.6) * mm, "radius": 3.18 * mm});
            skCircle(sketch, "E7.122.0.44", {"center": v(243.99, -1130.6) * mm, "radius": 3.18 * mm});
            skCircle(sketch, "E7.124.0.44", {"center": v(212.24, -1130.6) * mm, "radius": 3.18 * mm});
            skCircle(sketch, "E7.126.0.44", {"center": v(783.74, -1130.6) * mm, "radius": 3.18 * mm});
            skCircle(sketch, "E7.128.0.44", {"center": v(497.99, -1130.6) * mm, "radius": 3.18 * mm});
            skCircle(sketch, "E7.130.0.44", {"center": v(402.74, -1130.6) * mm, "radius": 3.18 * mm});
            skCircle(sketch, "E7.132.0.44", {"center": v(624.99, -1130.6) * mm, "radius": 3.18 * mm});
            skCircle(sketch, "E7.134.0.44", {"center": v(751.99, -1130.6) * mm, "radius": 3.18 * mm});
            skCircle(sketch, "E7.136.0.44", {"center": v(466.24, -1130.6) * mm, "radius": 3.18 * mm});
            skCircle(sketch, "E7.138.0.44", {"center": v(688.49, -1130.6) * mm, "radius": 3.18 * mm});
            skCircle(sketch, "E7.140.0.44", {"center": v(116.99, -1130.6) * mm, "radius": 3.18 * mm});
            skCircle(sketch, "E7.142.0.44", {"center": v(85.24, -1130.6) * mm, "radius": 3.18 * mm});
            skCircle(sketch, "E7.144.0.44", {"center": v(53.49, -1130.6) * mm, "radius": 3.18 * mm});
            skLineSegment(sketch, "E7.146.0.44", {"start": v(-41.76, -1130.6) * mm, "end": v(-10.01, -1130.6) * mm, "construction": true});
            skCircle(sketch, "E7.149.0.44", {"center": v(21.74, -1130.6) * mm, "radius": 3.18 * mm});
            skCircle(sketch, "E7.151.0.44", {"center": v(-10.01, -1130.6) * mm, "radius": 3.18 * mm});
            skCircle(sketch, "E7.153.0.44", {"center": v(-41.76, -1130.6) * mm, "radius": 3.18 * mm});
            skCircle(sketch, "E7.0.0.45", {"center": v(2244.24, -1156) * mm, "radius": 3.18 * mm});
            skCircle(sketch, "E7.2.0.45", {"center": v(2180.74, -1156) * mm, "radius": 3.18 * mm});
            skCircle(sketch, "E7.4.0.45", {"center": v(2339.49, -1156) * mm, "radius": 3.18 * mm});
            skCircle(sketch, "E7.6.0.45", {"center": v(2307.74, -1156) * mm, "radius": 3.18 * mm});
            skCircle(sketch, "E7.8.0.45", {"center": v(2275.99, -1156) * mm, "radius": 3.18 * mm});
            skCircle(sketch, "E7.10.0.45", {"center": v(2212.49, -1156) * mm, "radius": 3.18 * mm});
            skCircle(sketch, "E7.12.0.45", {"center": v(1958.49, -1156) * mm, "radius": 3.18 * mm});
            skCircle(sketch, "E7.14.0.45", {"center": v(1894.99, -1156) * mm, "radius": 3.18 * mm});
            skCircle(sketch, "E7.16.0.45", {"center": v(2117.24, -1156) * mm, "radius": 3.18 * mm});
            skCircle(sketch, "E7.18.0.45", {"center": v(2085.49, -1156) * mm, "radius": 3.18 * mm});
            skCircle(sketch, "E7.20.0.45", {"center": v(2053.74, -1156) * mm, "radius": 3.18 * mm});
            skCircle(sketch, "E7.22.0.45", {"center": v(1926.74, -1156) * mm, "radius": 3.18 * mm});
            skCircle(sketch, "E7.24.0.45", {"center": v(2021.99, -1156) * mm, "radius": 3.18 * mm});
            skCircle(sketch, "E7.26.0.45", {"center": v(2148.99, -1156) * mm, "radius": 3.18 * mm});
            skCircle(sketch, "E7.28.0.45", {"center": v(1990.24, -1156) * mm, "radius": 3.18 * mm});
            skCircle(sketch, "E7.30.0.45", {"center": v(1450.49, -1156) * mm, "radius": 3.18 * mm});
            skCircle(sketch, "E7.32.0.45", {"center": v(1228.24, -1156) * mm, "radius": 3.18 * mm});
            skCircle(sketch, "E7.34.0.45", {"center": v(1736.24, -1156) * mm, "radius": 3.18 * mm});
            skCircle(sketch, "E7.36.0.45", {"center": v(1386.99, -1156) * mm, "radius": 3.18 * mm});
            skCircle(sketch, "E7.38.0.45", {"center": v(1164.74, -1156) * mm, "radius": 3.18 * mm});
            skCircle(sketch, "E7.40.0.45", {"center": v(1672.74, -1156) * mm, "radius": 3.18 * mm});
            skCircle(sketch, "E7.42.0.45", {"center": v(1101.24, -1156) * mm, "radius": 3.18 * mm});
            skCircle(sketch, "E7.44.0.45", {"center": v(1609.24, -1156) * mm, "radius": 3.18 * mm});
            skCircle(sketch, "E7.46.0.45", {"center": v(1355.24, -1156) * mm, "radius": 3.18 * mm});
            skCircle(sketch, "E7.48.0.45", {"center": v(1863.24, -1156) * mm, "radius": 3.18 * mm});
            skCircle(sketch, "E7.50.0.45", {"center": v(1069.49, -1156) * mm, "radius": 3.18 * mm});
            skCircle(sketch, "E7.52.0.45", {"center": v(1577.49, -1156) * mm, "radius": 3.18 * mm});
            skCircle(sketch, "E7.54.0.45", {"center": v(1323.49, -1156) * mm, "radius": 3.18 * mm});
            skCircle(sketch, "E7.56.0.45", {"center": v(1831.49, -1156) * mm, "radius": 3.18 * mm});
            skCircle(sketch, "E7.58.0.45", {"center": v(1037.74, -1156) * mm, "radius": 3.18 * mm});
            skCircle(sketch, "E7.60.0.45", {"center": v(1545.74, -1156) * mm, "radius": 3.18 * mm});
            skCircle(sketch, "E7.62.0.45", {"center": v(1418.74, -1156) * mm, "radius": 3.18 * mm});
            skCircle(sketch, "E7.64.0.45", {"center": v(1005.99, -1156) * mm, "radius": 3.18 * mm});
            skCircle(sketch, "E7.66.0.45", {"center": v(1513.99, -1156) * mm, "radius": 3.18 * mm});
            skCircle(sketch, "E7.68.0.45", {"center": v(1799.74, -1156) * mm, "radius": 3.18 * mm});
            skCircle(sketch, "E7.70.0.45", {"center": v(1291.74, -1156) * mm, "radius": 3.18 * mm});
            skCircle(sketch, "E7.72.0.45", {"center": v(1132.99, -1156) * mm, "radius": 3.18 * mm});
            skCircle(sketch, "E7.74.0.45", {"center": v(974.24, -1156) * mm, "radius": 3.18 * mm});
            skCircle(sketch, "E7.76.0.45", {"center": v(1482.24, -1156) * mm, "radius": 3.18 * mm});
            skCircle(sketch, "E7.78.0.45", {"center": v(1259.99, -1156) * mm, "radius": 3.18 * mm});
            skCircle(sketch, "E7.80.0.45", {"center": v(1640.99, -1156) * mm, "radius": 3.18 * mm});
            skCircle(sketch, "E7.82.0.45", {"center": v(1767.99, -1156) * mm, "radius": 3.18 * mm});
            skCircle(sketch, "E7.84.0.45", {"center": v(1196.49, -1156) * mm, "radius": 3.18 * mm});
            skCircle(sketch, "E7.86.0.45", {"center": v(1704.49, -1156) * mm, "radius": 3.18 * mm});
            skCircle(sketch, "E7.88.0.45", {"center": v(720.24, -1156) * mm, "radius": 3.18 * mm});
            skCircle(sketch, "E7.90.0.45", {"center": v(942.49, -1156) * mm, "radius": 3.18 * mm});
            skCircle(sketch, "E7.92.0.45", {"center": v(878.99, -1156) * mm, "radius": 3.18 * mm});
            skCircle(sketch, "E7.94.0.45", {"center": v(434.49, -1156) * mm, "radius": 3.18 * mm});
            skCircle(sketch, "E7.96.0.45", {"center": v(656.74, -1156) * mm, "radius": 3.18 * mm});
            skCircle(sketch, "E7.98.0.45", {"center": v(370.99, -1156) * mm, "radius": 3.18 * mm});
            skCircle(sketch, "E7.100.0.45", {"center": v(593.24, -1156) * mm, "radius": 3.18 * mm});
            skCircle(sketch, "E7.102.0.45", {"center": v(847.24, -1156) * mm, "radius": 3.18 * mm});
            skCircle(sketch, "E7.104.0.45", {"center": v(339.24, -1156) * mm, "radius": 3.18 * mm});
            skCircle(sketch, "E7.106.0.45", {"center": v(561.49, -1156) * mm, "radius": 3.18 * mm});
            skCircle(sketch, "E7.108.0.45", {"center": v(815.49, -1156) * mm, "radius": 3.18 * mm});
            skCircle(sketch, "E7.110.0.45", {"center": v(307.49, -1156) * mm, "radius": 3.18 * mm});
            skCircle(sketch, "E7.112.0.45", {"center": v(529.74, -1156) * mm, "radius": 3.18 * mm});
            skCircle(sketch, "E7.114.0.45", {"center": v(180.49, -1156) * mm, "radius": 3.18 * mm});
            skCircle(sketch, "E7.116.0.45", {"center": v(148.74, -1156) * mm, "radius": 3.18 * mm});
            skCircle(sketch, "E7.118.0.45", {"center": v(910.74, -1156) * mm, "radius": 3.18 * mm});
            skCircle(sketch, "E7.120.0.45", {"center": v(275.74, -1156) * mm, "radius": 3.18 * mm});
            skCircle(sketch, "E7.122.0.45", {"center": v(243.99, -1156) * mm, "radius": 3.18 * mm});
            skCircle(sketch, "E7.124.0.45", {"center": v(212.24, -1156) * mm, "radius": 3.18 * mm});
            skCircle(sketch, "E7.126.0.45", {"center": v(783.74, -1156) * mm, "radius": 3.18 * mm});
            skCircle(sketch, "E7.128.0.45", {"center": v(497.99, -1156) * mm, "radius": 3.18 * mm});
            skCircle(sketch, "E7.130.0.45", {"center": v(402.74, -1156) * mm, "radius": 3.18 * mm});
            skCircle(sketch, "E7.132.0.45", {"center": v(624.99, -1156) * mm, "radius": 3.18 * mm});
            skCircle(sketch, "E7.134.0.45", {"center": v(751.99, -1156) * mm, "radius": 3.18 * mm});
            skCircle(sketch, "E7.136.0.45", {"center": v(466.24, -1156) * mm, "radius": 3.18 * mm});
            skCircle(sketch, "E7.138.0.45", {"center": v(688.49, -1156) * mm, "radius": 3.18 * mm});
            skCircle(sketch, "E7.140.0.45", {"center": v(116.99, -1156) * mm, "radius": 3.18 * mm});
            skCircle(sketch, "E7.142.0.45", {"center": v(85.24, -1156) * mm, "radius": 3.18 * mm});
            skCircle(sketch, "E7.144.0.45", {"center": v(53.49, -1156) * mm, "radius": 3.18 * mm});
            skLineSegment(sketch, "E7.146.0.45", {"start": v(-41.76, -1156) * mm, "end": v(-10.01, -1156) * mm, "construction": true});
            skCircle(sketch, "E7.149.0.45", {"center": v(21.74, -1156) * mm, "radius": 3.18 * mm});
            skCircle(sketch, "E7.151.0.45", {"center": v(-10.01, -1156) * mm, "radius": 3.18 * mm});
            skCircle(sketch, "E7.153.0.45", {"center": v(-41.76, -1156) * mm, "radius": 3.18 * mm});
            skCircle(sketch, "E8.0.0.46", {"center": v(2244.24, -1181.4) * mm, "radius": 3.18 * mm});
            skCircle(sketch, "E8.2.0.46", {"center": v(2180.74, -1181.4) * mm, "radius": 3.18 * mm});
            skCircle(sketch, "E8.4.0.46", {"center": v(2339.49, -1181.4) * mm, "radius": 3.18 * mm});
            skCircle(sketch, "E8.6.0.46", {"center": v(2307.74, -1181.4) * mm, "radius": 3.18 * mm});
            skCircle(sketch, "E8.8.0.46", {"center": v(2275.99, -1181.4) * mm, "radius": 3.18 * mm});
            skCircle(sketch, "E8.10.0.46", {"center": v(2212.49, -1181.4) * mm, "radius": 3.18 * mm});
            skCircle(sketch, "E8.12.0.46", {"center": v(1958.49, -1181.4) * mm, "radius": 3.18 * mm});
            skCircle(sketch, "E8.14.0.46", {"center": v(1894.99, -1181.4) * mm, "radius": 3.18 * mm});
            skCircle(sketch, "E8.16.0.46", {"center": v(2117.24, -1181.4) * mm, "radius": 3.18 * mm});
            skCircle(sketch, "E8.18.0.46", {"center": v(2085.49, -1181.4) * mm, "radius": 3.18 * mm});
            skCircle(sketch, "E8.20.0.46", {"center": v(2053.74, -1181.4) * mm, "radius": 3.18 * mm});
            skCircle(sketch, "E8.22.0.46", {"center": v(1926.74, -1181.4) * mm, "radius": 3.18 * mm});
            skCircle(sketch, "E8.24.0.46", {"center": v(2021.99, -1181.4) * mm, "radius": 3.18 * mm});
            skCircle(sketch, "E8.26.0.46", {"center": v(2148.99, -1181.4) * mm, "radius": 3.18 * mm});
            skCircle(sketch, "E8.28.0.46", {"center": v(1990.24, -1181.4) * mm, "radius": 3.18 * mm});
            skCircle(sketch, "E8.30.0.46", {"center": v(1450.49, -1181.4) * mm, "radius": 3.18 * mm});
            skCircle(sketch, "E8.32.0.46", {"center": v(1228.24, -1181.4) * mm, "radius": 3.18 * mm});
            skCircle(sketch, "E8.34.0.46", {"center": v(1736.24, -1181.4) * mm, "radius": 3.18 * mm});
            skCircle(sketch, "E8.36.0.46", {"center": v(1386.99, -1181.4) * mm, "radius": 3.18 * mm});
            skCircle(sketch, "E8.38.0.46", {"center": v(1164.74, -1181.4) * mm, "radius": 3.18 * mm});
            skCircle(sketch, "E8.40.0.46", {"center": v(1672.74, -1181.4) * mm, "radius": 3.18 * mm});
            skCircle(sketch, "E8.42.0.46", {"center": v(1101.24, -1181.4) * mm, "radius": 3.18 * mm});
            skCircle(sketch, "E8.44.0.46", {"center": v(1609.24, -1181.4) * mm, "radius": 3.18 * mm});
            skCircle(sketch, "E8.46.0.46", {"center": v(1355.24, -1181.4) * mm, "radius": 3.18 * mm});
            skCircle(sketch, "E8.48.0.46", {"center": v(1863.24, -1181.4) * mm, "radius": 3.18 * mm});
            skCircle(sketch, "E8.50.0.46", {"center": v(1069.49, -1181.4) * mm, "radius": 3.18 * mm});
            skCircle(sketch, "E8.52.0.46", {"center": v(1577.49, -1181.4) * mm, "radius": 3.18 * mm});
            skCircle(sketch, "E8.54.0.46", {"center": v(1323.49, -1181.4) * mm, "radius": 3.18 * mm});
            skCircle(sketch, "E8.56.0.46", {"center": v(1831.49, -1181.4) * mm, "radius": 3.18 * mm});
            skCircle(sketch, "E8.58.0.46", {"center": v(1037.74, -1181.4) * mm, "radius": 3.18 * mm});
            skCircle(sketch, "E8.60.0.46", {"center": v(1545.74, -1181.4) * mm, "radius": 3.18 * mm});
            skCircle(sketch, "E8.62.0.46", {"center": v(1418.74, -1181.4) * mm, "radius": 3.18 * mm});
            skCircle(sketch, "E8.64.0.46", {"center": v(1005.99, -1181.4) * mm, "radius": 3.18 * mm});
            skCircle(sketch, "E8.66.0.46", {"center": v(1513.99, -1181.4) * mm, "radius": 3.18 * mm});
            skCircle(sketch, "E8.68.0.46", {"center": v(1799.74, -1181.4) * mm, "radius": 3.18 * mm});
            skCircle(sketch, "E8.70.0.46", {"center": v(1291.74, -1181.4) * mm, "radius": 3.18 * mm});
            skCircle(sketch, "E8.72.0.46", {"center": v(1132.99, -1181.4) * mm, "radius": 3.18 * mm});
            skCircle(sketch, "E8.74.0.46", {"center": v(974.24, -1181.4) * mm, "radius": 3.18 * mm});
            skCircle(sketch, "E8.76.0.46", {"center": v(1482.24, -1181.4) * mm, "radius": 3.18 * mm});
            skCircle(sketch, "E8.78.0.46", {"center": v(1259.99, -1181.4) * mm, "radius": 3.18 * mm});
            skCircle(sketch, "E8.80.0.46", {"center": v(1640.99, -1181.4) * mm, "radius": 3.18 * mm});
            skCircle(sketch, "E8.82.0.46", {"center": v(1767.99, -1181.4) * mm, "radius": 3.18 * mm});
            skCircle(sketch, "E8.84.0.46", {"center": v(1196.49, -1181.4) * mm, "radius": 3.18 * mm});
            skCircle(sketch, "E8.86.0.46", {"center": v(1704.49, -1181.4) * mm, "radius": 3.18 * mm});
            skCircle(sketch, "E8.88.0.46", {"center": v(720.24, -1181.4) * mm, "radius": 3.18 * mm});
            skCircle(sketch, "E8.90.0.46", {"center": v(942.49, -1181.4) * mm, "radius": 3.18 * mm});
            skCircle(sketch, "E8.92.0.46", {"center": v(878.99, -1181.4) * mm, "radius": 3.18 * mm});
            skCircle(sketch, "E8.94.0.46", {"center": v(434.49, -1181.4) * mm, "radius": 3.18 * mm});
            skCircle(sketch, "E8.96.0.46", {"center": v(656.74, -1181.4) * mm, "radius": 3.18 * mm});
            skCircle(sketch, "E8.98.0.46", {"center": v(370.99, -1181.4) * mm, "radius": 3.18 * mm});
            skCircle(sketch, "E8.100.0.46", {"center": v(593.24, -1181.4) * mm, "radius": 3.18 * mm});
            skCircle(sketch, "E8.102.0.46", {"center": v(847.24, -1181.4) * mm, "radius": 3.18 * mm});
            skCircle(sketch, "E8.104.0.46", {"center": v(339.24, -1181.4) * mm, "radius": 3.18 * mm});
            skCircle(sketch, "E8.106.0.46", {"center": v(561.49, -1181.4) * mm, "radius": 3.18 * mm});
            skCircle(sketch, "E8.108.0.46", {"center": v(815.49, -1181.4) * mm, "radius": 3.18 * mm});
            skCircle(sketch, "E8.110.0.46", {"center": v(307.49, -1181.4) * mm, "radius": 3.18 * mm});
            skCircle(sketch, "E8.112.0.46", {"center": v(529.74, -1181.4) * mm, "radius": 3.18 * mm});
            skCircle(sketch, "E8.114.0.46", {"center": v(180.49, -1181.4) * mm, "radius": 3.18 * mm});
            skCircle(sketch, "E8.116.0.46", {"center": v(148.74, -1181.4) * mm, "radius": 3.18 * mm});
            skCircle(sketch, "E8.118.0.46", {"center": v(910.74, -1181.4) * mm, "radius": 3.18 * mm});
            skCircle(sketch, "E8.120.0.46", {"center": v(275.74, -1181.4) * mm, "radius": 3.18 * mm});
            skCircle(sketch, "E8.122.0.46", {"center": v(243.99, -1181.4) * mm, "radius": 3.18 * mm});
            skCircle(sketch, "E8.124.0.46", {"center": v(212.24, -1181.4) * mm, "radius": 3.18 * mm});
            skCircle(sketch, "E8.126.0.46", {"center": v(783.74, -1181.4) * mm, "radius": 3.18 * mm});
            skCircle(sketch, "E8.128.0.46", {"center": v(497.99, -1181.4) * mm, "radius": 3.18 * mm});
            skCircle(sketch, "E8.130.0.46", {"center": v(402.74, -1181.4) * mm, "radius": 3.18 * mm});
            skCircle(sketch, "E8.132.0.46", {"center": v(624.99, -1181.4) * mm, "radius": 3.18 * mm});
            skCircle(sketch, "E8.134.0.46", {"center": v(751.99, -1181.4) * mm, "radius": 3.18 * mm});
            skCircle(sketch, "E8.136.0.46", {"center": v(466.24, -1181.4) * mm, "radius": 3.18 * mm});
            skCircle(sketch, "E8.138.0.46", {"center": v(688.49, -1181.4) * mm, "radius": 3.18 * mm});
            skCircle(sketch, "E8.140.0.46", {"center": v(116.99, -1181.4) * mm, "radius": 3.18 * mm});
            skCircle(sketch, "E8.142.0.46", {"center": v(85.24, -1181.4) * mm, "radius": 3.18 * mm});
            skCircle(sketch, "E8.144.0.46", {"center": v(53.49, -1181.4) * mm, "radius": 3.18 * mm});
            skLineSegment(sketch, "E8.146.0.46", {"start": v(-41.76, -1181.4) * mm, "end": v(-10.01, -1181.4) * mm, "construction": true});
            skCircle(sketch, "E8.149.0.46", {"center": v(21.74, -1181.4) * mm, "radius": 3.18 * mm});
            skCircle(sketch, "E8.151.0.46", {"center": v(-10.01, -1181.4) * mm, "radius": 3.18 * mm});
            skCircle(sketch, "E8.153.0.46", {"center": v(-41.76, -1181.4) * mm, "radius": 3.18 * mm});
            skSolve(sketch);
        }
        {
            var Q0;
            Q0=makeQuery(id+"F0.imprint","IMPRINT",FACE,{"disambiguationData":[TD([[makeQuery(id+"F0.imprint","IMPRINT",EDGE,{"derivedFrom":sQuery(id+"F0.wireOp",EDGE,"E0.bottom")}),-1.0]])]});
            extrude(context, id + "F1", {"entities" : qUnion([Q0]), "depth" : 25.4 * mm});
        }
    });
